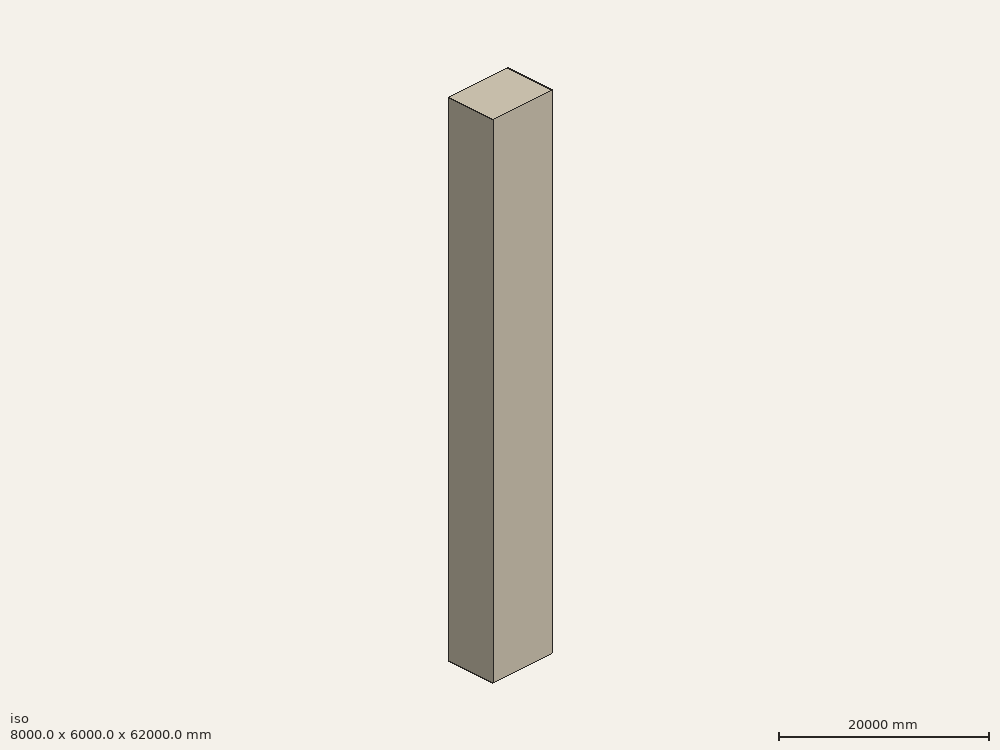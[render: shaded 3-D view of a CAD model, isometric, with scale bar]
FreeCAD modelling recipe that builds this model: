
FCSTD DOCUMENT  (FreeCAD 0.19R24276 (Git))
Label: Tower_Plant
License: All rights reserved
LicenseURL: http://en.wikipedia.org/wiki/All_rights_reserved
objects: Part::Line×1566, Part::Feature×523, Part::Plane×1, Part::Box×1
note: 2091 computed .brp shape members not serialized (recipe doc carries the construction recipe); baked Part::Feature solids carry a one-line shape summary decoded from their .brp

FEATURE [Part::Feature] Heliostat_1  label="Heliostat_1(Mirror,Axis_1_1,Axis_2_1,Normal_1,Target_point)"
  Placement = pos=(-239680,-638881,4.06356e-10) rot=(0,0,1;0rad)
  shape: bbox 10000 x 21.41 x 10000 mm, 1 faces, 0 solids (baked)
FEATURE [Part::Line] Normal_1
  AttacherType = Attacher::AttachEngine3D
  X1 = -239680
  X2 = -239680
  Y1 = 528703
  Y2 = 527703
  Z1 = 0
  Z2 = 0
FEATURE [Part::Line] Axis_1_1
  AttacherType = Attacher::AttachEngine3D
  X1 = -239680
  X2 = -239680
  Y1 = 528703
  Y2 = 528703
  Z1 = 0
  Z2 = -1000
FEATURE [Part::Line] Axis_2_1
  AttacherType = Attacher::AttachEngine3D
  X1 = -239680
  X2 = -240680
  Y1 = 528703
  Y2 = 528703
  Z1 = 0
  Z2 = 0
FEATURE [Part::Feature] Heliostat_2  label="Heliostat_2(Mirror,Axis_1_2,Axis_2_2,Normal_2,Target_point)"
  Placement = pos=(281709,-660028,4.06356e-10) rot=(0,0,1;0rad)
  shape: bbox 10000 x 21.41 x 10000 mm, 1 faces, 0 solids (baked)
FEATURE [Part::Line] Normal_2
  AttacherType = Attacher::AttachEngine3D
  X1 = 281709
  X2 = 281709
  Y1 = 507557
  Y2 = 506557
  Z1 = 0
  Z2 = 0
FEATURE [Part::Line] Axis_1_2
  AttacherType = Attacher::AttachEngine3D
  X1 = 281709
  X2 = 281709
  Y1 = 507557
  Y2 = 507557
  Z1 = 0
  Z2 = -1000
FEATURE [Part::Line] Axis_2_2
  AttacherType = Attacher::AttachEngine3D
  X1 = 281709
  X2 = 280709
  Y1 = 507557
  Y2 = 507557
  Z1 = 0
  Z2 = 0
FEATURE [Part::Feature] Heliostat_3  label="Heliostat_3(Mirror,Axis_1_3,Axis_2_3,Normal_3,Target_point)"
  Placement = pos=(-281709,-660028,4.06356e-10) rot=(0,0,1;0rad)
  shape: bbox 10000 x 21.41 x 10000 mm, 1 faces, 0 solids (baked)
FEATURE [Part::Line] Normal_3
  AttacherType = Attacher::AttachEngine3D
  X1 = -281709
  X2 = -281709
  Y1 = 507557
  Y2 = 506557
  Z1 = 0
  Z2 = 0
FEATURE [Part::Line] Axis_1_3
  AttacherType = Attacher::AttachEngine3D
  X1 = -281709
  X2 = -281709
  Y1 = 507557
  Y2 = 507557
  Z1 = 0
  Z2 = -1000
FEATURE [Part::Line] Axis_2_3
  AttacherType = Attacher::AttachEngine3D
  X1 = -281709
  X2 = -282709
  Y1 = 507557
  Y2 = 507557
  Z1 = 0
  Z2 = 0
FEATURE [Part::Feature] Heliostat_4  label="Heliostat_4(Mirror,Axis_1_4,Axis_2_4,Normal_4,Target_point)"
  Placement = pos=(324319,-653058,2.9829e-10) rot=(0,0,1;0rad)
  shape: bbox 10000 x 23.13 x 10000 mm, 1 faces, 0 solids (baked)
FEATURE [Part::Line] Normal_4
  AttacherType = Attacher::AttachEngine3D
  X1 = 324319
  X2 = 324319
  Y1 = 427889
  Y2 = 426889
  Z1 = 0
  Z2 = 0
FEATURE [Part::Line] Axis_1_4
  AttacherType = Attacher::AttachEngine3D
  X1 = 324319
  X2 = 324319
  Y1 = 427889
  Y2 = 427889
  Z1 = 0
  Z2 = -1000
FEATURE [Part::Line] Axis_2_4
  AttacherType = Attacher::AttachEngine3D
  X1 = 324319
  X2 = 323319
  Y1 = 427889
  Y2 = 427889
  Z1 = 0
  Z2 = 0
FEATURE [Part::Feature] Heliostat_5  label="Heliostat_5(Mirror,Axis_1_5,Axis_2_5,Normal_5,Target_point)"
  Placement = pos=(-324319,-653058,2.9829e-10) rot=(0,0,1;0rad)
  shape: bbox 10000 x 23.13 x 10000 mm, 1 faces, 0 solids (baked)
FEATURE [Part::Line] Normal_5
  AttacherType = Attacher::AttachEngine3D
  X1 = -324319
  X2 = -324319
  Y1 = 427889
  Y2 = 426889
  Z1 = 0
  Z2 = 0
FEATURE [Part::Line] Axis_1_5
  AttacherType = Attacher::AttachEngine3D
  X1 = -324319
  X2 = -324319
  Y1 = 427889
  Y2 = 427889
  Z1 = 0
  Z2 = -1000
FEATURE [Part::Line] Axis_2_5
  AttacherType = Attacher::AttachEngine3D
  X1 = -324319
  X2 = -325319
  Y1 = 427889
  Y2 = 427889
  Z1 = 0
  Z2 = 0
FEATURE [Part::Feature] Heliostat_6  label="Heliostat_6(Mirror,Axis_1_6,Axis_2_6,Normal_6,Target_point)"
  Placement = pos=(328411,-579165,4.3478e-11) rot=(0,0,1;0rad)
  shape: bbox 10000 x 31.86 x 10000 mm, 1 faces, 0 solids (baked)
FEATURE [Part::Line] Normal_6
  AttacherType = Attacher::AttachEngine3D
  X1 = 328411
  X2 = 328411
  Y1 = 205551
  Y2 = 204551
  Z1 = 0
  Z2 = 0
FEATURE [Part::Line] Axis_1_6
  AttacherType = Attacher::AttachEngine3D
  X1 = 328411
  X2 = 328411
  Y1 = 205551
  Y2 = 205551
  Z1 = 0
  Z2 = -1000
FEATURE [Part::Line] Axis_2_6
  AttacherType = Attacher::AttachEngine3D
  X1 = 328411
  X2 = 327411
  Y1 = 205551
  Y2 = 205551
  Z1 = 0
  Z2 = 0
FEATURE [Part::Feature] Heliostat_7  label="Heliostat_7(Mirror,Axis_1_7,Axis_2_7,Normal_7,Target_point)"
  Placement = pos=(-328411,-579165,4.3478e-11) rot=(0,0,1;0rad)
  shape: bbox 10000 x 31.86 x 10000 mm, 1 faces, 0 solids (baked)
FEATURE [Part::Line] Normal_7
  AttacherType = Attacher::AttachEngine3D
  X1 = -328411
  X2 = -328411
  Y1 = 205551
  Y2 = 204551
  Z1 = 0
  Z2 = 0
FEATURE [Part::Line] Axis_1_7
  AttacherType = Attacher::AttachEngine3D
  X1 = -328411
  X2 = -328411
  Y1 = 205551
  Y2 = 205551
  Z1 = 0
  Z2 = -1000
FEATURE [Part::Line] Axis_2_7
  AttacherType = Attacher::AttachEngine3D
  X1 = -328411
  X2 = -329411
  Y1 = 205551
  Y2 = 205551
  Z1 = 0
  Z2 = 0
FEATURE [Part::Feature] Heliostat_8  label="Heliostat_8(Mirror,Axis_1_8,Axis_2_8,Normal_8,Target_point)"
  Placement = pos=(180161,-344791,1.40591e-10) rot=(0,0,1;0rad)
  shape: bbox 10000 x 47.5 x 10000 mm, 1 faces, 0 solids (baked)
FEATURE [Part::Line] Normal_8
  AttacherType = Attacher::AttachEngine3D
  X1 = 180161
  X2 = 180161
  Y1 = 181556
  Y2 = 180556
  Z1 = 0
  Z2 = 0
FEATURE [Part::Line] Axis_1_8
  AttacherType = Attacher::AttachEngine3D
  X1 = 180161
  X2 = 180161
  Y1 = 181556
  Y2 = 181556
  Z1 = 0
  Z2 = -1000
FEATURE [Part::Line] Axis_2_8
  AttacherType = Attacher::AttachEngine3D
  X1 = 180161
  X2 = 179161
  Y1 = 181556
  Y2 = 181556
  Z1 = 0
  Z2 = 0
FEATURE [Part::Feature] Heliostat_9  label="Heliostat_9(Mirror,Axis_1_9,Axis_2_9,Normal_9,Target_point)"
  Placement = pos=(-180161,-344791,1.40591e-10) rot=(0,0,1;0rad)
  shape: bbox 10000 x 47.5 x 10000 mm, 1 faces, 0 solids (baked)
FEATURE [Part::Line] Normal_9
  AttacherType = Attacher::AttachEngine3D
  X1 = -180161
  X2 = -180161
  Y1 = 181556
  Y2 = 180556
  Z1 = 0
  Z2 = 0
FEATURE [Part::Line] Axis_1_9
  AttacherType = Attacher::AttachEngine3D
  X1 = -180161
  X2 = -180161
  Y1 = 181556
  Y2 = 181556
  Z1 = 0
  Z2 = -1000
FEATURE [Part::Line] Axis_2_9
  AttacherType = Attacher::AttachEngine3D
  X1 = -180161
  X2 = -181161
  Y1 = 181556
  Y2 = 181556
  Z1 = 0
  Z2 = 0
FEATURE [Part::Feature] Heliostat_10  label="Heliostat_10(Mirror,Axis_1_10,Axis_2_10,Normal_10,Target_point)"
  Placement = pos=(335249,-595803,2.1959e-10) rot=(0,0,1;0rad)
  shape: bbox 10000 x 29.51 x 10000 mm, 1 faces, 0 solids (baked)
FEATURE [Part::Line] Normal_10
  AttacherType = Attacher::AttachEngine3D
  X1 = 335249
  X2 = 335249
  Y1 = 251457
  Y2 = 250457
  Z1 = 0
  Z2 = 0
FEATURE [Part::Line] Axis_1_10
  AttacherType = Attacher::AttachEngine3D
  X1 = 335249
  X2 = 335249
  Y1 = 251457
  Y2 = 251457
  Z1 = 0
  Z2 = -1000
FEATURE [Part::Line] Axis_2_10
  AttacherType = Attacher::AttachEngine3D
  X1 = 335249
  X2 = 334249
  Y1 = 251457
  Y2 = 251457
  Z1 = 0
  Z2 = 0
FEATURE [Part::Feature] Heliostat_11  label="Heliostat_11(Mirror,Axis_1_11,Axis_2_11,Normal_11,Target_point)"
  Placement = pos=(-335249,-595803,2.1959e-10) rot=(0,0,1;0rad)
  shape: bbox 10000 x 29.51 x 10000 mm, 1 faces, 0 solids (baked)
FEATURE [Part::Line] Normal_11
  AttacherType = Attacher::AttachEngine3D
  X1 = -335249
  X2 = -335249
  Y1 = 251457
  Y2 = 250457
  Z1 = 0
  Z2 = 0
FEATURE [Part::Line] Axis_1_11
  AttacherType = Attacher::AttachEngine3D
  X1 = -335249
  X2 = -335249
  Y1 = 251457
  Y2 = 251457
  Z1 = 0
  Z2 = -1000
FEATURE [Part::Line] Axis_2_11
  AttacherType = Attacher::AttachEngine3D
  X1 = -335249
  X2 = -336249
  Y1 = 251457
  Y2 = 251457
  Z1 = 0
  Z2 = 0
FEATURE [Part::Feature] Heliostat_12  label="Heliostat_12(Mirror,Axis_1_12,Axis_2_12,Normal_12,Target_point)"
  Placement = pos=(-340605,-617288,8.39512e-11) rot=(0,0,1;0rad)
  shape: bbox 10000 x 27.15 x 10000 mm, 1 faces, 0 solids (baked)
FEATURE [Part::Line] Normal_12
  AttacherType = Attacher::AttachEngine3D
  X1 = -340605
  X2 = -340605
  Y1 = 303489
  Y2 = 302489
  Z1 = 0
  Z2 = 0
FEATURE [Part::Line] Axis_1_12
  AttacherType = Attacher::AttachEngine3D
  X1 = -340605
  X2 = -340605
  Y1 = 303489
  Y2 = 303489
  Z1 = 0
  Z2 = -1000
FEATURE [Part::Line] Axis_2_12
  AttacherType = Attacher::AttachEngine3D
  X1 = -340605
  X2 = -341605
  Y1 = 303489
  Y2 = 303489
  Z1 = 0
  Z2 = 0
FEATURE [Part::Feature] Heliostat_13  label="Heliostat_13(Mirror,Axis_1_13,Axis_2_13,Normal_13,Target_point)"
  Placement = pos=(340605,-617288,8.39512e-11) rot=(0,0,1;0rad)
  shape: bbox 10000 x 27.15 x 10000 mm, 1 faces, 0 solids (baked)
FEATURE [Part::Line] Normal_13
  AttacherType = Attacher::AttachEngine3D
  X1 = 340605
  X2 = 340605
  Y1 = 303489
  Y2 = 302489
  Z1 = 0
  Z2 = 0
FEATURE [Part::Line] Axis_1_13
  AttacherType = Attacher::AttachEngine3D
  X1 = 340605
  X2 = 340605
  Y1 = 303489
  Y2 = 303489
  Z1 = 0
  Z2 = -1000
FEATURE [Part::Line] Axis_2_13
  AttacherType = Attacher::AttachEngine3D
  X1 = 340605
  X2 = 339605
  Y1 = 303489
  Y2 = 303489
  Z1 = 0
  Z2 = 0
FEATURE [Part::Feature] Heliostat_14  label="Heliostat_14(Mirror,Axis_1_14,Axis_2_14,Normal_14,Target_point)"
  Placement = pos=(288602,-628199,2.94608e-10) rot=(0,0,1;0rad)
  shape: bbox 10000 x 23.13 x 10000 mm, 1 faces, 0 solids (baked)
FEATURE [Part::Line] Normal_14
  AttacherType = Attacher::AttachEngine3D
  X1 = 288602
  X2 = 288602
  Y1 = 452748
  Y2 = 451748
  Z1 = 0
  Z2 = 0
FEATURE [Part::Line] Axis_1_14
  AttacherType = Attacher::AttachEngine3D
  X1 = 288602
  X2 = 288602
  Y1 = 452748
  Y2 = 452748
  Z1 = 0
  Z2 = -1000
FEATURE [Part::Line] Axis_2_14
  AttacherType = Attacher::AttachEngine3D
  X1 = 288602
  X2 = 287602
  Y1 = 452748
  Y2 = 452748
  Z1 = 0
  Z2 = 0
FEATURE [Part::Feature] Heliostat_15  label="Heliostat_15(Mirror,Axis_1_15,Axis_2_15,Normal_15,Target_point)"
  Placement = pos=(-288602,-628199,2.94608e-10) rot=(0,0,1;0rad)
  shape: bbox 10000 x 23.13 x 10000 mm, 1 faces, 0 solids (baked)
FEATURE [Part::Line] Normal_15
  AttacherType = Attacher::AttachEngine3D
  X1 = -288602
  X2 = -288602
  Y1 = 452748
  Y2 = 451748
  Z1 = 0
  Z2 = 0
FEATURE [Part::Line] Axis_1_15
  AttacherType = Attacher::AttachEngine3D
  X1 = -288602
  X2 = -288602
  Y1 = 452748
  Y2 = 452748
  Z1 = 0
  Z2 = -1000
FEATURE [Part::Line] Axis_2_15
  AttacherType = Attacher::AttachEngine3D
  X1 = -288602
  X2 = -289602
  Y1 = 452748
  Y2 = 452748
  Z1 = 0
  Z2 = 0
FEATURE [Part::Feature] Heliostat_16  label="Heliostat_16(Mirror,Axis_1_16,Axis_2_16,Normal_16,Target_point)"
  Placement = pos=(306713,-640267,1.85804e-10) rot=(0,0,1;0rad)
  shape: bbox 10000 x 23.13 x 10000 mm, 1 faces, 0 solids (baked)
FEATURE [Part::Line] Normal_16
  AttacherType = Attacher::AttachEngine3D
  X1 = 306713
  X2 = 306713
  Y1 = 440680
  Y2 = 439680
  Z1 = 0
  Z2 = 0
FEATURE [Part::Line] Axis_1_16
  AttacherType = Attacher::AttachEngine3D
  X1 = 306713
  X2 = 306713
  Y1 = 440680
  Y2 = 440680
  Z1 = 0
  Z2 = -1000
FEATURE [Part::Line] Axis_2_16
  AttacherType = Attacher::AttachEngine3D
  X1 = 306713
  X2 = 305713
  Y1 = 440680
  Y2 = 440680
  Z1 = 0
  Z2 = 0
FEATURE [Part::Feature] Heliostat_17  label="Heliostat_17(Mirror,Axis_1_17,Axis_2_17,Normal_17,Target_point)"
  Placement = pos=(-306713,-640267,1.85804e-10) rot=(0,0,1;0rad)
  shape: bbox 10000 x 23.13 x 10000 mm, 1 faces, 0 solids (baked)
FEATURE [Part::Line] Normal_17
  AttacherType = Attacher::AttachEngine3D
  X1 = -306713
  X2 = -306713
  Y1 = 440680
  Y2 = 439680
  Z1 = 0
  Z2 = 0
FEATURE [Part::Line] Axis_1_17
  AttacherType = Attacher::AttachEngine3D
  X1 = -306713
  X2 = -306713
  Y1 = 440680
  Y2 = 440680
  Z1 = 0
  Z2 = -1000
FEATURE [Part::Line] Axis_2_17
  AttacherType = Attacher::AttachEngine3D
  X1 = -306713
  X2 = -307713
  Y1 = 440680
  Y2 = 440680
  Z1 = 0
  Z2 = 0
FEATURE [Part::Feature] Heliostat_18  label="Heliostat_18(Mirror,Axis_1_18,Axis_2_18,Normal_18,Target_point)"
  Placement = pos=(321332,-620083,1.82429e-10) rot=(0,0,1;0rad)
  shape: bbox 10000 x 25.14 x 10000 mm, 1 faces, 0 solids (baked)
FEATURE [Part::Line] Normal_18
  AttacherType = Attacher::AttachEngine3D
  X1 = 321332
  X2 = 321332
  Y1 = 374320
  Y2 = 373320
  Z1 = 0
  Z2 = 0
FEATURE [Part::Line] Axis_1_18
  AttacherType = Attacher::AttachEngine3D
  X1 = 321332
  X2 = 321332
  Y1 = 374320
  Y2 = 374320
  Z1 = 0
  Z2 = -1000
FEATURE [Part::Line] Axis_2_18
  AttacherType = Attacher::AttachEngine3D
  X1 = 321332
  X2 = 320332
  Y1 = 374320
  Y2 = 374320
  Z1 = 0
  Z2 = 0
FEATURE [Part::Feature] Heliostat_19  label="Heliostat_19(Mirror,Axis_1_19,Axis_2_19,Normal_19,Target_point)"
  Placement = pos=(-321332,-620083,1.82429e-10) rot=(0,0,1;0rad)
  shape: bbox 10000 x 25.14 x 10000 mm, 1 faces, 0 solids (baked)
FEATURE [Part::Line] Normal_19
  AttacherType = Attacher::AttachEngine3D
  X1 = -321332
  X2 = -321332
  Y1 = 374320
  Y2 = 373320
  Z1 = 0
  Z2 = 0
FEATURE [Part::Line] Axis_1_19
  AttacherType = Attacher::AttachEngine3D
  X1 = -321332
  X2 = -321332
  Y1 = 374320
  Y2 = 374320
  Z1 = 0
  Z2 = -1000
FEATURE [Part::Line] Axis_2_19
  AttacherType = Attacher::AttachEngine3D
  X1 = -321332
  X2 = -322332
  Y1 = 374320
  Y2 = 374320
  Z1 = 0
  Z2 = 0
FEATURE [Part::Feature] Heliostat_20  label="Heliostat_20(Mirror,Axis_1_20,Axis_2_20,Normal_20,Target_point)"
  Placement = pos=(59685.6,-162676,1.04186e-11) rot=(0,0,1;0rad)
  shape: bbox 10000 x 144.2 x 10000 mm, 1 faces, 0 solids (baked)
FEATURE [Part::Line] Normal_20
  AttacherType = Attacher::AttachEngine3D
  X1 = 59685.6
  X2 = 59685.6
  Y1 = 10728.3
  Y2 = 9728.32
  Z1 = 0
  Z2 = 0
FEATURE [Part::Line] Axis_1_20
  AttacherType = Attacher::AttachEngine3D
  X1 = 59685.6
  X2 = 59685.6
  Y1 = 10728.3
  Y2 = 10728.3
  Z1 = 0
  Z2 = -1000
FEATURE [Part::Line] Axis_2_20
  AttacherType = Attacher::AttachEngine3D
  X1 = 59685.6
  X2 = 58685.6
  Y1 = 10728.3
  Y2 = 10728.3
  Z1 = 0
  Z2 = 0
FEATURE [Part::Feature] Heliostat_21  label="Heliostat_21(Mirror,Axis_1_21,Axis_2_21,Normal_21,Target_point)"
  Placement = pos=(-59685.6,-162676,1.04186e-11) rot=(0,0,1;0rad)
  shape: bbox 10000 x 144.2 x 10000 mm, 1 faces, 0 solids (baked)
FEATURE [Part::Line] Normal_21
  AttacherType = Attacher::AttachEngine3D
  X1 = -59685.6
  X2 = -59685.6
  Y1 = 10728.3
  Y2 = 9728.32
  Z1 = 0
  Z2 = 0
FEATURE [Part::Line] Axis_1_21
  AttacherType = Attacher::AttachEngine3D
  X1 = -59685.6
  X2 = -59685.6
  Y1 = 10728.3
  Y2 = 10728.3
  Z1 = 0
  Z2 = -1000
FEATURE [Part::Line] Axis_2_21
  AttacherType = Attacher::AttachEngine3D
  X1 = -59685.6
  X2 = -60685.6
  Y1 = 10728.3
  Y2 = 10728.3
  Z1 = 0
  Z2 = 0
FEATURE [Part::Feature] Heliostat_22  label="Heliostat_22(Mirror,Axis_1_22,Axis_2_22,Normal_22,Target_point)"
  Placement = pos=(220290,-403255,4.94649e-11) rot=(0,0,1;0rad)
  shape: bbox 10000 x 51.21 x 10000 mm, 1 faces, 0 solids (baked)
FEATURE [Part::Line] Normal_22
  AttacherType = Attacher::AttachEngine3D
  X1 = 220290
  X2 = 220290
  Y1 = 84926.1
  Y2 = 83926.1
  Z1 = 0
  Z2 = 0
FEATURE [Part::Line] Axis_1_22
  AttacherType = Attacher::AttachEngine3D
  X1 = 220290
  X2 = 220290
  Y1 = 84926.1
  Y2 = 84926.1
  Z1 = 0
  Z2 = -1000
FEATURE [Part::Line] Axis_2_22
  AttacherType = Attacher::AttachEngine3D
  X1 = 220290
  X2 = 219290
  Y1 = 84926.1
  Y2 = 84926.1
  Z1 = 0
  Z2 = 0
FEATURE [Part::Feature] Heliostat_23  label="Heliostat_23(Mirror,Axis_1_23,Axis_2_23,Normal_23,Target_point)"
  Placement = pos=(-220290,-403255,4.94649e-11) rot=(0,0,1;0rad)
  shape: bbox 10000 x 51.21 x 10000 mm, 1 faces, 0 solids (baked)
FEATURE [Part::Line] Normal_23
  AttacherType = Attacher::AttachEngine3D
  X1 = -220290
  X2 = -220290
  Y1 = 84926.1
  Y2 = 83926.1
  Z1 = 0
  Z2 = 0
FEATURE [Part::Line] Axis_1_23
  AttacherType = Attacher::AttachEngine3D
  X1 = -220290
  X2 = -220290
  Y1 = 84926.1
  Y2 = 84926.1
  Z1 = 0
  Z2 = -1000
FEATURE [Part::Line] Axis_2_23
  AttacherType = Attacher::AttachEngine3D
  X1 = -220290
  X2 = -221290
  Y1 = 84926.1
  Y2 = 84926.1
  Z1 = 0
  Z2 = 0
FEATURE [Part::Feature] Heliostat_24  label="Heliostat_24(Mirror,Axis_1_24,Axis_2_24,Normal_24,Target_point)"
  Placement = pos=(244770,-464081,1.33122e-10) rot=(0,0,1;0rad)
  shape: bbox 10000 x 34.61 x 10000 mm, 1 faces, 0 solids (baked)
FEATURE [Part::Line] Normal_24
  AttacherType = Attacher::AttachEngine3D
  X1 = 244770
  X2 = 244770
  Y1 = 258220
  Y2 = 257220
  Z1 = 0
  Z2 = 0
FEATURE [Part::Line] Axis_1_24
  AttacherType = Attacher::AttachEngine3D
  X1 = 244770
  X2 = 244770
  Y1 = 258220
  Y2 = 258220
  Z1 = 0
  Z2 = -1000
FEATURE [Part::Line] Axis_2_24
  AttacherType = Attacher::AttachEngine3D
  X1 = 244770
  X2 = 243770
  Y1 = 258220
  Y2 = 258220
  Z1 = 0
  Z2 = 0
FEATURE [Part::Feature] Heliostat_25  label="Heliostat_25(Mirror,Axis_1_25,Axis_2_25,Normal_25,Target_point)"
  Placement = pos=(-244770,-464081,1.33122e-10) rot=(0,0,1;0rad)
  shape: bbox 10000 x 34.61 x 10000 mm, 1 faces, 0 solids (baked)
FEATURE [Part::Line] Normal_25
  AttacherType = Attacher::AttachEngine3D
  X1 = -244770
  X2 = -244770
  Y1 = 258220
  Y2 = 257220
  Z1 = 0
  Z2 = 0
FEATURE [Part::Line] Axis_1_25
  AttacherType = Attacher::AttachEngine3D
  X1 = -244770
  X2 = -244770
  Y1 = 258220
  Y2 = 258220
  Z1 = 0
  Z2 = -1000
FEATURE [Part::Line] Axis_2_25
  AttacherType = Attacher::AttachEngine3D
  X1 = -244770
  X2 = -245770
  Y1 = 258220
  Y2 = 258220
  Z1 = 0
  Z2 = 0
FEATURE [Part::Feature] Heliostat_26  label="Heliostat_26(Mirror,Axis_1_26,Axis_2_26,Normal_26,Target_point)"
  Placement = pos=(89489.5,-509262,2.66794e-10) rot=(0,0,1;0rad)
  shape: bbox 10000 x 25.14 x 10000 mm, 1 faces, 0 solids (baked)
FEATURE [Part::Line] Normal_26
  AttacherType = Attacher::AttachEngine3D
  X1 = 89489.5
  X2 = 89489.5
  Y1 = 485140
  Y2 = 484140
  Z1 = 0
  Z2 = 0
FEATURE [Part::Line] Axis_1_26
  AttacherType = Attacher::AttachEngine3D
  X1 = 89489.5
  X2 = 89489.5
  Y1 = 485140
  Y2 = 485140
  Z1 = 0
  Z2 = -1000
FEATURE [Part::Line] Axis_2_26
  AttacherType = Attacher::AttachEngine3D
  X1 = 89489.5
  X2 = 88489.5
  Y1 = 485140
  Y2 = 485140
  Z1 = 0
  Z2 = 0
FEATURE [Part::Feature] Heliostat_27  label="Heliostat_27(Mirror,Axis_1_27,Axis_2_27,Normal_27,Target_point)"
  Placement = pos=(-89489.5,-509262,2.66794e-10) rot=(0,0,1;0rad)
  shape: bbox 10000 x 25.14 x 10000 mm, 1 faces, 0 solids (baked)
FEATURE [Part::Line] Normal_27
  AttacherType = Attacher::AttachEngine3D
  X1 = -89489.5
  X2 = -89489.5
  Y1 = 485140
  Y2 = 484140
  Z1 = 0
  Z2 = 0
FEATURE [Part::Line] Axis_1_27
  AttacherType = Attacher::AttachEngine3D
  X1 = -89489.5
  X2 = -89489.5
  Y1 = 485140
  Y2 = 485140
  Z1 = 0
  Z2 = -1000
FEATURE [Part::Line] Axis_2_27
  AttacherType = Attacher::AttachEngine3D
  X1 = -89489.5
  X2 = -90489.5
  Y1 = 485140
  Y2 = 485140
  Z1 = 0
  Z2 = 0
FEATURE [Part::Feature] Heliostat_28  label="Heliostat_28(Mirror,Axis_1_28,Axis_2_28,Normal_28,Target_point)"
  Placement = pos=(110708,-230569,4.70102e-11) rot=(0,0,1;0rad)
  shape: bbox 10000 x 95.83 x 10000 mm, 1 faces, 0 solids (baked)
FEATURE [Part::Line] Normal_28
  AttacherType = Attacher::AttachEngine3D
  X1 = 110708
  X2 = 110708
  Y1 = 30316.5
  Y2 = 29316.5
  Z1 = 0
  Z2 = 0
FEATURE [Part::Line] Axis_1_28
  AttacherType = Attacher::AttachEngine3D
  X1 = 110708
  X2 = 110708
  Y1 = 30316.5
  Y2 = 30316.5
  Z1 = 0
  Z2 = -1000
FEATURE [Part::Line] Axis_2_28
  AttacherType = Attacher::AttachEngine3D
  X1 = 110708
  X2 = 109708
  Y1 = 30316.5
  Y2 = 30316.5
  Z1 = 0
  Z2 = 0
FEATURE [Part::Feature] Heliostat_29  label="Heliostat_29(Mirror,Axis_1_29,Axis_2_29,Normal_29,Target_point)"
  Placement = pos=(-110708,-230569,4.70102e-11) rot=(0,0,1;0rad)
  shape: bbox 10000 x 95.83 x 10000 mm, 1 faces, 0 solids (baked)
FEATURE [Part::Line] Normal_29
  AttacherType = Attacher::AttachEngine3D
  X1 = -110708
  X2 = -110708
  Y1 = 30316.5
  Y2 = 29316.5
  Z1 = 0
  Z2 = 0
FEATURE [Part::Line] Axis_1_29
  AttacherType = Attacher::AttachEngine3D
  X1 = -110708
  X2 = -110708
  Y1 = 30316.5
  Y2 = 30316.5
  Z1 = 0
  Z2 = -1000
FEATURE [Part::Line] Axis_2_29
  AttacherType = Attacher::AttachEngine3D
  X1 = -110708
  X2 = -111708
  Y1 = 30316.5
  Y2 = 30316.5
  Z1 = 0
  Z2 = 0
FEATURE [Part::Feature] Heliostat_30  label="Heliostat_30(Mirror,Axis_1_30,Axis_2_30,Normal_30,Target_point)"
  Placement = pos=(59421.5,-277571,9.8826e-11) rot=(0,0,1;0rad)
  shape: bbox 10000 x 47.5 x 10000 mm, 1 faces, 0 solids (baked)
FEATURE [Part::Line] Normal_30
  AttacherType = Attacher::AttachEngine3D
  X1 = 59421.5
  X2 = 59421.5
  Y1 = 248776
  Y2 = 247776
  Z1 = 0
  Z2 = 0
FEATURE [Part::Line] Axis_1_30
  AttacherType = Attacher::AttachEngine3D
  X1 = 59421.5
  X2 = 59421.5
  Y1 = 248776
  Y2 = 248776
  Z1 = 0
  Z2 = -1000
FEATURE [Part::Line] Axis_2_30
  AttacherType = Attacher::AttachEngine3D
  X1 = 59421.5
  X2 = 58421.5
  Y1 = 248776
  Y2 = 248776
  Z1 = 0
  Z2 = 0
FEATURE [Part::Feature] Heliostat_31  label="Heliostat_31(Mirror,Axis_1_31,Axis_2_31,Normal_31,Target_point)"
  Placement = pos=(-59421.5,-277571,9.8826e-11) rot=(0,0,1;0rad)
  shape: bbox 10000 x 47.5 x 10000 mm, 1 faces, 0 solids (baked)
FEATURE [Part::Line] Normal_31
  AttacherType = Attacher::AttachEngine3D
  X1 = -59421.5
  X2 = -59421.5
  Y1 = 248776
  Y2 = 247776
  Z1 = 0
  Z2 = 0
FEATURE [Part::Line] Axis_1_31
  AttacherType = Attacher::AttachEngine3D
  X1 = -59421.5
  X2 = -59421.5
  Y1 = 248776
  Y2 = 248776
  Z1 = 0
  Z2 = -1000
FEATURE [Part::Line] Axis_2_31
  AttacherType = Attacher::AttachEngine3D
  X1 = -59421.5
  X2 = -60421.5
  Y1 = 248776
  Y2 = 248776
  Z1 = 0
  Z2 = 0
FEATURE [Part::Feature] Heliostat_32  label="Heliostat_32(Mirror,Axis_1_32,Axis_2_32,Normal_32,Target_point)"
  Placement = pos=(218058,-629603,1.65478e-10) rot=(0,0,1;0rad)
  shape: bbox 10000 x 21.41 x 10000 mm, 1 faces, 0 solids (baked)
FEATURE [Part::Line] Normal_32
  AttacherType = Attacher::AttachEngine3D
  X1 = 218058
  X2 = 218058
  Y1 = 537982
  Y2 = 536982
  Z1 = 0
  Z2 = 0
FEATURE [Part::Line] Axis_1_32
  AttacherType = Attacher::AttachEngine3D
  X1 = 218058
  X2 = 218058
  Y1 = 537982
  Y2 = 537982
  Z1 = 0
  Z2 = -1000
FEATURE [Part::Line] Axis_2_32
  AttacherType = Attacher::AttachEngine3D
  X1 = 218058
  X2 = 217058
  Y1 = 537982
  Y2 = 537982
  Z1 = 0
  Z2 = 0
FEATURE [Part::Feature] Heliostat_33  label="Heliostat_33(Mirror,Axis_1_33,Axis_2_33,Normal_33,Target_point)"
  Placement = pos=(-218058,-629603,1.65478e-10) rot=(0,0,1;0rad)
  shape: bbox 10000 x 21.41 x 10000 mm, 1 faces, 0 solids (baked)
FEATURE [Part::Line] Normal_33
  AttacherType = Attacher::AttachEngine3D
  X1 = -218058
  X2 = -218058
  Y1 = 537982
  Y2 = 536982
  Z1 = 0
  Z2 = 0
FEATURE [Part::Line] Axis_1_33
  AttacherType = Attacher::AttachEngine3D
  X1 = -218058
  X2 = -218058
  Y1 = 537982
  Y2 = 537982
  Z1 = 0
  Z2 = -1000
FEATURE [Part::Line] Axis_2_33
  AttacherType = Attacher::AttachEngine3D
  X1 = -218058
  X2 = -219058
  Y1 = 537982
  Y2 = 537982
  Z1 = 0
  Z2 = 0
FEATURE [Part::Feature] Heliostat_34  label="Heliostat_34(Mirror,Axis_1_34,Axis_2_34,Normal_34,Target_point)"
  Placement = pos=(105302,-596721,2.14629e-10) rot=(0,0,1;0rad)
  shape: bbox 10000 x 21.41 x 10000 mm, 1 faces, 0 solids (baked)
FEATURE [Part::Line] Normal_34
  AttacherType = Attacher::AttachEngine3D
  X1 = 105302
  X2 = 105302
  Y1 = 570863
  Y2 = 569863
  Z1 = 0
  Z2 = 0
FEATURE [Part::Line] Axis_1_34
  AttacherType = Attacher::AttachEngine3D
  X1 = 105302
  X2 = 105302
  Y1 = 570863
  Y2 = 570863
  Z1 = 0
  Z2 = -1000
FEATURE [Part::Line] Axis_2_34
  AttacherType = Attacher::AttachEngine3D
  X1 = 105302
  X2 = 104302
  Y1 = 570863
  Y2 = 570863
  Z1 = 0
  Z2 = 0
FEATURE [Part::Feature] Heliostat_35  label="Heliostat_35(Mirror,Axis_1_35,Axis_2_35,Normal_35,Target_point)"
  Placement = pos=(-105302,-596721,2.14629e-10) rot=(0,0,1;0rad)
  shape: bbox 10000 x 21.41 x 10000 mm, 1 faces, 0 solids (baked)
FEATURE [Part::Line] Normal_35
  AttacherType = Attacher::AttachEngine3D
  X1 = -105302
  X2 = -105302
  Y1 = 570863
  Y2 = 569863
  Z1 = 0
  Z2 = 0
FEATURE [Part::Line] Axis_1_35
  AttacherType = Attacher::AttachEngine3D
  X1 = -105302
  X2 = -105302
  Y1 = 570863
  Y2 = 570863
  Z1 = 0
  Z2 = -1000
FEATURE [Part::Line] Axis_2_35
  AttacherType = Attacher::AttachEngine3D
  X1 = -105302
  X2 = -106302
  Y1 = 570863
  Y2 = 570863
  Z1 = 0
  Z2 = 0
FEATURE [Part::Feature] Heliostat_36  label="Heliostat_36(Mirror,Axis_1_36,Axis_2_36,Normal_36,Target_point)"
  Placement = pos=(127095,-389981,1.97655e-10) rot=(0,0,1;0rad)
  shape: bbox 10000 x 34.61 x 10000 mm, 1 faces, 0 solids (baked)
FEATURE [Part::Line] Normal_36
  AttacherType = Attacher::AttachEngine3D
  X1 = 127095
  X2 = 127095
  Y1 = 332320
  Y2 = 331320
  Z1 = 0
  Z2 = 0
FEATURE [Part::Line] Axis_1_36
  AttacherType = Attacher::AttachEngine3D
  X1 = 127095
  X2 = 127095
  Y1 = 332320
  Y2 = 332320
  Z1 = 0
  Z2 = -1000
FEATURE [Part::Line] Axis_2_36
  AttacherType = Attacher::AttachEngine3D
  X1 = 127095
  X2 = 126095
  Y1 = 332320
  Y2 = 332320
  Z1 = 0
  Z2 = 0
FEATURE [Part::Feature] Heliostat_37  label="Heliostat_37(Mirror,Axis_1_37,Axis_2_37,Normal_37,Target_point)"
  Placement = pos=(-127095,-389981,1.97655e-10) rot=(0,0,1;0rad)
  shape: bbox 10000 x 34.61 x 10000 mm, 1 faces, 0 solids (baked)
FEATURE [Part::Line] Normal_37
  AttacherType = Attacher::AttachEngine3D
  X1 = -127095
  X2 = -127095
  Y1 = 332320
  Y2 = 331320
  Z1 = 0
  Z2 = 0
FEATURE [Part::Line] Axis_1_37
  AttacherType = Attacher::AttachEngine3D
  X1 = -127095
  X2 = -127095
  Y1 = 332320
  Y2 = 332320
  Z1 = 0
  Z2 = -1000
FEATURE [Part::Line] Axis_2_37
  AttacherType = Attacher::AttachEngine3D
  X1 = -127095
  X2 = -128095
  Y1 = 332320
  Y2 = 332320
  Z1 = 0
  Z2 = 0
FEATURE [Part::Feature] Heliostat_38  label="Heliostat_38(Mirror,Axis_1_38,Axis_2_38,Normal_38,Target_point)"
  Placement = pos=(196077,-621208,1.15201e-10) rot=(0,0,1;0rad)
  shape: bbox 10000 x 21.41 x 10000 mm, 1 faces, 0 solids (baked)
FEATURE [Part::Line] Normal_38
  AttacherType = Attacher::AttachEngine3D
  X1 = 196077
  X2 = 196077
  Y1 = 546376
  Y2 = 545376
  Z1 = 0
  Z2 = 0
FEATURE [Part::Line] Axis_1_38
  AttacherType = Attacher::AttachEngine3D
  X1 = 196077
  X2 = 196077
  Y1 = 546376
  Y2 = 546376
  Z1 = 0
  Z2 = -1000
FEATURE [Part::Line] Axis_2_38
  AttacherType = Attacher::AttachEngine3D
  X1 = 196077
  X2 = 195077
  Y1 = 546376
  Y2 = 546376
  Z1 = 0
  Z2 = 0
FEATURE [Part::Feature] Heliostat_39  label="Heliostat_39(Mirror,Axis_1_39,Axis_2_39,Normal_39,Target_point)"
  Placement = pos=(-196077,-621208,1.15201e-10) rot=(0,0,1;0rad)
  shape: bbox 10000 x 21.41 x 10000 mm, 1 faces, 0 solids (baked)
FEATURE [Part::Line] Normal_39
  AttacherType = Attacher::AttachEngine3D
  X1 = -196077
  X2 = -196077
  Y1 = 546376
  Y2 = 545376
  Z1 = 0
  Z2 = 0
FEATURE [Part::Line] Axis_1_39
  AttacherType = Attacher::AttachEngine3D
  X1 = -196077
  X2 = -196077
  Y1 = 546376
  Y2 = 546376
  Z1 = 0
  Z2 = -1000
FEATURE [Part::Line] Axis_2_39
  AttacherType = Attacher::AttachEngine3D
  X1 = -196077
  X2 = -197077
  Y1 = 546376
  Y2 = 546376
  Z1 = 0
  Z2 = 0
FEATURE [Part::Feature] Heliostat_40  label="Heliostat_40(Mirror,Axis_1_40,Axis_2_40,Normal_40,Target_point)"
  Placement = pos=(82081.6,-592923,4.10454e-10) rot=(0,0,1;0rad)
  shape: bbox 10000 x 21.41 x 10000 mm, 1 faces, 0 solids (baked)
FEATURE [Part::Line] Normal_40
  AttacherType = Attacher::AttachEngine3D
  X1 = 82081.5
  X2 = 82081.5
  Y1 = 574662
  Y2 = 573662
  Z1 = 0
  Z2 = 0
FEATURE [Part::Line] Axis_1_40
  AttacherType = Attacher::AttachEngine3D
  X1 = 82081.5
  X2 = 82081.5
  Y1 = 574662
  Y2 = 574662
  Z1 = 0
  Z2 = -1000
FEATURE [Part::Line] Axis_2_40
  AttacherType = Attacher::AttachEngine3D
  X1 = 82081.5
  X2 = 81081.5
  Y1 = 574662
  Y2 = 574662
  Z1 = 0
  Z2 = 0
FEATURE [Part::Feature] Heliostat_41  label="Heliostat_41(Mirror,Axis_1_41,Axis_2_41,Normal_41,Target_point)"
  Placement = pos=(-82081.5,-592923,4.10454e-10) rot=(0,0,1;0rad)
  shape: bbox 10000 x 21.41 x 10000 mm, 1 faces, 0 solids (baked)
FEATURE [Part::Line] Normal_41
  AttacherType = Attacher::AttachEngine3D
  X1 = -82081.5
  X2 = -82081.5
  Y1 = 574662
  Y2 = 573662
  Z1 = 0
  Z2 = 0
FEATURE [Part::Line] Axis_1_41
  AttacherType = Attacher::AttachEngine3D
  X1 = -82081.5
  X2 = -82081.5
  Y1 = 574662
  Y2 = 574662
  Z1 = 0
  Z2 = -1000
FEATURE [Part::Line] Axis_2_41
  AttacherType = Attacher::AttachEngine3D
  X1 = -82081.5
  X2 = -83081.5
  Y1 = 574662
  Y2 = 574662
  Z1 = 0
  Z2 = 0
FEATURE [Part::Feature] Heliostat_42  label="Heliostat_42(Mirror,Axis_1_42,Axis_2_42,Normal_42,Target_point)"
  Placement = pos=(214264,-438257,1.97655e-10) rot=(0,0,1;0rad)
  shape: bbox 10000 x 34.61 x 10000 mm, 1 faces, 0 solids (baked)
FEATURE [Part::Line] Normal_42
  AttacherType = Attacher::AttachEngine3D
  X1 = 214264
  X2 = 214264
  Y1 = 284044
  Y2 = 283044
  Z1 = 0
  Z2 = 0
FEATURE [Part::Line] Axis_1_42
  AttacherType = Attacher::AttachEngine3D
  X1 = 214264
  X2 = 214264
  Y1 = 284044
  Y2 = 284044
  Z1 = 0
  Z2 = -1000
FEATURE [Part::Line] Axis_2_42
  AttacherType = Attacher::AttachEngine3D
  X1 = 214264
  X2 = 213264
  Y1 = 284044
  Y2 = 284044
  Z1 = 0
  Z2 = 0
FEATURE [Part::Feature] Heliostat_43  label="Heliostat_43(Mirror,Axis_1_43,Axis_2_43,Normal_43,Target_point)"
  Placement = pos=(-214264,-438257,1.97655e-10) rot=(0,0,1;0rad)
  shape: bbox 10000 x 34.61 x 10000 mm, 1 faces, 0 solids (baked)
FEATURE [Part::Line] Normal_43
  AttacherType = Attacher::AttachEngine3D
  X1 = -214264
  X2 = -214264
  Y1 = 284044
  Y2 = 283044
  Z1 = 0
  Z2 = 0
FEATURE [Part::Line] Axis_1_43
  AttacherType = Attacher::AttachEngine3D
  X1 = -214264
  X2 = -214264
  Y1 = 284044
  Y2 = 284044
  Z1 = 0
  Z2 = -1000
FEATURE [Part::Line] Axis_2_43
  AttacherType = Attacher::AttachEngine3D
  X1 = -214264
  X2 = -215264
  Y1 = 284044
  Y2 = 284044
  Z1 = 0
  Z2 = 0
FEATURE [Part::Feature] Heliostat_44  label="Heliostat_44(Mirror,Axis_1_44,Axis_2_44,Normal_44,Target_point)"
  Placement = pos=(58726.2,-590068,4.06356e-10) rot=(0,0,1;0rad)
  shape: bbox 10000 x 21.41 x 10000 mm, 1 faces, 0 solids (baked)
FEATURE [Part::Line] Normal_44
  AttacherType = Attacher::AttachEngine3D
  X1 = 58726.2
  X2 = 58726.2
  Y1 = 577516
  Y2 = 576516
  Z1 = 0
  Z2 = 0
FEATURE [Part::Line] Axis_1_44
  AttacherType = Attacher::AttachEngine3D
  X1 = 58726.2
  X2 = 58726.2
  Y1 = 577516
  Y2 = 577516
  Z1 = 0
  Z2 = -1000
FEATURE [Part::Line] Axis_2_44
  AttacherType = Attacher::AttachEngine3D
  X1 = 58726.2
  X2 = 57726.2
  Y1 = 577516
  Y2 = 577516
  Z1 = 0
  Z2 = 0
FEATURE [Part::Feature] Heliostat_45  label="Heliostat_45(Mirror,Axis_1_45,Axis_2_45,Normal_45,Target_point)"
  Placement = pos=(-58726.2,-590068,4.06356e-10) rot=(0,0,1;0rad)
  shape: bbox 10000 x 21.41 x 10000 mm, 1 faces, 0 solids (baked)
FEATURE [Part::Line] Normal_45
  AttacherType = Attacher::AttachEngine3D
  X1 = -58726.2
  X2 = -58726.2
  Y1 = 577516
  Y2 = 576516
  Z1 = 0
  Z2 = 0
FEATURE [Part::Line] Axis_1_45
  AttacherType = Attacher::AttachEngine3D
  X1 = -58726.2
  X2 = -58726.2
  Y1 = 577516
  Y2 = 577516
  Z1 = 0
  Z2 = -1000
FEATURE [Part::Line] Axis_2_45
  AttacherType = Attacher::AttachEngine3D
  X1 = -58726.2
  X2 = -59726.2
  Y1 = 577516
  Y2 = 577516
  Z1 = 0
  Z2 = 0
FEATURE [Part::Feature] Heliostat_46  label="Heliostat_46(Mirror,Axis_1_46,Axis_2_46,Normal_46,Target_point)"
  Placement = pos=(-35274.4,-588163,5.02412e-10) rot=(0,0,1;0rad)
  shape: bbox 10000 x 21.41 x 10000 mm, 1 faces, 0 solids (baked)
FEATURE [Part::Line] Normal_46
  AttacherType = Attacher::AttachEngine3D
  X1 = -35274.4
  X2 = -35274.4
  Y1 = 579421
  Y2 = 578421
  Z1 = 0
  Z2 = 0
FEATURE [Part::Line] Axis_1_46
  AttacherType = Attacher::AttachEngine3D
  X1 = -35274.4
  X2 = -35274.4
  Y1 = 579421
  Y2 = 579421
  Z1 = 0
  Z2 = -1000
FEATURE [Part::Line] Axis_2_46
  AttacherType = Attacher::AttachEngine3D
  X1 = -35274.4
  X2 = -36274.4
  Y1 = 579421
  Y2 = 579421
  Z1 = 0
  Z2 = 0
FEATURE [Part::Feature] Heliostat_47  label="Heliostat_47(Mirror,Axis_1_47,Axis_2_47,Normal_47,Target_point)"
  Placement = pos=(35274.4,-588163,5.02412e-10) rot=(0,0,1;0rad)
  shape: bbox 10000 x 21.41 x 10000 mm, 1 faces, 0 solids (baked)
FEATURE [Part::Line] Normal_47
  AttacherType = Attacher::AttachEngine3D
  X1 = 35274.4
  X2 = 35274.4
  Y1 = 579421
  Y2 = 578421
  Z1 = 0
  Z2 = 0
FEATURE [Part::Line] Axis_1_47
  AttacherType = Attacher::AttachEngine3D
  X1 = 35274.4
  X2 = 35274.4
  Y1 = 579421
  Y2 = 579421
  Z1 = 0
  Z2 = -1000
FEATURE [Part::Line] Axis_2_47
  AttacherType = Attacher::AttachEngine3D
  X1 = 35274.4
  X2 = 34274.4
  Y1 = 579421
  Y2 = 579421
  Z1 = 0
  Z2 = 0
FEATURE [Part::Feature] Heliostat_48  label="Heliostat_48(Mirror,Axis_1_48,Axis_2_48,Normal_48,Target_point)"
  Placement = pos=(-11764.6,-587209,2.14733e-10) rot=(0,0,1;0rad)
  shape: bbox 10000 x 21.41 x 10000 mm, 1 faces, 0 solids (baked)
FEATURE [Part::Line] Normal_48
  AttacherType = Attacher::AttachEngine3D
  X1 = -11764.6
  X2 = -11764.6
  Y1 = 580375
  Y2 = 579375
  Z1 = 0
  Z2 = 0
FEATURE [Part::Line] Axis_1_48
  AttacherType = Attacher::AttachEngine3D
  X1 = -11764.6
  X2 = -11764.6
  Y1 = 580375
  Y2 = 580375
  Z1 = 0
  Z2 = -1000
FEATURE [Part::Line] Axis_2_48
  AttacherType = Attacher::AttachEngine3D
  X1 = -11764.6
  X2 = -12764.6
  Y1 = 580375
  Y2 = 580375
  Z1 = 0
  Z2 = 0
FEATURE [Part::Feature] Heliostat_49  label="Heliostat_49(Mirror,Axis_1_49,Axis_2_49,Normal_49,Target_point)"
  Placement = pos=(11764.6,-587209,2.14733e-10) rot=(0,0,1;0rad)
  shape: bbox 10000 x 21.41 x 10000 mm, 1 faces, 0 solids (baked)
FEATURE [Part::Line] Normal_49
  AttacherType = Attacher::AttachEngine3D
  X1 = 11764.6
  X2 = 11764.6
  Y1 = 580375
  Y2 = 579375
  Z1 = 0
  Z2 = 0
FEATURE [Part::Line] Axis_1_49
  AttacherType = Attacher::AttachEngine3D
  X1 = 11764.6
  X2 = 11764.6
  Y1 = 580375
  Y2 = 580375
  Z1 = 0
  Z2 = -1000
FEATURE [Part::Line] Axis_2_49
  AttacherType = Attacher::AttachEngine3D
  X1 = 11764.6
  X2 = 10764.6
  Y1 = 580375
  Y2 = 580375
  Z1 = 0
  Z2 = 0
FEATURE [Part::Feature] Heliostat_50  label="Heliostat_50(Mirror,Axis_1_50,Axis_2_50,Normal_50,Target_point)"
  Placement = pos=(173774,-613711,3.12574e-10) rot=(0,0,1;0rad)
  shape: bbox 10000 x 21.41 x 10000 mm, 1 faces, 0 solids (baked)
FEATURE [Part::Line] Normal_50
  AttacherType = Attacher::AttachEngine3D
  X1 = 173774
  X2 = 173774
  Y1 = 553873
  Y2 = 552873
  Z1 = 0
  Z2 = 0
FEATURE [Part::Line] Axis_1_50
  AttacherType = Attacher::AttachEngine3D
  X1 = 173774
  X2 = 173774
  Y1 = 553873
  Y2 = 553873
  Z1 = 0
  Z2 = -1000
FEATURE [Part::Line] Axis_2_50
  AttacherType = Attacher::AttachEngine3D
  X1 = 173774
  X2 = 172774
  Y1 = 553873
  Y2 = 553873
  Z1 = 0
  Z2 = 0
FEATURE [Part::Feature] Heliostat_51  label="Heliostat_51(Mirror,Axis_1_51,Axis_2_51,Normal_51,Target_point)"
  Placement = pos=(-173774,-613711,3.12574e-10) rot=(0,0,1;0rad)
  shape: bbox 10000 x 21.41 x 10000 mm, 1 faces, 0 solids (baked)
FEATURE [Part::Line] Normal_51
  AttacherType = Attacher::AttachEngine3D
  X1 = -173774
  X2 = -173774
  Y1 = 553873
  Y2 = 552873
  Z1 = 0
  Z2 = 0
FEATURE [Part::Line] Axis_1_51
  AttacherType = Attacher::AttachEngine3D
  X1 = -173774
  X2 = -173774
  Y1 = 553873
  Y2 = 553873
  Z1 = 0
  Z2 = -1000
FEATURE [Part::Line] Axis_2_51
  AttacherType = Attacher::AttachEngine3D
  X1 = -173774
  X2 = -174774
  Y1 = 553873
  Y2 = 553873
  Z1 = 0
  Z2 = 0
FEATURE [Part::Feature] Heliostat_52  label="Heliostat_52(Mirror,Axis_1_52,Axis_2_52,Normal_52,Target_point)"
  Placement = pos=(286048,-507046,1.19225e-10) rot=(0,0,1;0rad)
  shape: bbox 10000 x 37.36 x 10000 mm, 1 faces, 0 solids (baked)
FEATURE [Part::Line] Normal_52
  AttacherType = Attacher::AttachEngine3D
  X1 = 286048
  X2 = 286048
  Y1 = 162157
  Y2 = 161157
  Z1 = 0
  Z2 = 0
FEATURE [Part::Line] Axis_1_52
  AttacherType = Attacher::AttachEngine3D
  X1 = 286048
  X2 = 286048
  Y1 = 162157
  Y2 = 162157
  Z1 = 0
  Z2 = -1000
FEATURE [Part::Line] Axis_2_52
  AttacherType = Attacher::AttachEngine3D
  X1 = 286048
  X2 = 285048
  Y1 = 162157
  Y2 = 162157
  Z1 = 0
  Z2 = 0
FEATURE [Part::Feature] Heliostat_53  label="Heliostat_53(Mirror,Axis_1_53,Axis_2_53,Normal_53,Target_point)"
  Placement = pos=(-286048,-507046,1.19225e-10) rot=(0,0,1;0rad)
  shape: bbox 10000 x 37.36 x 10000 mm, 1 faces, 0 solids (baked)
FEATURE [Part::Line] Normal_53
  AttacherType = Attacher::AttachEngine3D
  X1 = -286048
  X2 = -286048
  Y1 = 162157
  Y2 = 161157
  Z1 = 0
  Z2 = 0
FEATURE [Part::Line] Axis_1_53
  AttacherType = Attacher::AttachEngine3D
  X1 = -286048
  X2 = -286048
  Y1 = 162157
  Y2 = 162157
  Z1 = 0
  Z2 = -1000
FEATURE [Part::Line] Axis_2_53
  AttacherType = Attacher::AttachEngine3D
  X1 = -286048
  X2 = -287048
  Y1 = 162157
  Y2 = 162157
  Z1 = 0
  Z2 = 0
FEATURE [Part::Feature] Heliostat_54  label="Heliostat_54(Mirror,Axis_1_54,Axis_2_54,Normal_54,Target_point)"
  Placement = pos=(323021,-598636,1.69358e-10) rot=(0,0,1;0rad)
  shape: bbox 10000 x 27.15 x 10000 mm, 1 faces, 0 solids (baked)
FEATURE [Part::Line] Normal_54
  AttacherType = Attacher::AttachEngine3D
  X1 = 323021
  X2 = 323021
  Y1 = 322141
  Y2 = 321141
  Z1 = 0
  Z2 = 0
FEATURE [Part::Line] Axis_1_54
  AttacherType = Attacher::AttachEngine3D
  X1 = 323021
  X2 = 323021
  Y1 = 322141
  Y2 = 322141
  Z1 = 0
  Z2 = -1000
FEATURE [Part::Line] Axis_2_54
  AttacherType = Attacher::AttachEngine3D
  X1 = 323021
  X2 = 322021
  Y1 = 322141
  Y2 = 322141
  Z1 = 0
  Z2 = 0
FEATURE [Part::Feature] Heliostat_55  label="Heliostat_55(Mirror,Axis_1_55,Axis_2_55,Normal_55,Target_point)"
  Placement = pos=(-323021,-598636,1.69358e-10) rot=(0,0,1;0rad)
  shape: bbox 10000 x 27.15 x 10000 mm, 1 faces, 0 solids (baked)
FEATURE [Part::Line] Normal_55
  AttacherType = Attacher::AttachEngine3D
  X1 = -323021
  X2 = -323021
  Y1 = 322141
  Y2 = 321141
  Z1 = 0
  Z2 = 0
FEATURE [Part::Line] Axis_1_55
  AttacherType = Attacher::AttachEngine3D
  X1 = -323021
  X2 = -323021
  Y1 = 322141
  Y2 = 322141
  Z1 = 0
  Z2 = -1000
FEATURE [Part::Line] Axis_2_55
  AttacherType = Attacher::AttachEngine3D
  X1 = -323021
  X2 = -324021
  Y1 = 322141
  Y2 = 322141
  Z1 = 0
  Z2 = 0
FEATURE [Part::Feature] Heliostat_56  label="Heliostat_56(Mirror,Axis_1_56,Axis_2_56,Normal_56,Target_point)"
  Placement = pos=(268191,-477777,1.00815e-10) rot=(0,0,1;0rad)
  shape: bbox 10000 x 40.57 x 10000 mm, 1 faces, 0 solids (baked)
FEATURE [Part::Line] Normal_56
  AttacherType = Attacher::AttachEngine3D
  X1 = 268191
  X2 = 268191
  Y1 = 138479
  Y2 = 137479
  Z1 = 0
  Z2 = 0
FEATURE [Part::Line] Axis_1_56
  AttacherType = Attacher::AttachEngine3D
  X1 = 268191
  X2 = 268191
  Y1 = 138479
  Y2 = 138479
  Z1 = 0
  Z2 = -1000
FEATURE [Part::Line] Axis_2_56
  AttacherType = Attacher::AttachEngine3D
  X1 = 268191
  X2 = 267191
  Y1 = 138479
  Y2 = 138479
  Z1 = 0
  Z2 = 0
FEATURE [Part::Feature] Heliostat_57  label="Heliostat_57(Mirror,Axis_1_57,Axis_2_57,Normal_57,Target_point)"
  Placement = pos=(-268191,-477777,1.00815e-10) rot=(0,0,1;0rad)
  shape: bbox 10000 x 40.57 x 10000 mm, 1 faces, 0 solids (baked)
FEATURE [Part::Line] Normal_57
  AttacherType = Attacher::AttachEngine3D
  X1 = -268191
  X2 = -268191
  Y1 = 138479
  Y2 = 137479
  Z1 = 0
  Z2 = 0
FEATURE [Part::Line] Axis_1_57
  AttacherType = Attacher::AttachEngine3D
  X1 = -268191
  X2 = -268191
  Y1 = 138479
  Y2 = 138479
  Z1 = 0
  Z2 = -1000
FEATURE [Part::Line] Axis_2_57
  AttacherType = Attacher::AttachEngine3D
  X1 = -268191
  X2 = -269191
  Y1 = 138479
  Y2 = 138479
  Z1 = 0
  Z2 = 0
FEATURE [Part::Feature] Heliostat_58  label="Heliostat_58(Mirror,Axis_1_58,Axis_2_58,Normal_58,Target_point)"
  Placement = pos=(270018,-616876,1.9455e-10) rot=(0,0,1;0rad)
  shape: bbox 10000 x 23.13 x 10000 mm, 1 faces, 0 solids (baked)
FEATURE [Part::Line] Normal_58
  AttacherType = Attacher::AttachEngine3D
  X1 = 270018
  X2 = 270018
  Y1 = 464071
  Y2 = 463071
  Z1 = 0
  Z2 = 0
FEATURE [Part::Line] Axis_1_58
  AttacherType = Attacher::AttachEngine3D
  X1 = 270018
  X2 = 270018
  Y1 = 464071
  Y2 = 464071
  Z1 = 0
  Z2 = -1000
FEATURE [Part::Line] Axis_2_58
  AttacherType = Attacher::AttachEngine3D
  X1 = 270018
  X2 = 269018
  Y1 = 464071
  Y2 = 464071
  Z1 = 0
  Z2 = 0
FEATURE [Part::Feature] Heliostat_59  label="Heliostat_59(Mirror,Axis_1_59,Axis_2_59,Normal_59,Target_point)"
  Placement = pos=(-270018,-616876,1.9455e-10) rot=(0,0,1;0rad)
  shape: bbox 10000 x 23.13 x 10000 mm, 1 faces, 0 solids (baked)
FEATURE [Part::Line] Normal_59
  AttacherType = Attacher::AttachEngine3D
  X1 = -270018
  X2 = -270018
  Y1 = 464071
  Y2 = 463071
  Z1 = 0
  Z2 = 0
FEATURE [Part::Line] Axis_1_59
  AttacherType = Attacher::AttachEngine3D
  X1 = -270018
  X2 = -270018
  Y1 = 464071
  Y2 = 464071
  Z1 = 0
  Z2 = -1000
FEATURE [Part::Line] Axis_2_59
  AttacherType = Attacher::AttachEngine3D
  X1 = -270018
  X2 = -271018
  Y1 = 464071
  Y2 = 464071
  Z1 = 0
  Z2 = 0
FEATURE [Part::Feature] Heliostat_60  label="Heliostat_60(Mirror,Axis_1_60,Axis_2_60,Normal_60,Target_point)"
  Placement = pos=(320596,-577369,2.1959e-10) rot=(0,0,1;0rad)
  shape: bbox 10000 x 29.51 x 10000 mm, 1 faces, 0 solids (baked)
FEATURE [Part::Line] Normal_60
  AttacherType = Attacher::AttachEngine3D
  X1 = 320596
  X2 = 320596
  Y1 = 269890
  Y2 = 268890
  Z1 = 0
  Z2 = 0
FEATURE [Part::Line] Axis_1_60
  AttacherType = Attacher::AttachEngine3D
  X1 = 320596
  X2 = 320596
  Y1 = 269890
  Y2 = 269890
  Z1 = 0
  Z2 = -1000
FEATURE [Part::Line] Axis_2_60
  AttacherType = Attacher::AttachEngine3D
  X1 = 320596
  X2 = 319596
  Y1 = 269890
  Y2 = 269890
  Z1 = 0
  Z2 = 0
FEATURE [Part::Feature] Heliostat_61  label="Heliostat_61(Mirror,Axis_1_61,Axis_2_61,Normal_61,Target_point)"
  Placement = pos=(-320596,-577369,2.1959e-10) rot=(0,0,1;0rad)
  shape: bbox 10000 x 29.51 x 10000 mm, 1 faces, 0 solids (baked)
FEATURE [Part::Line] Normal_61
  AttacherType = Attacher::AttachEngine3D
  X1 = -320596
  X2 = -320596
  Y1 = 269890
  Y2 = 268890
  Z1 = 0
  Z2 = 0
FEATURE [Part::Line] Axis_1_61
  AttacherType = Attacher::AttachEngine3D
  X1 = -320596
  X2 = -320596
  Y1 = 269890
  Y2 = 269890
  Z1 = 0
  Z2 = -1000
FEATURE [Part::Line] Axis_2_61
  AttacherType = Attacher::AttachEngine3D
  X1 = -320596
  X2 = -321596
  Y1 = 269890
  Y2 = 269890
  Z1 = 0
  Z2 = 0
FEATURE [Part::Feature] Heliostat_62  label="Heliostat_62(Mirror,Axis_1_62,Axis_2_62,Normal_62,Target_point)"
  Placement = pos=(151186,-607124,2.14733e-10) rot=(0,0,1;0rad)
  shape: bbox 10000 x 21.41 x 10000 mm, 1 faces, 0 solids (baked)
FEATURE [Part::Line] Normal_62
  AttacherType = Attacher::AttachEngine3D
  X1 = 151186
  X2 = 151186
  Y1 = 560461
  Y2 = 559461
  Z1 = 0
  Z2 = 0
FEATURE [Part::Line] Axis_1_62
  AttacherType = Attacher::AttachEngine3D
  X1 = 151186
  X2 = 151186
  Y1 = 560461
  Y2 = 560461
  Z1 = 0
  Z2 = -1000
FEATURE [Part::Line] Axis_2_62
  AttacherType = Attacher::AttachEngine3D
  X1 = 151186
  X2 = 150186
  Y1 = 560461
  Y2 = 560461
  Z1 = 0
  Z2 = 0
FEATURE [Part::Feature] Heliostat_63  label="Heliostat_63(Mirror,Axis_1_63,Axis_2_63,Normal_63,Target_point)"
  Placement = pos=(-151186,-607124,2.14733e-10) rot=(0,0,1;0rad)
  shape: bbox 10000 x 21.41 x 10000 mm, 1 faces, 0 solids (baked)
FEATURE [Part::Line] Normal_63
  AttacherType = Attacher::AttachEngine3D
  X1 = -151186
  X2 = -151186
  Y1 = 560461
  Y2 = 559461
  Z1 = 0
  Z2 = 0
FEATURE [Part::Line] Axis_1_63
  AttacherType = Attacher::AttachEngine3D
  X1 = -151186
  X2 = -151186
  Y1 = 560461
  Y2 = 560461
  Z1 = 0
  Z2 = -1000
FEATURE [Part::Line] Axis_2_63
  AttacherType = Attacher::AttachEngine3D
  X1 = -151186
  X2 = -152186
  Y1 = 560461
  Y2 = 560461
  Z1 = 0
  Z2 = 0
FEATURE [Part::Feature] Heliostat_64  label="Heliostat_64(Mirror,Axis_1_64,Axis_2_64,Normal_64,Target_point)"
  Placement = pos=(316347,-561043,1.43589e-10) rot=(0,0,1;0rad)
  shape: bbox 10000 x 31.86 x 10000 mm, 1 faces, 0 solids (baked)
FEATURE [Part::Line] Normal_64
  AttacherType = Attacher::AttachEngine3D
  X1 = 316347
  X2 = 316347
  Y1 = 223673
  Y2 = 222673
  Z1 = 0
  Z2 = 0
FEATURE [Part::Line] Axis_1_64
  AttacherType = Attacher::AttachEngine3D
  X1 = 316347
  X2 = 316347
  Y1 = 223673
  Y2 = 223673
  Z1 = 0
  Z2 = -1000
FEATURE [Part::Line] Axis_2_64
  AttacherType = Attacher::AttachEngine3D
  X1 = 316347
  X2 = 315347
  Y1 = 223673
  Y2 = 223673
  Z1 = 0
  Z2 = 0
FEATURE [Part::Feature] Heliostat_65  label="Heliostat_65(Mirror,Axis_1_65,Axis_2_65,Normal_65,Target_point)"
  Placement = pos=(-316347,-561043,1.43589e-10) rot=(0,0,1;0rad)
  shape: bbox 10000 x 31.86 x 10000 mm, 1 faces, 0 solids (baked)
FEATURE [Part::Line] Normal_65
  AttacherType = Attacher::AttachEngine3D
  X1 = -316347
  X2 = -316347
  Y1 = 223673
  Y2 = 222673
  Z1 = 0
  Z2 = 0
FEATURE [Part::Line] Axis_1_65
  AttacherType = Attacher::AttachEngine3D
  X1 = -316347
  X2 = -316347
  Y1 = 223673
  Y2 = 223673
  Z1 = 0
  Z2 = -1000
FEATURE [Part::Line] Axis_2_65
  AttacherType = Attacher::AttachEngine3D
  X1 = -316347
  X2 = -317347
  Y1 = 223673
  Y2 = 223673
  Z1 = 0
  Z2 = 0
FEATURE [Part::Feature] Heliostat_66  label="Heliostat_66(Mirror,Axis_1_66,Axis_2_66,Normal_66,Target_point)"
  Placement = pos=(128350,-601457,3.14826e-10) rot=(0,0,1;0rad)
  shape: bbox 10000 x 21.41 x 10000 mm, 1 faces, 0 solids (baked)
FEATURE [Part::Line] Normal_66
  AttacherType = Attacher::AttachEngine3D
  X1 = 128350
  X2 = 128350
  Y1 = 566127
  Y2 = 565127
  Z1 = 0
  Z2 = 0
FEATURE [Part::Line] Axis_1_66
  AttacherType = Attacher::AttachEngine3D
  X1 = 128350
  X2 = 128350
  Y1 = 566127
  Y2 = 566127
  Z1 = 0
  Z2 = -1000
FEATURE [Part::Line] Axis_2_66
  AttacherType = Attacher::AttachEngine3D
  X1 = 128350
  X2 = 127350
  Y1 = 566127
  Y2 = 566127
  Z1 = 0
  Z2 = 0
FEATURE [Part::Feature] Heliostat_67  label="Heliostat_67(Mirror,Axis_1_67,Axis_2_67,Normal_67,Target_point)"
  Placement = pos=(-128350,-601457,3.14826e-10) rot=(0,0,1;0rad)
  shape: bbox 10000 x 21.41 x 10000 mm, 1 faces, 0 solids (baked)
FEATURE [Part::Line] Normal_67
  AttacherType = Attacher::AttachEngine3D
  X1 = -128350
  X2 = -128350
  Y1 = 566127
  Y2 = 565127
  Z1 = 0
  Z2 = 0
FEATURE [Part::Line] Axis_1_67
  AttacherType = Attacher::AttachEngine3D
  X1 = -128350
  X2 = -128350
  Y1 = 566127
  Y2 = 566127
  Z1 = 0
  Z2 = -1000
FEATURE [Part::Line] Axis_2_67
  AttacherType = Attacher::AttachEngine3D
  X1 = -128350
  X2 = -129350
  Y1 = 566127
  Y2 = 566127
  Z1 = 0
  Z2 = 0
FEATURE [Part::Feature] Heliostat_68  label="Heliostat_68(Mirror,Axis_1_68,Axis_2_68,Normal_68,Target_point)"
  Placement = pos=(221730,-553715,2.69056e-10) rot=(0,0,1;0rad)
  shape: bbox 10000 x 25.14 x 10000 mm, 1 faces, 0 solids (baked)
FEATURE [Part::Line] Normal_68
  AttacherType = Attacher::AttachEngine3D
  X1 = 221730
  X2 = 221730
  Y1 = 440687
  Y2 = 439687
  Z1 = 0
  Z2 = 0
FEATURE [Part::Line] Axis_1_68
  AttacherType = Attacher::AttachEngine3D
  X1 = 221730
  X2 = 221730
  Y1 = 440687
  Y2 = 440687
  Z1 = 0
  Z2 = -1000
FEATURE [Part::Line] Axis_2_68
  AttacherType = Attacher::AttachEngine3D
  X1 = 221730
  X2 = 220730
  Y1 = 440687
  Y2 = 440687
  Z1 = 0
  Z2 = 0
FEATURE [Part::Feature] Heliostat_69  label="Heliostat_69(Mirror,Axis_1_69,Axis_2_69,Normal_69,Target_point)"
  Placement = pos=(-221730,-553715,2.69056e-10) rot=(0,0,1;0rad)
  shape: bbox 10000 x 25.14 x 10000 mm, 1 faces, 0 solids (baked)
FEATURE [Part::Line] Normal_69
  AttacherType = Attacher::AttachEngine3D
  X1 = -221730
  X2 = -221730
  Y1 = 440687
  Y2 = 439687
  Z1 = 0
  Z2 = 0
FEATURE [Part::Line] Axis_1_69
  AttacherType = Attacher::AttachEngine3D
  X1 = -221730
  X2 = -221730
  Y1 = 440687
  Y2 = 440687
  Z1 = 0
  Z2 = -1000
FEATURE [Part::Line] Axis_2_69
  AttacherType = Attacher::AttachEngine3D
  X1 = -221730
  X2 = -222730
  Y1 = 440687
  Y2 = 440687
  Z1 = 0
  Z2 = 0
FEATURE [Part::Feature] Heliostat_70  label="Heliostat_70(Mirror,Axis_1_70,Axis_2_70,Normal_70,Target_point)"
  Placement = pos=(252537,-453076,1.05655e-10) rot=(0,0,1;0rad)
  shape: bbox 10000 x 43.77 x 10000 mm, 1 faces, 0 solids (baked)
FEATURE [Part::Line] Normal_70
  AttacherType = Attacher::AttachEngine3D
  X1 = 252537
  X2 = 252537
  Y1 = 118138
  Y2 = 117138
  Z1 = 0
  Z2 = 0
FEATURE [Part::Line] Axis_1_70
  AttacherType = Attacher::AttachEngine3D
  X1 = 252537
  X2 = 252537
  Y1 = 118138
  Y2 = 118138
  Z1 = 0
  Z2 = -1000
FEATURE [Part::Line] Axis_2_70
  AttacherType = Attacher::AttachEngine3D
  X1 = 252537
  X2 = 251537
  Y1 = 118138
  Y2 = 118138
  Z1 = 0
  Z2 = 0
FEATURE [Part::Feature] Heliostat_71  label="Heliostat_71(Mirror,Axis_1_71,Axis_2_71,Normal_71,Target_point)"
  Placement = pos=(-252537,-453076,1.05655e-10) rot=(0,0,1;0rad)
  shape: bbox 10000 x 43.77 x 10000 mm, 1 faces, 0 solids (baked)
FEATURE [Part::Line] Normal_71
  AttacherType = Attacher::AttachEngine3D
  X1 = -252537
  X2 = -252537
  Y1 = 118138
  Y2 = 117138
  Z1 = 0
  Z2 = 0
FEATURE [Part::Line] Axis_1_71
  AttacherType = Attacher::AttachEngine3D
  X1 = -252537
  X2 = -252537
  Y1 = 118138
  Y2 = 118138
  Z1 = 0
  Z2 = -1000
FEATURE [Part::Line] Axis_2_71
  AttacherType = Attacher::AttachEngine3D
  X1 = -252537
  X2 = -253537
  Y1 = 118138
  Y2 = 118138
  Z1 = 0
  Z2 = 0
FEATURE [Part::Feature] Heliostat_72  label="Heliostat_72(Mirror,Axis_1_72,Axis_2_72,Normal_72,Target_point)"
  Placement = pos=(250990,-606315,1.93734e-10) rot=(0,0,1;0rad)
  shape: bbox 10000 x 23.13 x 10000 mm, 1 faces, 0 solids (baked)
FEATURE [Part::Line] Normal_72
  AttacherType = Attacher::AttachEngine3D
  X1 = 250990
  X2 = 250990
  Y1 = 474632
  Y2 = 473632
  Z1 = 0
  Z2 = 0
FEATURE [Part::Line] Axis_1_72
  AttacherType = Attacher::AttachEngine3D
  X1 = 250990
  X2 = 250990
  Y1 = 474632
  Y2 = 474632
  Z1 = 0
  Z2 = -1000
FEATURE [Part::Line] Axis_2_72
  AttacherType = Attacher::AttachEngine3D
  X1 = 250990
  X2 = 249990
  Y1 = 474632
  Y2 = 474632
  Z1 = 0
  Z2 = 0
FEATURE [Part::Feature] Heliostat_73  label="Heliostat_73(Mirror,Axis_1_73,Axis_2_73,Normal_73,Target_point)"
  Placement = pos=(-250990,-606315,1.93734e-10) rot=(0,0,1;0rad)
  shape: bbox 10000 x 23.13 x 10000 mm, 1 faces, 0 solids (baked)
FEATURE [Part::Line] Normal_73
  AttacherType = Attacher::AttachEngine3D
  X1 = -250990
  X2 = -250990
  Y1 = 474632
  Y2 = 473632
  Z1 = 0
  Z2 = 0
FEATURE [Part::Line] Axis_1_73
  AttacherType = Attacher::AttachEngine3D
  X1 = -250990
  X2 = -250990
  Y1 = 474632
  Y2 = 474632
  Z1 = 0
  Z2 = -1000
FEATURE [Part::Line] Axis_2_73
  AttacherType = Attacher::AttachEngine3D
  X1 = -250990
  X2 = -251990
  Y1 = 474632
  Y2 = 474632
  Z1 = 0
  Z2 = 0
FEATURE [Part::Feature] Heliostat_74  label="Heliostat_74(Mirror,Axis_1_74,Axis_2_74,Normal_74,Target_point)"
  Placement = pos=(231549,-596533,2.86613e-10) rot=(0,0,1;0rad)
  shape: bbox 10000 x 23.13 x 10000 mm, 1 faces, 0 solids (baked)
FEATURE [Part::Line] Normal_74
  AttacherType = Attacher::AttachEngine3D
  X1 = 231549
  X2 = 231549
  Y1 = 484414
  Y2 = 483414
  Z1 = 0
  Z2 = 0
FEATURE [Part::Line] Axis_1_74
  AttacherType = Attacher::AttachEngine3D
  X1 = 231549
  X2 = 231549
  Y1 = 484414
  Y2 = 484414
  Z1 = 0
  Z2 = -1000
FEATURE [Part::Line] Axis_2_74
  AttacherType = Attacher::AttachEngine3D
  X1 = 231549
  X2 = 230549
  Y1 = 484414
  Y2 = 484414
  Z1 = 0
  Z2 = 0
FEATURE [Part::Feature] Heliostat_75  label="Heliostat_75(Mirror,Axis_1_75,Axis_2_75,Normal_75,Target_point)"
  Placement = pos=(-231549,-596533,2.86613e-10) rot=(0,0,1;0rad)
  shape: bbox 10000 x 23.13 x 10000 mm, 1 faces, 0 solids (baked)
FEATURE [Part::Line] Normal_75
  AttacherType = Attacher::AttachEngine3D
  X1 = -231549
  X2 = -231549
  Y1 = 484414
  Y2 = 483414
  Z1 = 0
  Z2 = 0
FEATURE [Part::Line] Axis_1_75
  AttacherType = Attacher::AttachEngine3D
  X1 = -231549
  X2 = -231549
  Y1 = 484414
  Y2 = 484414
  Z1 = 0
  Z2 = -1000
FEATURE [Part::Line] Axis_2_75
  AttacherType = Attacher::AttachEngine3D
  X1 = -231549
  X2 = -232549
  Y1 = 484414
  Y2 = 484414
  Z1 = 0
  Z2 = 0
FEATURE [Part::Feature] Heliostat_76  label="Heliostat_76(Mirror,Axis_1_76,Axis_2_76,Normal_76,Target_point)"
  Placement = pos=(303285,-543628,1.43666e-10) rot=(0,0,1;0rad)
  shape: bbox 10000 x 31.86 x 10000 mm, 1 faces, 0 solids (baked)
FEATURE [Part::Line] Normal_76
  AttacherType = Attacher::AttachEngine3D
  X1 = 303285
  X2 = 303285
  Y1 = 241088
  Y2 = 240088
  Z1 = 0
  Z2 = 0
FEATURE [Part::Line] Axis_1_76
  AttacherType = Attacher::AttachEngine3D
  X1 = 303285
  X2 = 303285
  Y1 = 241088
  Y2 = 241088
  Z1 = 0
  Z2 = -1000
FEATURE [Part::Line] Axis_2_76
  AttacherType = Attacher::AttachEngine3D
  X1 = 303285
  X2 = 302285
  Y1 = 241088
  Y2 = 241088
  Z1 = 0
  Z2 = 0
FEATURE [Part::Feature] Heliostat_77  label="Heliostat_77(Mirror,Axis_1_77,Axis_2_77,Normal_77,Target_point)"
  Placement = pos=(-303285,-543628,1.43666e-10) rot=(0,0,1;0rad)
  shape: bbox 10000 x 31.86 x 10000 mm, 1 faces, 0 solids (baked)
FEATURE [Part::Line] Normal_77
  AttacherType = Attacher::AttachEngine3D
  X1 = -303285
  X2 = -303285
  Y1 = 241088
  Y2 = 240088
  Z1 = 0
  Z2 = 0
FEATURE [Part::Line] Axis_1_77
  AttacherType = Attacher::AttachEngine3D
  X1 = -303285
  X2 = -303285
  Y1 = 241088
  Y2 = 241088
  Z1 = 0
  Z2 = -1000
FEATURE [Part::Line] Axis_2_77
  AttacherType = Attacher::AttachEngine3D
  X1 = -303285
  X2 = -304285
  Y1 = 241088
  Y2 = 241088
  Z1 = 0
  Z2 = 0
FEATURE [Part::Feature] Heliostat_78  label="Heliostat_78(Mirror,Axis_1_78,Axis_2_78,Normal_78,Target_point)"
  Placement = pos=(304418,-581001,2.42787e-10) rot=(0,0,1;0rad)
  shape: bbox 10000 x 27.15 x 10000 mm, 1 faces, 0 solids (baked)
FEATURE [Part::Line] Normal_78
  AttacherType = Attacher::AttachEngine3D
  X1 = 304418
  X2 = 304418
  Y1 = 339775
  Y2 = 338775
  Z1 = 0
  Z2 = 0
FEATURE [Part::Line] Axis_1_78
  AttacherType = Attacher::AttachEngine3D
  X1 = 304418
  X2 = 304418
  Y1 = 339775
  Y2 = 339775
  Z1 = 0
  Z2 = -1000
FEATURE [Part::Line] Axis_2_78
  AttacherType = Attacher::AttachEngine3D
  X1 = 304418
  X2 = 303418
  Y1 = 339775
  Y2 = 339775
  Z1 = 0
  Z2 = 0
FEATURE [Part::Feature] Heliostat_79  label="Heliostat_79(Mirror,Axis_1_79,Axis_2_79,Normal_79,Target_point)"
  Placement = pos=(-304418,-581001,2.42787e-10) rot=(0,0,1;0rad)
  shape: bbox 10000 x 27.15 x 10000 mm, 1 faces, 0 solids (baked)
FEATURE [Part::Line] Normal_79
  AttacherType = Attacher::AttachEngine3D
  X1 = -304418
  X2 = -304418
  Y1 = 339775
  Y2 = 338775
  Z1 = 0
  Z2 = 0
FEATURE [Part::Line] Axis_1_79
  AttacherType = Attacher::AttachEngine3D
  X1 = -304418
  X2 = -304418
  Y1 = 339775
  Y2 = 339775
  Z1 = 0
  Z2 = -1000
FEATURE [Part::Line] Axis_2_79
  AttacherType = Attacher::AttachEngine3D
  X1 = -304418
  X2 = -305418
  Y1 = 339775
  Y2 = 339775
  Z1 = 0
  Z2 = 0
FEATURE [Part::Feature] Heliostat_80  label="Heliostat_80(Mirror,Axis_1_80,Axis_2_80,Normal_80,Target_point)"
  Placement = pos=(273551,-583867,1.35663e-10) rot=(0,0,1;0rad)
  shape: bbox 10000 x 25.14 x 10000 mm, 1 faces, 0 solids (baked)
FEATURE [Part::Line] Normal_80
  AttacherType = Attacher::AttachEngine3D
  X1 = 273551
  X2 = 273551
  Y1 = 410535
  Y2 = 409535
  Z1 = 0
  Z2 = 0
FEATURE [Part::Line] Axis_1_80
  AttacherType = Attacher::AttachEngine3D
  X1 = 273551
  X2 = 273551
  Y1 = 410535
  Y2 = 410535
  Z1 = 0
  Z2 = -1000
FEATURE [Part::Line] Axis_2_80
  AttacherType = Attacher::AttachEngine3D
  X1 = 273551
  X2 = 272551
  Y1 = 410535
  Y2 = 410535
  Z1 = 0
  Z2 = 0
FEATURE [Part::Feature] Heliostat_81  label="Heliostat_81(Mirror,Axis_1_81,Axis_2_81,Normal_81,Target_point)"
  Placement = pos=(-273551,-583867,1.35663e-10) rot=(0,0,1;0rad)
  shape: bbox 10000 x 25.14 x 10000 mm, 1 faces, 0 solids (baked)
FEATURE [Part::Line] Normal_81
  AttacherType = Attacher::AttachEngine3D
  X1 = -273551
  X2 = -273551
  Y1 = 410535
  Y2 = 409535
  Z1 = 0
  Z2 = 0
FEATURE [Part::Line] Axis_1_81
  AttacherType = Attacher::AttachEngine3D
  X1 = -273551
  X2 = -273551
  Y1 = 410535
  Y2 = 410535
  Z1 = 0
  Z2 = -1000
FEATURE [Part::Line] Axis_2_81
  AttacherType = Attacher::AttachEngine3D
  X1 = -273551
  X2 = -274551
  Y1 = 410535
  Y2 = 410535
  Z1 = 0
  Z2 = 0
FEATURE [Part::Feature] Heliostat_82  label="Heliostat_82(Mirror,Axis_1_82,Axis_2_82,Normal_82,Target_point)"
  Placement = pos=(150312,-565507,1.93734e-10) rot=(0,0,1;0rad)
  shape: bbox 10000 x 23.13 x 10000 mm, 1 faces, 0 solids (baked)
FEATURE [Part::Line] Normal_82
  AttacherType = Attacher::AttachEngine3D
  X1 = 150312
  X2 = 150312
  Y1 = 515440
  Y2 = 514440
  Z1 = 0
  Z2 = 0
FEATURE [Part::Line] Axis_1_82
  AttacherType = Attacher::AttachEngine3D
  X1 = 150312
  X2 = 150312
  Y1 = 515440
  Y2 = 515440
  Z1 = 0
  Z2 = -1000
FEATURE [Part::Line] Axis_2_82
  AttacherType = Attacher::AttachEngine3D
  X1 = 150312
  X2 = 149312
  Y1 = 515440
  Y2 = 515440
  Z1 = 0
  Z2 = 0
FEATURE [Part::Feature] Heliostat_83  label="Heliostat_83(Mirror,Axis_1_83,Axis_2_83,Normal_83,Target_point)"
  Placement = pos=(-150312,-565507,1.93734e-10) rot=(0,0,1;0rad)
  shape: bbox 10000 x 23.13 x 10000 mm, 1 faces, 0 solids (baked)
FEATURE [Part::Line] Normal_83
  AttacherType = Attacher::AttachEngine3D
  X1 = -150312
  X2 = -150312
  Y1 = 515440
  Y2 = 514440
  Z1 = 0
  Z2 = 0
FEATURE [Part::Line] Axis_1_83
  AttacherType = Attacher::AttachEngine3D
  X1 = -150312
  X2 = -150312
  Y1 = 515440
  Y2 = 515440
  Z1 = 0
  Z2 = -1000
FEATURE [Part::Line] Axis_2_83
  AttacherType = Attacher::AttachEngine3D
  X1 = -150312
  X2 = -151312
  Y1 = 515440
  Y2 = 515440
  Z1 = 0
  Z2 = 0
FEATURE [Part::Feature] Heliostat_84  label="Heliostat_84(Mirror,Axis_1_84,Axis_2_84,Normal_84,Target_point)"
  Placement = pos=(211729,-587548,1.93734e-10) rot=(0,0,1;0rad)
  shape: bbox 10000 x 23.13 x 10000 mm, 1 faces, 0 solids (baked)
FEATURE [Part::Line] Normal_84
  AttacherType = Attacher::AttachEngine3D
  X1 = 211729
  X2 = 211729
  Y1 = 493399
  Y2 = 492399
  Z1 = 0
  Z2 = 0
FEATURE [Part::Line] Axis_1_84
  AttacherType = Attacher::AttachEngine3D
  X1 = 211729
  X2 = 211729
  Y1 = 493399
  Y2 = 493399
  Z1 = 0
  Z2 = -1000
FEATURE [Part::Line] Axis_2_84
  AttacherType = Attacher::AttachEngine3D
  X1 = 211729
  X2 = 210729
  Y1 = 493399
  Y2 = 493399
  Z1 = 0
  Z2 = 0
FEATURE [Part::Feature] Heliostat_85  label="Heliostat_85(Mirror,Axis_1_85,Axis_2_85,Normal_85,Target_point)"
  Placement = pos=(-211729,-587548,1.93734e-10) rot=(0,0,1;0rad)
  shape: bbox 10000 x 23.13 x 10000 mm, 1 faces, 0 solids (baked)
FEATURE [Part::Line] Normal_85
  AttacherType = Attacher::AttachEngine3D
  X1 = -211729
  X2 = -211729
  Y1 = 493399
  Y2 = 492399
  Z1 = 0
  Z2 = 0
FEATURE [Part::Line] Axis_1_85
  AttacherType = Attacher::AttachEngine3D
  X1 = -211729
  X2 = -211729
  Y1 = 493399
  Y2 = 493399
  Z1 = 0
  Z2 = -1000
FEATURE [Part::Line] Axis_2_85
  AttacherType = Attacher::AttachEngine3D
  X1 = -211729
  X2 = -212729
  Y1 = 493399
  Y2 = 493399
  Z1 = 0
  Z2 = 0
FEATURE [Part::Feature] Heliostat_86  label="Heliostat_86(Mirror,Axis_1_86,Axis_2_86,Normal_86,Target_point)"
  Placement = pos=(103798,-211881,7.05225e-11) rot=(0,0,1;0rad)
  shape: bbox 10000 x 95.83 x 10000 mm, 1 faces, 0 solids (baked)
FEATURE [Part::Line] Normal_86
  AttacherType = Attacher::AttachEngine3D
  X1 = 103798
  X2 = 103798
  Y1 = 49004.2
  Y2 = 48004.2
  Z1 = 0
  Z2 = 0
FEATURE [Part::Line] Axis_1_86
  AttacherType = Attacher::AttachEngine3D
  X1 = 103798
  X2 = 103798
  Y1 = 49004.2
  Y2 = 49004.2
  Z1 = 0
  Z2 = -1000
FEATURE [Part::Line] Axis_2_86
  AttacherType = Attacher::AttachEngine3D
  X1 = 103798
  X2 = 102798
  Y1 = 49004.2
  Y2 = 49004.2
  Z1 = 0
  Z2 = 0
FEATURE [Part::Feature] Heliostat_87  label="Heliostat_87(Mirror,Axis_1_87,Axis_2_87,Normal_87,Target_point)"
  Placement = pos=(-103798,-211881,7.05225e-11) rot=(0,0,1;0rad)
  shape: bbox 10000 x 95.83 x 10000 mm, 1 faces, 0 solids (baked)
FEATURE [Part::Line] Normal_87
  AttacherType = Attacher::AttachEngine3D
  X1 = -103798
  X2 = -103798
  Y1 = 49004.2
  Y2 = 48004.2
  Z1 = 0
  Z2 = 0
FEATURE [Part::Line] Axis_1_87
  AttacherType = Attacher::AttachEngine3D
  X1 = -103798
  X2 = -103798
  Y1 = 49004.2
  Y2 = 49004.2
  Z1 = 0
  Z2 = -1000
FEATURE [Part::Line] Axis_2_87
  AttacherType = Attacher::AttachEngine3D
  X1 = -103798
  X2 = -104798
  Y1 = 49004.2
  Y2 = 49004.2
  Z1 = 0
  Z2 = 0
FEATURE [Part::Feature] Heliostat_88  label="Heliostat_88(Mirror,Axis_1_88,Axis_2_88,Normal_88,Target_point)"
  Placement = pos=(128483,-518103,2.63934e-10) rot=(0,0,1;0rad)
  shape: bbox 10000 x 25.14 x 10000 mm, 1 faces, 0 solids (baked)
FEATURE [Part::Line] Normal_88
  AttacherType = Attacher::AttachEngine3D
  X1 = 128483
  X2 = 128483
  Y1 = 476300
  Y2 = 475300
  Z1 = 0
  Z2 = 0
FEATURE [Part::Line] Axis_1_88
  AttacherType = Attacher::AttachEngine3D
  X1 = 128483
  X2 = 128483
  Y1 = 476300
  Y2 = 476300
  Z1 = 0
  Z2 = -1000
FEATURE [Part::Line] Axis_2_88
  AttacherType = Attacher::AttachEngine3D
  X1 = 128483
  X2 = 127483
  Y1 = 476300
  Y2 = 476300
  Z1 = 0
  Z2 = 0
FEATURE [Part::Feature] Heliostat_89  label="Heliostat_89(Mirror,Axis_1_89,Axis_2_89,Normal_89,Target_point)"
  Placement = pos=(-128483,-518103,2.63934e-10) rot=(0,0,1;0rad)
  shape: bbox 10000 x 25.14 x 10000 mm, 1 faces, 0 solids (baked)
FEATURE [Part::Line] Normal_89
  AttacherType = Attacher::AttachEngine3D
  X1 = -128483
  X2 = -128483
  Y1 = 476300
  Y2 = 475300
  Z1 = 0
  Z2 = 0
FEATURE [Part::Line] Axis_1_89
  AttacherType = Attacher::AttachEngine3D
  X1 = -128483
  X2 = -128483
  Y1 = 476300
  Y2 = 476300
  Z1 = 0
  Z2 = -1000
FEATURE [Part::Line] Axis_2_89
  AttacherType = Attacher::AttachEngine3D
  X1 = -128483
  X2 = -129483
  Y1 = 476300
  Y2 = 476300
  Z1 = 0
  Z2 = 0
FEATURE [Part::Feature] Heliostat_90  label="Heliostat_90(Mirror,Axis_1_90,Axis_2_90,Normal_90,Target_point)"
  Placement = pos=(304931,-559788,8.18275e-11) rot=(0,0,1;0rad)
  shape: bbox 10000 x 29.51 x 10000 mm, 1 faces, 0 solids (baked)
FEATURE [Part::Line] Normal_90
  AttacherType = Attacher::AttachEngine3D
  X1 = 304931
  X2 = 304931
  Y1 = 287471
  Y2 = 286471
  Z1 = 0
  Z2 = 0
FEATURE [Part::Line] Axis_1_90
  AttacherType = Attacher::AttachEngine3D
  X1 = 304931
  X2 = 304931
  Y1 = 287471
  Y2 = 287471
  Z1 = 0
  Z2 = -1000
FEATURE [Part::Line] Axis_2_90
  AttacherType = Attacher::AttachEngine3D
  X1 = 304931
  X2 = 303931
  Y1 = 287471
  Y2 = 287471
  Z1 = 0
  Z2 = 0
FEATURE [Part::Feature] Heliostat_91  label="Heliostat_91(Mirror,Axis_1_91,Axis_2_91,Normal_91,Target_point)"
  Placement = pos=(-304931,-559788,8.18275e-11) rot=(0,0,1;0rad)
  shape: bbox 10000 x 29.51 x 10000 mm, 1 faces, 0 solids (baked)
FEATURE [Part::Line] Normal_91
  AttacherType = Attacher::AttachEngine3D
  X1 = -304931
  X2 = -304931
  Y1 = 287471
  Y2 = 286471
  Z1 = 0
  Z2 = 0
FEATURE [Part::Line] Axis_1_91
  AttacherType = Attacher::AttachEngine3D
  X1 = -304931
  X2 = -304931
  Y1 = 287471
  Y2 = 287471
  Z1 = 0
  Z2 = -1000
FEATURE [Part::Line] Axis_2_91
  AttacherType = Attacher::AttachEngine3D
  X1 = -304931
  X2 = -305931
  Y1 = 287471
  Y2 = 287471
  Z1 = 0
  Z2 = 0
FEATURE [Part::Feature] Heliostat_92  label="Heliostat_92(Mirror,Axis_1_92,Axis_2_92,Normal_92,Target_point)"
  Placement = pos=(98353.4,-215037,2.33538e-11) rot=(0,0,1;0rad)
  shape: bbox 10000 x 105.8 x 10000 mm, 1 faces, 0 solids (baked)
FEATURE [Part::Line] Normal_92
  AttacherType = Attacher::AttachEngine3D
  X1 = 98353.4
  X2 = 98353.4
  Y1 = 21341.3
  Y2 = 20341.3
  Z1 = 0
  Z2 = 0
FEATURE [Part::Line] Axis_1_92
  AttacherType = Attacher::AttachEngine3D
  X1 = 98353.4
  X2 = 98353.4
  Y1 = 21341.3
  Y2 = 21341.3
  Z1 = 0
  Z2 = -1000
FEATURE [Part::Line] Axis_2_92
  AttacherType = Attacher::AttachEngine3D
  X1 = 98353.4
  X2 = 97353.4
  Y1 = 21341.3
  Y2 = 21341.3
  Z1 = 0
  Z2 = 0
FEATURE [Part::Feature] Heliostat_93  label="Heliostat_93(Mirror,Axis_1_93,Axis_2_93,Normal_93,Target_point)"
  Placement = pos=(-98353.4,-215037,2.33538e-11) rot=(0,0,1;0rad)
  shape: bbox 10000 x 105.8 x 10000 mm, 1 faces, 0 solids (baked)
FEATURE [Part::Line] Normal_93
  AttacherType = Attacher::AttachEngine3D
  X1 = -98353.4
  X2 = -98353.4
  Y1 = 21341.3
  Y2 = 20341.3
  Z1 = 0
  Z2 = 0
FEATURE [Part::Line] Axis_1_93
  AttacherType = Attacher::AttachEngine3D
  X1 = -98353.4
  X2 = -98353.4
  Y1 = 21341.3
  Y2 = 21341.3
  Z1 = 0
  Z2 = -1000
FEATURE [Part::Line] Axis_2_93
  AttacherType = Attacher::AttachEngine3D
  X1 = -98353.4
  X2 = -99353.4
  Y1 = 21341.3
  Y2 = 21341.3
  Z1 = 0
  Z2 = 0
FEATURE [Part::Feature] Heliostat_94  label="Heliostat_94(Mirror,Axis_1_94,Axis_2_94,Normal_94,Target_point)"
  Placement = pos=(191560,-579373,2.9829e-10) rot=(0,0,1;0rad)
  shape: bbox 10000 x 23.13 x 10000 mm, 1 faces, 0 solids (baked)
FEATURE [Part::Line] Normal_94
  AttacherType = Attacher::AttachEngine3D
  X1 = 191560
  X2 = 191560
  Y1 = 501574
  Y2 = 500574
  Z1 = 0
  Z2 = 0
FEATURE [Part::Line] Axis_1_94
  AttacherType = Attacher::AttachEngine3D
  X1 = 191560
  X2 = 191560
  Y1 = 501574
  Y2 = 501574
  Z1 = 0
  Z2 = -1000
FEATURE [Part::Line] Axis_2_94
  AttacherType = Attacher::AttachEngine3D
  X1 = 191560
  X2 = 190560
  Y1 = 501574
  Y2 = 501574
  Z1 = 0
  Z2 = 0
FEATURE [Part::Feature] Heliostat_95  label="Heliostat_95(Mirror,Axis_1_95,Axis_2_95,Normal_95,Target_point)"
  Placement = pos=(-191560,-579373,2.9829e-10) rot=(0,0,1;0rad)
  shape: bbox 10000 x 23.13 x 10000 mm, 1 faces, 0 solids (baked)
FEATURE [Part::Line] Normal_95
  AttacherType = Attacher::AttachEngine3D
  X1 = -191560
  X2 = -191560
  Y1 = 501574
  Y2 = 500574
  Z1 = 0
  Z2 = 0
FEATURE [Part::Line] Axis_1_95
  AttacherType = Attacher::AttachEngine3D
  X1 = -191560
  X2 = -191560
  Y1 = 501574
  Y2 = 501574
  Z1 = 0
  Z2 = -1000
FEATURE [Part::Line] Axis_2_95
  AttacherType = Attacher::AttachEngine3D
  X1 = -191560
  X2 = -192560
  Y1 = 501574
  Y2 = 501574
  Z1 = 0
  Z2 = 0
FEATURE [Part::Feature] Heliostat_96  label="Heliostat_96(Mirror,Axis_1_96,Axis_2_96,Normal_96,Target_point)"
  Placement = pos=(136348,-271367,5.78436e-11) rot=(0,0,1;0rad)
  shape: bbox 10000 x 80.99 x 10000 mm, 1 faces, 0 solids (baked)
FEATURE [Part::Line] Normal_96
  AttacherType = Attacher::AttachEngine3D
  X1 = 136348
  X2 = 136348
  Y1 = 37337.6
  Y2 = 36337.6
  Z1 = 0
  Z2 = 0
FEATURE [Part::Line] Axis_1_96
  AttacherType = Attacher::AttachEngine3D
  X1 = 136348
  X2 = 136348
  Y1 = 37337.6
  Y2 = 37337.6
  Z1 = 0
  Z2 = -1000
FEATURE [Part::Line] Axis_2_96
  AttacherType = Attacher::AttachEngine3D
  X1 = 136348
  X2 = 135348
  Y1 = 37337.6
  Y2 = 37337.6
  Z1 = 0
  Z2 = 0
FEATURE [Part::Feature] Heliostat_97  label="Heliostat_97(Mirror,Axis_1_97,Axis_2_97,Normal_97,Target_point)"
  Placement = pos=(-136348,-271367,5.78436e-11) rot=(0,0,1;0rad)
  shape: bbox 10000 x 80.99 x 10000 mm, 1 faces, 0 solids (baked)
FEATURE [Part::Line] Normal_97
  AttacherType = Attacher::AttachEngine3D
  X1 = -136348
  X2 = -136348
  Y1 = 37337.6
  Y2 = 36337.6
  Z1 = 0
  Z2 = 0
FEATURE [Part::Line] Axis_1_97
  AttacherType = Attacher::AttachEngine3D
  X1 = -136348
  X2 = -136348
  Y1 = 37337.6
  Y2 = 37337.6
  Z1 = 0
  Z2 = -1000
FEATURE [Part::Line] Axis_2_97
  AttacherType = Attacher::AttachEngine3D
  X1 = -136348
  X2 = -137348
  Y1 = 37337.6
  Y2 = 37337.6
  Z1 = 0
  Z2 = 0
FEATURE [Part::Feature] Heliostat_98  label="Heliostat_98(Mirror,Axis_1_98,Axis_2_98,Normal_98,Target_point)"
  Placement = pos=(171076,-572022,2.9829e-10) rot=(0,0,1;0rad)
  shape: bbox 10000 x 23.13 x 10000 mm, 1 faces, 0 solids (baked)
FEATURE [Part::Line] Normal_98
  AttacherType = Attacher::AttachEngine3D
  X1 = 171076
  X2 = 171076
  Y1 = 508925
  Y2 = 507925
  Z1 = 0
  Z2 = 0
FEATURE [Part::Line] Axis_1_98
  AttacherType = Attacher::AttachEngine3D
  X1 = 171076
  X2 = 171076
  Y1 = 508925
  Y2 = 508925
  Z1 = 0
  Z2 = -1000
FEATURE [Part::Line] Axis_2_98
  AttacherType = Attacher::AttachEngine3D
  X1 = 171076
  X2 = 170076
  Y1 = 508925
  Y2 = 508925
  Z1 = 0
  Z2 = 0
FEATURE [Part::Feature] Heliostat_99  label="Heliostat_99(Mirror,Axis_1_99,Axis_2_99,Normal_99,Target_point)"
  Placement = pos=(-171076,-572022,2.9829e-10) rot=(0,0,1;0rad)
  shape: bbox 10000 x 23.13 x 10000 mm, 1 faces, 0 solids (baked)
FEATURE [Part::Line] Normal_99
  AttacherType = Attacher::AttachEngine3D
  X1 = -171076
  X2 = -171076
  Y1 = 508925
  Y2 = 507925
  Z1 = 0
  Z2 = 0
FEATURE [Part::Line] Axis_1_99
  AttacherType = Attacher::AttachEngine3D
  X1 = -171076
  X2 = -171076
  Y1 = 508925
  Y2 = 508925
  Z1 = 0
  Z2 = -1000
FEATURE [Part::Line] Axis_2_99
  AttacherType = Attacher::AttachEngine3D
  X1 = -171076
  X2 = -172076
  Y1 = 508925
  Y2 = 508925
  Z1 = 0
  Z2 = 0
FEATURE [Part::Feature] Heliostat_100  label="Heliostat_100(Mirror,Axis_1_100,Axis_2_100,Normal_100,Target_point)"
  Placement = pos=(86675,-551080,2.86613e-10) rot=(0,0,1;0rad)
  shape: bbox 10000 x 23.13 x 10000 mm, 1 faces, 0 solids (baked)
FEATURE [Part::Line] Normal_100
  AttacherType = Attacher::AttachEngine3D
  X1 = 86675
  X2 = 86675
  Y1 = 529867
  Y2 = 528867
  Z1 = 0
  Z2 = 0
FEATURE [Part::Line] Axis_1_100
  AttacherType = Attacher::AttachEngine3D
  X1 = 86675
  X2 = 86675
  Y1 = 529867
  Y2 = 529867
  Z1 = 0
  Z2 = -1000
FEATURE [Part::Line] Axis_2_100
  AttacherType = Attacher::AttachEngine3D
  X1 = 86675
  X2 = 85675
  Y1 = 529867
  Y2 = 529867
  Z1 = 0
  Z2 = 0
FEATURE [Part::Feature] Heliostat_101  label="Heliostat_101(Mirror,Axis_1_101,Axis_2_101,Normal_101,Target_point)"
  Placement = pos=(-86675,-551080,2.86613e-10) rot=(0,0,1;0rad)
  shape: bbox 10000 x 23.13 x 10000 mm, 1 faces, 0 solids (baked)
FEATURE [Part::Line] Normal_101
  AttacherType = Attacher::AttachEngine3D
  X1 = -86675
  X2 = -86675
  Y1 = 529867
  Y2 = 528867
  Z1 = 0
  Z2 = 0
FEATURE [Part::Line] Axis_1_101
  AttacherType = Attacher::AttachEngine3D
  X1 = -86675
  X2 = -86675
  Y1 = 529867
  Y2 = 529867
  Z1 = 0
  Z2 = -1000
FEATURE [Part::Line] Axis_2_101
  AttacherType = Attacher::AttachEngine3D
  X1 = -86675
  X2 = -87675
  Y1 = 529867
  Y2 = 529867
  Z1 = 0
  Z2 = 0
FEATURE [Part::Feature] Heliostat_102  label="Heliostat_102(Mirror,Axis_1_102,Axis_2_102,Normal_102,Target_point)"
  Placement = pos=(284853,-564439,8.39512e-11) rot=(0,0,1;0rad)
  shape: bbox 10000 x 27.15 x 10000 mm, 1 faces, 0 solids (baked)
FEATURE [Part::Line] Normal_102
  AttacherType = Attacher::AttachEngine3D
  X1 = 284853
  X2 = 284853
  Y1 = 356338
  Y2 = 355338
  Z1 = 0
  Z2 = 0
FEATURE [Part::Line] Axis_1_102
  AttacherType = Attacher::AttachEngine3D
  X1 = 284853
  X2 = 284853
  Y1 = 356338
  Y2 = 356338
  Z1 = 0
  Z2 = -1000
FEATURE [Part::Line] Axis_2_102
  AttacherType = Attacher::AttachEngine3D
  X1 = 284853
  X2 = 283853
  Y1 = 356338
  Y2 = 356338
  Z1 = 0
  Z2 = 0
FEATURE [Part::Feature] Heliostat_103  label="Heliostat_103(Mirror,Axis_1_103,Axis_2_103,Normal_103,Target_point)"
  Placement = pos=(-284853,-564439,8.39512e-11) rot=(0,0,1;0rad)
  shape: bbox 10000 x 27.15 x 10000 mm, 1 faces, 0 solids (baked)
FEATURE [Part::Line] Normal_103
  AttacherType = Attacher::AttachEngine3D
  X1 = -284853
  X2 = -284853
  Y1 = 356338
  Y2 = 355338
  Z1 = 0
  Z2 = 0
FEATURE [Part::Line] Axis_1_103
  AttacherType = Attacher::AttachEngine3D
  X1 = -284853
  X2 = -284853
  Y1 = 356338
  Y2 = 356338
  Z1 = 0
  Z2 = -1000
FEATURE [Part::Line] Axis_2_103
  AttacherType = Attacher::AttachEngine3D
  X1 = -284853
  X2 = -285853
  Y1 = 356338
  Y2 = 356338
  Z1 = 0
  Z2 = 0
FEATURE [Part::Feature] Heliostat_104  label="Heliostat_104(Mirror,Axis_1_104,Axis_2_104,Normal_104,Target_point)"
  Placement = pos=(65596.5,-166691,7.09671e-11) rot=(0,0,1;0rad)
  shape: bbox 10000 x 95.83 x 10000 mm, 1 faces, 0 solids (baked)
FEATURE [Part::Line] Normal_104
  AttacherType = Attacher::AttachEngine3D
  X1 = 65596.5
  X2 = 65596.5
  Y1 = 94194.1
  Y2 = 93194.1
  Z1 = 0
  Z2 = 0
FEATURE [Part::Line] Axis_1_104
  AttacherType = Attacher::AttachEngine3D
  X1 = 65596.5
  X2 = 65596.5
  Y1 = 94194.1
  Y2 = 94194.1
  Z1 = 0
  Z2 = -1000
FEATURE [Part::Line] Axis_2_104
  AttacherType = Attacher::AttachEngine3D
  X1 = 65596.5
  X2 = 64596.5
  Y1 = 94194.1
  Y2 = 94194.1
  Z1 = 0
  Z2 = 0
FEATURE [Part::Feature] Heliostat_105  label="Heliostat_105(Mirror,Axis_1_105,Axis_2_105,Normal_105,Target_point)"
  Placement = pos=(-65596.5,-166691,7.09671e-11) rot=(0,0,1;0rad)
  shape: bbox 10000 x 95.83 x 10000 mm, 1 faces, 0 solids (baked)
FEATURE [Part::Line] Normal_105
  AttacherType = Attacher::AttachEngine3D
  X1 = -65596.5
  X2 = -65596.5
  Y1 = 94194.1
  Y2 = 93194.1
  Z1 = 0
  Z2 = 0
FEATURE [Part::Line] Axis_1_105
  AttacherType = Attacher::AttachEngine3D
  X1 = -65596.5
  X2 = -65596.5
  Y1 = 94194.1
  Y2 = 94194.1
  Z1 = 0
  Z2 = -1000
FEATURE [Part::Line] Axis_2_105
  AttacherType = Attacher::AttachEngine3D
  X1 = -65596.5
  X2 = -66596.5
  Y1 = 94194.1
  Y2 = 94194.1
  Z1 = 0
  Z2 = 0
FEATURE [Part::Feature] Heliostat_106  label="Heliostat_106(Mirror,Axis_1_106,Axis_2_106,Normal_106,Target_point)"
  Placement = pos=(65131.2,-548003,4.24192e-10) rot=(0,0,1;0rad)
  shape: bbox 10000 x 23.13 x 10000 mm, 1 faces, 0 solids (baked)
FEATURE [Part::Line] Normal_106
  AttacherType = Attacher::AttachEngine3D
  X1 = 65131.2
  X2 = 65131.2
  Y1 = 532944
  Y2 = 531944
  Z1 = 0
  Z2 = 0
FEATURE [Part::Line] Axis_1_106
  AttacherType = Attacher::AttachEngine3D
  X1 = 65131.2
  X2 = 65131.2
  Y1 = 532944
  Y2 = 532944
  Z1 = 0
  Z2 = -1000
FEATURE [Part::Line] Axis_2_106
  AttacherType = Attacher::AttachEngine3D
  X1 = 65131.2
  X2 = 64131.2
  Y1 = 532944
  Y2 = 532944
  Z1 = 0
  Z2 = 0
FEATURE [Part::Feature] Heliostat_107  label="Heliostat_107(Mirror,Axis_1_107,Axis_2_107,Normal_107,Target_point)"
  Placement = pos=(-65131.2,-548003,4.24192e-10) rot=(0,0,1;0rad)
  shape: bbox 10000 x 23.13 x 10000 mm, 1 faces, 0 solids (baked)
FEATURE [Part::Line] Normal_107
  AttacherType = Attacher::AttachEngine3D
  X1 = -65131.2
  X2 = -65131.2
  Y1 = 532944
  Y2 = 531944
  Z1 = 0
  Z2 = 0
FEATURE [Part::Line] Axis_1_107
  AttacherType = Attacher::AttachEngine3D
  X1 = -65131.2
  X2 = -65131.2
  Y1 = 532944
  Y2 = 532944
  Z1 = 0
  Z2 = -1000
FEATURE [Part::Line] Axis_2_107
  AttacherType = Attacher::AttachEngine3D
  X1 = -65131.2
  X2 = -66131.2
  Y1 = 532944
  Y2 = 532944
  Z1 = 0
  Z2 = 0
FEATURE [Part::Feature] Heliostat_108  label="Heliostat_108(Mirror,Axis_1_108,Axis_2_108,Normal_108,Target_point)"
  Placement = pos=(129300,-559839,2.94608e-10) rot=(0,0,1;0rad)
  shape: bbox 10000 x 23.13 x 10000 mm, 1 faces, 0 solids (baked)
FEATURE [Part::Line] Normal_108
  AttacherType = Attacher::AttachEngine3D
  X1 = 129300
  X2 = 129300
  Y1 = 521108
  Y2 = 520108
  Z1 = 0
  Z2 = 0
FEATURE [Part::Line] Axis_1_108
  AttacherType = Attacher::AttachEngine3D
  X1 = 129300
  X2 = 129300
  Y1 = 521108
  Y2 = 521108
  Z1 = 0
  Z2 = -1000
FEATURE [Part::Line] Axis_2_108
  AttacherType = Attacher::AttachEngine3D
  X1 = 129300
  X2 = 128300
  Y1 = 521108
  Y2 = 521108
  Z1 = 0
  Z2 = 0
FEATURE [Part::Feature] Heliostat_109  label="Heliostat_109(Mirror,Axis_1_109,Axis_2_109,Normal_109,Target_point)"
  Placement = pos=(-129300,-559839,2.94608e-10) rot=(0,0,1;0rad)
  shape: bbox 10000 x 23.13 x 10000 mm, 1 faces, 0 solids (baked)
FEATURE [Part::Line] Normal_109
  AttacherType = Attacher::AttachEngine3D
  X1 = -129300
  X2 = -129300
  Y1 = 521108
  Y2 = 520108
  Z1 = 0
  Z2 = 0
FEATURE [Part::Line] Axis_1_109
  AttacherType = Attacher::AttachEngine3D
  X1 = -129300
  X2 = -129300
  Y1 = 521108
  Y2 = 521108
  Z1 = 0
  Z2 = -1000
FEATURE [Part::Line] Axis_2_109
  AttacherType = Attacher::AttachEngine3D
  X1 = -129300
  X2 = -130300
  Y1 = 521108
  Y2 = 521108
  Z1 = 0
  Z2 = 0
FEATURE [Part::Feature] Heliostat_110  label="Heliostat_110(Mirror,Axis_1_110,Axis_2_110,Normal_110,Target_point)"
  Placement = pos=(284628,-508813,1.94453e-10) rot=(0,0,1;0rad)
  shape: bbox 10000 x 34.61 x 10000 mm, 1 faces, 0 solids (baked)
FEATURE [Part::Line] Normal_110
  AttacherType = Attacher::AttachEngine3D
  X1 = 284628
  X2 = 284628
  Y1 = 213488
  Y2 = 212488
  Z1 = 0
  Z2 = 0
FEATURE [Part::Line] Axis_1_110
  AttacherType = Attacher::AttachEngine3D
  X1 = 284628
  X2 = 284628
  Y1 = 213488
  Y2 = 213488
  Z1 = 0
  Z2 = -1000
FEATURE [Part::Line] Axis_2_110
  AttacherType = Attacher::AttachEngine3D
  X1 = 284628
  X2 = 283628
  Y1 = 213488
  Y2 = 213488
  Z1 = 0
  Z2 = 0
FEATURE [Part::Feature] Heliostat_111  label="Heliostat_111(Mirror,Axis_1_111,Axis_2_111,Normal_111,Target_point)"
  Placement = pos=(-284628,-508813,1.94453e-10) rot=(0,0,1;0rad)
  shape: bbox 10000 x 34.61 x 10000 mm, 1 faces, 0 solids (baked)
FEATURE [Part::Line] Normal_111
  AttacherType = Attacher::AttachEngine3D
  X1 = -284628
  X2 = -284628
  Y1 = 213488
  Y2 = 212488
  Z1 = 0
  Z2 = 0
FEATURE [Part::Line] Axis_1_111
  AttacherType = Attacher::AttachEngine3D
  X1 = -284628
  X2 = -284628
  Y1 = 213488
  Y2 = 213488
  Z1 = 0
  Z2 = -1000
FEATURE [Part::Line] Axis_2_111
  AttacherType = Attacher::AttachEngine3D
  X1 = -284628
  X2 = -285628
  Y1 = 213488
  Y2 = 213488
  Z1 = 0
  Z2 = 0
FEATURE [Part::Feature] Heliostat_112  label="Heliostat_112(Mirror,Axis_1_112,Axis_2_112,Normal_112,Target_point)"
  Placement = pos=(186208,-346144,1.27201e-10) rot=(0,0,1;0rad)
  shape: bbox 10000 x 59.82 x 10000 mm, 1 faces, 0 solids (baked)
FEATURE [Part::Line] Normal_112
  AttacherType = Attacher::AttachEngine3D
  X1 = 186208
  X2 = 186208
  Y1 = 71786.6
  Y2 = 70786.6
  Z1 = 0
  Z2 = 0
FEATURE [Part::Line] Axis_1_112
  AttacherType = Attacher::AttachEngine3D
  X1 = 186208
  X2 = 186208
  Y1 = 71786.6
  Y2 = 71786.6
  Z1 = 0
  Z2 = -1000
FEATURE [Part::Line] Axis_2_112
  AttacherType = Attacher::AttachEngine3D
  X1 = 186208
  X2 = 185208
  Y1 = 71786.6
  Y2 = 71786.6
  Z1 = 0
  Z2 = 0
FEATURE [Part::Feature] Heliostat_113  label="Heliostat_113(Mirror,Axis_1_113,Axis_2_113,Normal_113,Target_point)"
  Placement = pos=(-186208,-346144,1.27201e-10) rot=(0,0,1;0rad)
  shape: bbox 10000 x 59.82 x 10000 mm, 1 faces, 0 solids (baked)
FEATURE [Part::Line] Normal_113
  AttacherType = Attacher::AttachEngine3D
  X1 = -186208
  X2 = -186208
  Y1 = 71786.6
  Y2 = 70786.6
  Z1 = 0
  Z2 = 0
FEATURE [Part::Line] Axis_1_113
  AttacherType = Attacher::AttachEngine3D
  X1 = -186208
  X2 = -186208
  Y1 = 71786.6
  Y2 = 71786.6
  Z1 = 0
  Z2 = -1000
FEATURE [Part::Line] Axis_2_113
  AttacherType = Attacher::AttachEngine3D
  X1 = -186208
  X2 = -187208
  Y1 = 71786.6
  Y2 = 71786.6
  Z1 = 0
  Z2 = 0
FEATURE [Part::Feature] Heliostat_114  label="Heliostat_114(Mirror,Axis_1_114,Axis_2_114,Normal_114,Target_point)"
  Placement = pos=(108076,-555028,2.9829e-10) rot=(0,0,1;0rad)
  shape: bbox 10000 x 23.13 x 10000 mm, 1 faces, 0 solids (baked)
FEATURE [Part::Line] Normal_114
  AttacherType = Attacher::AttachEngine3D
  X1 = 108076
  X2 = 108076
  Y1 = 525919
  Y2 = 524919
  Z1 = 0
  Z2 = 0
FEATURE [Part::Line] Axis_1_114
  AttacherType = Attacher::AttachEngine3D
  X1 = 108076
  X2 = 108076
  Y1 = 525919
  Y2 = 525919
  Z1 = 0
  Z2 = -1000
FEATURE [Part::Line] Axis_2_114
  AttacherType = Attacher::AttachEngine3D
  X1 = 108076
  X2 = 107076
  Y1 = 525919
  Y2 = 525919
  Z1 = 0
  Z2 = 0
FEATURE [Part::Feature] Heliostat_115  label="Heliostat_115(Mirror,Axis_1_115,Axis_2_115,Normal_115,Target_point)"
  Placement = pos=(-108076,-555028,2.9829e-10) rot=(0,0,1;0rad)
  shape: bbox 10000 x 23.13 x 10000 mm, 1 faces, 0 solids (baked)
FEATURE [Part::Line] Normal_115
  AttacherType = Attacher::AttachEngine3D
  X1 = -108076
  X2 = -108076
  Y1 = 525919
  Y2 = 524919
  Z1 = 0
  Z2 = 0
FEATURE [Part::Line] Axis_1_115
  AttacherType = Attacher::AttachEngine3D
  X1 = -108076
  X2 = -108076
  Y1 = 525919
  Y2 = 525919
  Z1 = 0
  Z2 = -1000
FEATURE [Part::Line] Axis_2_115
  AttacherType = Attacher::AttachEngine3D
  X1 = -108076
  X2 = -109076
  Y1 = 525919
  Y2 = 525919
  Z1 = 0
  Z2 = 0
FEATURE [Part::Feature] Heliostat_116  label="Heliostat_116(Mirror,Axis_1_116,Axis_2_116,Normal_116,Target_point)"
  Placement = pos=(272515,-485208,1.77539e-10) rot=(0,0,1;0rad)
  shape: bbox 10000 x 37.36 x 10000 mm, 1 faces, 0 solids (baked)
FEATURE [Part::Line] Normal_116
  AttacherType = Attacher::AttachEngine3D
  X1 = 272515
  X2 = 272515
  Y1 = 183995
  Y2 = 182995
  Z1 = 0
  Z2 = 0
FEATURE [Part::Line] Axis_1_116
  AttacherType = Attacher::AttachEngine3D
  X1 = 272515
  X2 = 272515
  Y1 = 183995
  Y2 = 183995
  Z1 = 0
  Z2 = -1000
FEATURE [Part::Line] Axis_2_116
  AttacherType = Attacher::AttachEngine3D
  X1 = 272515
  X2 = 271515
  Y1 = 183995
  Y2 = 183995
  Z1 = 0
  Z2 = 0
FEATURE [Part::Feature] Heliostat_117  label="Heliostat_117(Mirror,Axis_1_117,Axis_2_117,Normal_117,Target_point)"
  Placement = pos=(-272515,-485208,1.77539e-10) rot=(0,0,1;0rad)
  shape: bbox 10000 x 37.36 x 10000 mm, 1 faces, 0 solids (baked)
FEATURE [Part::Line] Normal_117
  AttacherType = Attacher::AttachEngine3D
  X1 = -272515
  X2 = -272515
  Y1 = 183995
  Y2 = 182995
  Z1 = 0
  Z2 = 0
FEATURE [Part::Line] Axis_1_117
  AttacherType = Attacher::AttachEngine3D
  X1 = -272515
  X2 = -272515
  Y1 = 183995
  Y2 = 183995
  Z1 = 0
  Z2 = -1000
FEATURE [Part::Line] Axis_2_117
  AttacherType = Attacher::AttachEngine3D
  X1 = -272515
  X2 = -273515
  Y1 = 183995
  Y2 = 183995
  Z1 = 0
  Z2 = 0
FEATURE [Part::Feature] Heliostat_118  label="Heliostat_118(Mirror,Axis_1_118,Axis_2_118,Normal_118,Target_point)"
  Placement = pos=(288303,-543115,8.65532e-11) rot=(0,0,1;0rad)
  shape: bbox 10000 x 29.51 x 10000 mm, 1 faces, 0 solids (baked)
FEATURE [Part::Line] Normal_118
  AttacherType = Attacher::AttachEngine3D
  X1 = 288303
  X2 = 288303
  Y1 = 304144
  Y2 = 303144
  Z1 = 0
  Z2 = 0
FEATURE [Part::Line] Axis_1_118
  AttacherType = Attacher::AttachEngine3D
  X1 = 288303
  X2 = 288303
  Y1 = 304144
  Y2 = 304144
  Z1 = 0
  Z2 = -1000
FEATURE [Part::Line] Axis_2_118
  AttacherType = Attacher::AttachEngine3D
  X1 = 288303
  X2 = 287303
  Y1 = 304144
  Y2 = 304144
  Z1 = 0
  Z2 = 0
FEATURE [Part::Feature] Heliostat_119  label="Heliostat_119(Mirror,Axis_1_119,Axis_2_119,Normal_119,Target_point)"
  Placement = pos=(-288303,-543115,8.65532e-11) rot=(0,0,1;0rad)
  shape: bbox 10000 x 29.51 x 10000 mm, 1 faces, 0 solids (baked)
FEATURE [Part::Line] Normal_119
  AttacherType = Attacher::AttachEngine3D
  X1 = -288303
  X2 = -288303
  Y1 = 304144
  Y2 = 303144
  Z1 = 0
  Z2 = 0
FEATURE [Part::Line] Axis_1_119
  AttacherType = Attacher::AttachEngine3D
  X1 = -288303
  X2 = -288303
  Y1 = 304144
  Y2 = 304144
  Z1 = 0
  Z2 = -1000
FEATURE [Part::Line] Axis_2_119
  AttacherType = Attacher::AttachEngine3D
  X1 = -288303
  X2 = -289303
  Y1 = 304144
  Y2 = 304144
  Z1 = 0
  Z2 = 0
FEATURE [Part::Feature] Heliostat_120  label="Heliostat_120(Mirror,Axis_1_120,Axis_2_120,Normal_120,Target_point)"
  Placement = pos=(272187,-493163,1.94453e-10) rot=(0,0,1;0rad)
  shape: bbox 10000 x 34.61 x 10000 mm, 1 faces, 0 solids (baked)
FEATURE [Part::Line] Normal_120
  AttacherType = Attacher::AttachEngine3D
  X1 = 272187
  X2 = 272187
  Y1 = 229138
  Y2 = 228138
  Z1 = 0
  Z2 = 0
FEATURE [Part::Line] Axis_1_120
  AttacherType = Attacher::AttachEngine3D
  X1 = 272187
  X2 = 272187
  Y1 = 229138
  Y2 = 229138
  Z1 = 0
  Z2 = -1000
FEATURE [Part::Line] Axis_2_120
  AttacherType = Attacher::AttachEngine3D
  X1 = 272187
  X2 = 271187
  Y1 = 229138
  Y2 = 229138
  Z1 = 0
  Z2 = 0
FEATURE [Part::Feature] Heliostat_121  label="Heliostat_121(Mirror,Axis_1_121,Axis_2_121,Normal_121,Target_point)"
  Placement = pos=(-272187,-493163,1.94453e-10) rot=(0,0,1;0rad)
  shape: bbox 10000 x 34.61 x 10000 mm, 1 faces, 0 solids (baked)
FEATURE [Part::Line] Normal_121
  AttacherType = Attacher::AttachEngine3D
  X1 = -272187
  X2 = -272187
  Y1 = 229138
  Y2 = 228138
  Z1 = 0
  Z2 = 0
FEATURE [Part::Line] Axis_1_121
  AttacherType = Attacher::AttachEngine3D
  X1 = -272187
  X2 = -272187
  Y1 = 229138
  Y2 = 229138
  Z1 = 0
  Z2 = -1000
FEATURE [Part::Line] Axis_2_121
  AttacherType = Attacher::AttachEngine3D
  X1 = -272187
  X2 = -273187
  Y1 = 229138
  Y2 = 229138
  Z1 = 0
  Z2 = 0
FEATURE [Part::Feature] Heliostat_122  label="Heliostat_122(Mirror,Axis_1_122,Axis_2_122,Normal_122,Target_point)"
  Placement = pos=(264388,-549002,8.81217e-11) rot=(0,0,1;0rad)
  shape: bbox 10000 x 27.15 x 10000 mm, 1 faces, 0 solids (baked)
FEATURE [Part::Line] Normal_122
  AttacherType = Attacher::AttachEngine3D
  X1 = 264388
  X2 = 264388
  Y1 = 371775
  Y2 = 370775
  Z1 = 0
  Z2 = 0
FEATURE [Part::Line] Axis_1_122
  AttacherType = Attacher::AttachEngine3D
  X1 = 264388
  X2 = 264388
  Y1 = 371775
  Y2 = 371775
  Z1 = 0
  Z2 = -1000
FEATURE [Part::Line] Axis_2_122
  AttacherType = Attacher::AttachEngine3D
  X1 = 264388
  X2 = 263388
  Y1 = 371775
  Y2 = 371775
  Z1 = 0
  Z2 = 0
FEATURE [Part::Feature] Heliostat_123  label="Heliostat_123(Mirror,Axis_1_123,Axis_2_123,Normal_123,Target_point)"
  Placement = pos=(-264388,-549002,8.81217e-11) rot=(0,0,1;0rad)
  shape: bbox 10000 x 27.15 x 10000 mm, 1 faces, 0 solids (baked)
FEATURE [Part::Line] Normal_123
  AttacherType = Attacher::AttachEngine3D
  X1 = -264388
  X2 = -264388
  Y1 = 371775
  Y2 = 370775
  Z1 = 0
  Z2 = 0
FEATURE [Part::Line] Axis_1_123
  AttacherType = Attacher::AttachEngine3D
  X1 = -264388
  X2 = -264388
  Y1 = 371775
  Y2 = 371775
  Z1 = 0
  Z2 = -1000
FEATURE [Part::Line] Axis_2_123
  AttacherType = Attacher::AttachEngine3D
  X1 = -264388
  X2 = -265388
  Y1 = 371775
  Y2 = 371775
  Z1 = 0
  Z2 = 0
FEATURE [Part::Feature] Heliostat_124  label="Heliostat_124(Mirror,Axis_1_124,Axis_2_124,Normal_124,Target_point)"
  Placement = pos=(256561,-457260,1.69118e-10) rot=(0,0,1;0rad)
  shape: bbox 10000 x 40.57 x 10000 mm, 1 faces, 0 solids (baked)
FEATURE [Part::Line] Normal_124
  AttacherType = Attacher::AttachEngine3D
  X1 = 256561
  X2 = 256561
  Y1 = 158996
  Y2 = 157996
  Z1 = 0
  Z2 = 0
FEATURE [Part::Line] Axis_1_124
  AttacherType = Attacher::AttachEngine3D
  X1 = 256561
  X2 = 256561
  Y1 = 158996
  Y2 = 158996
  Z1 = 0
  Z2 = -1000
FEATURE [Part::Line] Axis_2_124
  AttacherType = Attacher::AttachEngine3D
  X1 = 256561
  X2 = 255561
  Y1 = 158996
  Y2 = 158996
  Z1 = 0
  Z2 = 0
FEATURE [Part::Feature] Heliostat_125  label="Heliostat_125(Mirror,Axis_1_125,Axis_2_125,Normal_125,Target_point)"
  Placement = pos=(-256561,-457260,1.69118e-10) rot=(0,0,1;0rad)
  shape: bbox 10000 x 40.57 x 10000 mm, 1 faces, 0 solids (baked)
FEATURE [Part::Line] Normal_125
  AttacherType = Attacher::AttachEngine3D
  X1 = -256561
  X2 = -256561
  Y1 = 158996
  Y2 = 157996
  Z1 = 0
  Z2 = 0
FEATURE [Part::Line] Axis_1_125
  AttacherType = Attacher::AttachEngine3D
  X1 = -256561
  X2 = -256561
  Y1 = 158996
  Y2 = 158996
  Z1 = 0
  Z2 = -1000
FEATURE [Part::Line] Axis_2_125
  AttacherType = Attacher::AttachEngine3D
  X1 = -256561
  X2 = -257561
  Y1 = 158996
  Y2 = 158996
  Z1 = 0
  Z2 = 0
FEATURE [Part::Feature] Heliostat_126  label="Heliostat_126(Mirror,Axis_1_126,Axis_2_126,Normal_126,Target_point)"
  Placement = pos=(43480.3,-545801,2.9829e-10) rot=(0,0,1;0rad)
  shape: bbox 10000 x 23.13 x 10000 mm, 1 faces, 0 solids (baked)
FEATURE [Part::Line] Normal_126
  AttacherType = Attacher::AttachEngine3D
  X1 = 43480.3
  X2 = 43480.3
  Y1 = 535146
  Y2 = 534146
  Z1 = 0
  Z2 = 0
FEATURE [Part::Line] Axis_1_126
  AttacherType = Attacher::AttachEngine3D
  X1 = 43480.3
  X2 = 43480.3
  Y1 = 535146
  Y2 = 535146
  Z1 = 0
  Z2 = -1000
FEATURE [Part::Line] Axis_2_126
  AttacherType = Attacher::AttachEngine3D
  X1 = 43480.3
  X2 = 42480.3
  Y1 = 535146
  Y2 = 535146
  Z1 = 0
  Z2 = 0
FEATURE [Part::Feature] Heliostat_127  label="Heliostat_127(Mirror,Axis_1_127,Axis_2_127,Normal_127,Target_point)"
  Placement = pos=(-43480.3,-545801,2.9829e-10) rot=(0,0,1;0rad)
  shape: bbox 10000 x 23.13 x 10000 mm, 1 faces, 0 solids (baked)
FEATURE [Part::Line] Normal_127
  AttacherType = Attacher::AttachEngine3D
  X1 = -43480.3
  X2 = -43480.3
  Y1 = 535146
  Y2 = 534146
  Z1 = 0
  Z2 = 0
FEATURE [Part::Line] Axis_1_127
  AttacherType = Attacher::AttachEngine3D
  X1 = -43480.3
  X2 = -43480.3
  Y1 = 535146
  Y2 = 535146
  Z1 = 0
  Z2 = -1000
FEATURE [Part::Line] Axis_2_127
  AttacherType = Attacher::AttachEngine3D
  X1 = -43480.3
  X2 = -44480.3
  Y1 = 535146
  Y2 = 535146
  Z1 = 0
  Z2 = 0
FEATURE [Part::Feature] Heliostat_128  label="Heliostat_128(Mirror,Axis_1_128,Axis_2_128,Normal_128,Target_point)"
  Placement = pos=(21758,-544479,2.94608e-10) rot=(0,0,1;0rad)
  shape: bbox 10000 x 23.13 x 10000 mm, 1 faces, 0 solids (baked)
FEATURE [Part::Line] Normal_128
  AttacherType = Attacher::AttachEngine3D
  X1 = 21758
  X2 = 21758
  Y1 = 536468
  Y2 = 535468
  Z1 = 0
  Z2 = 0
FEATURE [Part::Line] Axis_1_128
  AttacherType = Attacher::AttachEngine3D
  X1 = 21758
  X2 = 21758
  Y1 = 536468
  Y2 = 536468
  Z1 = 0
  Z2 = -1000
FEATURE [Part::Line] Axis_2_128
  AttacherType = Attacher::AttachEngine3D
  X1 = 21758
  X2 = 20758
  Y1 = 536468
  Y2 = 536468
  Z1 = 0
  Z2 = 0
FEATURE [Part::Feature] Heliostat_129  label="Heliostat_129(Mirror,Axis_1_129,Axis_2_129,Normal_129,Target_point)"
  Placement = pos=(-21758,-544479,2.94608e-10) rot=(0,0,1;0rad)
  shape: bbox 10000 x 23.13 x 10000 mm, 1 faces, 0 solids (baked)
FEATURE [Part::Line] Normal_129
  AttacherType = Attacher::AttachEngine3D
  X1 = -21758
  X2 = -21758
  Y1 = 536468
  Y2 = 535468
  Z1 = 0
  Z2 = 0
FEATURE [Part::Line] Axis_1_129
  AttacherType = Attacher::AttachEngine3D
  X1 = -21758
  X2 = -21758
  Y1 = 536468
  Y2 = 536468
  Z1 = 0
  Z2 = -1000
FEATURE [Part::Line] Axis_2_129
  AttacherType = Attacher::AttachEngine3D
  X1 = -21758
  X2 = -22758
  Y1 = 536468
  Y2 = 536468
  Z1 = 0
  Z2 = 0
FEATURE [Part::Feature] Heliostat_130  label="Heliostat_130(Mirror,Axis_1_130,Axis_2_130,Normal_130,Target_point)"
  Placement = pos=(5.72425e-10,-544038,2.94608e-10) rot=(0,0,1;0rad)
  shape: bbox 10000 x 23.13 x 10000 mm, 1 faces, 0 solids (baked)
FEATURE [Part::Line] Normal_130
  AttacherType = Attacher::AttachEngine3D
  X1 = 0
  X2 = 0
  Y1 = 536909
  Y2 = 535909
  Z1 = 0
  Z2 = 0
FEATURE [Part::Line] Axis_1_130
  AttacherType = Attacher::AttachEngine3D
  X1 = 0
  X2 = 0
  Y1 = 536909
  Y2 = 536909
  Z1 = 0
  Z2 = -1000
FEATURE [Part::Line] Axis_2_130
  AttacherType = Attacher::AttachEngine3D
  X1 = 0
  X2 = -1000
  Y1 = 536909
  Y2 = 536909
  Z1 = 0
  Z2 = 0
FEATURE [Part::Feature] Heliostat_131  label="Heliostat_131(Mirror,Axis_1_131,Axis_2_131,Normal_131,Target_point)"
  Placement = pos=(217411,-391614,1.40591e-10) rot=(0,0,1;0rad)
  shape: bbox 10000 x 47.5 x 10000 mm, 1 faces, 0 solids (baked)
FEATURE [Part::Line] Normal_131
  AttacherType = Attacher::AttachEngine3D
  X1 = 217411
  X2 = 217411
  Y1 = 134733
  Y2 = 133733
  Z1 = 0
  Z2 = 0
FEATURE [Part::Line] Axis_1_131
  AttacherType = Attacher::AttachEngine3D
  X1 = 217411
  X2 = 217411
  Y1 = 134733
  Y2 = 134733
  Z1 = 0
  Z2 = -1000
FEATURE [Part::Line] Axis_2_131
  AttacherType = Attacher::AttachEngine3D
  X1 = 217411
  X2 = 216411
  Y1 = 134733
  Y2 = 134733
  Z1 = 0
  Z2 = 0
FEATURE [Part::Feature] Heliostat_132  label="Heliostat_132(Mirror,Axis_1_132,Axis_2_132,Normal_132,Target_point)"
  Placement = pos=(-217411,-391614,1.40591e-10) rot=(0,0,1;0rad)
  shape: bbox 10000 x 47.5 x 10000 mm, 1 faces, 0 solids (baked)
FEATURE [Part::Line] Normal_132
  AttacherType = Attacher::AttachEngine3D
  X1 = -217411
  X2 = -217411
  Y1 = 134733
  Y2 = 133733
  Z1 = 0
  Z2 = 0
FEATURE [Part::Line] Axis_1_132
  AttacherType = Attacher::AttachEngine3D
  X1 = -217411
  X2 = -217411
  Y1 = 134733
  Y2 = 134733
  Z1 = 0
  Z2 = -1000
FEATURE [Part::Line] Axis_2_132
  AttacherType = Attacher::AttachEngine3D
  X1 = -217411
  X2 = -218411
  Y1 = 134733
  Y2 = 134733
  Z1 = 0
  Z2 = 0
FEATURE [Part::Feature] Heliostat_133  label="Heliostat_133(Mirror,Axis_1_133,Axis_2_133,Normal_133,Target_point)"
  Placement = pos=(203689,-545092,9.48171e-11) rot=(0,0,1;0rad)
  shape: bbox 10000 x 25.14 x 10000 mm, 1 faces, 0 solids (baked)
FEATURE [Part::Line] Normal_133
  AttacherType = Attacher::AttachEngine3D
  X1 = 203689
  X2 = 203689
  Y1 = 449311
  Y2 = 448311
  Z1 = 0
  Z2 = 0
FEATURE [Part::Line] Axis_1_133
  AttacherType = Attacher::AttachEngine3D
  X1 = 203689
  X2 = 203689
  Y1 = 449311
  Y2 = 449311
  Z1 = 0
  Z2 = -1000
FEATURE [Part::Line] Axis_2_133
  AttacherType = Attacher::AttachEngine3D
  X1 = 203689
  X2 = 202689
  Y1 = 449311
  Y2 = 449311
  Z1 = 0
  Z2 = 0
FEATURE [Part::Feature] Heliostat_134  label="Heliostat_134(Mirror,Axis_1_134,Axis_2_134,Normal_134,Target_point)"
  Placement = pos=(-203689,-545092,9.48171e-11) rot=(0,0,1;0rad)
  shape: bbox 10000 x 25.14 x 10000 mm, 1 faces, 0 solids (baked)
FEATURE [Part::Line] Normal_134
  AttacherType = Attacher::AttachEngine3D
  X1 = -203689
  X2 = -203689
  Y1 = 449311
  Y2 = 448311
  Z1 = 0
  Z2 = 0
FEATURE [Part::Line] Axis_1_134
  AttacherType = Attacher::AttachEngine3D
  X1 = -203689
  X2 = -203689
  Y1 = 449311
  Y2 = 449311
  Z1 = 0
  Z2 = -1000
FEATURE [Part::Line] Axis_2_134
  AttacherType = Attacher::AttachEngine3D
  X1 = -203689
  X2 = -204689
  Y1 = 449311
  Y2 = 449311
  Z1 = 0
  Z2 = 0
FEATURE [Part::Feature] Heliostat_135  label="Heliostat_135(Mirror,Axis_1_135,Axis_2_135,Normal_135,Target_point)"
  Placement = pos=(197371,-361455,7.3208e-12) rot=(0,0,1;0rad)
  shape: bbox 10000 x 55.53 x 10000 mm, 1 faces, 0 solids (baked)
FEATURE [Part::Line] Normal_135
  AttacherType = Attacher::AttachEngine3D
  X1 = 197371
  X2 = 197371
  Y1 = 88765.2
  Y2 = 87765.2
  Z1 = 0
  Z2 = 0
FEATURE [Part::Line] Axis_1_135
  AttacherType = Attacher::AttachEngine3D
  X1 = 197371
  X2 = 197371
  Y1 = 88765.2
  Y2 = 88765.2
  Z1 = 0
  Z2 = -1000
FEATURE [Part::Line] Axis_2_135
  AttacherType = Attacher::AttachEngine3D
  X1 = 197371
  X2 = 196371
  Y1 = 88765.2
  Y2 = 88765.2
  Z1 = 0
  Z2 = 0
FEATURE [Part::Feature] Heliostat_136  label="Heliostat_136(Mirror,Axis_1_136,Axis_2_136,Normal_136,Target_point)"
  Placement = pos=(-197371,-361455,7.3208e-12) rot=(0,0,1;0rad)
  shape: bbox 10000 x 55.53 x 10000 mm, 1 faces, 0 solids (baked)
FEATURE [Part::Line] Normal_136
  AttacherType = Attacher::AttachEngine3D
  X1 = -197371
  X2 = -197371
  Y1 = 88765.2
  Y2 = 87765.2
  Z1 = 0
  Z2 = 0
FEATURE [Part::Line] Axis_1_136
  AttacherType = Attacher::AttachEngine3D
  X1 = -197371
  X2 = -197371
  Y1 = 88765.2
  Y2 = 88765.2
  Z1 = 0
  Z2 = -1000
FEATURE [Part::Line] Axis_2_136
  AttacherType = Attacher::AttachEngine3D
  X1 = -197371
  X2 = -198371
  Y1 = 88765.2
  Y2 = 88765.2
  Z1 = 0
  Z2 = 0
FEATURE [Part::Feature] Heliostat_137  label="Heliostat_137(Mirror,Axis_1_137,Axis_2_137,Normal_137,Target_point)"
  Placement = pos=(289264,-526974,1.43666e-10) rot=(0,0,1;0rad)
  shape: bbox 10000 x 31.86 x 10000 mm, 1 faces, 0 solids (baked)
FEATURE [Part::Line] Normal_137
  AttacherType = Attacher::AttachEngine3D
  X1 = 289264
  X2 = 289264
  Y1 = 257742
  Y2 = 256742
  Z1 = 0
  Z2 = 0
FEATURE [Part::Line] Axis_1_137
  AttacherType = Attacher::AttachEngine3D
  X1 = 289264
  X2 = 289264
  Y1 = 257742
  Y2 = 257742
  Z1 = 0
  Z2 = -1000
FEATURE [Part::Line] Axis_2_137
  AttacherType = Attacher::AttachEngine3D
  X1 = 289264
  X2 = 288264
  Y1 = 257742
  Y2 = 257742
  Z1 = 0
  Z2 = 0
FEATURE [Part::Feature] Heliostat_138  label="Heliostat_138(Mirror,Axis_1_138,Axis_2_138,Normal_138,Target_point)"
  Placement = pos=(-289264,-526974,1.43666e-10) rot=(0,0,1;0rad)
  shape: bbox 10000 x 31.86 x 10000 mm, 1 faces, 0 solids (baked)
FEATURE [Part::Line] Normal_138
  AttacherType = Attacher::AttachEngine3D
  X1 = -289264
  X2 = -289264
  Y1 = 257742
  Y2 = 256742
  Z1 = 0
  Z2 = 0
FEATURE [Part::Line] Axis_1_138
  AttacherType = Attacher::AttachEngine3D
  X1 = -289264
  X2 = -289264
  Y1 = 257742
  Y2 = 257742
  Z1 = 0
  Z2 = -1000
FEATURE [Part::Line] Axis_2_138
  AttacherType = Attacher::AttachEngine3D
  X1 = -289264
  X2 = -290264
  Y1 = 257742
  Y2 = 257742
  Z1 = 0
  Z2 = 0
FEATURE [Part::Feature] Heliostat_139  label="Heliostat_139(Mirror,Axis_1_139,Axis_2_139,Normal_139,Target_point)"
  Placement = pos=(78808.2,-186301,5.46924e-11) rot=(0,0,1;0rad)
  shape: bbox 10000 x 122.9 x 10000 mm, 1 faces, 0 solids (baked)
FEATURE [Part::Line] Normal_139
  AttacherType = Attacher::AttachEngine3D
  X1 = 78808.2
  X2 = 78808.2
  Y1 = 17100.2
  Y2 = 16100.2
  Z1 = 0
  Z2 = 0
FEATURE [Part::Line] Axis_1_139
  AttacherType = Attacher::AttachEngine3D
  X1 = 78808.2
  X2 = 78808.2
  Y1 = 17100.2
  Y2 = 17100.2
  Z1 = 0
  Z2 = -1000
FEATURE [Part::Line] Axis_2_139
  AttacherType = Attacher::AttachEngine3D
  X1 = 78808.2
  X2 = 77808.2
  Y1 = 17100.2
  Y2 = 17100.2
  Z1 = 0
  Z2 = 0
FEATURE [Part::Feature] Heliostat_140  label="Heliostat_140(Mirror,Axis_1_140,Axis_2_140,Normal_140,Target_point)"
  Placement = pos=(-78808.2,-186301,5.46924e-11) rot=(0,0,1;0rad)
  shape: bbox 10000 x 122.9 x 10000 mm, 1 faces, 0 solids (baked)
FEATURE [Part::Line] Normal_140
  AttacherType = Attacher::AttachEngine3D
  X1 = -78808.2
  X2 = -78808.2
  Y1 = 17100.2
  Y2 = 16100.2
  Z1 = 0
  Z2 = 0
FEATURE [Part::Line] Axis_1_140
  AttacherType = Attacher::AttachEngine3D
  X1 = -78808.2
  X2 = -78808.2
  Y1 = 17100.2
  Y2 = 17100.2
  Z1 = 0
  Z2 = -1000
FEATURE [Part::Line] Axis_2_140
  AttacherType = Attacher::AttachEngine3D
  X1 = -78808.2
  X2 = -79808.2
  Y1 = 17100.2
  Y2 = 17100.2
  Z1 = 0
  Z2 = 0
FEATURE [Part::Feature] Heliostat_141  label="Heliostat_141(Mirror,Axis_1_141,Axis_2_141,Normal_141,Target_point)"
  Placement = pos=(270764,-527402,2.28161e-10) rot=(0,0,1;0rad)
  shape: bbox 10000 x 29.51 x 10000 mm, 1 faces, 0 solids (baked)
FEATURE [Part::Line] Normal_141
  AttacherType = Attacher::AttachEngine3D
  X1 = 270764
  X2 = 270764
  Y1 = 319858
  Y2 = 318858
  Z1 = 0
  Z2 = 0
FEATURE [Part::Line] Axis_1_141
  AttacherType = Attacher::AttachEngine3D
  X1 = 270764
  X2 = 270764
  Y1 = 319858
  Y2 = 319858
  Z1 = 0
  Z2 = -1000
FEATURE [Part::Line] Axis_2_141
  AttacherType = Attacher::AttachEngine3D
  X1 = 270764
  X2 = 269764
  Y1 = 319858
  Y2 = 319858
  Z1 = 0
  Z2 = 0
FEATURE [Part::Feature] Heliostat_142  label="Heliostat_142(Mirror,Axis_1_142,Axis_2_142,Normal_142,Target_point)"
  Placement = pos=(-270764,-527402,2.28161e-10) rot=(0,0,1;0rad)
  shape: bbox 10000 x 29.51 x 10000 mm, 1 faces, 0 solids (baked)
FEATURE [Part::Line] Normal_142
  AttacherType = Attacher::AttachEngine3D
  X1 = -270764
  X2 = -270764
  Y1 = 319858
  Y2 = 318858
  Z1 = 0
  Z2 = 0
FEATURE [Part::Line] Axis_1_142
  AttacherType = Attacher::AttachEngine3D
  X1 = -270764
  X2 = -270764
  Y1 = 319858
  Y2 = 319858
  Z1 = 0
  Z2 = -1000
FEATURE [Part::Line] Axis_2_142
  AttacherType = Attacher::AttachEngine3D
  X1 = -270764
  X2 = -271764
  Y1 = 319858
  Y2 = 319858
  Z1 = 0
  Z2 = 0
FEATURE [Part::Feature] Heliostat_143  label="Heliostat_143(Mirror,Axis_1_143,Axis_2_143,Normal_143,Target_point)"
  Placement = pos=(242542,-433720,9.3684e-12) rot=(0,0,1;0rad)
  shape: bbox 10000 x 43.77 x 10000 mm, 1 faces, 0 solids (baked)
FEATURE [Part::Line] Normal_143
  AttacherType = Attacher::AttachEngine3D
  X1 = 242542
  X2 = 242542
  Y1 = 137494
  Y2 = 136494
  Z1 = 0
  Z2 = 0
FEATURE [Part::Line] Axis_1_143
  AttacherType = Attacher::AttachEngine3D
  X1 = 242542
  X2 = 242542
  Y1 = 137494
  Y2 = 137494
  Z1 = 0
  Z2 = -1000
FEATURE [Part::Line] Axis_2_143
  AttacherType = Attacher::AttachEngine3D
  X1 = 242542
  X2 = 241542
  Y1 = 137494
  Y2 = 137494
  Z1 = 0
  Z2 = 0
FEATURE [Part::Feature] Heliostat_144  label="Heliostat_144(Mirror,Axis_1_144,Axis_2_144,Normal_144,Target_point)"
  Placement = pos=(-242542,-433720,9.3684e-12) rot=(0,0,1;0rad)
  shape: bbox 10000 x 43.77 x 10000 mm, 1 faces, 0 solids (baked)
FEATURE [Part::Line] Normal_144
  AttacherType = Attacher::AttachEngine3D
  X1 = -242542
  X2 = -242542
  Y1 = 137494
  Y2 = 136494
  Z1 = 0
  Z2 = 0
FEATURE [Part::Line] Axis_1_144
  AttacherType = Attacher::AttachEngine3D
  X1 = -242542
  X2 = -242542
  Y1 = 137494
  Y2 = 137494
  Z1 = 0
  Z2 = -1000
FEATURE [Part::Line] Axis_2_144
  AttacherType = Attacher::AttachEngine3D
  X1 = -242542
  X2 = -243542
  Y1 = 137494
  Y2 = 137494
  Z1 = 0
  Z2 = 0
FEATURE [Part::Feature] Heliostat_145  label="Heliostat_145(Mirror,Axis_1_145,Axis_2_145,Normal_145,Target_point)"
  Placement = pos=(147680,-523701,9.48171e-11) rot=(0,0,1;0rad)
  shape: bbox 10000 x 25.14 x 10000 mm, 1 faces, 0 solids (baked)
FEATURE [Part::Line] Normal_145
  AttacherType = Attacher::AttachEngine3D
  X1 = 147680
  X2 = 147680
  Y1 = 470702
  Y2 = 469702
  Z1 = 0
  Z2 = 0
FEATURE [Part::Line] Axis_1_145
  AttacherType = Attacher::AttachEngine3D
  X1 = 147680
  X2 = 147680
  Y1 = 470702
  Y2 = 470702
  Z1 = 0
  Z2 = -1000
FEATURE [Part::Line] Axis_2_145
  AttacherType = Attacher::AttachEngine3D
  X1 = 147680
  X2 = 146680
  Y1 = 470702
  Y2 = 470702
  Z1 = 0
  Z2 = 0
FEATURE [Part::Feature] Heliostat_146  label="Heliostat_146(Mirror,Axis_1_146,Axis_2_146,Normal_146,Target_point)"
  Placement = pos=(-147680,-523701,9.48171e-11) rot=(0,0,1;0rad)
  shape: bbox 10000 x 25.14 x 10000 mm, 1 faces, 0 solids (baked)
FEATURE [Part::Line] Normal_146
  AttacherType = Attacher::AttachEngine3D
  X1 = -147680
  X2 = -147680
  Y1 = 470702
  Y2 = 469702
  Z1 = 0
  Z2 = 0
FEATURE [Part::Line] Axis_1_146
  AttacherType = Attacher::AttachEngine3D
  X1 = -147680
  X2 = -147680
  Y1 = 470702
  Y2 = 470702
  Z1 = 0
  Z2 = -1000
FEATURE [Part::Line] Axis_2_146
  AttacherType = Attacher::AttachEngine3D
  X1 = -147680
  X2 = -148680
  Y1 = 470702
  Y2 = 470702
  Z1 = 0
  Z2 = 0
FEATURE [Part::Feature] Heliostat_147  label="Heliostat_147(Mirror,Axis_1_147,Axis_2_147,Normal_147,Target_point)"
  Placement = pos=(209707,-379721,4.65379e-11) rot=(0,0,1;0rad)
  shape: bbox 10000 x 51.21 x 10000 mm, 1 faces, 0 solids (baked)
FEATURE [Part::Line] Normal_147
  AttacherType = Attacher::AttachEngine3D
  X1 = 209707
  X2 = 209707
  Y1 = 108459
  Y2 = 107459
  Z1 = 0
  Z2 = 0
FEATURE [Part::Line] Axis_1_147
  AttacherType = Attacher::AttachEngine3D
  X1 = 209707
  X2 = 209707
  Y1 = 108459
  Y2 = 108459
  Z1 = 0
  Z2 = -1000
FEATURE [Part::Line] Axis_2_147
  AttacherType = Attacher::AttachEngine3D
  X1 = 209707
  X2 = 208707
  Y1 = 108459
  Y2 = 108459
  Z1 = 0
  Z2 = 0
FEATURE [Part::Feature] Heliostat_148  label="Heliostat_148(Mirror,Axis_1_148,Axis_2_148,Normal_148,Target_point)"
  Placement = pos=(-209707,-379721,4.65379e-11) rot=(0,0,1;0rad)
  shape: bbox 10000 x 51.21 x 10000 mm, 1 faces, 0 solids (baked)
FEATURE [Part::Line] Normal_148
  AttacherType = Attacher::AttachEngine3D
  X1 = -209707
  X2 = -209707
  Y1 = 108459
  Y2 = 107459
  Z1 = 0
  Z2 = 0
FEATURE [Part::Line] Axis_1_148
  AttacherType = Attacher::AttachEngine3D
  X1 = -209707
  X2 = -209707
  Y1 = 108459
  Y2 = 108459
  Z1 = 0
  Z2 = -1000
FEATURE [Part::Line] Axis_2_148
  AttacherType = Attacher::AttachEngine3D
  X1 = -209707
  X2 = -210707
  Y1 = 108459
  Y2 = 108459
  Z1 = 0
  Z2 = 0
FEATURE [Part::Feature] Heliostat_149  label="Heliostat_149(Mirror,Axis_1_149,Axis_2_149,Normal_149,Target_point)"
  Placement = pos=(221022,-521694,2.39897e-10) rot=(0,0,1;0rad)
  shape: bbox 10000 x 27.15 x 10000 mm, 1 faces, 0 solids (baked)
FEATURE [Part::Line] Normal_149
  AttacherType = Attacher::AttachEngine3D
  X1 = 221022
  X2 = 221022
  Y1 = 399082
  Y2 = 398082
  Z1 = 0
  Z2 = 0
FEATURE [Part::Line] Axis_1_149
  AttacherType = Attacher::AttachEngine3D
  X1 = 221022
  X2 = 221022
  Y1 = 399082
  Y2 = 399082
  Z1 = 0
  Z2 = -1000
FEATURE [Part::Line] Axis_2_149
  AttacherType = Attacher::AttachEngine3D
  X1 = 221022
  X2 = 220022
  Y1 = 399082
  Y2 = 399082
  Z1 = 0
  Z2 = 0
FEATURE [Part::Feature] Heliostat_150  label="Heliostat_150(Mirror,Axis_1_150,Axis_2_150,Normal_150,Target_point)"
  Placement = pos=(-221022,-521694,2.39897e-10) rot=(0,0,1;0rad)
  shape: bbox 10000 x 27.15 x 10000 mm, 1 faces, 0 solids (baked)
FEATURE [Part::Line] Normal_150
  AttacherType = Attacher::AttachEngine3D
  X1 = -221022
  X2 = -221022
  Y1 = 399082
  Y2 = 398082
  Z1 = 0
  Z2 = 0
FEATURE [Part::Line] Axis_1_150
  AttacherType = Attacher::AttachEngine3D
  X1 = -221022
  X2 = -221022
  Y1 = 399082
  Y2 = 399082
  Z1 = 0
  Z2 = -1000
FEATURE [Part::Line] Axis_2_150
  AttacherType = Attacher::AttachEngine3D
  X1 = -221022
  X2 = -222022
  Y1 = 399082
  Y2 = 399082
  Z1 = 0
  Z2 = 0
FEATURE [Part::Feature] Heliostat_151  label="Heliostat_151(Mirror,Axis_1_151,Axis_2_151,Normal_151,Target_point)"
  Placement = pos=(144262,-278299,8.98539e-11) rot=(0,0,1;0rad)
  shape: bbox 10000 x 75.38 x 10000 mm, 1 faces, 0 solids (baked)
FEATURE [Part::Line] Normal_151
  AttacherType = Attacher::AttachEngine3D
  X1 = 144262
  X2 = 144262
  Y1 = 53345.5
  Y2 = 52345.5
  Z1 = 0
  Z2 = 0
FEATURE [Part::Line] Axis_1_151
  AttacherType = Attacher::AttachEngine3D
  X1 = 144262
  X2 = 144262
  Y1 = 53345.5
  Y2 = 53345.5
  Z1 = 0
  Z2 = -1000
FEATURE [Part::Line] Axis_2_151
  AttacherType = Attacher::AttachEngine3D
  X1 = 144262
  X2 = 143262
  Y1 = 53345.5
  Y2 = 53345.5
  Z1 = 0
  Z2 = 0
FEATURE [Part::Feature] Heliostat_152  label="Heliostat_152(Mirror,Axis_1_152,Axis_2_152,Normal_152,Target_point)"
  Placement = pos=(-144262,-278299,8.98539e-11) rot=(0,0,1;0rad)
  shape: bbox 10000 x 75.38 x 10000 mm, 1 faces, 0 solids (baked)
FEATURE [Part::Line] Normal_152
  AttacherType = Attacher::AttachEngine3D
  X1 = -144262
  X2 = -144262
  Y1 = 53345.5
  Y2 = 52345.5
  Z1 = 0
  Z2 = 0
FEATURE [Part::Line] Axis_1_152
  AttacherType = Attacher::AttachEngine3D
  X1 = -144262
  X2 = -144262
  Y1 = 53345.5
  Y2 = 53345.5
  Z1 = 0
  Z2 = -1000
FEATURE [Part::Line] Axis_2_152
  AttacherType = Attacher::AttachEngine3D
  X1 = -144262
  X2 = -145262
  Y1 = 53345.5
  Y2 = 53345.5
  Z1 = 0
  Z2 = 0
FEATURE [Part::Feature] Heliostat_153  label="Heliostat_153(Mirror,Axis_1_153,Axis_2_153,Normal_153,Target_point)"
  Placement = pos=(252371,-512698,9.08762e-11) rot=(0,0,1;0rad)
  shape: bbox 10000 x 29.51 x 10000 mm, 1 faces, 0 solids (baked)
FEATURE [Part::Line] Normal_153
  AttacherType = Attacher::AttachEngine3D
  X1 = 252371
  X2 = 252371
  Y1 = 334561
  Y2 = 333561
  Z1 = 0
  Z2 = 0
FEATURE [Part::Line] Axis_1_153
  AttacherType = Attacher::AttachEngine3D
  X1 = 252371
  X2 = 252371
  Y1 = 334561
  Y2 = 334561
  Z1 = 0
  Z2 = -1000
FEATURE [Part::Line] Axis_2_153
  AttacherType = Attacher::AttachEngine3D
  X1 = 252371
  X2 = 251371
  Y1 = 334561
  Y2 = 334561
  Z1 = 0
  Z2 = 0
FEATURE [Part::Feature] Heliostat_154  label="Heliostat_154(Mirror,Axis_1_154,Axis_2_154,Normal_154,Target_point)"
  Placement = pos=(-252371,-512698,9.08762e-11) rot=(0,0,1;0rad)
  shape: bbox 10000 x 29.51 x 10000 mm, 1 faces, 0 solids (baked)
FEATURE [Part::Line] Normal_154
  AttacherType = Attacher::AttachEngine3D
  X1 = -252371
  X2 = -252371
  Y1 = 334561
  Y2 = 333561
  Z1 = 0
  Z2 = 0
FEATURE [Part::Line] Axis_1_154
  AttacherType = Attacher::AttachEngine3D
  X1 = -252371
  X2 = -252371
  Y1 = 334561
  Y2 = 334561
  Z1 = 0
  Z2 = -1000
FEATURE [Part::Line] Axis_2_154
  AttacherType = Attacher::AttachEngine3D
  X1 = -252371
  X2 = -253371
  Y1 = 334561
  Y2 = 334561
  Z1 = 0
  Z2 = 0
FEATURE [Part::Feature] Heliostat_155  label="Heliostat_155(Mirror,Axis_1_155,Axis_2_155,Normal_155,Target_point)"
  Placement = pos=(89020.3,-377823,1.97655e-10) rot=(0,0,1;0rad)
  shape: bbox 10000 x 34.61 x 10000 mm, 1 faces, 0 solids (baked)
FEATURE [Part::Line] Normal_155
  AttacherType = Attacher::AttachEngine3D
  X1 = 89020.3
  X2 = 89020.3
  Y1 = 344478
  Y2 = 343478
  Z1 = 0
  Z2 = 0
FEATURE [Part::Line] Axis_1_155
  AttacherType = Attacher::AttachEngine3D
  X1 = 89020.3
  X2 = 89020.3
  Y1 = 344478
  Y2 = 344478
  Z1 = 0
  Z2 = -1000
FEATURE [Part::Line] Axis_2_155
  AttacherType = Attacher::AttachEngine3D
  X1 = 89020.3
  X2 = 88020.3
  Y1 = 344478
  Y2 = 344478
  Z1 = 0
  Z2 = 0
FEATURE [Part::Feature] Heliostat_156  label="Heliostat_156(Mirror,Axis_1_156,Axis_2_156,Normal_156,Target_point)"
  Placement = pos=(-89020.3,-377823,1.97655e-10) rot=(0,0,1;0rad)
  shape: bbox 10000 x 34.61 x 10000 mm, 1 faces, 0 solids (baked)
FEATURE [Part::Line] Normal_156
  AttacherType = Attacher::AttachEngine3D
  X1 = -89020.3
  X2 = -89020.3
  Y1 = 344478
  Y2 = 343478
  Z1 = 0
  Z2 = 0
FEATURE [Part::Line] Axis_1_156
  AttacherType = Attacher::AttachEngine3D
  X1 = -89020.3
  X2 = -89020.3
  Y1 = 344478
  Y2 = 344478
  Z1 = 0
  Z2 = -1000
FEATURE [Part::Line] Axis_2_156
  AttacherType = Attacher::AttachEngine3D
  X1 = -89020.3
  X2 = -90020.3
  Y1 = 344478
  Y2 = 344478
  Z1 = 0
  Z2 = 0
FEATURE [Part::Feature] Heliostat_157  label="Heliostat_157(Mirror,Axis_1_157,Axis_2_157,Normal_157,Target_point)"
  Placement = pos=(198258,-509910,2.39897e-10) rot=(0,0,1;0rad)
  shape: bbox 10000 x 27.15 x 10000 mm, 1 faces, 0 solids (baked)
FEATURE [Part::Line] Normal_157
  AttacherType = Attacher::AttachEngine3D
  X1 = 198258
  X2 = 198258
  Y1 = 410866
  Y2 = 409866
  Z1 = 0
  Z2 = 0
FEATURE [Part::Line] Axis_1_157
  AttacherType = Attacher::AttachEngine3D
  X1 = 198258
  X2 = 198258
  Y1 = 410866
  Y2 = 410866
  Z1 = 0
  Z2 = -1000
FEATURE [Part::Line] Axis_2_157
  AttacherType = Attacher::AttachEngine3D
  X1 = 198258
  X2 = 197258
  Y1 = 410866
  Y2 = 410866
  Z1 = 0
  Z2 = 0
FEATURE [Part::Feature] Heliostat_158  label="Heliostat_158(Mirror,Axis_1_158,Axis_2_158,Normal_158,Target_point)"
  Placement = pos=(-198258,-509910,2.39897e-10) rot=(0,0,1;0rad)
  shape: bbox 10000 x 27.15 x 10000 mm, 1 faces, 0 solids (baked)
FEATURE [Part::Line] Normal_158
  AttacherType = Attacher::AttachEngine3D
  X1 = -198258
  X2 = -198258
  Y1 = 410866
  Y2 = 409866
  Z1 = 0
  Z2 = 0
FEATURE [Part::Line] Axis_1_158
  AttacherType = Attacher::AttachEngine3D
  X1 = -198258
  X2 = -198258
  Y1 = 410866
  Y2 = 410866
  Z1 = 0
  Z2 = -1000
FEATURE [Part::Line] Axis_2_158
  AttacherType = Attacher::AttachEngine3D
  X1 = -198258
  X2 = -199258
  Y1 = 410866
  Y2 = 410866
  Z1 = 0
  Z2 = 0
FEATURE [Part::Feature] Heliostat_159  label="Heliostat_159(Mirror,Axis_1_159,Axis_2_159,Normal_159,Target_point)"
  Placement = pos=(274331,-511133,7.33721e-11) rot=(0,0,1;0rad)
  shape: bbox 10000 x 31.86 x 10000 mm, 1 faces, 0 solids (baked)
FEATURE [Part::Line] Normal_159
  AttacherType = Attacher::AttachEngine3D
  X1 = 274331
  X2 = 274331
  Y1 = 273583
  Y2 = 272583
  Z1 = 0
  Z2 = 0
FEATURE [Part::Line] Axis_1_159
  AttacherType = Attacher::AttachEngine3D
  X1 = 274331
  X2 = 274331
  Y1 = 273583
  Y2 = 273583
  Z1 = 0
  Z2 = -1000
FEATURE [Part::Line] Axis_2_159
  AttacherType = Attacher::AttachEngine3D
  X1 = 274331
  X2 = 273331
  Y1 = 273583
  Y2 = 273583
  Z1 = 0
  Z2 = 0
FEATURE [Part::Feature] Heliostat_160  label="Heliostat_160(Mirror,Axis_1_160,Axis_2_160,Normal_160,Target_point)"
  Placement = pos=(-274331,-511133,7.33721e-11) rot=(0,0,1;0rad)
  shape: bbox 10000 x 31.86 x 10000 mm, 1 faces, 0 solids (baked)
FEATURE [Part::Line] Normal_160
  AttacherType = Attacher::AttachEngine3D
  X1 = -274331
  X2 = -274331
  Y1 = 273583
  Y2 = 272583
  Z1 = 0
  Z2 = 0
FEATURE [Part::Line] Axis_1_160
  AttacherType = Attacher::AttachEngine3D
  X1 = -274331
  X2 = -274331
  Y1 = 273583
  Y2 = 273583
  Z1 = 0
  Z2 = -1000
FEATURE [Part::Line] Axis_2_160
  AttacherType = Attacher::AttachEngine3D
  X1 = -274331
  X2 = -275331
  Y1 = 273583
  Y2 = 273583
  Z1 = 0
  Z2 = 0
FEATURE [Part::Feature] Heliostat_161  label="Heliostat_161(Mirror,Axis_1_161,Axis_2_161,Normal_161,Target_point)"
  Placement = pos=(243089,-534739,2.4056e-10) rot=(0,0,1;0rad)
  shape: bbox 10000 x 27.15 x 10000 mm, 1 faces, 0 solids (baked)
FEATURE [Part::Line] Normal_161
  AttacherType = Attacher::AttachEngine3D
  X1 = 243089
  X2 = 243089
  Y1 = 386038
  Y2 = 385038
  Z1 = 0
  Z2 = 0
FEATURE [Part::Line] Axis_1_161
  AttacherType = Attacher::AttachEngine3D
  X1 = 243089
  X2 = 243089
  Y1 = 386038
  Y2 = 386038
  Z1 = 0
  Z2 = -1000
FEATURE [Part::Line] Axis_2_161
  AttacherType = Attacher::AttachEngine3D
  X1 = 243089
  X2 = 242089
  Y1 = 386038
  Y2 = 386038
  Z1 = 0
  Z2 = 0
FEATURE [Part::Feature] Heliostat_162  label="Heliostat_162(Mirror,Axis_1_162,Axis_2_162,Normal_162,Target_point)"
  Placement = pos=(-243089,-534739,2.4056e-10) rot=(0,0,1;0rad)
  shape: bbox 10000 x 27.15 x 10000 mm, 1 faces, 0 solids (baked)
FEATURE [Part::Line] Normal_162
  AttacherType = Attacher::AttachEngine3D
  X1 = -243089
  X2 = -243089
  Y1 = 386038
  Y2 = 385038
  Z1 = 0
  Z2 = 0
FEATURE [Part::Line] Axis_1_162
  AttacherType = Attacher::AttachEngine3D
  X1 = -243089
  X2 = -243089
  Y1 = 386038
  Y2 = 386038
  Z1 = 0
  Z2 = -1000
FEATURE [Part::Line] Axis_2_162
  AttacherType = Attacher::AttachEngine3D
  X1 = -243089
  X2 = -244089
  Y1 = 386038
  Y2 = 386038
  Z1 = 0
  Z2 = 0
FEATURE [Part::Feature] Heliostat_163  label="Heliostat_163(Mirror,Axis_1_163,Axis_2_163,Normal_163,Target_point)"
  Placement = pos=(257318,-464494,6.19852e-11) rot=(0,0,1;0rad)
  shape: bbox 10000 x 37.36 x 10000 mm, 1 faces, 0 solids (baked)
FEATURE [Part::Line] Normal_163
  AttacherType = Attacher::AttachEngine3D
  X1 = 257318
  X2 = 257318
  Y1 = 204710
  Y2 = 203710
  Z1 = 0
  Z2 = 0
FEATURE [Part::Line] Axis_1_163
  AttacherType = Attacher::AttachEngine3D
  X1 = 257318
  X2 = 257318
  Y1 = 204710
  Y2 = 204710
  Z1 = 0
  Z2 = -1000
FEATURE [Part::Line] Axis_2_163
  AttacherType = Attacher::AttachEngine3D
  X1 = 257318
  X2 = 256318
  Y1 = 204710
  Y2 = 204710
  Z1 = 0
  Z2 = 0
FEATURE [Part::Feature] Heliostat_164  label="Heliostat_164(Mirror,Axis_1_164,Axis_2_164,Normal_164,Target_point)"
  Placement = pos=(-257318,-464494,6.19852e-11) rot=(0,0,1;0rad)
  shape: bbox 10000 x 37.36 x 10000 mm, 1 faces, 0 solids (baked)
FEATURE [Part::Line] Normal_164
  AttacherType = Attacher::AttachEngine3D
  X1 = -257318
  X2 = -257318
  Y1 = 204710
  Y2 = 203710
  Z1 = 0
  Z2 = 0
FEATURE [Part::Line] Axis_1_164
  AttacherType = Attacher::AttachEngine3D
  X1 = -257318
  X2 = -257318
  Y1 = 204710
  Y2 = 204710
  Z1 = 0
  Z2 = -1000
FEATURE [Part::Line] Axis_2_164
  AttacherType = Attacher::AttachEngine3D
  X1 = -257318
  X2 = -258318
  Y1 = 204710
  Y2 = 204710
  Z1 = 0
  Z2 = 0
FEATURE [Part::Feature] Heliostat_165  label="Heliostat_165(Mirror,Axis_1_165,Axis_2_165,Normal_165,Target_point)"
  Placement = pos=(9997.95,-501179,2.66794e-10) rot=(0,0,1;0rad)
  shape: bbox 10000 x 25.14 x 10000 mm, 1 faces, 0 solids (baked)
FEATURE [Part::Line] Normal_165
  AttacherType = Attacher::AttachEngine3D
  X1 = 9997.95
  X2 = 9997.95
  Y1 = 493223
  Y2 = 492223
  Z1 = 0
  Z2 = 0
FEATURE [Part::Line] Axis_1_165
  AttacherType = Attacher::AttachEngine3D
  X1 = 9997.95
  X2 = 9997.95
  Y1 = 493223
  Y2 = 493223
  Z1 = 0
  Z2 = -1000
FEATURE [Part::Line] Axis_2_165
  AttacherType = Attacher::AttachEngine3D
  X1 = 9997.95
  X2 = 8997.95
  Y1 = 493223
  Y2 = 493223
  Z1 = 0
  Z2 = 0
FEATURE [Part::Feature] Heliostat_166  label="Heliostat_166(Mirror,Axis_1_166,Axis_2_166,Normal_166,Target_point)"
  Placement = pos=(-9997.95,-501179,2.66794e-10) rot=(0,0,1;0rad)
  shape: bbox 10000 x 25.14 x 10000 mm, 1 faces, 0 solids (baked)
FEATURE [Part::Line] Normal_166
  AttacherType = Attacher::AttachEngine3D
  X1 = -9997.95
  X2 = -9997.95
  Y1 = 493223
  Y2 = 492223
  Z1 = 0
  Z2 = 0
FEATURE [Part::Line] Axis_1_166
  AttacherType = Attacher::AttachEngine3D
  X1 = -9997.95
  X2 = -9997.95
  Y1 = 493223
  Y2 = 493223
  Z1 = 0
  Z2 = -1000
FEATURE [Part::Line] Axis_2_166
  AttacherType = Attacher::AttachEngine3D
  X1 = -9997.95
  X2 = -10997.9
  Y1 = 493223
  Y2 = 493223
  Z1 = 0
  Z2 = 0
FEATURE [Part::Feature] Heliostat_167  label="Heliostat_167(Mirror,Axis_1_167,Axis_2_167,Normal_167,Target_point)"
  Placement = pos=(9985.06,-203435,1.39932e-10) rot=(0,0,1;0rad)
  shape: bbox 10000 x 64.79 x 10000 mm, 1 faces, 0 solids (baked)
FEATURE [Part::Line] Normal_167
  AttacherType = Attacher::AttachEngine3D
  X1 = 9985.06
  X2 = 9985.06
  Y1 = 182446
  Y2 = 181446
  Z1 = 0
  Z2 = 0
FEATURE [Part::Line] Axis_1_167
  AttacherType = Attacher::AttachEngine3D
  X1 = 9985.06
  X2 = 9985.06
  Y1 = 182446
  Y2 = 182446
  Z1 = 0
  Z2 = -1000
FEATURE [Part::Line] Axis_2_167
  AttacherType = Attacher::AttachEngine3D
  X1 = 9985.06
  X2 = 8985.06
  Y1 = 182446
  Y2 = 182446
  Z1 = 0
  Z2 = 0
FEATURE [Part::Feature] Heliostat_168  label="Heliostat_168(Mirror,Axis_1_168,Axis_2_168,Normal_168,Target_point)"
  Placement = pos=(-9985.06,-203435,1.39932e-10) rot=(0,0,1;0rad)
  shape: bbox 10000 x 64.79 x 10000 mm, 1 faces, 0 solids (baked)
FEATURE [Part::Line] Normal_168
  AttacherType = Attacher::AttachEngine3D
  X1 = -9985.06
  X2 = -9985.06
  Y1 = 182446
  Y2 = 181446
  Z1 = 0
  Z2 = 0
FEATURE [Part::Line] Axis_1_168
  AttacherType = Attacher::AttachEngine3D
  X1 = -9985.06
  X2 = -9985.06
  Y1 = 182446
  Y2 = 182446
  Z1 = 0
  Z2 = -1000
FEATURE [Part::Line] Axis_2_168
  AttacherType = Attacher::AttachEngine3D
  X1 = -9985.06
  X2 = -10985.1
  Y1 = 182446
  Y2 = 182446
  Z1 = 0
  Z2 = 0
FEATURE [Part::Feature] Heliostat_169  label="Heliostat_169(Mirror,Axis_1_169,Axis_2_169,Normal_169,Target_point)"
  Placement = pos=(231067,-415203,5.24243e-11) rot=(0,0,1;0rad)
  shape: bbox 10000 x 43.77 x 10000 mm, 1 faces, 0 solids (baked)
FEATURE [Part::Line] Normal_169
  AttacherType = Attacher::AttachEngine3D
  X1 = 231067
  X2 = 231067
  Y1 = 156011
  Y2 = 155011
  Z1 = 0
  Z2 = 0
FEATURE [Part::Line] Axis_1_169
  AttacherType = Attacher::AttachEngine3D
  X1 = 231067
  X2 = 231067
  Y1 = 156011
  Y2 = 156011
  Z1 = 0
  Z2 = -1000
FEATURE [Part::Line] Axis_2_169
  AttacherType = Attacher::AttachEngine3D
  X1 = 231067
  X2 = 230067
  Y1 = 156011
  Y2 = 156011
  Z1 = 0
  Z2 = 0
FEATURE [Part::Feature] Heliostat_170  label="Heliostat_170(Mirror,Axis_1_170,Axis_2_170,Normal_170,Target_point)"
  Placement = pos=(-231067,-415203,5.24243e-11) rot=(0,0,1;0rad)
  shape: bbox 10000 x 43.77 x 10000 mm, 1 faces, 0 solids (baked)
FEATURE [Part::Line] Normal_170
  AttacherType = Attacher::AttachEngine3D
  X1 = -231067
  X2 = -231067
  Y1 = 156011
  Y2 = 155011
  Z1 = 0
  Z2 = 0
FEATURE [Part::Line] Axis_1_170
  AttacherType = Attacher::AttachEngine3D
  X1 = -231067
  X2 = -231067
  Y1 = 156011
  Y2 = 156011
  Z1 = 0
  Z2 = -1000
FEATURE [Part::Line] Axis_2_170
  AttacherType = Attacher::AttachEngine3D
  X1 = -231067
  X2 = -232067
  Y1 = 156011
  Y2 = 156011
  Z1 = 0
  Z2 = 0
FEATURE [Part::Feature] Heliostat_171  label="Heliostat_171(Mirror,Axis_1_171,Axis_2_171,Normal_171,Target_point)"
  Placement = pos=(258531,-496157,1.10204e-11) rot=(0,0,1;0rad)
  shape: bbox 10000 x 31.86 x 10000 mm, 1 faces, 0 solids (baked)
FEATURE [Part::Line] Normal_171
  AttacherType = Attacher::AttachEngine3D
  X1 = 258531
  X2 = 258531
  Y1 = 288559
  Y2 = 287559
  Z1 = 0
  Z2 = 0
FEATURE [Part::Line] Axis_1_171
  AttacherType = Attacher::AttachEngine3D
  X1 = 258531
  X2 = 258531
  Y1 = 288559
  Y2 = 288559
  Z1 = 0
  Z2 = -1000
FEATURE [Part::Line] Axis_2_171
  AttacherType = Attacher::AttachEngine3D
  X1 = 258531
  X2 = 257531
  Y1 = 288559
  Y2 = 288559
  Z1 = 0
  Z2 = 0
FEATURE [Part::Feature] Heliostat_172  label="Heliostat_172(Mirror,Axis_1_172,Axis_2_172,Normal_172,Target_point)"
  Placement = pos=(-258531,-496157,1.10204e-11) rot=(0,0,1;0rad)
  shape: bbox 10000 x 31.86 x 10000 mm, 1 faces, 0 solids (baked)
FEATURE [Part::Line] Normal_172
  AttacherType = Attacher::AttachEngine3D
  X1 = -258531
  X2 = -258531
  Y1 = 288559
  Y2 = 287559
  Z1 = 0
  Z2 = 0
FEATURE [Part::Line] Axis_1_172
  AttacherType = Attacher::AttachEngine3D
  X1 = -258531
  X2 = -258531
  Y1 = 288559
  Y2 = 288559
  Z1 = 0
  Z2 = -1000
FEATURE [Part::Line] Axis_2_172
  AttacherType = Attacher::AttachEngine3D
  X1 = -258531
  X2 = -259531
  Y1 = 288559
  Y2 = 288559
  Z1 = 0
  Z2 = 0
FEATURE [Part::Feature] Heliostat_173  label="Heliostat_173(Mirror,Axis_1_173,Axis_2_173,Normal_173,Target_point)"
  Placement = pos=(174867,-499423,8.39512e-11) rot=(0,0,1;0rad)
  shape: bbox 10000 x 27.15 x 10000 mm, 1 faces, 0 solids (baked)
FEATURE [Part::Line] Normal_173
  AttacherType = Attacher::AttachEngine3D
  X1 = 174867
  X2 = 174867
  Y1 = 421354
  Y2 = 420354
  Z1 = 0
  Z2 = 0
FEATURE [Part::Line] Axis_1_173
  AttacherType = Attacher::AttachEngine3D
  X1 = 174867
  X2 = 174867
  Y1 = 421354
  Y2 = 421354
  Z1 = 0
  Z2 = -1000
FEATURE [Part::Line] Axis_2_173
  AttacherType = Attacher::AttachEngine3D
  X1 = 174867
  X2 = 173867
  Y1 = 421354
  Y2 = 421354
  Z1 = 0
  Z2 = 0
FEATURE [Part::Feature] Heliostat_174  label="Heliostat_174(Mirror,Axis_1_174,Axis_2_174,Normal_174,Target_point)"
  Placement = pos=(-174867,-499423,8.39512e-11) rot=(0,0,1;0rad)
  shape: bbox 10000 x 27.15 x 10000 mm, 1 faces, 0 solids (baked)
FEATURE [Part::Line] Normal_174
  AttacherType = Attacher::AttachEngine3D
  X1 = -174867
  X2 = -174867
  Y1 = 421354
  Y2 = 420354
  Z1 = 0
  Z2 = 0
FEATURE [Part::Line] Axis_1_174
  AttacherType = Attacher::AttachEngine3D
  X1 = -174867
  X2 = -174867
  Y1 = 421354
  Y2 = 421354
  Z1 = 0
  Z2 = -1000
FEATURE [Part::Line] Axis_2_174
  AttacherType = Attacher::AttachEngine3D
  X1 = -174867
  X2 = -175867
  Y1 = 421354
  Y2 = 421354
  Z1 = 0
  Z2 = 0
FEATURE [Part::Feature] Heliostat_175  label="Heliostat_175(Mirror,Axis_1_175,Axis_2_175,Normal_175,Target_point)"
  Placement = pos=(243364,-437715,6.26794e-11) rot=(0,0,1;0rad)
  shape: bbox 10000 x 40.57 x 10000 mm, 1 faces, 0 solids (baked)
FEATURE [Part::Line] Normal_175
  AttacherType = Attacher::AttachEngine3D
  X1 = 243364
  X2 = 243364
  Y1 = 178541
  Y2 = 177541
  Z1 = 0
  Z2 = 0
FEATURE [Part::Line] Axis_1_175
  AttacherType = Attacher::AttachEngine3D
  X1 = 243364
  X2 = 243364
  Y1 = 178541
  Y2 = 178541
  Z1 = 0
  Z2 = -1000
FEATURE [Part::Line] Axis_2_175
  AttacherType = Attacher::AttachEngine3D
  X1 = 243364
  X2 = 242364
  Y1 = 178541
  Y2 = 178541
  Z1 = 0
  Z2 = 0
FEATURE [Part::Feature] Heliostat_176  label="Heliostat_176(Mirror,Axis_1_176,Axis_2_176,Normal_176,Target_point)"
  Placement = pos=(-243364,-437715,6.26794e-11) rot=(0,0,1;0rad)
  shape: bbox 10000 x 40.57 x 10000 mm, 1 faces, 0 solids (baked)
FEATURE [Part::Line] Normal_176
  AttacherType = Attacher::AttachEngine3D
  X1 = -243364
  X2 = -243364
  Y1 = 178541
  Y2 = 177541
  Z1 = 0
  Z2 = 0
FEATURE [Part::Line] Axis_1_176
  AttacherType = Attacher::AttachEngine3D
  X1 = -243364
  X2 = -243364
  Y1 = 178541
  Y2 = 178541
  Z1 = 0
  Z2 = -1000
FEATURE [Part::Line] Axis_2_176
  AttacherType = Attacher::AttachEngine3D
  X1 = -243364
  X2 = -244364
  Y1 = 178541
  Y2 = 178541
  Z1 = 0
  Z2 = 0
FEATURE [Part::Feature] Heliostat_177  label="Heliostat_177(Mirror,Axis_1_177,Axis_2_177,Normal_177,Target_point)"
  Placement = pos=(233181,-499051,2.2786e-10) rot=(0,0,1;0rad)
  shape: bbox 10000 x 29.51 x 10000 mm, 1 faces, 0 solids (baked)
FEATURE [Part::Line] Normal_177
  AttacherType = Attacher::AttachEngine3D
  X1 = 233181
  X2 = 233181
  Y1 = 348208
  Y2 = 347208
  Z1 = 0
  Z2 = 0
FEATURE [Part::Line] Axis_1_177
  AttacherType = Attacher::AttachEngine3D
  X1 = 233181
  X2 = 233181
  Y1 = 348208
  Y2 = 348208
  Z1 = 0
  Z2 = -1000
FEATURE [Part::Line] Axis_2_177
  AttacherType = Attacher::AttachEngine3D
  X1 = 233181
  X2 = 232181
  Y1 = 348208
  Y2 = 348208
  Z1 = 0
  Z2 = 0
FEATURE [Part::Feature] Heliostat_178  label="Heliostat_178(Mirror,Axis_1_178,Axis_2_178,Normal_178,Target_point)"
  Placement = pos=(-233181,-499051,2.2786e-10) rot=(0,0,1;0rad)
  shape: bbox 10000 x 29.51 x 10000 mm, 1 faces, 0 solids (baked)
FEATURE [Part::Line] Normal_178
  AttacherType = Attacher::AttachEngine3D
  X1 = -233181
  X2 = -233181
  Y1 = 348208
  Y2 = 347208
  Z1 = 0
  Z2 = 0
FEATURE [Part::Line] Axis_1_178
  AttacherType = Attacher::AttachEngine3D
  X1 = -233181
  X2 = -233181
  Y1 = 348208
  Y2 = 348208
  Z1 = 0
  Z2 = -1000
FEATURE [Part::Line] Axis_2_178
  AttacherType = Attacher::AttachEngine3D
  X1 = -233181
  X2 = -234181
  Y1 = 348208
  Y2 = 348208
  Z1 = 0
  Z2 = 0
FEATURE [Part::Feature] Heliostat_179  label="Heliostat_179(Mirror,Axis_1_179,Axis_2_179,Normal_179,Target_point)"
  Placement = pos=(150925,-490266,3.21893e-10) rot=(0,0,1;0rad)
  shape: bbox 10000 x 27.15 x 10000 mm, 1 faces, 0 solids (baked)
FEATURE [Part::Line] Normal_179
  AttacherType = Attacher::AttachEngine3D
  X1 = 150925
  X2 = 150925
  Y1 = 430510
  Y2 = 429510
  Z1 = 0
  Z2 = 0
FEATURE [Part::Line] Axis_1_179
  AttacherType = Attacher::AttachEngine3D
  X1 = 150925
  X2 = 150925
  Y1 = 430510
  Y2 = 430510
  Z1 = 0
  Z2 = -1000
FEATURE [Part::Line] Axis_2_179
  AttacherType = Attacher::AttachEngine3D
  X1 = 150925
  X2 = 149925
  Y1 = 430510
  Y2 = 430510
  Z1 = 0
  Z2 = 0
FEATURE [Part::Feature] Heliostat_180  label="Heliostat_180(Mirror,Axis_1_180,Axis_2_180,Normal_180,Target_point)"
  Placement = pos=(-150925,-490266,3.21893e-10) rot=(0,0,1;0rad)
  shape: bbox 10000 x 27.15 x 10000 mm, 1 faces, 0 solids (baked)
FEATURE [Part::Line] Normal_180
  AttacherType = Attacher::AttachEngine3D
  X1 = -150925
  X2 = -150925
  Y1 = 430510
  Y2 = 429510
  Z1 = 0
  Z2 = 0
FEATURE [Part::Line] Axis_1_180
  AttacherType = Attacher::AttachEngine3D
  X1 = -150925
  X2 = -150925
  Y1 = 430510
  Y2 = 430510
  Z1 = 0
  Z2 = -1000
FEATURE [Part::Line] Axis_2_180
  AttacherType = Attacher::AttachEngine3D
  X1 = -150925
  X2 = -151925
  Y1 = 430510
  Y2 = 430510
  Z1 = 0
  Z2 = 0
FEATURE [Part::Feature] Heliostat_181  label="Heliostat_181(Mirror,Axis_1_181,Axis_2_181,Normal_181,Target_point)"
  Placement = pos=(69755.9,-506034,3.50694e-10) rot=(0,0,1;0rad)
  shape: bbox 10000 x 25.14 x 10000 mm, 1 faces, 0 solids (baked)
FEATURE [Part::Line] Normal_181
  AttacherType = Attacher::AttachEngine3D
  X1 = 69755.9
  X2 = 69755.9
  Y1 = 488368
  Y2 = 487368
  Z1 = 0
  Z2 = 0
FEATURE [Part::Line] Axis_1_181
  AttacherType = Attacher::AttachEngine3D
  X1 = 69755.9
  X2 = 69755.9
  Y1 = 488368
  Y2 = 488368
  Z1 = 0
  Z2 = -1000
FEATURE [Part::Line] Axis_2_181
  AttacherType = Attacher::AttachEngine3D
  X1 = 69755.9
  X2 = 68755.9
  Y1 = 488368
  Y2 = 488368
  Z1 = 0
  Z2 = 0
FEATURE [Part::Feature] Heliostat_182  label="Heliostat_182(Mirror,Axis_1_182,Axis_2_182,Normal_182,Target_point)"
  Placement = pos=(-69755.9,-506034,3.50694e-10) rot=(0,0,1;0rad)
  shape: bbox 10000 x 25.14 x 10000 mm, 1 faces, 0 solids (baked)
FEATURE [Part::Line] Normal_182
  AttacherType = Attacher::AttachEngine3D
  X1 = -69755.9
  X2 = -69755.9
  Y1 = 488368
  Y2 = 487368
  Z1 = 0
  Z2 = 0
FEATURE [Part::Line] Axis_1_182
  AttacherType = Attacher::AttachEngine3D
  X1 = -69755.9
  X2 = -69755.9
  Y1 = 488368
  Y2 = 488368
  Z1 = 0
  Z2 = -1000
FEATURE [Part::Line] Axis_2_182
  AttacherType = Attacher::AttachEngine3D
  X1 = -69755.9
  X2 = -70755.9
  Y1 = 488368
  Y2 = 488368
  Z1 = 0
  Z2 = 0
FEATURE [Part::Feature] Heliostat_183  label="Heliostat_183(Mirror,Axis_1_183,Axis_2_183,Normal_183,Target_point)"
  Placement = pos=(241915,-482091,2.08325e-10) rot=(0,0,1;0rad)
  shape: bbox 10000 x 31.86 x 10000 mm, 1 faces, 0 solids (baked)
FEATURE [Part::Line] Normal_183
  AttacherType = Attacher::AttachEngine3D
  X1 = 241915
  X2 = 241915
  Y1 = 302625
  Y2 = 301625
  Z1 = 0
  Z2 = 0
FEATURE [Part::Line] Axis_1_183
  AttacherType = Attacher::AttachEngine3D
  X1 = 241915
  X2 = 241915
  Y1 = 302625
  Y2 = 302625
  Z1 = 0
  Z2 = -1000
FEATURE [Part::Line] Axis_2_183
  AttacherType = Attacher::AttachEngine3D
  X1 = 241915
  X2 = 240915
  Y1 = 302625
  Y2 = 302625
  Z1 = 0
  Z2 = 0
FEATURE [Part::Feature] Heliostat_184  label="Heliostat_184(Mirror,Axis_1_184,Axis_2_184,Normal_184,Target_point)"
  Placement = pos=(-241915,-482091,2.08325e-10) rot=(0,0,1;0rad)
  shape: bbox 10000 x 31.86 x 10000 mm, 1 faces, 0 solids (baked)
FEATURE [Part::Line] Normal_184
  AttacherType = Attacher::AttachEngine3D
  X1 = -241915
  X2 = -241915
  Y1 = 302625
  Y2 = 301625
  Z1 = 0
  Z2 = 0
FEATURE [Part::Line] Axis_1_184
  AttacherType = Attacher::AttachEngine3D
  X1 = -241915
  X2 = -241915
  Y1 = 302625
  Y2 = 302625
  Z1 = 0
  Z2 = -1000
FEATURE [Part::Line] Axis_2_184
  AttacherType = Attacher::AttachEngine3D
  X1 = -241915
  X2 = -242915
  Y1 = 302625
  Y2 = 302625
  Z1 = 0
  Z2 = 0
FEATURE [Part::Feature] Heliostat_185  label="Heliostat_185(Mirror,Axis_1_185,Axis_2_185,Normal_185,Target_point)"
  Placement = pos=(213255,-486504,3.36922e-10) rot=(0,0,1;0rad)
  shape: bbox 10000 x 29.51 x 10000 mm, 1 faces, 0 solids (baked)
FEATURE [Part::Line] Normal_185
  AttacherType = Attacher::AttachEngine3D
  X1 = 213255
  X2 = 213255
  Y1 = 360755
  Y2 = 359755
  Z1 = 0
  Z2 = 0
FEATURE [Part::Line] Axis_1_185
  AttacherType = Attacher::AttachEngine3D
  X1 = 213255
  X2 = 213255
  Y1 = 360755
  Y2 = 360755
  Z1 = 0
  Z2 = -1000
FEATURE [Part::Line] Axis_2_185
  AttacherType = Attacher::AttachEngine3D
  X1 = 213255
  X2 = 212255
  Y1 = 360755
  Y2 = 360755
  Z1 = 0
  Z2 = 0
FEATURE [Part::Feature] Heliostat_186  label="Heliostat_186(Mirror,Axis_1_186,Axis_2_186,Normal_186,Target_point)"
  Placement = pos=(-213255,-486504,3.36922e-10) rot=(0,0,1;0rad)
  shape: bbox 10000 x 29.51 x 10000 mm, 1 faces, 0 solids (baked)
FEATURE [Part::Line] Normal_186
  AttacherType = Attacher::AttachEngine3D
  X1 = -213255
  X2 = -213255
  Y1 = 360755
  Y2 = 359755
  Z1 = 0
  Z2 = 0
FEATURE [Part::Line] Axis_1_186
  AttacherType = Attacher::AttachEngine3D
  X1 = -213255
  X2 = -213255
  Y1 = 360755
  Y2 = 360755
  Z1 = 0
  Z2 = -1000
FEATURE [Part::Line] Axis_2_186
  AttacherType = Attacher::AttachEngine3D
  X1 = -213255
  X2 = -214255
  Y1 = 360755
  Y2 = 360755
  Z1 = 0
  Z2 = 0
FEATURE [Part::Feature] Heliostat_187  label="Heliostat_187(Mirror,Axis_1_187,Axis_2_187,Normal_187,Target_point)"
  Placement = pos=(149701,-318958,1.86587e-10) rot=(0,0,1;0rad)
  shape: bbox 10000 x 47.5 x 10000 mm, 1 faces, 0 solids (baked)
FEATURE [Part::Line] Normal_187
  AttacherType = Attacher::AttachEngine3D
  X1 = 149701
  X2 = 149701
  Y1 = 207389
  Y2 = 206389
  Z1 = 0
  Z2 = 0
FEATURE [Part::Line] Axis_1_187
  AttacherType = Attacher::AttachEngine3D
  X1 = 149701
  X2 = 149701
  Y1 = 207389
  Y2 = 207389
  Z1 = 0
  Z2 = -1000
FEATURE [Part::Line] Axis_2_187
  AttacherType = Attacher::AttachEngine3D
  X1 = 149701
  X2 = 148701
  Y1 = 207389
  Y2 = 207389
  Z1 = 0
  Z2 = 0
FEATURE [Part::Feature] Heliostat_188  label="Heliostat_188(Mirror,Axis_1_188,Axis_2_188,Normal_188,Target_point)"
  Placement = pos=(-149701,-318958,1.86587e-10) rot=(0,0,1;0rad)
  shape: bbox 10000 x 47.5 x 10000 mm, 1 faces, 0 solids (baked)
FEATURE [Part::Line] Normal_188
  AttacherType = Attacher::AttachEngine3D
  X1 = -149701
  X2 = -149701
  Y1 = 207389
  Y2 = 206389
  Z1 = 0
  Z2 = 0
FEATURE [Part::Line] Axis_1_188
  AttacherType = Attacher::AttachEngine3D
  X1 = -149701
  X2 = -149701
  Y1 = 207389
  Y2 = 207389
  Z1 = 0
  Z2 = -1000
FEATURE [Part::Line] Axis_2_188
  AttacherType = Attacher::AttachEngine3D
  X1 = -149701
  X2 = -150701
  Y1 = 207389
  Y2 = 207389
  Z1 = 0
  Z2 = 0
FEATURE [Part::Feature] Heliostat_189  label="Heliostat_189(Mirror,Axis_1_189,Axis_2_189,Normal_189,Target_point)"
  Placement = pos=(51166.5,-467456,8.43523e-11) rot=(0,0,1;0rad)
  shape: bbox 10000 x 27.15 x 10000 mm, 1 faces, 0 solids (baked)
FEATURE [Part::Line] Normal_189
  AttacherType = Attacher::AttachEngine3D
  X1 = 51166.5
  X2 = 51166.5
  Y1 = 453320
  Y2 = 452320
  Z1 = 0
  Z2 = 0
FEATURE [Part::Line] Axis_1_189
  AttacherType = Attacher::AttachEngine3D
  X1 = 51166.5
  X2 = 51166.5
  Y1 = 453320
  Y2 = 453320
  Z1 = 0
  Z2 = -1000
FEATURE [Part::Line] Axis_2_189
  AttacherType = Attacher::AttachEngine3D
  X1 = 51166.5
  X2 = 50166.5
  Y1 = 453320
  Y2 = 453320
  Z1 = 0
  Z2 = 0
FEATURE [Part::Feature] Heliostat_190  label="Heliostat_190(Mirror,Axis_1_190,Axis_2_190,Normal_190,Target_point)"
  Placement = pos=(-51166.5,-467456,8.43523e-11) rot=(0,0,1;0rad)
  shape: bbox 10000 x 27.15 x 10000 mm, 1 faces, 0 solids (baked)
FEATURE [Part::Line] Normal_190
  AttacherType = Attacher::AttachEngine3D
  X1 = -51166.5
  X2 = -51166.5
  Y1 = 453320
  Y2 = 452320
  Z1 = 0
  Z2 = 0
FEATURE [Part::Line] Axis_1_190
  AttacherType = Attacher::AttachEngine3D
  X1 = -51166.5
  X2 = -51166.5
  Y1 = 453320
  Y2 = 453320
  Z1 = 0
  Z2 = -1000
FEATURE [Part::Line] Axis_2_190
  AttacherType = Attacher::AttachEngine3D
  X1 = -51166.5
  X2 = -52166.5
  Y1 = 453320
  Y2 = 453320
  Z1 = 0
  Z2 = 0
FEATURE [Part::Feature] Heliostat_191  label="Heliostat_191(Mirror,Axis_1_191,Axis_2_191,Normal_191,Target_point)"
  Placement = pos=(192656,-475095,1.54673e-10) rot=(0,0,1;0rad)
  shape: bbox 10000 x 29.51 x 10000 mm, 1 faces, 0 solids (baked)
FEATURE [Part::Line] Normal_191
  AttacherType = Attacher::AttachEngine3D
  X1 = 192656
  X2 = 192656
  Y1 = 372164
  Y2 = 371164
  Z1 = 0
  Z2 = 0
FEATURE [Part::Line] Axis_1_191
  AttacherType = Attacher::AttachEngine3D
  X1 = 192656
  X2 = 192656
  Y1 = 372164
  Y2 = 372164
  Z1 = 0
  Z2 = -1000
FEATURE [Part::Line] Axis_2_191
  AttacherType = Attacher::AttachEngine3D
  X1 = 192656
  X2 = 191656
  Y1 = 372164
  Y2 = 372164
  Z1 = 0
  Z2 = 0
FEATURE [Part::Feature] Heliostat_192  label="Heliostat_192(Mirror,Axis_1_192,Axis_2_192,Normal_192,Target_point)"
  Placement = pos=(-192656,-475095,1.54673e-10) rot=(0,0,1;0rad)
  shape: bbox 10000 x 29.51 x 10000 mm, 1 faces, 0 solids (baked)
FEATURE [Part::Line] Normal_192
  AttacherType = Attacher::AttachEngine3D
  X1 = -192656
  X2 = -192656
  Y1 = 372164
  Y2 = 371164
  Z1 = 0
  Z2 = 0
FEATURE [Part::Line] Axis_1_192
  AttacherType = Attacher::AttachEngine3D
  X1 = -192656
  X2 = -192656
  Y1 = 372164
  Y2 = 372164
  Z1 = 0
  Z2 = -1000
FEATURE [Part::Line] Axis_2_192
  AttacherType = Attacher::AttachEngine3D
  X1 = -192656
  X2 = -193656
  Y1 = 372164
  Y2 = 372164
  Z1 = 0
  Z2 = 0
FEATURE [Part::Feature] Heliostat_193  label="Heliostat_193(Mirror,Axis_1_193,Axis_2_193,Normal_193,Target_point)"
  Placement = pos=(240549,-445028,1.19225e-10) rot=(0,0,1;0rad)
  shape: bbox 10000 x 37.36 x 10000 mm, 1 faces, 0 solids (baked)
FEATURE [Part::Line] Normal_193
  AttacherType = Attacher::AttachEngine3D
  X1 = 240549
  X2 = 240549
  Y1 = 224175
  Y2 = 223175
  Z1 = 0
  Z2 = 0
FEATURE [Part::Line] Axis_1_193
  AttacherType = Attacher::AttachEngine3D
  X1 = 240549
  X2 = 240549
  Y1 = 224175
  Y2 = 224175
  Z1 = 0
  Z2 = -1000
FEATURE [Part::Line] Axis_2_193
  AttacherType = Attacher::AttachEngine3D
  X1 = 240549
  X2 = 239549
  Y1 = 224175
  Y2 = 224175
  Z1 = 0
  Z2 = 0
FEATURE [Part::Feature] Heliostat_194  label="Heliostat_194(Mirror,Axis_1_194,Axis_2_194,Normal_194,Target_point)"
  Placement = pos=(-240549,-445028,1.19225e-10) rot=(0,0,1;0rad)
  shape: bbox 10000 x 37.36 x 10000 mm, 1 faces, 0 solids (baked)
FEATURE [Part::Line] Normal_194
  AttacherType = Attacher::AttachEngine3D
  X1 = -240549
  X2 = -240549
  Y1 = 224175
  Y2 = 223175
  Z1 = 0
  Z2 = 0
FEATURE [Part::Line] Axis_1_194
  AttacherType = Attacher::AttachEngine3D
  X1 = -240549
  X2 = -240549
  Y1 = 224175
  Y2 = 224175
  Z1 = 0
  Z2 = -1000
FEATURE [Part::Line] Axis_2_194
  AttacherType = Attacher::AttachEngine3D
  X1 = -240549
  X2 = -241549
  Y1 = 224175
  Y2 = 224175
  Z1 = 0
  Z2 = 0
FEATURE [Part::Feature] Heliostat_195  label="Heliostat_195(Mirror,Axis_1_195,Axis_2_195,Normal_195,Target_point)"
  Placement = pos=(25623.7,-465298,2.3998e-10) rot=(0,0,1;0rad)
  shape: bbox 10000 x 27.15 x 10000 mm, 1 faces, 0 solids (baked)
FEATURE [Part::Line] Normal_195
  AttacherType = Attacher::AttachEngine3D
  X1 = 25623.7
  X2 = 25623.7
  Y1 = 455479
  Y2 = 454479
  Z1 = 0
  Z2 = 0
FEATURE [Part::Line] Axis_1_195
  AttacherType = Attacher::AttachEngine3D
  X1 = 25623.7
  X2 = 25623.7
  Y1 = 455479
  Y2 = 455479
  Z1 = 0
  Z2 = -1000
FEATURE [Part::Line] Axis_2_195
  AttacherType = Attacher::AttachEngine3D
  X1 = 25623.7
  X2 = 24623.7
  Y1 = 455479
  Y2 = 455479
  Z1 = 0
  Z2 = 0
FEATURE [Part::Feature] Heliostat_196  label="Heliostat_196(Mirror,Axis_1_196,Axis_2_196,Normal_196,Target_point)"
  Placement = pos=(-25623.7,-465298,2.3998e-10) rot=(0,0,1;0rad)
  shape: bbox 10000 x 27.15 x 10000 mm, 1 faces, 0 solids (baked)
FEATURE [Part::Line] Normal_196
  AttacherType = Attacher::AttachEngine3D
  X1 = -25623.7
  X2 = -25623.7
  Y1 = 455479
  Y2 = 454479
  Z1 = 0
  Z2 = 0
FEATURE [Part::Line] Axis_1_196
  AttacherType = Attacher::AttachEngine3D
  X1 = -25623.7
  X2 = -25623.7
  Y1 = 455479
  Y2 = 455479
  Z1 = 0
  Z2 = -1000
FEATURE [Part::Line] Axis_2_196
  AttacherType = Attacher::AttachEngine3D
  X1 = -25623.7
  X2 = -26623.7
  Y1 = 455479
  Y2 = 455479
  Z1 = 0
  Z2 = 0
FEATURE [Part::Feature] Heliostat_197  label="Heliostat_197(Mirror,Axis_1_197,Axis_2_197,Normal_197,Target_point)"
  Placement = pos=(4.14308e-11,-464577,1.69358e-10) rot=(0,0,1;0rad)
  shape: bbox 10000 x 27.15 x 10000 mm, 1 faces, 0 solids (baked)
FEATURE [Part::Line] Normal_197
  AttacherType = Attacher::AttachEngine3D
  X1 = 0
  X2 = 0
  Y1 = 456199
  Y2 = 455199
  Z1 = 0
  Z2 = 0
FEATURE [Part::Line] Axis_1_197
  AttacherType = Attacher::AttachEngine3D
  X1 = 0
  X2 = 0
  Y1 = 456199
  Y2 = 456199
  Z1 = 0
  Z2 = -1000
FEATURE [Part::Line] Axis_2_197
  AttacherType = Attacher::AttachEngine3D
  X1 = 0
  X2 = -1000
  Y1 = 456199
  Y2 = 456199
  Z1 = 0
  Z2 = 0
FEATURE [Part::Feature] Heliostat_198  label="Heliostat_198(Mirror,Axis_1_198,Axis_2_198,Normal_198,Target_point)"
  Placement = pos=(133608,-261242,3.73906e-11) rot=(0,0,1;0rad)
  shape: bbox 10000 x 64.79 x 10000 mm, 1 faces, 0 solids (baked)
FEATURE [Part::Line] Normal_198
  AttacherType = Attacher::AttachEngine3D
  X1 = 133608
  X2 = 133608
  Y1 = 124639
  Y2 = 123639
  Z1 = 0
  Z2 = 0
FEATURE [Part::Line] Axis_1_198
  AttacherType = Attacher::AttachEngine3D
  X1 = 133608
  X2 = 133608
  Y1 = 124639
  Y2 = 124639
  Z1 = 0
  Z2 = -1000
FEATURE [Part::Line] Axis_2_198
  AttacherType = Attacher::AttachEngine3D
  X1 = 133608
  X2 = 132608
  Y1 = 124639
  Y2 = 124639
  Z1 = 0
  Z2 = 0
FEATURE [Part::Feature] Heliostat_199  label="Heliostat_199(Mirror,Axis_1_199,Axis_2_199,Normal_199,Target_point)"
  Placement = pos=(-133608,-261242,3.73906e-11) rot=(0,0,1;0rad)
  shape: bbox 10000 x 64.79 x 10000 mm, 1 faces, 0 solids (baked)
FEATURE [Part::Line] Normal_199
  AttacherType = Attacher::AttachEngine3D
  X1 = -133608
  X2 = -133608
  Y1 = 124639
  Y2 = 123639
  Z1 = 0
  Z2 = 0
FEATURE [Part::Line] Axis_1_199
  AttacherType = Attacher::AttachEngine3D
  X1 = -133608
  X2 = -133608
  Y1 = 124639
  Y2 = 124639
  Z1 = 0
  Z2 = -1000
FEATURE [Part::Line] Axis_2_199
  AttacherType = Attacher::AttachEngine3D
  X1 = -133608
  X2 = -134608
  Y1 = 124639
  Y2 = 124639
  Z1 = 0
  Z2 = 0
FEATURE [Part::Feature] Heliostat_200  label="Heliostat_200(Mirror,Axis_1_200,Axis_2_200,Normal_200,Target_point)"
  Placement = pos=(177261,-326251,4.05393e-11) rot=(0,0,1;0rad)
  shape: bbox 10000 x 59.82 x 10000 mm, 1 faces, 0 solids (baked)
FEATURE [Part::Line] Normal_200
  AttacherType = Attacher::AttachEngine3D
  X1 = 177261
  X2 = 177261
  Y1 = 91678.8
  Y2 = 90678.8
  Z1 = 0
  Z2 = 0
FEATURE [Part::Line] Axis_1_200
  AttacherType = Attacher::AttachEngine3D
  X1 = 177261
  X2 = 177261
  Y1 = 91678.8
  Y2 = 91678.8
  Z1 = 0
  Z2 = -1000
FEATURE [Part::Line] Axis_2_200
  AttacherType = Attacher::AttachEngine3D
  X1 = 177261
  X2 = 176261
  Y1 = 91678.8
  Y2 = 91678.8
  Z1 = 0
  Z2 = 0
FEATURE [Part::Feature] Heliostat_201  label="Heliostat_201(Mirror,Axis_1_201,Axis_2_201,Normal_201,Target_point)"
  Placement = pos=(-177261,-326251,4.05393e-11) rot=(0,0,1;0rad)
  shape: bbox 10000 x 59.82 x 10000 mm, 1 faces, 0 solids (baked)
FEATURE [Part::Line] Normal_201
  AttacherType = Attacher::AttachEngine3D
  X1 = -177261
  X2 = -177261
  Y1 = 91678.8
  Y2 = 90678.8
  Z1 = 0
  Z2 = 0
FEATURE [Part::Line] Axis_1_201
  AttacherType = Attacher::AttachEngine3D
  X1 = -177261
  X2 = -177261
  Y1 = 91678.8
  Y2 = 91678.8
  Z1 = 0
  Z2 = -1000
FEATURE [Part::Line] Axis_2_201
  AttacherType = Attacher::AttachEngine3D
  X1 = -177261
  X2 = -178261
  Y1 = 91678.8
  Y2 = 91678.8
  Z1 = 0
  Z2 = 0
FEATURE [Part::Feature] Heliostat_202  label="Heliostat_202(Mirror,Axis_1_202,Axis_2_202,Normal_202,Target_point)"
  Placement = pos=(152159,-286787,6.51989e-11) rot=(0,0,1;0rad)
  shape: bbox 10000 x 69.71 x 10000 mm, 1 faces, 0 solids (baked)
FEATURE [Part::Line] Normal_202
  AttacherType = Attacher::AttachEngine3D
  X1 = 152159
  X2 = 152159
  Y1 = 71836
  Y2 = 70836
  Z1 = 0
  Z2 = 0
FEATURE [Part::Line] Axis_1_202
  AttacherType = Attacher::AttachEngine3D
  X1 = 152159
  X2 = 152159
  Y1 = 71836
  Y2 = 71836
  Z1 = 0
  Z2 = -1000
FEATURE [Part::Line] Axis_2_202
  AttacherType = Attacher::AttachEngine3D
  X1 = 152159
  X2 = 151159
  Y1 = 71836
  Y2 = 71836
  Z1 = 0
  Z2 = 0
FEATURE [Part::Feature] Heliostat_203  label="Heliostat_203(Mirror,Axis_1_203,Axis_2_203,Normal_203,Target_point)"
  Placement = pos=(-152159,-286787,6.51989e-11) rot=(0,0,1;0rad)
  shape: bbox 10000 x 69.71 x 10000 mm, 1 faces, 0 solids (baked)
FEATURE [Part::Line] Normal_203
  AttacherType = Attacher::AttachEngine3D
  X1 = -152159
  X2 = -152159
  Y1 = 71836
  Y2 = 70836
  Z1 = 0
  Z2 = 0
FEATURE [Part::Line] Axis_1_203
  AttacherType = Attacher::AttachEngine3D
  X1 = -152159
  X2 = -152159
  Y1 = 71836
  Y2 = 71836
  Z1 = 0
  Z2 = -1000
FEATURE [Part::Line] Axis_2_203
  AttacherType = Attacher::AttachEngine3D
  X1 = -152159
  X2 = -153159
  Y1 = 71836
  Y2 = 71836
  Z1 = 0
  Z2 = 0
FEATURE [Part::Feature] Heliostat_204  label="Heliostat_204(Mirror,Axis_1_204,Axis_2_204,Normal_204,Target_point)"
  Placement = pos=(186505,-340446,4.16514e-11) rot=(0,0,1;0rad)
  shape: bbox 10000 x 55.53 x 10000 mm, 1 faces, 0 solids (baked)
FEATURE [Part::Line] Normal_204
  AttacherType = Attacher::AttachEngine3D
  X1 = 186505
  X2 = 186505
  Y1 = 109774
  Y2 = 108774
  Z1 = 0
  Z2 = 0
FEATURE [Part::Line] Axis_1_204
  AttacherType = Attacher::AttachEngine3D
  X1 = 186505
  X2 = 186505
  Y1 = 109774
  Y2 = 109774
  Z1 = 0
  Z2 = -1000
FEATURE [Part::Line] Axis_2_204
  AttacherType = Attacher::AttachEngine3D
  X1 = 186505
  X2 = 185505
  Y1 = 109774
  Y2 = 109774
  Z1 = 0
  Z2 = 0
FEATURE [Part::Feature] Heliostat_205  label="Heliostat_205(Mirror,Axis_1_205,Axis_2_205,Normal_205,Target_point)"
  Placement = pos=(-186505,-340446,4.16514e-11) rot=(0,0,1;0rad)
  shape: bbox 10000 x 55.53 x 10000 mm, 1 faces, 0 solids (baked)
FEATURE [Part::Line] Normal_205
  AttacherType = Attacher::AttachEngine3D
  X1 = -186505
  X2 = -186505
  Y1 = 109774
  Y2 = 108774
  Z1 = 0
  Z2 = 0
FEATURE [Part::Line] Axis_1_205
  AttacherType = Attacher::AttachEngine3D
  X1 = -186505
  X2 = -186505
  Y1 = 109774
  Y2 = 109774
  Z1 = 0
  Z2 = -1000
FEATURE [Part::Line] Axis_2_205
  AttacherType = Attacher::AttachEngine3D
  X1 = -186505
  X2 = -187505
  Y1 = 109774
  Y2 = 109774
  Z1 = 0
  Z2 = 0
FEATURE [Part::Feature] Heliostat_206  label="Heliostat_206(Mirror,Axis_1_206,Axis_2_206,Normal_206,Target_point)"
  Placement = pos=(228682,-419259,1.69118e-10) rot=(0,0,1;0rad)
  shape: bbox 10000 x 40.57 x 10000 mm, 1 faces, 0 solids (baked)
FEATURE [Part::Line] Normal_206
  AttacherType = Attacher::AttachEngine3D
  X1 = 228682
  X2 = 228682
  Y1 = 196997
  Y2 = 195997
  Z1 = 0
  Z2 = 0
FEATURE [Part::Line] Axis_1_206
  AttacherType = Attacher::AttachEngine3D
  X1 = 228682
  X2 = 228682
  Y1 = 196997
  Y2 = 196997
  Z1 = 0
  Z2 = -1000
FEATURE [Part::Line] Axis_2_206
  AttacherType = Attacher::AttachEngine3D
  X1 = 228682
  X2 = 227682
  Y1 = 196997
  Y2 = 196997
  Z1 = 0
  Z2 = 0
FEATURE [Part::Feature] Heliostat_207  label="Heliostat_207(Mirror,Axis_1_207,Axis_2_207,Normal_207,Target_point)"
  Placement = pos=(-228682,-419259,1.69118e-10) rot=(0,0,1;0rad)
  shape: bbox 10000 x 40.57 x 10000 mm, 1 faces, 0 solids (baked)
FEATURE [Part::Line] Normal_207
  AttacherType = Attacher::AttachEngine3D
  X1 = -228682
  X2 = -228682
  Y1 = 196997
  Y2 = 195997
  Z1 = 0
  Z2 = 0
FEATURE [Part::Line] Axis_1_207
  AttacherType = Attacher::AttachEngine3D
  X1 = -228682
  X2 = -228682
  Y1 = 196997
  Y2 = 196997
  Z1 = 0
  Z2 = -1000
FEATURE [Part::Line] Axis_2_207
  AttacherType = Attacher::AttachEngine3D
  X1 = -228682
  X2 = -229682
  Y1 = 196997
  Y2 = 196997
  Z1 = 0
  Z2 = 0
FEATURE [Part::Feature] Heliostat_208  label="Heliostat_208(Mirror,Axis_1_208,Axis_2_208,Normal_208,Target_point)"
  Placement = pos=(229880,-450741,2.54381e-10) rot=(0,0,1;0rad)
  shape: bbox 10000 x 34.61 x 10000 mm, 1 faces, 0 solids (baked)
FEATURE [Part::Line] Normal_208
  AttacherType = Attacher::AttachEngine3D
  X1 = 229880
  X2 = 229880
  Y1 = 271560
  Y2 = 270560
  Z1 = 0
  Z2 = 0
FEATURE [Part::Line] Axis_1_208
  AttacherType = Attacher::AttachEngine3D
  X1 = 229880
  X2 = 229880
  Y1 = 271560
  Y2 = 271560
  Z1 = 0
  Z2 = -1000
FEATURE [Part::Line] Axis_2_208
  AttacherType = Attacher::AttachEngine3D
  X1 = 229880
  X2 = 228880
  Y1 = 271560
  Y2 = 271560
  Z1 = 0
  Z2 = 0
FEATURE [Part::Feature] Heliostat_209  label="Heliostat_209(Mirror,Axis_1_209,Axis_2_209,Normal_209,Target_point)"
  Placement = pos=(-229880,-450741,2.54381e-10) rot=(0,0,1;0rad)
  shape: bbox 10000 x 34.61 x 10000 mm, 1 faces, 0 solids (baked)
FEATURE [Part::Line] Normal_209
  AttacherType = Attacher::AttachEngine3D
  X1 = -229880
  X2 = -229880
  Y1 = 271560
  Y2 = 270560
  Z1 = 0
  Z2 = 0
FEATURE [Part::Line] Axis_1_209
  AttacherType = Attacher::AttachEngine3D
  X1 = -229880
  X2 = -229880
  Y1 = 271560
  Y2 = 271560
  Z1 = 0
  Z2 = -1000
FEATURE [Part::Line] Axis_2_209
  AttacherType = Attacher::AttachEngine3D
  X1 = -229880
  X2 = -230880
  Y1 = 271560
  Y2 = 271560
  Z1 = 0
  Z2 = 0
FEATURE [Part::Feature] Heliostat_210  label="Heliostat_210(Mirror,Axis_1_210,Axis_2_210,Normal_210,Target_point)"
  Placement = pos=(126506,-482469,1.69358e-10) rot=(0,0,1;0rad)
  shape: bbox 10000 x 27.15 x 10000 mm, 1 faces, 0 solids (baked)
FEATURE [Part::Line] Normal_210
  AttacherType = Attacher::AttachEngine3D
  X1 = 126506
  X2 = 126506
  Y1 = 438308
  Y2 = 437308
  Z1 = 0
  Z2 = 0
FEATURE [Part::Line] Axis_1_210
  AttacherType = Attacher::AttachEngine3D
  X1 = 126506
  X2 = 126506
  Y1 = 438308
  Y2 = 438308
  Z1 = 0
  Z2 = -1000
FEATURE [Part::Line] Axis_2_210
  AttacherType = Attacher::AttachEngine3D
  X1 = 126506
  X2 = 125506
  Y1 = 438308
  Y2 = 438308
  Z1 = 0
  Z2 = 0
FEATURE [Part::Feature] Heliostat_211  label="Heliostat_211(Mirror,Axis_1_211,Axis_2_211,Normal_211,Target_point)"
  Placement = pos=(-126506,-482469,1.69358e-10) rot=(0,0,1;0rad)
  shape: bbox 10000 x 27.15 x 10000 mm, 1 faces, 0 solids (baked)
FEATURE [Part::Line] Normal_211
  AttacherType = Attacher::AttachEngine3D
  X1 = -126506
  X2 = -126506
  Y1 = 438308
  Y2 = 437308
  Z1 = 0
  Z2 = 0
FEATURE [Part::Line] Axis_1_211
  AttacherType = Attacher::AttachEngine3D
  X1 = -126506
  X2 = -126506
  Y1 = 438308
  Y2 = 438308
  Z1 = 0
  Z2 = -1000
FEATURE [Part::Line] Axis_2_211
  AttacherType = Attacher::AttachEngine3D
  X1 = -126506
  X2 = -127506
  Y1 = 438308
  Y2 = 438308
  Z1 = 0
  Z2 = 0
FEATURE [Part::Feature] Heliostat_212  label="Heliostat_212(Mirror,Axis_1_212,Axis_2_212,Normal_212,Target_point)"
  Placement = pos=(149699,-455835,2.1959e-10) rot=(0,0,1;0rad)
  shape: bbox 10000 x 29.51 x 10000 mm, 1 faces, 0 solids (baked)
FEATURE [Part::Line] Normal_212
  AttacherType = Attacher::AttachEngine3D
  X1 = 149699
  X2 = 149699
  Y1 = 391424
  Y2 = 390424
  Z1 = 0
  Z2 = 0
FEATURE [Part::Line] Axis_1_212
  AttacherType = Attacher::AttachEngine3D
  X1 = 149699
  X2 = 149699
  Y1 = 391424
  Y2 = 391424
  Z1 = 0
  Z2 = -1000
FEATURE [Part::Line] Axis_2_212
  AttacherType = Attacher::AttachEngine3D
  X1 = 149699
  X2 = 148699
  Y1 = 391424
  Y2 = 391424
  Z1 = 0
  Z2 = 0
FEATURE [Part::Feature] Heliostat_213  label="Heliostat_213(Mirror,Axis_1_213,Axis_2_213,Normal_213,Target_point)"
  Placement = pos=(-149699,-455835,2.1959e-10) rot=(0,0,1;0rad)
  shape: bbox 10000 x 29.51 x 10000 mm, 1 faces, 0 solids (baked)
FEATURE [Part::Line] Normal_213
  AttacherType = Attacher::AttachEngine3D
  X1 = -149699
  X2 = -149699
  Y1 = 391424
  Y2 = 390424
  Z1 = 0
  Z2 = 0
FEATURE [Part::Line] Axis_1_213
  AttacherType = Attacher::AttachEngine3D
  X1 = -149699
  X2 = -149699
  Y1 = 391424
  Y2 = 391424
  Z1 = 0
  Z2 = -1000
FEATURE [Part::Line] Axis_2_213
  AttacherType = Attacher::AttachEngine3D
  X1 = -149699
  X2 = -150699
  Y1 = 391424
  Y2 = 391424
  Z1 = 0
  Z2 = 0
FEATURE [Part::Feature] Heliostat_214  label="Heliostat_214(Mirror,Axis_1_214,Axis_2_214,Normal_214,Target_point)"
  Placement = pos=(120924,-241374,5.28103e-11) rot=(0,0,1;0rad)
  shape: bbox 10000 x 87.39 x 10000 mm, 1 faces, 0 solids (baked)
FEATURE [Part::Line] Normal_214
  AttacherType = Attacher::AttachEngine3D
  X1 = 120924
  X2 = 120924
  Y1 = 44715.5
  Y2 = 43715.5
  Z1 = 0
  Z2 = 0
FEATURE [Part::Line] Axis_1_214
  AttacherType = Attacher::AttachEngine3D
  X1 = 120924
  X2 = 120924
  Y1 = 44715.5
  Y2 = 44715.5
  Z1 = 0
  Z2 = -1000
FEATURE [Part::Line] Axis_2_214
  AttacherType = Attacher::AttachEngine3D
  X1 = 120924
  X2 = 119924
  Y1 = 44715.5
  Y2 = 44715.5
  Z1 = 0
  Z2 = 0
FEATURE [Part::Feature] Heliostat_215  label="Heliostat_215(Mirror,Axis_1_215,Axis_2_215,Normal_215,Target_point)"
  Placement = pos=(-120924,-241374,5.28103e-11) rot=(0,0,1;0rad)
  shape: bbox 10000 x 87.39 x 10000 mm, 1 faces, 0 solids (baked)
FEATURE [Part::Line] Normal_215
  AttacherType = Attacher::AttachEngine3D
  X1 = -120924
  X2 = -120924
  Y1 = 44715.5
  Y2 = 43715.5
  Z1 = 0
  Z2 = 0
FEATURE [Part::Line] Axis_1_215
  AttacherType = Attacher::AttachEngine3D
  X1 = -120924
  X2 = -120924
  Y1 = 44715.5
  Y2 = 44715.5
  Z1 = 0
  Z2 = -1000
FEATURE [Part::Line] Axis_2_215
  AttacherType = Attacher::AttachEngine3D
  X1 = -120924
  X2 = -121924
  Y1 = 44715.5
  Y2 = 44715.5
  Z1 = 0
  Z2 = 0
FEATURE [Part::Feature] Heliostat_216  label="Heliostat_216(Mirror,Axis_1_216,Axis_2_216,Normal_216,Target_point)"
  Placement = pos=(196618,-357484,8.6968e-11) rot=(0,0,1;0rad)
  shape: bbox 10000 x 51.21 x 10000 mm, 1 faces, 0 solids (baked)
FEATURE [Part::Line] Normal_216
  AttacherType = Attacher::AttachEngine3D
  X1 = 196618
  X2 = 196618
  Y1 = 130697
  Y2 = 129697
  Z1 = 0
  Z2 = 0
FEATURE [Part::Line] Axis_1_216
  AttacherType = Attacher::AttachEngine3D
  X1 = 196618
  X2 = 196618
  Y1 = 130697
  Y2 = 130697
  Z1 = 0
  Z2 = -1000
FEATURE [Part::Line] Axis_2_216
  AttacherType = Attacher::AttachEngine3D
  X1 = 196618
  X2 = 195618
  Y1 = 130697
  Y2 = 130697
  Z1 = 0
  Z2 = 0
FEATURE [Part::Feature] Heliostat_217  label="Heliostat_217(Mirror,Axis_1_217,Axis_2_217,Normal_217,Target_point)"
  Placement = pos=(187707,-445790,7.33721e-11) rot=(0,0,1;0rad)
  shape: bbox 10000 x 31.86 x 10000 mm, 1 faces, 0 solids (baked)
FEATURE [Part::Line] Normal_217
  AttacherType = Attacher::AttachEngine3D
  X1 = 187707
  X2 = 187707
  Y1 = 338927
  Y2 = 337927
  Z1 = 0
  Z2 = 0
FEATURE [Part::Line] Axis_1_217
  AttacherType = Attacher::AttachEngine3D
  X1 = 187707
  X2 = 187707
  Y1 = 338927
  Y2 = 338927
  Z1 = 0
  Z2 = -1000
FEATURE [Part::Line] Axis_2_217
  AttacherType = Attacher::AttachEngine3D
  X1 = 187707
  X2 = 186707
  Y1 = 338927
  Y2 = 338927
  Z1 = 0
  Z2 = 0
FEATURE [Part::Feature] Heliostat_218  label="Heliostat_218(Mirror,Axis_1_218,Axis_2_218,Normal_218,Target_point)"
  Placement = pos=(-187707,-445790,7.33721e-11) rot=(0,0,1;0rad)
  shape: bbox 10000 x 31.86 x 10000 mm, 1 faces, 0 solids (baked)
FEATURE [Part::Line] Normal_218
  AttacherType = Attacher::AttachEngine3D
  X1 = -187707
  X2 = -187707
  Y1 = 338927
  Y2 = 337927
  Z1 = 0
  Z2 = 0
FEATURE [Part::Line] Axis_1_218
  AttacherType = Attacher::AttachEngine3D
  X1 = -187707
  X2 = -187707
  Y1 = 338927
  Y2 = 338927
  Z1 = 0
  Z2 = -1000
FEATURE [Part::Line] Axis_2_218
  AttacherType = Attacher::AttachEngine3D
  X1 = -187707
  X2 = -188707
  Y1 = 338927
  Y2 = 338927
  Z1 = 0
  Z2 = 0
FEATURE [Part::Feature] Heliostat_219  label="Heliostat_219(Mirror,Axis_1_219,Axis_2_219,Normal_219,Target_point)"
  Placement = pos=(-196618,-357484,8.6968e-11) rot=(0,0,1;0rad)
  shape: bbox 10000 x 51.21 x 10000 mm, 1 faces, 0 solids (baked)
FEATURE [Part::Line] Normal_219
  AttacherType = Attacher::AttachEngine3D
  X1 = -196618
  X2 = -196618
  Y1 = 130697
  Y2 = 129697
  Z1 = 0
  Z2 = 0
FEATURE [Part::Line] Axis_1_219
  AttacherType = Attacher::AttachEngine3D
  X1 = -196618
  X2 = -196618
  Y1 = 130697
  Y2 = 130697
  Z1 = 0
  Z2 = -1000
FEATURE [Part::Line] Axis_2_219
  AttacherType = Attacher::AttachEngine3D
  X1 = -196618
  X2 = -197618
  Y1 = 130697
  Y2 = 130697
  Z1 = 0
  Z2 = 0
FEATURE [Part::Feature] Heliostat_220  label="Heliostat_220(Mirror,Axis_1_220,Axis_2_220,Normal_220,Target_point)"
  Placement = pos=(101687,-476055,3.21893e-10) rot=(0,0,1;0rad)
  shape: bbox 10000 x 27.15 x 10000 mm, 1 faces, 0 solids (baked)
FEATURE [Part::Line] Normal_220
  AttacherType = Attacher::AttachEngine3D
  X1 = 101687
  X2 = 101687
  Y1 = 444721
  Y2 = 443721
  Z1 = 0
  Z2 = 0
FEATURE [Part::Line] Axis_1_220
  AttacherType = Attacher::AttachEngine3D
  X1 = 101687
  X2 = 101687
  Y1 = 444721
  Y2 = 444721
  Z1 = 0
  Z2 = -1000
FEATURE [Part::Line] Axis_2_220
  AttacherType = Attacher::AttachEngine3D
  X1 = 101687
  X2 = 100687
  Y1 = 444721
  Y2 = 444721
  Z1 = 0
  Z2 = 0
FEATURE [Part::Feature] Heliostat_221  label="Heliostat_221(Mirror,Axis_1_221,Axis_2_221,Normal_221,Target_point)"
  Placement = pos=(-101687,-476055,3.21893e-10) rot=(0,0,1;0rad)
  shape: bbox 10000 x 27.15 x 10000 mm, 1 faces, 0 solids (baked)
FEATURE [Part::Line] Normal_221
  AttacherType = Attacher::AttachEngine3D
  X1 = -101687
  X2 = -101687
  Y1 = 444721
  Y2 = 443721
  Z1 = 0
  Z2 = 0
FEATURE [Part::Line] Axis_1_221
  AttacherType = Attacher::AttachEngine3D
  X1 = -101687
  X2 = -101687
  Y1 = 444721
  Y2 = 444721
  Z1 = 0
  Z2 = -1000
FEATURE [Part::Line] Axis_2_221
  AttacherType = Attacher::AttachEngine3D
  X1 = -101687
  X2 = -102687
  Y1 = 444721
  Y2 = 444721
  Z1 = 0
  Z2 = 0
FEATURE [Part::Feature] Heliostat_222  label="Heliostat_222(Mirror,Axis_1_222,Axis_2_222,Normal_222,Target_point)"
  Placement = pos=(181054,-416018,2.78906e-10) rot=(0,0,1;0rad)
  shape: bbox 10000 x 34.61 x 10000 mm, 1 faces, 0 solids (baked)
FEATURE [Part::Line] Normal_222
  AttacherType = Attacher::AttachEngine3D
  X1 = 181054
  X2 = 181054
  Y1 = 306283
  Y2 = 305283
  Z1 = 0
  Z2 = 0
FEATURE [Part::Line] Axis_1_222
  AttacherType = Attacher::AttachEngine3D
  X1 = 181054
  X2 = 181054
  Y1 = 306283
  Y2 = 306283
  Z1 = 0
  Z2 = -1000
FEATURE [Part::Line] Axis_2_222
  AttacherType = Attacher::AttachEngine3D
  X1 = 181054
  X2 = 180054
  Y1 = 306283
  Y2 = 306283
  Z1 = 0
  Z2 = 0
FEATURE [Part::Feature] Heliostat_223  label="Heliostat_223(Mirror,Axis_1_223,Axis_2_223,Normal_223,Target_point)"
  Placement = pos=(-181054,-416018,2.78906e-10) rot=(0,0,1;0rad)
  shape: bbox 10000 x 34.61 x 10000 mm, 1 faces, 0 solids (baked)
FEATURE [Part::Line] Normal_223
  AttacherType = Attacher::AttachEngine3D
  X1 = -181054
  X2 = -181054
  Y1 = 306283
  Y2 = 305283
  Z1 = 0
  Z2 = 0
FEATURE [Part::Line] Axis_1_223
  AttacherType = Attacher::AttachEngine3D
  X1 = -181054
  X2 = -181054
  Y1 = 306283
  Y2 = 306283
  Z1 = 0
  Z2 = -1000
FEATURE [Part::Line] Axis_2_223
  AttacherType = Attacher::AttachEngine3D
  X1 = -181054
  X2 = -182054
  Y1 = 306283
  Y2 = 306283
  Z1 = 0
  Z2 = 0
FEATURE [Part::Feature] Heliostat_224  label="Heliostat_224(Mirror,Axis_1_224,Axis_2_224,Normal_224,Target_point)"
  Placement = pos=(224536,-468981,1.10204e-11) rot=(0,0,1;0rad)
  shape: bbox 10000 x 31.86 x 10000 mm, 1 faces, 0 solids (baked)
FEATURE [Part::Line] Normal_224
  AttacherType = Attacher::AttachEngine3D
  X1 = 224536
  X2 = 224536
  Y1 = 315735
  Y2 = 314735
  Z1 = 0
  Z2 = 0
FEATURE [Part::Line] Axis_1_224
  AttacherType = Attacher::AttachEngine3D
  X1 = 224536
  X2 = 224536
  Y1 = 315735
  Y2 = 315735
  Z1 = 0
  Z2 = -1000
FEATURE [Part::Line] Axis_2_224
  AttacherType = Attacher::AttachEngine3D
  X1 = 224536
  X2 = 223536
  Y1 = 315735
  Y2 = 315735
  Z1 = 0
  Z2 = 0
FEATURE [Part::Feature] Heliostat_225  label="Heliostat_225(Mirror,Axis_1_225,Axis_2_225,Normal_225,Target_point)"
  Placement = pos=(-224536,-468981,1.10204e-11) rot=(0,0,1;0rad)
  shape: bbox 10000 x 31.86 x 10000 mm, 1 faces, 0 solids (baked)
FEATURE [Part::Line] Normal_225
  AttacherType = Attacher::AttachEngine3D
  X1 = -224536
  X2 = -224536
  Y1 = 315735
  Y2 = 314735
  Z1 = 0
  Z2 = 0
FEATURE [Part::Line] Axis_1_225
  AttacherType = Attacher::AttachEngine3D
  X1 = -224536
  X2 = -224536
  Y1 = 315735
  Y2 = 315735
  Z1 = 0
  Z2 = -1000
FEATURE [Part::Line] Axis_2_225
  AttacherType = Attacher::AttachEngine3D
  X1 = -224536
  X2 = -225536
  Y1 = 315735
  Y2 = 315735
  Z1 = 0
  Z2 = 0
FEATURE [Part::Feature] Heliostat_226  label="Heliostat_226(Mirror,Axis_1_226,Axis_2_226,Normal_226,Target_point)"
  Placement = pos=(49822.6,-370012,1.33122e-10) rot=(0,0,1;0rad)
  shape: bbox 10000 x 34.61 x 10000 mm, 1 faces, 0 solids (baked)
FEATURE [Part::Line] Normal_226
  AttacherType = Attacher::AttachEngine3D
  X1 = 49822.6
  X2 = 49822.6
  Y1 = 352289
  Y2 = 351289
  Z1 = 0
  Z2 = 0
FEATURE [Part::Line] Axis_1_226
  AttacherType = Attacher::AttachEngine3D
  X1 = 49822.6
  X2 = 49822.6
  Y1 = 352289
  Y2 = 352289
  Z1 = 0
  Z2 = -1000
FEATURE [Part::Line] Axis_2_226
  AttacherType = Attacher::AttachEngine3D
  X1 = 49822.6
  X2 = 48822.6
  Y1 = 352289
  Y2 = 352289
  Z1 = 0
  Z2 = 0
FEATURE [Part::Feature] Heliostat_227  label="Heliostat_227(Mirror,Axis_1_227,Axis_2_227,Normal_227,Target_point)"
  Placement = pos=(-49822.6,-370012,1.33122e-10) rot=(0,0,1;0rad)
  shape: bbox 10000 x 34.61 x 10000 mm, 1 faces, 0 solids (baked)
FEATURE [Part::Line] Normal_227
  AttacherType = Attacher::AttachEngine3D
  X1 = -49822.6
  X2 = -49822.6
  Y1 = 352289
  Y2 = 351289
  Z1 = 0
  Z2 = 0
FEATURE [Part::Line] Axis_1_227
  AttacherType = Attacher::AttachEngine3D
  X1 = -49822.6
  X2 = -49822.6
  Y1 = 352289
  Y2 = 352289
  Z1 = 0
  Z2 = -1000
FEATURE [Part::Line] Axis_2_227
  AttacherType = Attacher::AttachEngine3D
  X1 = -49822.6
  X2 = -50822.6
  Y1 = 352289
  Y2 = 352289
  Z1 = 0
  Z2 = 0
FEATURE [Part::Feature] Heliostat_228  label="Heliostat_228(Mirror,Axis_1_228,Axis_2_228,Normal_228,Target_point)"
  Placement = pos=(127477,-448045,3.36922e-10) rot=(0,0,1;0rad)
  shape: bbox 10000 x 29.51 x 10000 mm, 1 faces, 0 solids (baked)
FEATURE [Part::Line] Normal_228
  AttacherType = Attacher::AttachEngine3D
  X1 = 127477
  X2 = 127477
  Y1 = 399214
  Y2 = 398214
  Z1 = 0
  Z2 = 0
FEATURE [Part::Line] Axis_1_228
  AttacherType = Attacher::AttachEngine3D
  X1 = 127477
  X2 = 127477
  Y1 = 399214
  Y2 = 399214
  Z1 = 0
  Z2 = -1000
FEATURE [Part::Line] Axis_2_228
  AttacherType = Attacher::AttachEngine3D
  X1 = 127477
  X2 = 126477
  Y1 = 399214
  Y2 = 399214
  Z1 = 0
  Z2 = 0
FEATURE [Part::Feature] Heliostat_229  label="Heliostat_229(Mirror,Axis_1_229,Axis_2_229,Normal_229,Target_point)"
  Placement = pos=(-127477,-448045,3.36922e-10) rot=(0,0,1;0rad)
  shape: bbox 10000 x 29.51 x 10000 mm, 1 faces, 0 solids (baked)
FEATURE [Part::Line] Normal_229
  AttacherType = Attacher::AttachEngine3D
  X1 = -127477
  X2 = -127477
  Y1 = 399214
  Y2 = 398214
  Z1 = 0
  Z2 = 0
FEATURE [Part::Line] Axis_1_229
  AttacherType = Attacher::AttachEngine3D
  X1 = -127477
  X2 = -127477
  Y1 = 399214
  Y2 = 399214
  Z1 = 0
  Z2 = -1000
FEATURE [Part::Line] Axis_2_229
  AttacherType = Attacher::AttachEngine3D
  X1 = -127477
  X2 = -128477
  Y1 = 399214
  Y2 = 399214
  Z1 = 0
  Z2 = 0
FEATURE [Part::Feature] Heliostat_230  label="Heliostat_230(Mirror,Axis_1_230,Axis_2_230,Normal_230,Target_point)"
  Placement = pos=(9962.27,-146534,2.59227e-11) rot=(0,0,1;0rad)
  shape: bbox 10000 x 95.83 x 10000 mm, 1 faces, 0 solids (baked)
FEATURE [Part::Line] Normal_230
  AttacherType = Attacher::AttachEngine3D
  X1 = 9962.27
  X2 = 9962.27
  Y1 = 114351
  Y2 = 113351
  Z1 = 0
  Z2 = 0
FEATURE [Part::Line] Axis_1_230
  AttacherType = Attacher::AttachEngine3D
  X1 = 9962.27
  X2 = 9962.27
  Y1 = 114351
  Y2 = 114351
  Z1 = 0
  Z2 = -1000
FEATURE [Part::Line] Axis_2_230
  AttacherType = Attacher::AttachEngine3D
  X1 = 9962.27
  X2 = 8962.27
  Y1 = 114351
  Y2 = 114351
  Z1 = 0
  Z2 = 0
FEATURE [Part::Feature] Heliostat_231  label="Heliostat_231(Mirror,Axis_1_231,Axis_2_231,Normal_231,Target_point)"
  Placement = pos=(-9962.26,-146534,2.59227e-11) rot=(0,0,1;0rad)
  shape: bbox 10000 x 95.83 x 10000 mm, 1 faces, 0 solids (baked)
FEATURE [Part::Line] Normal_231
  AttacherType = Attacher::AttachEngine3D
  X1 = -9962.27
  X2 = -9962.27
  Y1 = 114351
  Y2 = 113351
  Z1 = 0
  Z2 = 0
FEATURE [Part::Line] Axis_1_231
  AttacherType = Attacher::AttachEngine3D
  X1 = -9962.27
  X2 = -9962.27
  Y1 = 114351
  Y2 = 114351
  Z1 = 0
  Z2 = -1000
FEATURE [Part::Line] Axis_2_231
  AttacherType = Attacher::AttachEngine3D
  X1 = -9962.27
  X2 = -10962.3
  Y1 = 114351
  Y2 = 114351
  Z1 = 0
  Z2 = 0
FEATURE [Part::Feature] Heliostat_232  label="Heliostat_232(Mirror,Axis_1_232,Axis_2_232,Normal_232,Target_point)"
  Placement = pos=(76547.7,-471045,8.81217e-11) rot=(0,0,1;0rad)
  shape: bbox 10000 x 27.15 x 10000 mm, 1 faces, 0 solids (baked)
FEATURE [Part::Line] Normal_232
  AttacherType = Attacher::AttachEngine3D
  X1 = 76547.7
  X2 = 76547.7
  Y1 = 449731
  Y2 = 448731
  Z1 = 0
  Z2 = 0
FEATURE [Part::Line] Axis_1_232
  AttacherType = Attacher::AttachEngine3D
  X1 = 76547.7
  X2 = 76547.7
  Y1 = 449731
  Y2 = 449731
  Z1 = 0
  Z2 = -1000
FEATURE [Part::Line] Axis_2_232
  AttacherType = Attacher::AttachEngine3D
  X1 = 76547.7
  X2 = 75547.7
  Y1 = 449731
  Y2 = 449731
  Z1 = 0
  Z2 = 0
FEATURE [Part::Feature] Heliostat_233  label="Heliostat_233(Mirror,Axis_1_233,Axis_2_233,Normal_233,Target_point)"
  Placement = pos=(-76547.7,-471045,8.81217e-11) rot=(0,0,1;0rad)
  shape: bbox 10000 x 27.15 x 10000 mm, 1 faces, 0 solids (baked)
FEATURE [Part::Line] Normal_233
  AttacherType = Attacher::AttachEngine3D
  X1 = -76547.7
  X2 = -76547.7
  Y1 = 449731
  Y2 = 448731
  Z1 = 0
  Z2 = 0
FEATURE [Part::Line] Axis_1_233
  AttacherType = Attacher::AttachEngine3D
  X1 = -76547.7
  X2 = -76547.7
  Y1 = 449731
  Y2 = 449731
  Z1 = 0
  Z2 = -1000
FEATURE [Part::Line] Axis_2_233
  AttacherType = Attacher::AttachEngine3D
  X1 = -76547.7
  X2 = -77547.7
  Y1 = 449731
  Y2 = 449731
  Z1 = 0
  Z2 = 0
FEATURE [Part::Feature] Heliostat_234  label="Heliostat_234(Mirror,Axis_1_234,Axis_2_234,Normal_234,Target_point)"
  Placement = pos=(206228,-375051,1.40591e-10) rot=(0,0,1;0rad)
  shape: bbox 10000 x 47.5 x 10000 mm, 1 faces, 0 solids (baked)
FEATURE [Part::Line] Normal_234
  AttacherType = Attacher::AttachEngine3D
  X1 = 206228
  X2 = 206228
  Y1 = 151296
  Y2 = 150296
  Z1 = 0
  Z2 = 0
FEATURE [Part::Line] Axis_1_234
  AttacherType = Attacher::AttachEngine3D
  X1 = 206228
  X2 = 206228
  Y1 = 151296
  Y2 = 151296
  Z1 = 0
  Z2 = -1000
FEATURE [Part::Line] Axis_2_234
  AttacherType = Attacher::AttachEngine3D
  X1 = 206228
  X2 = 205228
  Y1 = 151296
  Y2 = 151296
  Z1 = 0
  Z2 = 0
FEATURE [Part::Feature] Heliostat_235  label="Heliostat_235(Mirror,Axis_1_235,Axis_2_235,Normal_235,Target_point)"
  Placement = pos=(-206228,-375051,1.40591e-10) rot=(0,0,1;0rad)
  shape: bbox 10000 x 47.5 x 10000 mm, 1 faces, 0 solids (baked)
FEATURE [Part::Line] Normal_235
  AttacherType = Attacher::AttachEngine3D
  X1 = -206228
  X2 = -206228
  Y1 = 151296
  Y2 = 150296
  Z1 = 0
  Z2 = 0
FEATURE [Part::Line] Axis_1_235
  AttacherType = Attacher::AttachEngine3D
  X1 = -206228
  X2 = -206228
  Y1 = 151296
  Y2 = 151296
  Z1 = 0
  Z2 = -1000
FEATURE [Part::Line] Axis_2_235
  AttacherType = Attacher::AttachEngine3D
  X1 = -206228
  X2 = -207228
  Y1 = 151296
  Y2 = 151296
  Z1 = 0
  Z2 = 0
FEATURE [Part::Feature] Heliostat_236  label="Heliostat_236(Mirror,Axis_1_236,Axis_2_236,Normal_236,Target_point)"
  Placement = pos=(218181,-397639,1.0474e-10) rot=(0,0,1;0rad)
  shape: bbox 10000 x 43.77 x 10000 mm, 1 faces, 0 solids (baked)
FEATURE [Part::Line] Normal_236
  AttacherType = Attacher::AttachEngine3D
  X1 = 218181
  X2 = 218181
  Y1 = 173575
  Y2 = 172575
  Z1 = 0
  Z2 = 0
FEATURE [Part::Line] Axis_1_236
  AttacherType = Attacher::AttachEngine3D
  X1 = 218181
  X2 = 218181
  Y1 = 173575
  Y2 = 173575
  Z1 = 0
  Z2 = -1000
FEATURE [Part::Line] Axis_2_236
  AttacherType = Attacher::AttachEngine3D
  X1 = 218181
  X2 = 217181
  Y1 = 173575
  Y2 = 173575
  Z1 = 0
  Z2 = 0
FEATURE [Part::Feature] Heliostat_237  label="Heliostat_237(Mirror,Axis_1_237,Axis_2_237,Normal_237,Target_point)"
  Placement = pos=(-218181,-397639,1.0474e-10) rot=(0,0,1;0rad)
  shape: bbox 10000 x 43.77 x 10000 mm, 1 faces, 0 solids (baked)
FEATURE [Part::Line] Normal_237
  AttacherType = Attacher::AttachEngine3D
  X1 = -218181
  X2 = -218181
  Y1 = 173575
  Y2 = 172575
  Z1 = 0
  Z2 = 0
FEATURE [Part::Line] Axis_1_237
  AttacherType = Attacher::AttachEngine3D
  X1 = -218181
  X2 = -218181
  Y1 = 173575
  Y2 = 173575
  Z1 = 0
  Z2 = -1000
FEATURE [Part::Line] Axis_2_237
  AttacherType = Attacher::AttachEngine3D
  X1 = -218181
  X2 = -219181
  Y1 = 173575
  Y2 = 173575
  Z1 = 0
  Z2 = 0
FEATURE [Part::Feature] Heliostat_238  label="Heliostat_238(Mirror,Axis_1_238,Axis_2_238,Normal_238,Target_point)"
  Placement = pos=(222313,-426932,1.77539e-10) rot=(0,0,1;0rad)
  shape: bbox 10000 x 37.36 x 10000 mm, 1 faces, 0 solids (baked)
FEATURE [Part::Line] Normal_238
  AttacherType = Attacher::AttachEngine3D
  X1 = 222313
  X2 = 222313
  Y1 = 242271
  Y2 = 241271
  Z1 = 0
  Z2 = 0
FEATURE [Part::Line] Axis_1_238
  AttacherType = Attacher::AttachEngine3D
  X1 = 222313
  X2 = 222313
  Y1 = 242271
  Y2 = 242271
  Z1 = 0
  Z2 = -1000
FEATURE [Part::Line] Axis_2_238
  AttacherType = Attacher::AttachEngine3D
  X1 = 222313
  X2 = 221313
  Y1 = 242271
  Y2 = 242271
  Z1 = 0
  Z2 = 0
FEATURE [Part::Feature] Heliostat_239  label="Heliostat_239(Mirror,Axis_1_239,Axis_2_239,Normal_239,Target_point)"
  Placement = pos=(-222313,-426932,1.77539e-10) rot=(0,0,1;0rad)
  shape: bbox 10000 x 37.36 x 10000 mm, 1 faces, 0 solids (baked)
FEATURE [Part::Line] Normal_239
  AttacherType = Attacher::AttachEngine3D
  X1 = -222313
  X2 = -222313
  Y1 = 242271
  Y2 = 241271
  Z1 = 0
  Z2 = 0
FEATURE [Part::Line] Axis_1_239
  AttacherType = Attacher::AttachEngine3D
  X1 = -222313
  X2 = -222313
  Y1 = 242271
  Y2 = 242271
  Z1 = 0
  Z2 = -1000
FEATURE [Part::Line] Axis_2_239
  AttacherType = Attacher::AttachEngine3D
  X1 = -222313
  X2 = -223313
  Y1 = 242271
  Y2 = 242271
  Z1 = 0
  Z2 = 0
FEATURE [Part::Feature] Heliostat_240  label="Heliostat_240(Mirror,Axis_1_240,Axis_2_240,Normal_240,Target_point)"
  Placement = pos=(104853,-441515,9.08762e-11) rot=(0,0,1;0rad)
  shape: bbox 10000 x 29.51 x 10000 mm, 1 faces, 0 solids (baked)
FEATURE [Part::Line] Normal_240
  AttacherType = Attacher::AttachEngine3D
  X1 = 104853
  X2 = 104853
  Y1 = 405744
  Y2 = 404744
  Z1 = 0
  Z2 = 0
FEATURE [Part::Line] Axis_1_240
  AttacherType = Attacher::AttachEngine3D
  X1 = 104853
  X2 = 104853
  Y1 = 405744
  Y2 = 405744
  Z1 = 0
  Z2 = -1000
FEATURE [Part::Line] Axis_2_240
  AttacherType = Attacher::AttachEngine3D
  X1 = 104853
  X2 = 103853
  Y1 = 405744
  Y2 = 405744
  Z1 = 0
  Z2 = 0
FEATURE [Part::Feature] Heliostat_241  label="Heliostat_241(Mirror,Axis_1_241,Axis_2_241,Normal_241,Target_point)"
  Placement = pos=(-104853,-441515,9.08762e-11) rot=(0,0,1;0rad)
  shape: bbox 10000 x 29.51 x 10000 mm, 1 faces, 0 solids (baked)
FEATURE [Part::Line] Normal_241
  AttacherType = Attacher::AttachEngine3D
  X1 = -104853
  X2 = -104853
  Y1 = 405744
  Y2 = 404744
  Z1 = 0
  Z2 = 0
FEATURE [Part::Line] Axis_1_241
  AttacherType = Attacher::AttachEngine3D
  X1 = -104853
  X2 = -104853
  Y1 = 405744
  Y2 = 405744
  Z1 = 0
  Z2 = -1000
FEATURE [Part::Line] Axis_2_241
  AttacherType = Attacher::AttachEngine3D
  X1 = -104853
  X2 = -105853
  Y1 = 405744
  Y2 = 405744
  Z1 = 0
  Z2 = 0
FEATURE [Part::Feature] Heliostat_242  label="Heliostat_242(Mirror,Axis_1_242,Axis_2_242,Normal_242,Target_point)"
  Placement = pos=(81897.4,-436266,8.65532e-11) rot=(0,0,1;0rad)
  shape: bbox 10000 x 29.51 x 10000 mm, 1 faces, 0 solids (baked)
FEATURE [Part::Line] Normal_242
  AttacherType = Attacher::AttachEngine3D
  X1 = 81897.4
  X2 = 81897.4
  Y1 = 410993
  Y2 = 409993
  Z1 = 0
  Z2 = 0
FEATURE [Part::Line] Axis_1_242
  AttacherType = Attacher::AttachEngine3D
  X1 = 81897.4
  X2 = 81897.4
  Y1 = 410993
  Y2 = 410993
  Z1 = 0
  Z2 = -1000
FEATURE [Part::Line] Axis_2_242
  AttacherType = Attacher::AttachEngine3D
  X1 = 81897.4
  X2 = 80897.4
  Y1 = 410993
  Y2 = 410993
  Z1 = 0
  Z2 = 0
FEATURE [Part::Feature] Heliostat_243  label="Heliostat_243(Mirror,Axis_1_243,Axis_2_243,Normal_243,Target_point)"
  Placement = pos=(-81897.4,-436266,8.65532e-11) rot=(0,0,1;0rad)
  shape: bbox 10000 x 29.51 x 10000 mm, 1 faces, 0 solids (baked)
FEATURE [Part::Line] Normal_243
  AttacherType = Attacher::AttachEngine3D
  X1 = -81897.4
  X2 = -81897.4
  Y1 = 410993
  Y2 = 409993
  Z1 = 0
  Z2 = 0
FEATURE [Part::Line] Axis_1_243
  AttacherType = Attacher::AttachEngine3D
  X1 = -81897.4
  X2 = -81897.4
  Y1 = 410993
  Y2 = 410993
  Z1 = 0
  Z2 = -1000
FEATURE [Part::Line] Axis_2_243
  AttacherType = Attacher::AttachEngine3D
  X1 = -81897.4
  X2 = -82897.4
  Y1 = 410993
  Y2 = 410993
  Z1 = 0
  Z2 = 0
FEATURE [Part::Feature] Heliostat_244  label="Heliostat_244(Mirror,Axis_1_244,Axis_2_244,Normal_244,Target_point)"
  Placement = pos=(206447,-456868,7.33721e-11) rot=(0,0,1;0rad)
  shape: bbox 10000 x 31.86 x 10000 mm, 1 faces, 0 solids (baked)
FEATURE [Part::Line] Normal_244
  AttacherType = Attacher::AttachEngine3D
  X1 = 206447
  X2 = 206447
  Y1 = 327848
  Y2 = 326848
  Z1 = 0
  Z2 = 0
FEATURE [Part::Line] Axis_1_244
  AttacherType = Attacher::AttachEngine3D
  X1 = 206447
  X2 = 206447
  Y1 = 327848
  Y2 = 327848
  Z1 = 0
  Z2 = -1000
FEATURE [Part::Line] Axis_2_244
  AttacherType = Attacher::AttachEngine3D
  X1 = 206447
  X2 = 205447
  Y1 = 327848
  Y2 = 327848
  Z1 = 0
  Z2 = 0
FEATURE [Part::Feature] Heliostat_245  label="Heliostat_245(Mirror,Axis_1_245,Axis_2_245,Normal_245,Target_point)"
  Placement = pos=(-206447,-456868,7.33721e-11) rot=(0,0,1;0rad)
  shape: bbox 10000 x 31.86 x 10000 mm, 1 faces, 0 solids (baked)
FEATURE [Part::Line] Normal_245
  AttacherType = Attacher::AttachEngine3D
  X1 = -206447
  X2 = -206447
  Y1 = 327848
  Y2 = 326848
  Z1 = 0
  Z2 = 0
FEATURE [Part::Line] Axis_1_245
  AttacherType = Attacher::AttachEngine3D
  X1 = -206447
  X2 = -206447
  Y1 = 327848
  Y2 = 327848
  Z1 = 0
  Z2 = -1000
FEATURE [Part::Line] Axis_2_245
  AttacherType = Attacher::AttachEngine3D
  X1 = -206447
  X2 = -207447
  Y1 = 327848
  Y2 = 327848
  Z1 = 0
  Z2 = 0
FEATURE [Part::Feature] Heliostat_246  label="Heliostat_246(Mirror,Axis_1_246,Axis_2_246,Normal_246,Target_point)"
  Placement = pos=(58683.5,-432315,2.28161e-10) rot=(0,0,1;0rad)
  shape: bbox 10000 x 29.51 x 10000 mm, 1 faces, 0 solids (baked)
FEATURE [Part::Line] Normal_246
  AttacherType = Attacher::AttachEngine3D
  X1 = 58683.5
  X2 = 58683.5
  Y1 = 414944
  Y2 = 413944
  Z1 = 0
  Z2 = 0
FEATURE [Part::Line] Axis_1_246
  AttacherType = Attacher::AttachEngine3D
  X1 = 58683.5
  X2 = 58683.5
  Y1 = 414944
  Y2 = 414944
  Z1 = 0
  Z2 = -1000
FEATURE [Part::Line] Axis_2_246
  AttacherType = Attacher::AttachEngine3D
  X1 = 58683.5
  X2 = 57683.5
  Y1 = 414944
  Y2 = 414944
  Z1 = 0
  Z2 = 0
FEATURE [Part::Feature] Heliostat_247  label="Heliostat_247(Mirror,Axis_1_247,Axis_2_247,Normal_247,Target_point)"
  Placement = pos=(-58683.5,-432315,2.28161e-10) rot=(0,0,1;0rad)
  shape: bbox 10000 x 29.51 x 10000 mm, 1 faces, 0 solids (baked)
FEATURE [Part::Line] Normal_247
  AttacherType = Attacher::AttachEngine3D
  X1 = -58683.5
  X2 = -58683.5
  Y1 = 414944
  Y2 = 413944
  Z1 = 0
  Z2 = 0
FEATURE [Part::Line] Axis_1_247
  AttacherType = Attacher::AttachEngine3D
  X1 = -58683.5
  X2 = -58683.5
  Y1 = 414944
  Y2 = 414944
  Z1 = 0
  Z2 = -1000
FEATURE [Part::Line] Axis_2_247
  AttacherType = Attacher::AttachEngine3D
  X1 = -58683.5
  X2 = -59683.5
  Y1 = 414944
  Y2 = 414944
  Z1 = 0
  Z2 = 0
FEATURE [Part::Feature] Heliostat_248  label="Heliostat_248(Mirror,Axis_1_248,Axis_2_248,Normal_248,Target_point)"
  Placement = pos=(171448,-464862,9.08762e-11) rot=(0,0,1;0rad)
  shape: bbox 10000 x 29.51 x 10000 mm, 1 faces, 0 solids (baked)
FEATURE [Part::Line] Normal_248
  AttacherType = Attacher::AttachEngine3D
  X1 = 171448
  X2 = 171448
  Y1 = 382398
  Y2 = 381398
  Z1 = 0
  Z2 = 0
FEATURE [Part::Line] Axis_1_248
  AttacherType = Attacher::AttachEngine3D
  X1 = 171448
  X2 = 171448
  Y1 = 382398
  Y2 = 382398
  Z1 = 0
  Z2 = -1000
FEATURE [Part::Line] Axis_2_248
  AttacherType = Attacher::AttachEngine3D
  X1 = 171448
  X2 = 170448
  Y1 = 382398
  Y2 = 382398
  Z1 = 0
  Z2 = 0
FEATURE [Part::Feature] Heliostat_249  label="Heliostat_249(Mirror,Axis_1_249,Axis_2_249,Normal_249,Target_point)"
  Placement = pos=(-171448,-464862,9.08762e-11) rot=(0,0,1;0rad)
  shape: bbox 10000 x 29.51 x 10000 mm, 1 faces, 0 solids (baked)
FEATURE [Part::Line] Normal_249
  AttacherType = Attacher::AttachEngine3D
  X1 = -171448
  X2 = -171448
  Y1 = 382398
  Y2 = 381398
  Z1 = 0
  Z2 = 0
FEATURE [Part::Line] Axis_1_249
  AttacherType = Attacher::AttachEngine3D
  X1 = -171448
  X2 = -171448
  Y1 = 382398
  Y2 = 382398
  Z1 = 0
  Z2 = -1000
FEATURE [Part::Line] Axis_2_249
  AttacherType = Attacher::AttachEngine3D
  X1 = -171448
  X2 = -172448
  Y1 = 382398
  Y2 = 382398
  Z1 = 0
  Z2 = 0
FEATURE [Part::Feature] Heliostat_250  label="Heliostat_250(Mirror,Axis_1_250,Axis_2_250,Normal_250,Target_point)"
  Placement = pos=(-35284.4,-429674,3.36922e-10) rot=(0,0,1;0rad)
  shape: bbox 10000 x 29.51 x 10000 mm, 1 faces, 0 solids (baked)
FEATURE [Part::Line] Normal_250
  AttacherType = Attacher::AttachEngine3D
  X1 = -35284.4
  X2 = -35284.4
  Y1 = 417585
  Y2 = 416585
  Z1 = 0
  Z2 = 0
FEATURE [Part::Line] Axis_1_250
  AttacherType = Attacher::AttachEngine3D
  X1 = -35284.4
  X2 = -35284.4
  Y1 = 417585
  Y2 = 417585
  Z1 = 0
  Z2 = -1000
FEATURE [Part::Line] Axis_2_250
  AttacherType = Attacher::AttachEngine3D
  X1 = -35284.4
  X2 = -36284.4
  Y1 = 417585
  Y2 = 417585
  Z1 = 0
  Z2 = 0
FEATURE [Part::Feature] Heliostat_251  label="Heliostat_251(Mirror,Axis_1_251,Axis_2_251,Normal_251,Target_point)"
  Placement = pos=(35284.4,-429674,3.36922e-10) rot=(0,0,1;0rad)
  shape: bbox 10000 x 29.51 x 10000 mm, 1 faces, 0 solids (baked)
FEATURE [Part::Line] Normal_251
  AttacherType = Attacher::AttachEngine3D
  X1 = 35284.4
  X2 = 35284.4
  Y1 = 417585
  Y2 = 416585
  Z1 = 0
  Z2 = 0
FEATURE [Part::Line] Axis_1_251
  AttacherType = Attacher::AttachEngine3D
  X1 = 35284.4
  X2 = 35284.4
  Y1 = 417585
  Y2 = 417585
  Z1 = 0
  Z2 = -1000
FEATURE [Part::Line] Axis_2_251
  AttacherType = Attacher::AttachEngine3D
  X1 = 35284.4
  X2 = 34284.4
  Y1 = 417585
  Y2 = 417585
  Z1 = 0
  Z2 = 0
FEATURE [Part::Feature] Heliostat_252  label="Heliostat_252(Mirror,Axis_1_252,Axis_2_252,Normal_252,Target_point)"
  Placement = pos=(212603,-402006,1.64204e-10) rot=(0,0,1;0rad)
  shape: bbox 10000 x 40.57 x 10000 mm, 1 faces, 0 solids (baked)
FEATURE [Part::Line] Normal_252
  AttacherType = Attacher::AttachEngine3D
  X1 = 212603
  X2 = 212603
  Y1 = 214250
  Y2 = 213250
  Z1 = 0
  Z2 = 0
FEATURE [Part::Line] Axis_1_252
  AttacherType = Attacher::AttachEngine3D
  X1 = 212603
  X2 = 212603
  Y1 = 214250
  Y2 = 214250
  Z1 = 0
  Z2 = -1000
FEATURE [Part::Line] Axis_2_252
  AttacherType = Attacher::AttachEngine3D
  X1 = 212603
  X2 = 211603
  Y1 = 214250
  Y2 = 214250
  Z1 = 0
  Z2 = 0
FEATURE [Part::Feature] Heliostat_253  label="Heliostat_253(Mirror,Axis_1_253,Axis_2_253,Normal_253,Target_point)"
  Placement = pos=(-212603,-402006,1.64204e-10) rot=(0,0,1;0rad)
  shape: bbox 10000 x 40.57 x 10000 mm, 1 faces, 0 solids (baked)
FEATURE [Part::Line] Normal_253
  AttacherType = Attacher::AttachEngine3D
  X1 = -212603
  X2 = -212603
  Y1 = 214250
  Y2 = 213250
  Z1 = 0
  Z2 = 0
FEATURE [Part::Line] Axis_1_253
  AttacherType = Attacher::AttachEngine3D
  X1 = -212603
  X2 = -212603
  Y1 = 214250
  Y2 = 214250
  Z1 = 0
  Z2 = -1000
FEATURE [Part::Line] Axis_2_253
  AttacherType = Attacher::AttachEngine3D
  X1 = -212603
  X2 = -213603
  Y1 = 214250
  Y2 = 214250
  Z1 = 0
  Z2 = 0
FEATURE [Part::Feature] Heliostat_254  label="Heliostat_254(Mirror,Axis_1_254,Axis_2_254,Normal_254,Target_point)"
  Placement = pos=(11773.9,-428352,3.36922e-10) rot=(0,0,1;0rad)
  shape: bbox 10000 x 29.51 x 10000 mm, 1 faces, 0 solids (baked)
FEATURE [Part::Line] Normal_254
  AttacherType = Attacher::AttachEngine3D
  X1 = 11773.9
  X2 = 11773.9
  Y1 = 418908
  Y2 = 417908
  Z1 = 0
  Z2 = 0
FEATURE [Part::Line] Axis_1_254
  AttacherType = Attacher::AttachEngine3D
  X1 = 11773.9
  X2 = 11773.9
  Y1 = 418908
  Y2 = 418908
  Z1 = 0
  Z2 = -1000
FEATURE [Part::Line] Axis_2_254
  AttacherType = Attacher::AttachEngine3D
  X1 = 11773.9
  X2 = 10773.9
  Y1 = 418908
  Y2 = 418908
  Z1 = 0
  Z2 = 0
FEATURE [Part::Feature] Heliostat_255  label="Heliostat_255(Mirror,Axis_1_255,Axis_2_255,Normal_255,Target_point)"
  Placement = pos=(-11773.9,-428352,3.36922e-10) rot=(0,0,1;0rad)
  shape: bbox 10000 x 29.51 x 10000 mm, 1 faces, 0 solids (baked)
FEATURE [Part::Line] Normal_255
  AttacherType = Attacher::AttachEngine3D
  X1 = -11773.9
  X2 = -11773.9
  Y1 = 418908
  Y2 = 417908
  Z1 = 0
  Z2 = 0
FEATURE [Part::Line] Axis_1_255
  AttacherType = Attacher::AttachEngine3D
  X1 = -11773.9
  X2 = -11773.9
  Y1 = 418908
  Y2 = 418908
  Z1 = 0
  Z2 = -1000
FEATURE [Part::Line] Axis_2_255
  AttacherType = Attacher::AttachEngine3D
  X1 = -11773.9
  X2 = -12773.9
  Y1 = 418908
  Y2 = 418908
  Z1 = 0
  Z2 = 0
FEATURE [Part::Feature] Heliostat_256  label="Heliostat_256(Mirror,Axis_1_256,Axis_2_256,Normal_256,Target_point)"
  Placement = pos=(157468,-293198,3.77169e-11) rot=(0,0,1;0rad)
  shape: bbox 10000 x 64.79 x 10000 mm, 1 faces, 0 solids (baked)
FEATURE [Part::Line] Normal_256
  AttacherType = Attacher::AttachEngine3D
  X1 = 157468
  X2 = 157468
  Y1 = 92683
  Y2 = 91683
  Z1 = 0
  Z2 = 0
FEATURE [Part::Line] Axis_1_256
  AttacherType = Attacher::AttachEngine3D
  X1 = 157468
  X2 = 157468
  Y1 = 92683
  Y2 = 92683
  Z1 = 0
  Z2 = -1000
FEATURE [Part::Line] Axis_2_256
  AttacherType = Attacher::AttachEngine3D
  X1 = 157468
  X2 = 156468
  Y1 = 92683
  Y2 = 92683
  Z1 = 0
  Z2 = 0
FEATURE [Part::Feature] Heliostat_257  label="Heliostat_257(Mirror,Axis_1_257,Axis_2_257,Normal_257,Target_point)"
  Placement = pos=(-157468,-293198,3.77169e-11) rot=(0,0,1;0rad)
  shape: bbox 10000 x 64.79 x 10000 mm, 1 faces, 0 solids (baked)
FEATURE [Part::Line] Normal_257
  AttacherType = Attacher::AttachEngine3D
  X1 = -157468
  X2 = -157468
  Y1 = 92683
  Y2 = 91683
  Z1 = 0
  Z2 = 0
FEATURE [Part::Line] Axis_1_257
  AttacherType = Attacher::AttachEngine3D
  X1 = -157468
  X2 = -157468
  Y1 = 92683
  Y2 = 92683
  Z1 = 0
  Z2 = -1000
FEATURE [Part::Line] Axis_2_257
  AttacherType = Attacher::AttachEngine3D
  X1 = -157468
  X2 = -158468
  Y1 = 92683
  Y2 = 92683
  Z1 = 0
  Z2 = 0
FEATURE [Part::Feature] Heliostat_258  label="Heliostat_258(Mirror,Axis_1_258,Axis_2_258,Normal_258,Target_point)"
  Placement = pos=(202719,-410314,4.24186e-11) rot=(0,0,1;0rad)
  shape: bbox 10000 x 37.36 x 10000 mm, 1 faces, 0 solids (baked)
FEATURE [Part::Line] Normal_258
  AttacherType = Attacher::AttachEngine3D
  X1 = 202719
  X2 = 202719
  Y1 = 258889
  Y2 = 257889
  Z1 = 0
  Z2 = 0
FEATURE [Part::Line] Axis_1_258
  AttacherType = Attacher::AttachEngine3D
  X1 = 202719
  X2 = 202719
  Y1 = 258889
  Y2 = 258889
  Z1 = 0
  Z2 = -1000
FEATURE [Part::Line] Axis_2_258
  AttacherType = Attacher::AttachEngine3D
  X1 = 202719
  X2 = 201719
  Y1 = 258889
  Y2 = 258889
  Z1 = 0
  Z2 = 0
FEATURE [Part::Feature] Heliostat_259  label="Heliostat_259(Mirror,Axis_1_259,Axis_2_259,Normal_259,Target_point)"
  Placement = pos=(-202719,-410314,4.24186e-11) rot=(0,0,1;0rad)
  shape: bbox 10000 x 37.36 x 10000 mm, 1 faces, 0 solids (baked)
FEATURE [Part::Line] Normal_259
  AttacherType = Attacher::AttachEngine3D
  X1 = -202719
  X2 = -202719
  Y1 = 258889
  Y2 = 257889
  Z1 = 0
  Z2 = 0
FEATURE [Part::Line] Axis_1_259
  AttacherType = Attacher::AttachEngine3D
  X1 = -202719
  X2 = -202719
  Y1 = 258889
  Y2 = 258889
  Z1 = 0
  Z2 = -1000
FEATURE [Part::Line] Axis_2_259
  AttacherType = Attacher::AttachEngine3D
  X1 = -202719
  X2 = -203719
  Y1 = 258889
  Y2 = 258889
  Z1 = 0
  Z2 = 0
FEATURE [Part::Feature] Heliostat_260  label="Heliostat_260(Mirror,Axis_1_260,Axis_2_260,Normal_260,Target_point)"
  Placement = pos=(115591,-298182,5.0481e-11) rot=(0,0,1;0rad)
  shape: bbox 10000 x 47.5 x 10000 mm, 1 faces, 0 solids (baked)
FEATURE [Part::Line] Normal_260
  AttacherType = Attacher::AttachEngine3D
  X1 = 115591
  X2 = 115591
  Y1 = 228165
  Y2 = 227165
  Z1 = 0
  Z2 = 0
FEATURE [Part::Line] Axis_1_260
  AttacherType = Attacher::AttachEngine3D
  X1 = 115591
  X2 = 115591
  Y1 = 228165
  Y2 = 228165
  Z1 = 0
  Z2 = -1000
FEATURE [Part::Line] Axis_2_260
  AttacherType = Attacher::AttachEngine3D
  X1 = 115591
  X2 = 114591
  Y1 = 228165
  Y2 = 228165
  Z1 = 0
  Z2 = 0
FEATURE [Part::Feature] Heliostat_261  label="Heliostat_261(Mirror,Axis_1_261,Axis_2_261,Normal_261,Target_point)"
  Placement = pos=(-115591,-298182,5.0481e-11) rot=(0,0,1;0rad)
  shape: bbox 10000 x 47.5 x 10000 mm, 1 faces, 0 solids (baked)
FEATURE [Part::Line] Normal_261
  AttacherType = Attacher::AttachEngine3D
  X1 = -115591
  X2 = -115591
  Y1 = 228165
  Y2 = 227165
  Z1 = 0
  Z2 = 0
FEATURE [Part::Line] Axis_1_261
  AttacherType = Attacher::AttachEngine3D
  X1 = -115591
  X2 = -115591
  Y1 = 228165
  Y2 = 228165
  Z1 = 0
  Z2 = -1000
FEATURE [Part::Line] Axis_2_261
  AttacherType = Attacher::AttachEngine3D
  X1 = -115591
  X2 = -116591
  Y1 = 228165
  Y2 = 228165
  Z1 = 0
  Z2 = 0
FEATURE [Part::Feature] Heliostat_262  label="Heliostat_262(Mirror,Axis_1_262,Axis_2_262,Normal_262,Target_point)"
  Placement = pos=(168374,-435781,2.07508e-10) rot=(0,0,1;0rad)
  shape: bbox 10000 x 31.86 x 10000 mm, 1 faces, 0 solids (baked)
FEATURE [Part::Line] Normal_262
  AttacherType = Attacher::AttachEngine3D
  X1 = 168374
  X2 = 168374
  Y1 = 348935
  Y2 = 347935
  Z1 = 0
  Z2 = 0
FEATURE [Part::Line] Axis_1_262
  AttacherType = Attacher::AttachEngine3D
  X1 = 168374
  X2 = 168374
  Y1 = 348935
  Y2 = 348935
  Z1 = 0
  Z2 = -1000
FEATURE [Part::Line] Axis_2_262
  AttacherType = Attacher::AttachEngine3D
  X1 = 168374
  X2 = 167374
  Y1 = 348935
  Y2 = 348935
  Z1 = 0
  Z2 = 0
FEATURE [Part::Feature] Heliostat_263  label="Heliostat_263(Mirror,Axis_1_263,Axis_2_263,Normal_263,Target_point)"
  Placement = pos=(-168374,-435781,2.07508e-10) rot=(0,0,1;0rad)
  shape: bbox 10000 x 31.86 x 10000 mm, 1 faces, 0 solids (baked)
FEATURE [Part::Line] Normal_263
  AttacherType = Attacher::AttachEngine3D
  X1 = -168374
  X2 = -168374
  Y1 = 348935
  Y2 = 347935
  Z1 = 0
  Z2 = 0
FEATURE [Part::Line] Axis_1_263
  AttacherType = Attacher::AttachEngine3D
  X1 = -168374
  X2 = -168374
  Y1 = 348935
  Y2 = 348935
  Z1 = 0
  Z2 = -1000
FEATURE [Part::Line] Axis_2_263
  AttacherType = Attacher::AttachEngine3D
  X1 = -168374
  X2 = -169374
  Y1 = 348935
  Y2 = 348935
  Z1 = 0
  Z2 = 0
FEATURE [Part::Feature] Heliostat_264  label="Heliostat_264(Mirror,Axis_1_264,Axis_2_264,Normal_264,Target_point)"
  Placement = pos=(107437,-412477,9.6377e-12) rot=(0,0,1;0rad)
  shape: bbox 10000 x 31.86 x 10000 mm, 1 faces, 0 solids (baked)
FEATURE [Part::Line] Normal_264
  AttacherType = Attacher::AttachEngine3D
  X1 = 107437
  X2 = 107437
  Y1 = 372240
  Y2 = 371240
  Z1 = 0
  Z2 = 0
FEATURE [Part::Line] Axis_1_264
  AttacherType = Attacher::AttachEngine3D
  X1 = 107437
  X2 = 107437
  Y1 = 372240
  Y2 = 372240
  Z1 = 0
  Z2 = -1000
FEATURE [Part::Line] Axis_2_264
  AttacherType = Attacher::AttachEngine3D
  X1 = 107437
  X2 = 106437
  Y1 = 372240
  Y2 = 372240
  Z1 = 0
  Z2 = 0
FEATURE [Part::Feature] Heliostat_265  label="Heliostat_265(Mirror,Axis_1_265,Axis_2_265,Normal_265,Target_point)"
  Placement = pos=(-107437,-412477,9.6377e-12) rot=(0,0,1;0rad)
  shape: bbox 10000 x 31.86 x 10000 mm, 1 faces, 0 solids (baked)
FEATURE [Part::Line] Normal_265
  AttacherType = Attacher::AttachEngine3D
  X1 = -107437
  X2 = -107437
  Y1 = 372240
  Y2 = 371240
  Z1 = 0
  Z2 = 0
FEATURE [Part::Line] Axis_1_265
  AttacherType = Attacher::AttachEngine3D
  X1 = -107437
  X2 = -107437
  Y1 = 372240
  Y2 = 372240
  Z1 = 0
  Z2 = -1000
FEATURE [Part::Line] Axis_2_265
  AttacherType = Attacher::AttachEngine3D
  X1 = -107437
  X2 = -108437
  Y1 = 372240
  Y2 = 372240
  Z1 = 0
  Z2 = 0
FEATURE [Part::Feature] Heliostat_266  label="Heliostat_266(Mirror,Axis_1_266,Axis_2_266,Normal_266,Target_point)"
  Placement = pos=(173412,-320748,6.0785e-12) rot=(0,0,1;0rad)
  shape: bbox 10000 x 55.53 x 10000 mm, 1 faces, 0 solids (baked)
FEATURE [Part::Line] Normal_266
  AttacherType = Attacher::AttachEngine3D
  X1 = 173412
  X2 = 173412
  Y1 = 129472
  Y2 = 128472
  Z1 = 0
  Z2 = 0
FEATURE [Part::Line] Axis_1_266
  AttacherType = Attacher::AttachEngine3D
  X1 = 173412
  X2 = 173412
  Y1 = 129472
  Y2 = 129472
  Z1 = 0
  Z2 = -1000
FEATURE [Part::Line] Axis_2_266
  AttacherType = Attacher::AttachEngine3D
  X1 = 173412
  X2 = 172412
  Y1 = 129472
  Y2 = 129472
  Z1 = 0
  Z2 = 0
FEATURE [Part::Feature] Heliostat_267  label="Heliostat_267(Mirror,Axis_1_267,Axis_2_267,Normal_267,Target_point)"
  Placement = pos=(-173412,-320748,6.0785e-12) rot=(0,0,1;0rad)
  shape: bbox 10000 x 55.53 x 10000 mm, 1 faces, 0 solids (baked)
FEATURE [Part::Line] Normal_267
  AttacherType = Attacher::AttachEngine3D
  X1 = -173412
  X2 = -173412
  Y1 = 129472
  Y2 = 128472
  Z1 = 0
  Z2 = 0
FEATURE [Part::Line] Axis_1_267
  AttacherType = Attacher::AttachEngine3D
  X1 = -173412
  X2 = -173412
  Y1 = 129472
  Y2 = 129472
  Z1 = 0
  Z2 = -1000
FEATURE [Part::Line] Axis_2_267
  AttacherType = Attacher::AttachEngine3D
  X1 = -173412
  X2 = -174412
  Y1 = 129472
  Y2 = 129472
  Z1 = 0
  Z2 = 0
FEATURE [Part::Feature] Heliostat_268  label="Heliostat_268(Mirror,Axis_1_268,Axis_2_268,Normal_268,Target_point)"
  Placement = pos=(166198,-307454,4.05393e-11) rot=(0,0,1;0rad)
  shape: bbox 10000 x 59.82 x 10000 mm, 1 faces, 0 solids (baked)
FEATURE [Part::Line] Normal_268
  AttacherType = Attacher::AttachEngine3D
  X1 = 166198
  X2 = 166198
  Y1 = 110476
  Y2 = 109476
  Z1 = 0
  Z2 = 0
FEATURE [Part::Line] Axis_1_268
  AttacherType = Attacher::AttachEngine3D
  X1 = 166198
  X2 = 166198
  Y1 = 110476
  Y2 = 110476
  Z1 = 0
  Z2 = -1000
FEATURE [Part::Line] Axis_2_268
  AttacherType = Attacher::AttachEngine3D
  X1 = 166198
  X2 = 165198
  Y1 = 110476
  Y2 = 110476
  Z1 = 0
  Z2 = 0
FEATURE [Part::Feature] Heliostat_269  label="Heliostat_269(Mirror,Axis_1_269,Axis_2_269,Normal_269,Target_point)"
  Placement = pos=(-166198,-307454,4.05393e-11) rot=(0,0,1;0rad)
  shape: bbox 10000 x 59.82 x 10000 mm, 1 faces, 0 solids (baked)
FEATURE [Part::Line] Normal_269
  AttacherType = Attacher::AttachEngine3D
  X1 = -166198
  X2 = -166198
  Y1 = 110476
  Y2 = 109476
  Z1 = 0
  Z2 = 0
FEATURE [Part::Line] Axis_1_269
  AttacherType = Attacher::AttachEngine3D
  X1 = -166198
  X2 = -166198
  Y1 = 110476
  Y2 = 110476
  Z1 = 0
  Z2 = -1000
FEATURE [Part::Line] Axis_2_269
  AttacherType = Attacher::AttachEngine3D
  X1 = -166198
  X2 = -167198
  Y1 = 110476
  Y2 = 110476
  Z1 = 0
  Z2 = 0
FEATURE [Part::Feature] Heliostat_270  label="Heliostat_270(Mirror,Axis_1_270,Axis_2_270,Normal_270,Target_point)"
  Placement = pos=(19969.5,-271354,1.86587e-10) rot=(0,0,1;0rad)
  shape: bbox 10000 x 47.5 x 10000 mm, 1 faces, 0 solids (baked)
FEATURE [Part::Line] Normal_270
  AttacherType = Attacher::AttachEngine3D
  X1 = 19969.5
  X2 = 19969.5
  Y1 = 254994
  Y2 = 253994
  Z1 = 0
  Z2 = 0
FEATURE [Part::Line] Axis_1_270
  AttacherType = Attacher::AttachEngine3D
  X1 = 19969.5
  X2 = 19969.5
  Y1 = 254994
  Y2 = 254994
  Z1 = 0
  Z2 = -1000
FEATURE [Part::Line] Axis_2_270
  AttacherType = Attacher::AttachEngine3D
  X1 = 19969.5
  X2 = 18969.5
  Y1 = 254994
  Y2 = 254994
  Z1 = 0
  Z2 = 0
FEATURE [Part::Feature] Heliostat_271  label="Heliostat_271(Mirror,Axis_1_271,Axis_2_271,Normal_271,Target_point)"
  Placement = pos=(-19969.5,-271354,1.86587e-10) rot=(0,0,1;0rad)
  shape: bbox 10000 x 47.5 x 10000 mm, 1 faces, 0 solids (baked)
FEATURE [Part::Line] Normal_271
  AttacherType = Attacher::AttachEngine3D
  X1 = -19969.5
  X2 = -19969.5
  Y1 = 254994
  Y2 = 253994
  Z1 = 0
  Z2 = 0
FEATURE [Part::Line] Axis_1_271
  AttacherType = Attacher::AttachEngine3D
  X1 = -19969.5
  X2 = -19969.5
  Y1 = 254994
  Y2 = 254994
  Z1 = 0
  Z2 = -1000
FEATURE [Part::Line] Axis_2_271
  AttacherType = Attacher::AttachEngine3D
  X1 = -19969.5
  X2 = -20969.5
  Y1 = 254994
  Y2 = 254994
  Z1 = 0
  Z2 = 0
FEATURE [Part::Feature] Heliostat_272  label="Heliostat_272(Mirror,Axis_1_272,Axis_2_272,Normal_272,Target_point)"
  Placement = pos=(128175,-419099,1.48498e-10) rot=(0,0,1;0rad)
  shape: bbox 10000 x 31.86 x 10000 mm, 1 faces, 0 solids (baked)
FEATURE [Part::Line] Normal_272
  AttacherType = Attacher::AttachEngine3D
  X1 = 128175
  X2 = 128175
  Y1 = 365617
  Y2 = 364617
  Z1 = 0
  Z2 = 0
FEATURE [Part::Line] Axis_1_272
  AttacherType = Attacher::AttachEngine3D
  X1 = 128175
  X2 = 128175
  Y1 = 365617
  Y2 = 365617
  Z1 = 0
  Z2 = -1000
FEATURE [Part::Line] Axis_2_272
  AttacherType = Attacher::AttachEngine3D
  X1 = 128175
  X2 = 127175
  Y1 = 365617
  Y2 = 365617
  Z1 = 0
  Z2 = 0
FEATURE [Part::Feature] Heliostat_273  label="Heliostat_273(Mirror,Axis_1_273,Axis_2_273,Normal_273,Target_point)"
  Placement = pos=(-128175,-419099,1.48498e-10) rot=(0,0,1;0rad)
  shape: bbox 10000 x 31.86 x 10000 mm, 1 faces, 0 solids (baked)
FEATURE [Part::Line] Normal_273
  AttacherType = Attacher::AttachEngine3D
  X1 = -128175
  X2 = -128175
  Y1 = 365617
  Y2 = 364617
  Z1 = 0
  Z2 = 0
FEATURE [Part::Line] Axis_1_273
  AttacherType = Attacher::AttachEngine3D
  X1 = -128175
  X2 = -128175
  Y1 = 365617
  Y2 = 365617
  Z1 = 0
  Z2 = -1000
FEATURE [Part::Line] Axis_2_273
  AttacherType = Attacher::AttachEngine3D
  X1 = -128175
  X2 = -129175
  Y1 = 365617
  Y2 = 365617
  Z1 = 0
  Z2 = 0
FEATURE [Part::Feature] Heliostat_274  label="Heliostat_274(Mirror,Axis_1_274,Axis_2_274,Normal_274,Target_point)"
  Placement = pos=(195227,-386061,5.83394e-11) rot=(0,0,1;0rad)
  shape: bbox 10000 x 40.57 x 10000 mm, 1 faces, 0 solids (baked)
FEATURE [Part::Line] Normal_274
  AttacherType = Attacher::AttachEngine3D
  X1 = 195227
  X2 = 195227
  Y1 = 230194
  Y2 = 229194
  Z1 = 0
  Z2 = 0
FEATURE [Part::Line] Axis_1_274
  AttacherType = Attacher::AttachEngine3D
  X1 = 195227
  X2 = 195227
  Y1 = 230194
  Y2 = 230194
  Z1 = 0
  Z2 = -1000
FEATURE [Part::Line] Axis_2_274
  AttacherType = Attacher::AttachEngine3D
  X1 = 195227
  X2 = 194227
  Y1 = 230194
  Y2 = 230194
  Z1 = 0
  Z2 = 0
FEATURE [Part::Feature] Heliostat_275  label="Heliostat_275(Mirror,Axis_1_275,Axis_2_275,Normal_275,Target_point)"
  Placement = pos=(-195227,-386061,5.83394e-11) rot=(0,0,1;0rad)
  shape: bbox 10000 x 40.57 x 10000 mm, 1 faces, 0 solids (baked)
FEATURE [Part::Line] Normal_275
  AttacherType = Attacher::AttachEngine3D
  X1 = -195227
  X2 = -195227
  Y1 = 230194
  Y2 = 229194
  Z1 = 0
  Z2 = 0
FEATURE [Part::Line] Axis_1_275
  AttacherType = Attacher::AttachEngine3D
  X1 = -195227
  X2 = -195227
  Y1 = 230194
  Y2 = 230194
  Z1 = 0
  Z2 = -1000
FEATURE [Part::Line] Axis_2_275
  AttacherType = Attacher::AttachEngine3D
  X1 = -195227
  X2 = -196227
  Y1 = 230194
  Y2 = 230194
  Z1 = 0
  Z2 = 0
FEATURE [Part::Feature] Heliostat_276  label="Heliostat_276(Mirror,Axis_1_276,Axis_2_276,Normal_276,Target_point)"
  Placement = pos=(85542.2,-189622,6.92563e-11) rot=(0,0,1;0rad)
  shape: bbox 10000 x 113.9 x 10000 mm, 1 faces, 0 solids (baked)
FEATURE [Part::Line] Normal_276
  AttacherType = Attacher::AttachEngine3D
  X1 = 85542.2
  X2 = 85542.2
  Y1 = 29975.6
  Y2 = 28975.6
  Z1 = 0
  Z2 = 0
FEATURE [Part::Line] Axis_1_276
  AttacherType = Attacher::AttachEngine3D
  X1 = 85542.2
  X2 = 85542.2
  Y1 = 29975.6
  Y2 = 29975.6
  Z1 = 0
  Z2 = -1000
FEATURE [Part::Line] Axis_2_276
  AttacherType = Attacher::AttachEngine3D
  X1 = 85542.2
  X2 = 84542.2
  Y1 = 29975.6
  Y2 = 29975.6
  Z1 = 0
  Z2 = 0
FEATURE [Part::Feature] Heliostat_277  label="Heliostat_277(Mirror,Axis_1_277,Axis_2_277,Normal_277,Target_point)"
  Placement = pos=(-85542.2,-189622,6.92563e-11) rot=(0,0,1;0rad)
  shape: bbox 10000 x 113.9 x 10000 mm, 1 faces, 0 solids (baked)
FEATURE [Part::Line] Normal_277
  AttacherType = Attacher::AttachEngine3D
  X1 = -85542.2
  X2 = -85542.2
  Y1 = 29975.6
  Y2 = 28975.6
  Z1 = 0
  Z2 = 0
FEATURE [Part::Line] Axis_1_277
  AttacherType = Attacher::AttachEngine3D
  X1 = -85542.2
  X2 = -85542.2
  Y1 = 29975.6
  Y2 = 29975.6
  Z1 = 0
  Z2 = -1000
FEATURE [Part::Line] Axis_2_277
  AttacherType = Attacher::AttachEngine3D
  X1 = -85542.2
  X2 = -86542.2
  Y1 = 29975.6
  Y2 = 29975.6
  Z1 = 0
  Z2 = 0
FEATURE [Part::Feature] Heliostat_278  label="Heliostat_278(Mirror,Axis_1_278,Axis_2_278,Normal_278,Target_point)"
  Placement = pos=(181180,-336807,4.94649e-11) rot=(0,0,1;0rad)
  shape: bbox 10000 x 51.21 x 10000 mm, 1 faces, 0 solids (baked)
FEATURE [Part::Line] Normal_278
  AttacherType = Attacher::AttachEngine3D
  X1 = 181180
  X2 = 181180
  Y1 = 151373
  Y2 = 150373
  Z1 = 0
  Z2 = 0
FEATURE [Part::Line] Axis_1_278
  AttacherType = Attacher::AttachEngine3D
  X1 = 181180
  X2 = 181180
  Y1 = 151373
  Y2 = 151373
  Z1 = 0
  Z2 = -1000
FEATURE [Part::Line] Axis_2_278
  AttacherType = Attacher::AttachEngine3D
  X1 = 181180
  X2 = 180180
  Y1 = 151373
  Y2 = 151373
  Z1 = 0
  Z2 = 0
FEATURE [Part::Feature] Heliostat_279  label="Heliostat_279(Mirror,Axis_1_279,Axis_2_279,Normal_279,Target_point)"
  Placement = pos=(-181180,-336807,4.94649e-11) rot=(0,0,1;0rad)
  shape: bbox 10000 x 51.21 x 10000 mm, 1 faces, 0 solids (baked)
FEATURE [Part::Line] Normal_279
  AttacherType = Attacher::AttachEngine3D
  X1 = -181180
  X2 = -181180
  Y1 = 151373
  Y2 = 150373
  Z1 = 0
  Z2 = 0
FEATURE [Part::Line] Axis_1_279
  AttacherType = Attacher::AttachEngine3D
  X1 = -181180
  X2 = -181180
  Y1 = 151373
  Y2 = 151373
  Z1 = 0
  Z2 = -1000
FEATURE [Part::Line] Axis_2_279
  AttacherType = Attacher::AttachEngine3D
  X1 = -181180
  X2 = -182180
  Y1 = 151373
  Y2 = 151373
  Z1 = 0
  Z2 = 0
FEATURE [Part::Feature] Heliostat_280  label="Heliostat_280(Mirror,Axis_1_280,Axis_2_280,Normal_280,Target_point)"
  Placement = pos=(163565,-406332,1.97655e-10) rot=(0,0,1;0rad)
  shape: bbox 10000 x 34.61 x 10000 mm, 1 faces, 0 solids (baked)
FEATURE [Part::Line] Normal_280
  AttacherType = Attacher::AttachEngine3D
  X1 = 163565
  X2 = 163565
  Y1 = 315969
  Y2 = 314969
  Z1 = 0
  Z2 = 0
FEATURE [Part::Line] Axis_1_280
  AttacherType = Attacher::AttachEngine3D
  X1 = 163565
  X2 = 163565
  Y1 = 315969
  Y2 = 315969
  Z1 = 0
  Z2 = -1000
FEATURE [Part::Line] Axis_2_280
  AttacherType = Attacher::AttachEngine3D
  X1 = 163565
  X2 = 162565
  Y1 = 315969
  Y2 = 315969
  Z1 = 0
  Z2 = 0
FEATURE [Part::Feature] Heliostat_281  label="Heliostat_281(Mirror,Axis_1_281,Axis_2_281,Normal_281,Target_point)"
  Placement = pos=(-163565,-406332,1.97655e-10) rot=(0,0,1;0rad)
  shape: bbox 10000 x 34.61 x 10000 mm, 1 faces, 0 solids (baked)
FEATURE [Part::Line] Normal_281
  AttacherType = Attacher::AttachEngine3D
  X1 = -163565
  X2 = -163565
  Y1 = 315969
  Y2 = 314969
  Z1 = 0
  Z2 = 0
FEATURE [Part::Line] Axis_1_281
  AttacherType = Attacher::AttachEngine3D
  X1 = -163565
  X2 = -163565
  Y1 = 315969
  Y2 = 315969
  Z1 = 0
  Z2 = -1000
FEATURE [Part::Line] Axis_2_281
  AttacherType = Attacher::AttachEngine3D
  X1 = -163565
  X2 = -164565
  Y1 = 315969
  Y2 = 315969
  Z1 = 0
  Z2 = 0
FEATURE [Part::Feature] Heliostat_282  label="Heliostat_282(Mirror,Axis_1_282,Axis_2_282,Normal_282,Target_point)"
  Placement = pos=(132863,-254156,3.36582e-11) rot=(0,0,1;0rad)
  shape: bbox 10000 x 75.38 x 10000 mm, 1 faces, 0 solids (baked)
FEATURE [Part::Line] Normal_282
  AttacherType = Attacher::AttachEngine3D
  X1 = 132863
  X2 = 132863
  Y1 = 77488.6
  Y2 = 76488.6
  Z1 = 0
  Z2 = 0
FEATURE [Part::Line] Axis_1_282
  AttacherType = Attacher::AttachEngine3D
  X1 = 132863
  X2 = 132863
  Y1 = 77488.6
  Y2 = 77488.6
  Z1 = 0
  Z2 = -1000
FEATURE [Part::Line] Axis_2_282
  AttacherType = Attacher::AttachEngine3D
  X1 = 132863
  X2 = 131863
  Y1 = 77488.6
  Y2 = 77488.6
  Z1 = 0
  Z2 = 0
FEATURE [Part::Feature] Heliostat_283  label="Heliostat_283(Mirror,Axis_1_283,Axis_2_283,Normal_283,Target_point)"
  Placement = pos=(-132863,-254156,3.36582e-11) rot=(0,0,1;0rad)
  shape: bbox 10000 x 75.38 x 10000 mm, 1 faces, 0 solids (baked)
FEATURE [Part::Line] Normal_283
  AttacherType = Attacher::AttachEngine3D
  X1 = -132863
  X2 = -132863
  Y1 = 77488.6
  Y2 = 76488.6
  Z1 = 0
  Z2 = 0
FEATURE [Part::Line] Axis_1_283
  AttacherType = Attacher::AttachEngine3D
  X1 = -132863
  X2 = -132863
  Y1 = 77488.6
  Y2 = 77488.6
  Z1 = 0
  Z2 = -1000
FEATURE [Part::Line] Axis_2_283
  AttacherType = Attacher::AttachEngine3D
  X1 = -132863
  X2 = -133863
  Y1 = 77488.6
  Y2 = 77488.6
  Z1 = 0
  Z2 = 0
FEATURE [Part::Feature] Heliostat_284  label="Heliostat_284(Mirror,Axis_1_284,Axis_2_284,Normal_284,Target_point)"
  Placement = pos=(181888,-395278,1.74384e-10) rot=(0,0,1;0rad)
  shape: bbox 10000 x 37.36 x 10000 mm, 1 faces, 0 solids (baked)
FEATURE [Part::Line] Normal_284
  AttacherType = Attacher::AttachEngine3D
  X1 = 181888
  X2 = 181888
  Y1 = 273926
  Y2 = 272926
  Z1 = 0
  Z2 = 0
FEATURE [Part::Line] Axis_1_284
  AttacherType = Attacher::AttachEngine3D
  X1 = 181888
  X2 = 181888
  Y1 = 273926
  Y2 = 273926
  Z1 = 0
  Z2 = -1000
FEATURE [Part::Line] Axis_2_284
  AttacherType = Attacher::AttachEngine3D
  X1 = 181888
  X2 = 180888
  Y1 = 273926
  Y2 = 273926
  Z1 = 0
  Z2 = 0
FEATURE [Part::Feature] Heliostat_285  label="Heliostat_285(Mirror,Axis_1_285,Axis_2_285,Normal_285,Target_point)"
  Placement = pos=(-181888,-395278,1.74384e-10) rot=(0,0,1;0rad)
  shape: bbox 10000 x 37.36 x 10000 mm, 1 faces, 0 solids (baked)
FEATURE [Part::Line] Normal_285
  AttacherType = Attacher::AttachEngine3D
  X1 = -181888
  X2 = -181888
  Y1 = 273926
  Y2 = 272926
  Z1 = 0
  Z2 = 0
FEATURE [Part::Line] Axis_1_285
  AttacherType = Attacher::AttachEngine3D
  X1 = -181888
  X2 = -181888
  Y1 = 273926
  Y2 = 273926
  Z1 = 0
  Z2 = -1000
FEATURE [Part::Line] Axis_2_285
  AttacherType = Attacher::AttachEngine3D
  X1 = -181888
  X2 = -182888
  Y1 = 273926
  Y2 = 273926
  Z1 = 0
  Z2 = 0
FEATURE [Part::Feature] Heliostat_286  label="Heliostat_286(Mirror,Axis_1_286,Axis_2_286,Normal_286,Target_point)"
  Placement = pos=(148509,-426875,1.44071e-10) rot=(0,0,1;0rad)
  shape: bbox 10000 x 31.86 x 10000 mm, 1 faces, 0 solids (baked)
FEATURE [Part::Line] Normal_286
  AttacherType = Attacher::AttachEngine3D
  X1 = 148509
  X2 = 148509
  Y1 = 357841
  Y2 = 356841
  Z1 = 0
  Z2 = 0
FEATURE [Part::Line] Axis_1_286
  AttacherType = Attacher::AttachEngine3D
  X1 = 148509
  X2 = 148509
  Y1 = 357841
  Y2 = 357841
  Z1 = 0
  Z2 = -1000
FEATURE [Part::Line] Axis_2_286
  AttacherType = Attacher::AttachEngine3D
  X1 = 148509
  X2 = 147509
  Y1 = 357841
  Y2 = 357841
  Z1 = 0
  Z2 = 0
FEATURE [Part::Feature] Heliostat_287  label="Heliostat_287(Mirror,Axis_1_287,Axis_2_287,Normal_287,Target_point)"
  Placement = pos=(-148509,-426875,1.44071e-10) rot=(0,0,1;0rad)
  shape: bbox 10000 x 31.86 x 10000 mm, 1 faces, 0 solids (baked)
FEATURE [Part::Line] Normal_287
  AttacherType = Attacher::AttachEngine3D
  X1 = -148509
  X2 = -148509
  Y1 = 357841
  Y2 = 356841
  Z1 = 0
  Z2 = 0
FEATURE [Part::Line] Axis_1_287
  AttacherType = Attacher::AttachEngine3D
  X1 = -148509
  X2 = -148509
  Y1 = 357841
  Y2 = 357841
  Z1 = 0
  Z2 = -1000
FEATURE [Part::Line] Axis_2_287
  AttacherType = Attacher::AttachEngine3D
  X1 = -148509
  X2 = -149509
  Y1 = 357841
  Y2 = 357841
  Z1 = 0
  Z2 = 0
FEATURE [Part::Feature] Heliostat_288  label="Heliostat_288(Mirror,Axis_1_288,Axis_2_288,Normal_288,Target_point)"
  Placement = pos=(203964,-381134,5.58821e-11) rot=(0,0,1;0rad)
  shape: bbox 10000 x 43.77 x 10000 mm, 1 faces, 0 solids (baked)
FEATURE [Part::Line] Normal_288
  AttacherType = Attacher::AttachEngine3D
  X1 = 203964
  X2 = 203964
  Y1 = 190080
  Y2 = 189080
  Z1 = 0
  Z2 = 0
FEATURE [Part::Line] Axis_1_288
  AttacherType = Attacher::AttachEngine3D
  X1 = 203964
  X2 = 203964
  Y1 = 190080
  Y2 = 190080
  Z1 = 0
  Z2 = -1000
FEATURE [Part::Line] Axis_2_288
  AttacherType = Attacher::AttachEngine3D
  X1 = 203964
  X2 = 202964
  Y1 = 190080
  Y2 = 190080
  Z1 = 0
  Z2 = 0
FEATURE [Part::Feature] Heliostat_289  label="Heliostat_289(Mirror,Axis_1_289,Axis_2_289,Normal_289,Target_point)"
  Placement = pos=(-203964,-381134,5.58821e-11) rot=(0,0,1;0rad)
  shape: bbox 10000 x 43.77 x 10000 mm, 1 faces, 0 solids (baked)
FEATURE [Part::Line] Normal_289
  AttacherType = Attacher::AttachEngine3D
  X1 = -203964
  X2 = -203964
  Y1 = 190080
  Y2 = 189080
  Z1 = 0
  Z2 = 0
FEATURE [Part::Line] Axis_1_289
  AttacherType = Attacher::AttachEngine3D
  X1 = -203964
  X2 = -203964
  Y1 = 190080
  Y2 = 190080
  Z1 = 0
  Z2 = -1000
FEATURE [Part::Line] Axis_2_289
  AttacherType = Attacher::AttachEngine3D
  X1 = -203964
  X2 = -204964
  Y1 = 190080
  Y2 = 190080
  Z1 = 0
  Z2 = 0
FEATURE [Part::Feature] Heliostat_290  label="Heliostat_290(Mirror,Axis_1_290,Axis_2_290,Normal_290,Target_point)"
  Placement = pos=(127837,-248351,3.18246e-11) rot=(0,0,1;0rad)
  shape: bbox 10000 x 80.99 x 10000 mm, 1 faces, 0 solids (baked)
FEATURE [Part::Line] Normal_290
  AttacherType = Attacher::AttachEngine3D
  X1 = 127837
  X2 = 127837
  Y1 = 60353.4
  Y2 = 59353.4
  Z1 = 0
  Z2 = 0
FEATURE [Part::Line] Axis_1_290
  AttacherType = Attacher::AttachEngine3D
  X1 = 127837
  X2 = 127837
  Y1 = 60353.4
  Y2 = 60353.4
  Z1 = 0
  Z2 = -1000
FEATURE [Part::Line] Axis_2_290
  AttacherType = Attacher::AttachEngine3D
  X1 = 127837
  X2 = 126837
  Y1 = 60353.4
  Y2 = 60353.4
  Z1 = 0
  Z2 = 0
FEATURE [Part::Feature] Heliostat_291  label="Heliostat_291(Mirror,Axis_1_291,Axis_2_291,Normal_291,Target_point)"
  Placement = pos=(-127837,-248351,3.18246e-11) rot=(0,0,1;0rad)
  shape: bbox 10000 x 80.99 x 10000 mm, 1 faces, 0 solids (baked)
FEATURE [Part::Line] Normal_291
  AttacherType = Attacher::AttachEngine3D
  X1 = -127837
  X2 = -127837
  Y1 = 60353.4
  Y2 = 59353.4
  Z1 = 0
  Z2 = 0
FEATURE [Part::Line] Axis_1_291
  AttacherType = Attacher::AttachEngine3D
  X1 = -127837
  X2 = -127837
  Y1 = 60353.4
  Y2 = 60353.4
  Z1 = 0
  Z2 = -1000
FEATURE [Part::Line] Axis_2_291
  AttacherType = Attacher::AttachEngine3D
  X1 = -127837
  X2 = -128837
  Y1 = 60353.4
  Y2 = 60353.4
  Z1 = 0
  Z2 = 0
FEATURE [Part::Feature] Heliostat_292  label="Heliostat_292(Mirror,Axis_1_292,Axis_2_292,Normal_292,Target_point)"
  Placement = pos=(176659,-371522,1.00815e-10) rot=(0,0,1;0rad)
  shape: bbox 10000 x 40.57 x 10000 mm, 1 faces, 0 solids (baked)
FEATURE [Part::Line] Normal_292
  AttacherType = Attacher::AttachEngine3D
  X1 = 176659
  X2 = 176659
  Y1 = 244734
  Y2 = 243734
  Z1 = 0
  Z2 = 0
FEATURE [Part::Line] Axis_1_292
  AttacherType = Attacher::AttachEngine3D
  X1 = 176659
  X2 = 176659
  Y1 = 244734
  Y2 = 244734
  Z1 = 0
  Z2 = -1000
FEATURE [Part::Line] Axis_2_292
  AttacherType = Attacher::AttachEngine3D
  X1 = 176659
  X2 = 175659
  Y1 = 244734
  Y2 = 244734
  Z1 = 0
  Z2 = 0
FEATURE [Part::Feature] Heliostat_293  label="Heliostat_293(Mirror,Axis_1_293,Axis_2_293,Normal_293,Target_point)"
  Placement = pos=(-176659,-371522,1.00815e-10) rot=(0,0,1;0rad)
  shape: bbox 10000 x 40.57 x 10000 mm, 1 faces, 0 solids (baked)
FEATURE [Part::Line] Normal_293
  AttacherType = Attacher::AttachEngine3D
  X1 = -176659
  X2 = -176659
  Y1 = 244734
  Y2 = 243734
  Z1 = 0
  Z2 = 0
FEATURE [Part::Line] Axis_1_293
  AttacherType = Attacher::AttachEngine3D
  X1 = -176659
  X2 = -176659
  Y1 = 244734
  Y2 = 244734
  Z1 = 0
  Z2 = -1000
FEATURE [Part::Line] Axis_2_293
  AttacherType = Attacher::AttachEngine3D
  X1 = -176659
  X2 = -177659
  Y1 = 244734
  Y2 = 244734
  Z1 = 0
  Z2 = 0
FEATURE [Part::Feature] Heliostat_294  label="Heliostat_294(Mirror,Axis_1_294,Axis_2_294,Normal_294,Target_point)"
  Placement = pos=(188501,-365790,5.87511e-11) rot=(0,0,1;0rad)
  shape: bbox 10000 x 43.77 x 10000 mm, 1 faces, 0 solids (baked)
FEATURE [Part::Line] Normal_294
  AttacherType = Attacher::AttachEngine3D
  X1 = 188501
  X2 = 188501
  Y1 = 205424
  Y2 = 204424
  Z1 = 0
  Z2 = 0
FEATURE [Part::Line] Axis_1_294
  AttacherType = Attacher::AttachEngine3D
  X1 = 188501
  X2 = 188501
  Y1 = 205424
  Y2 = 205424
  Z1 = 0
  Z2 = -1000
FEATURE [Part::Line] Axis_2_294
  AttacherType = Attacher::AttachEngine3D
  X1 = 188501
  X2 = 187501
  Y1 = 205424
  Y2 = 205424
  Z1 = 0
  Z2 = 0
FEATURE [Part::Feature] Heliostat_295  label="Heliostat_295(Mirror,Axis_1_295,Axis_2_295,Normal_295,Target_point)"
  Placement = pos=(-188501,-365790,5.87511e-11) rot=(0,0,1;0rad)
  shape: bbox 10000 x 43.77 x 10000 mm, 1 faces, 0 solids (baked)
FEATURE [Part::Line] Normal_295
  AttacherType = Attacher::AttachEngine3D
  X1 = -188501
  X2 = -188501
  Y1 = 205424
  Y2 = 204424
  Z1 = 0
  Z2 = 0
FEATURE [Part::Line] Axis_1_295
  AttacherType = Attacher::AttachEngine3D
  X1 = -188501
  X2 = -188501
  Y1 = 205424
  Y2 = 205424
  Z1 = 0
  Z2 = -1000
FEATURE [Part::Line] Axis_2_295
  AttacherType = Attacher::AttachEngine3D
  X1 = -188501
  X2 = -189501
  Y1 = 205424
  Y2 = 205424
  Z1 = 0
  Z2 = 0
FEATURE [Part::Feature] Heliostat_296  label="Heliostat_296(Mirror,Axis_1_296,Axis_2_296,Normal_296,Target_point)"
  Placement = pos=(171887,-351700,1.05176e-10) rot=(0,0,1;0rad)
  shape: bbox 10000 x 43.77 x 10000 mm, 1 faces, 0 solids (baked)
FEATURE [Part::Line] Normal_296
  AttacherType = Attacher::AttachEngine3D
  X1 = 171887
  X2 = 171887
  Y1 = 219514
  Y2 = 218514
  Z1 = 0
  Z2 = 0
FEATURE [Part::Line] Axis_1_296
  AttacherType = Attacher::AttachEngine3D
  X1 = 171887
  X2 = 171887
  Y1 = 219514
  Y2 = 219514
  Z1 = 0
  Z2 = -1000
FEATURE [Part::Line] Axis_2_296
  AttacherType = Attacher::AttachEngine3D
  X1 = 171887
  X2 = 170887
  Y1 = 219514
  Y2 = 219514
  Z1 = 0
  Z2 = 0
FEATURE [Part::Feature] Heliostat_297  label="Heliostat_297(Mirror,Axis_1_297,Axis_2_297,Normal_297,Target_point)"
  Placement = pos=(-171887,-351700,1.05176e-10) rot=(0,0,1;0rad)
  shape: bbox 10000 x 43.77 x 10000 mm, 1 faces, 0 solids (baked)
FEATURE [Part::Line] Normal_297
  AttacherType = Attacher::AttachEngine3D
  X1 = -171887
  X2 = -171887
  Y1 = 219514
  Y2 = 218514
  Z1 = 0
  Z2 = 0
FEATURE [Part::Line] Axis_1_297
  AttacherType = Attacher::AttachEngine3D
  X1 = -171887
  X2 = -171887
  Y1 = 219514
  Y2 = 219514
  Z1 = 0
  Z2 = -1000
FEATURE [Part::Line] Axis_2_297
  AttacherType = Attacher::AttachEngine3D
  X1 = -171887
  X2 = -172887
  Y1 = 219514
  Y2 = 219514
  Z1 = 0
  Z2 = 0
FEATURE [Part::Feature] Heliostat_298  label="Heliostat_298(Mirror,Axis_1_298,Axis_2_298,Normal_298,Target_point)"
  Placement = pos=(-159946,-381913,1.77539e-10) rot=(0,0,1;0rad)
  shape: bbox 10000 x 37.36 x 10000 mm, 1 faces, 0 solids (baked)
FEATURE [Part::Line] Normal_298
  AttacherType = Attacher::AttachEngine3D
  X1 = -159946
  X2 = -159946
  Y1 = 287291
  Y2 = 286291
  Z1 = 0
  Z2 = 0
FEATURE [Part::Line] Axis_1_298
  AttacherType = Attacher::AttachEngine3D
  X1 = -159946
  X2 = -159946
  Y1 = 287291
  Y2 = 287291
  Z1 = 0
  Z2 = -1000
FEATURE [Part::Line] Axis_2_298
  AttacherType = Attacher::AttachEngine3D
  X1 = -159946
  X2 = -160946
  Y1 = 287291
  Y2 = 287291
  Z1 = 0
  Z2 = 0
FEATURE [Part::Feature] Heliostat_299  label="Heliostat_299(Mirror,Axis_1_299,Axis_2_299,Normal_299,Target_point)"
  Placement = pos=(159946,-381913,1.77539e-10) rot=(0,0,1;0rad)
  shape: bbox 10000 x 37.36 x 10000 mm, 1 faces, 0 solids (baked)
FEATURE [Part::Line] Normal_299
  AttacherType = Attacher::AttachEngine3D
  X1 = 159946
  X2 = 159946
  Y1 = 287291
  Y2 = 286291
  Z1 = 0
  Z2 = 0
FEATURE [Part::Line] Axis_1_299
  AttacherType = Attacher::AttachEngine3D
  X1 = 159946
  X2 = 159946
  Y1 = 287291
  Y2 = 287291
  Z1 = 0
  Z2 = -1000
FEATURE [Part::Line] Axis_2_299
  AttacherType = Attacher::AttachEngine3D
  X1 = 159946
  X2 = 158946
  Y1 = 287291
  Y2 = 287291
  Z1 = 0
  Z2 = 0
FEATURE [Part::Feature] Heliostat_300  label="Heliostat_300(Mirror,Axis_1_300,Axis_2_300,Normal_300,Target_point)"
  Placement = pos=(108228,-383367,1.63382e-10) rot=(0,0,1;0rad)
  shape: bbox 10000 x 34.61 x 10000 mm, 1 faces, 0 solids (baked)
FEATURE [Part::Line] Normal_300
  AttacherType = Attacher::AttachEngine3D
  X1 = 108228
  X2 = 108228
  Y1 = 338934
  Y2 = 337934
  Z1 = 0
  Z2 = 0
FEATURE [Part::Line] Axis_1_300
  AttacherType = Attacher::AttachEngine3D
  X1 = 108228
  X2 = 108228
  Y1 = 338934
  Y2 = 338934
  Z1 = 0
  Z2 = -1000
FEATURE [Part::Line] Axis_2_300
  AttacherType = Attacher::AttachEngine3D
  X1 = 108228
  X2 = 107228
  Y1 = 338934
  Y2 = 338934
  Z1 = 0
  Z2 = 0
FEATURE [Part::Feature] Heliostat_301  label="Heliostat_301(Mirror,Axis_1_301,Axis_2_301,Normal_301,Target_point)"
  Placement = pos=(-108228,-383367,1.63382e-10) rot=(0,0,1;0rad)
  shape: bbox 10000 x 34.61 x 10000 mm, 1 faces, 0 solids (baked)
FEATURE [Part::Line] Normal_301
  AttacherType = Attacher::AttachEngine3D
  X1 = -108228
  X2 = -108228
  Y1 = 338934
  Y2 = 337934
  Z1 = 0
  Z2 = 0
FEATURE [Part::Line] Axis_1_301
  AttacherType = Attacher::AttachEngine3D
  X1 = -108228
  X2 = -108228
  Y1 = 338934
  Y2 = 338934
  Z1 = 0
  Z2 = -1000
FEATURE [Part::Line] Axis_2_301
  AttacherType = Attacher::AttachEngine3D
  X1 = -108228
  X2 = -109228
  Y1 = 338934
  Y2 = 338934
  Z1 = 0
  Z2 = 0
FEATURE [Part::Feature] Heliostat_302  label="Heliostat_302(Mirror,Axis_1_302,Axis_2_302,Normal_302,Target_point)"
  Placement = pos=(86359.5,-407030,2.08325e-10) rot=(0,0,1;0rad)
  shape: bbox 10000 x 31.86 x 10000 mm, 1 faces, 0 solids (baked)
FEATURE [Part::Line] Normal_302
  AttacherType = Attacher::AttachEngine3D
  X1 = 86359.5
  X2 = 86359.5
  Y1 = 377686
  Y2 = 376686
  Z1 = 0
  Z2 = 0
FEATURE [Part::Line] Axis_1_302
  AttacherType = Attacher::AttachEngine3D
  X1 = 86359.5
  X2 = 86359.5
  Y1 = 377686
  Y2 = 377686
  Z1 = 0
  Z2 = -1000
FEATURE [Part::Line] Axis_2_302
  AttacherType = Attacher::AttachEngine3D
  X1 = 86359.5
  X2 = 85359.5
  Y1 = 377686
  Y2 = 377686
  Z1 = 0
  Z2 = 0
FEATURE [Part::Feature] Heliostat_303  label="Heliostat_303(Mirror,Axis_1_303,Axis_2_303,Normal_303,Target_point)"
  Placement = pos=(-86359.5,-407030,2.08325e-10) rot=(0,0,1;0rad)
  shape: bbox 10000 x 31.86 x 10000 mm, 1 faces, 0 solids (baked)
FEATURE [Part::Line] Normal_303
  AttacherType = Attacher::AttachEngine3D
  X1 = -86359.5
  X2 = -86359.5
  Y1 = 377686
  Y2 = 376686
  Z1 = 0
  Z2 = 0
FEATURE [Part::Line] Axis_1_303
  AttacherType = Attacher::AttachEngine3D
  X1 = -86359.5
  X2 = -86359.5
  Y1 = 377686
  Y2 = 377686
  Z1 = 0
  Z2 = -1000
FEATURE [Part::Line] Axis_2_303
  AttacherType = Attacher::AttachEngine3D
  X1 = -86359.5
  X2 = -87359.5
  Y1 = 377686
  Y2 = 377686
  Z1 = 0
  Z2 = 0
FEATURE [Part::Feature] Heliostat_304  label="Heliostat_304(Mirror,Axis_1_304,Axis_2_304,Normal_304,Target_point)"
  Placement = pos=(137444,-261557,6.51989e-11) rot=(0,0,1;0rad)
  shape: bbox 10000 x 69.71 x 10000 mm, 1 faces, 0 solids (baked)
FEATURE [Part::Line] Normal_304
  AttacherType = Attacher::AttachEngine3D
  X1 = 137444
  X2 = 137444
  Y1 = 97066.2
  Y2 = 96066.2
  Z1 = 0
  Z2 = 0
FEATURE [Part::Line] Axis_1_304
  AttacherType = Attacher::AttachEngine3D
  X1 = 137444
  X2 = 137444
  Y1 = 97066.2
  Y2 = 97066.2
  Z1 = 0
  Z2 = -1000
FEATURE [Part::Line] Axis_2_304
  AttacherType = Attacher::AttachEngine3D
  X1 = 137444
  X2 = 136444
  Y1 = 97066.2
  Y2 = 97066.2
  Z1 = 0
  Z2 = 0
FEATURE [Part::Feature] Heliostat_305  label="Heliostat_305(Mirror,Axis_1_305,Axis_2_305,Normal_305,Target_point)"
  Placement = pos=(-137444,-261557,6.51989e-11) rot=(0,0,1;0rad)
  shape: bbox 10000 x 69.71 x 10000 mm, 1 faces, 0 solids (baked)
FEATURE [Part::Line] Normal_305
  AttacherType = Attacher::AttachEngine3D
  X1 = -137444
  X2 = -137444
  Y1 = 97066.2
  Y2 = 96066.2
  Z1 = 0
  Z2 = 0
FEATURE [Part::Line] Axis_1_305
  AttacherType = Attacher::AttachEngine3D
  X1 = -137444
  X2 = -137444
  Y1 = 97066.2
  Y2 = 97066.2
  Z1 = 0
  Z2 = -1000
FEATURE [Part::Line] Axis_2_305
  AttacherType = Attacher::AttachEngine3D
  X1 = -137444
  X2 = -138444
  Y1 = 97066.2
  Y2 = 97066.2
  Z1 = 0
  Z2 = 0
FEATURE [Part::Feature] Heliostat_306  label="Heliostat_306(Mirror,Axis_1_306,Axis_2_306,Normal_306,Target_point)"
  Placement = pos=(65009.3,-402775,1.43666e-10) rot=(0,0,1;0rad)
  shape: bbox 10000 x 31.86 x 10000 mm, 1 faces, 0 solids (baked)
FEATURE [Part::Line] Normal_306
  AttacherType = Attacher::AttachEngine3D
  X1 = 65009.3
  X2 = 65009.3
  Y1 = 381941
  Y2 = 380941
  Z1 = 0
  Z2 = 0
FEATURE [Part::Line] Axis_1_306
  AttacherType = Attacher::AttachEngine3D
  X1 = 65009.3
  X2 = 65009.3
  Y1 = 381941
  Y2 = 381941
  Z1 = 0
  Z2 = -1000
FEATURE [Part::Line] Axis_2_306
  AttacherType = Attacher::AttachEngine3D
  X1 = 65009.3
  X2 = 64009.3
  Y1 = 381941
  Y2 = 381941
  Z1 = 0
  Z2 = 0
FEATURE [Part::Feature] Heliostat_307  label="Heliostat_307(Mirror,Axis_1_307,Axis_2_307,Normal_307,Target_point)"
  Placement = pos=(-65009.3,-402775,1.43666e-10) rot=(0,0,1;0rad)
  shape: bbox 10000 x 31.86 x 10000 mm, 1 faces, 0 solids (baked)
FEATURE [Part::Line] Normal_307
  AttacherType = Attacher::AttachEngine3D
  X1 = -65009.3
  X2 = -65009.3
  Y1 = 381941
  Y2 = 380941
  Z1 = 0
  Z2 = 0
FEATURE [Part::Line] Axis_1_307
  AttacherType = Attacher::AttachEngine3D
  X1 = -65009.3
  X2 = -65009.3
  Y1 = 381941
  Y2 = 381941
  Z1 = 0
  Z2 = -1000
FEATURE [Part::Line] Axis_2_307
  AttacherType = Attacher::AttachEngine3D
  X1 = -65009.3
  X2 = -66009.3
  Y1 = 381941
  Y2 = 381941
  Z1 = 0
  Z2 = 0
FEATURE [Part::Feature] Heliostat_308  label="Heliostat_308(Mirror,Axis_1_308,Axis_2_308,Normal_308,Target_point)"
  Placement = pos=(158247,-302597,4.47692e-11) rot=(0,0,1;0rad)
  shape: bbox 10000 x 55.53 x 10000 mm, 1 faces, 0 solids (baked)
FEATURE [Part::Line] Normal_308
  AttacherType = Attacher::AttachEngine3D
  X1 = 158247
  X2 = 158247
  Y1 = 147623
  Y2 = 146623
  Z1 = 0
  Z2 = 0
FEATURE [Part::Line] Axis_1_308
  AttacherType = Attacher::AttachEngine3D
  X1 = 158247
  X2 = 158247
  Y1 = 147623
  Y2 = 147623
  Z1 = 0
  Z2 = -1000
FEATURE [Part::Line] Axis_2_308
  AttacherType = Attacher::AttachEngine3D
  X1 = 158247
  X2 = 157247
  Y1 = 147623
  Y2 = 147623
  Z1 = 0
  Z2 = 0
FEATURE [Part::Feature] Heliostat_309  label="Heliostat_309(Mirror,Axis_1_309,Axis_2_309,Normal_309,Target_point)"
  Placement = pos=(-158247,-302597,4.47692e-11) rot=(0,0,1;0rad)
  shape: bbox 10000 x 55.53 x 10000 mm, 1 faces, 0 solids (baked)
FEATURE [Part::Line] Normal_309
  AttacherType = Attacher::AttachEngine3D
  X1 = -158247
  X2 = -158247
  Y1 = 147623
  Y2 = 146623
  Z1 = 0
  Z2 = 0
FEATURE [Part::Line] Axis_1_309
  AttacherType = Attacher::AttachEngine3D
  X1 = -158247
  X2 = -158247
  Y1 = 147623
  Y2 = 147623
  Z1 = 0
  Z2 = -1000
FEATURE [Part::Line] Axis_2_309
  AttacherType = Attacher::AttachEngine3D
  X1 = -158247
  X2 = -159247
  Y1 = 147623
  Y2 = 147623
  Z1 = 0
  Z2 = 0
FEATURE [Part::Feature] Heliostat_310  label="Heliostat_310(Mirror,Axis_1_310,Axis_2_310,Normal_310,Target_point)"
  Placement = pos=(137027,-370302,1.19225e-10) rot=(0,0,1;0rad)
  shape: bbox 10000 x 37.36 x 10000 mm, 1 faces, 0 solids (baked)
FEATURE [Part::Line] Normal_310
  AttacherType = Attacher::AttachEngine3D
  X1 = 137027
  X2 = 137027
  Y1 = 298901
  Y2 = 297901
  Z1 = 0
  Z2 = 0
FEATURE [Part::Line] Axis_1_310
  AttacherType = Attacher::AttachEngine3D
  X1 = 137027
  X2 = 137027
  Y1 = 298901
  Y2 = 298901
  Z1 = 0
  Z2 = -1000
FEATURE [Part::Line] Axis_2_310
  AttacherType = Attacher::AttachEngine3D
  X1 = 137027
  X2 = 136027
  Y1 = 298901
  Y2 = 298901
  Z1 = 0
  Z2 = 0
FEATURE [Part::Feature] Heliostat_311  label="Heliostat_311(Mirror,Axis_1_311,Axis_2_311,Normal_311,Target_point)"
  Placement = pos=(-137027,-370302,1.19225e-10) rot=(0,0,1;0rad)
  shape: bbox 10000 x 37.36 x 10000 mm, 1 faces, 0 solids (baked)
FEATURE [Part::Line] Normal_311
  AttacherType = Attacher::AttachEngine3D
  X1 = -137027
  X2 = -137027
  Y1 = 298901
  Y2 = 297901
  Z1 = 0
  Z2 = 0
FEATURE [Part::Line] Axis_1_311
  AttacherType = Attacher::AttachEngine3D
  X1 = -137027
  X2 = -137027
  Y1 = 298901
  Y2 = 298901
  Z1 = 0
  Z2 = -1000
FEATURE [Part::Line] Axis_2_311
  AttacherType = Attacher::AttachEngine3D
  X1 = -137027
  X2 = -138027
  Y1 = 298901
  Y2 = 298901
  Z1 = 0
  Z2 = 0
FEATURE [Part::Feature] Heliostat_312  label="Heliostat_312(Mirror,Axis_1_312,Axis_2_312,Normal_312,Target_point)"
  Placement = pos=(43453.9,-399727,2.08325e-10) rot=(0,0,1;0rad)
  shape: bbox 10000 x 31.86 x 10000 mm, 1 faces, 0 solids (baked)
FEATURE [Part::Line] Normal_312
  AttacherType = Attacher::AttachEngine3D
  X1 = 43453.9
  X2 = 43453.9
  Y1 = 384989
  Y2 = 383989
  Z1 = 0
  Z2 = 0
FEATURE [Part::Line] Axis_1_312
  AttacherType = Attacher::AttachEngine3D
  X1 = 43453.9
  X2 = 43453.9
  Y1 = 384989
  Y2 = 384989
  Z1 = 0
  Z2 = -1000
FEATURE [Part::Line] Axis_2_312
  AttacherType = Attacher::AttachEngine3D
  X1 = 43453.9
  X2 = 42453.9
  Y1 = 384989
  Y2 = 384989
  Z1 = 0
  Z2 = 0
FEATURE [Part::Feature] Heliostat_313  label="Heliostat_313(Mirror,Axis_1_313,Axis_2_313,Normal_313,Target_point)"
  Placement = pos=(-43453.9,-399727,2.08325e-10) rot=(0,0,1;0rad)
  shape: bbox 10000 x 31.86 x 10000 mm, 1 faces, 0 solids (baked)
FEATURE [Part::Line] Normal_313
  AttacherType = Attacher::AttachEngine3D
  X1 = -43453.9
  X2 = -43453.9
  Y1 = 384989
  Y2 = 383989
  Z1 = 0
  Z2 = 0
FEATURE [Part::Line] Axis_1_313
  AttacherType = Attacher::AttachEngine3D
  X1 = -43453.9
  X2 = -43453.9
  Y1 = 384989
  Y2 = 384989
  Z1 = 0
  Z2 = -1000
FEATURE [Part::Line] Axis_2_313
  AttacherType = Attacher::AttachEngine3D
  X1 = -43453.9
  X2 = -44453.9
  Y1 = 384989
  Y2 = 384989
  Z1 = 0
  Z2 = 0
FEATURE [Part::Feature] Heliostat_314  label="Heliostat_314(Mirror,Axis_1_314,Axis_2_314,Normal_314,Target_point)"
  Placement = pos=(163579,-317939,4.65379e-11) rot=(0,0,1;0rad)
  shape: bbox 10000 x 51.21 x 10000 mm, 1 faces, 0 solids (baked)
FEATURE [Part::Line] Normal_314
  AttacherType = Attacher::AttachEngine3D
  X1 = 163579
  X2 = 163579
  Y1 = 170242
  Y2 = 169242
  Z1 = 0
  Z2 = 0
FEATURE [Part::Line] Axis_1_314
  AttacherType = Attacher::AttachEngine3D
  X1 = 163579
  X2 = 163579
  Y1 = 170242
  Y2 = 170242
  Z1 = 0
  Z2 = -1000
FEATURE [Part::Line] Axis_2_314
  AttacherType = Attacher::AttachEngine3D
  X1 = 163579
  X2 = 162579
  Y1 = 170242
  Y2 = 170242
  Z1 = 0
  Z2 = 0
FEATURE [Part::Feature] Heliostat_315  label="Heliostat_315(Mirror,Axis_1_315,Axis_2_315,Normal_315,Target_point)"
  Placement = pos=(-163579,-317939,4.65379e-11) rot=(0,0,1;0rad)
  shape: bbox 10000 x 51.21 x 10000 mm, 1 faces, 0 solids (baked)
FEATURE [Part::Line] Normal_315
  AttacherType = Attacher::AttachEngine3D
  X1 = -163579
  X2 = -163579
  Y1 = 170242
  Y2 = 169242
  Z1 = 0
  Z2 = 0
FEATURE [Part::Line] Axis_1_315
  AttacherType = Attacher::AttachEngine3D
  X1 = -163579
  X2 = -163579
  Y1 = 170242
  Y2 = 170242
  Z1 = 0
  Z2 = -1000
FEATURE [Part::Line] Axis_2_315
  AttacherType = Attacher::AttachEngine3D
  X1 = -163579
  X2 = -164579
  Y1 = 170242
  Y2 = 170242
  Z1 = 0
  Z2 = 0
FEATURE [Part::Feature] Heliostat_316  label="Heliostat_316(Mirror,Axis_1_316,Axis_2_316,Normal_316,Target_point)"
  Placement = pos=(157012,-358476,2.13178e-10) rot=(0,0,1;0rad)
  shape: bbox 10000 x 40.57 x 10000 mm, 1 faces, 0 solids (baked)
FEATURE [Part::Line] Normal_316
  AttacherType = Attacher::AttachEngine3D
  X1 = 157012
  X2 = 157012
  Y1 = 257780
  Y2 = 256780
  Z1 = 0
  Z2 = 0
FEATURE [Part::Line] Axis_1_316
  AttacherType = Attacher::AttachEngine3D
  X1 = 157012
  X2 = 157012
  Y1 = 257780
  Y2 = 257780
  Z1 = 0
  Z2 = -1000
FEATURE [Part::Line] Axis_2_316
  AttacherType = Attacher::AttachEngine3D
  X1 = 157012
  X2 = 156012
  Y1 = 257780
  Y2 = 257780
  Z1 = 0
  Z2 = 0
FEATURE [Part::Feature] Heliostat_317  label="Heliostat_317(Mirror,Axis_1_317,Axis_2_317,Normal_317,Target_point)"
  Placement = pos=(-157012,-358476,2.13178e-10) rot=(0,0,1;0rad)
  shape: bbox 10000 x 40.57 x 10000 mm, 1 faces, 0 solids (baked)
FEATURE [Part::Line] Normal_317
  AttacherType = Attacher::AttachEngine3D
  X1 = -157012
  X2 = -157012
  Y1 = 257780
  Y2 = 256780
  Z1 = 0
  Z2 = 0
FEATURE [Part::Line] Axis_1_317
  AttacherType = Attacher::AttachEngine3D
  X1 = -157012
  X2 = -157012
  Y1 = 257780
  Y2 = 257780
  Z1 = 0
  Z2 = -1000
FEATURE [Part::Line] Axis_2_317
  AttacherType = Attacher::AttachEngine3D
  X1 = -157012
  X2 = -158012
  Y1 = 257780
  Y2 = 257780
  Z1 = 0
  Z2 = 0
FEATURE [Part::Feature] Heliostat_318  label="Heliostat_318(Mirror,Axis_1_318,Axis_2_318,Normal_318,Target_point)"
  Placement = pos=(21761.3,-397894,2.08325e-10) rot=(0,0,1;0rad)
  shape: bbox 10000 x 31.86 x 10000 mm, 1 faces, 0 solids (baked)
FEATURE [Part::Line] Normal_318
  AttacherType = Attacher::AttachEngine3D
  X1 = 21761.3
  X2 = 21761.3
  Y1 = 386822
  Y2 = 385822
  Z1 = 0
  Z2 = 0
FEATURE [Part::Line] Axis_1_318
  AttacherType = Attacher::AttachEngine3D
  X1 = 21761.3
  X2 = 21761.3
  Y1 = 386822
  Y2 = 386822
  Z1 = 0
  Z2 = -1000
FEATURE [Part::Line] Axis_2_318
  AttacherType = Attacher::AttachEngine3D
  X1 = 21761.3
  X2 = 20761.3
  Y1 = 386822
  Y2 = 386822
  Z1 = 0
  Z2 = 0
FEATURE [Part::Feature] Heliostat_319  label="Heliostat_319(Mirror,Axis_1_319,Axis_2_319,Normal_319,Target_point)"
  Placement = pos=(-21761.3,-397894,2.08325e-10) rot=(0,0,1;0rad)
  shape: bbox 10000 x 31.86 x 10000 mm, 1 faces, 0 solids (baked)
FEATURE [Part::Line] Normal_319
  AttacherType = Attacher::AttachEngine3D
  X1 = -21761.3
  X2 = -21761.3
  Y1 = 386822
  Y2 = 385822
  Z1 = 0
  Z2 = 0
FEATURE [Part::Line] Axis_1_319
  AttacherType = Attacher::AttachEngine3D
  X1 = -21761.3
  X2 = -21761.3
  Y1 = 386822
  Y2 = 386822
  Z1 = 0
  Z2 = -1000
FEATURE [Part::Line] Axis_2_319
  AttacherType = Attacher::AttachEngine3D
  X1 = -21761.3
  X2 = -22761.3
  Y1 = 386822
  Y2 = 386822
  Z1 = 0
  Z2 = 0
FEATURE [Part::Feature] Heliostat_320  label="Heliostat_320(Mirror,Axis_1_320,Axis_2_320,Normal_320,Target_point)"
  Placement = pos=(4.74609e-10,-397282,2.07508e-10) rot=(0,0,1;0rad)
  shape: bbox 10000 x 31.86 x 10000 mm, 1 faces, 0 solids (baked)
FEATURE [Part::Line] Normal_320
  AttacherType = Attacher::AttachEngine3D
  X1 = 0
  X2 = 0
  Y1 = 387434
  Y2 = 386434
  Z1 = 0
  Z2 = 0
FEATURE [Part::Line] Axis_1_320
  AttacherType = Attacher::AttachEngine3D
  X1 = 0
  X2 = 0
  Y1 = 387434
  Y2 = 387434
  Z1 = 0
  Z2 = -1000
FEATURE [Part::Line] Axis_2_320
  AttacherType = Attacher::AttachEngine3D
  X1 = 0
  X2 = -1000
  Y1 = 387434
  Y2 = 387434
  Z1 = 0
  Z2 = 0
FEATURE [Part::Feature] Heliostat_321  label="Heliostat_321(Mirror,Axis_1_321,Axis_2_321,Normal_321,Target_point)"
  Placement = pos=(165436,-331279,9.8826e-11) rot=(0,0,1;0rad)
  shape: bbox 10000 x 47.5 x 10000 mm, 1 faces, 0 solids (baked)
FEATURE [Part::Line] Normal_321
  AttacherType = Attacher::AttachEngine3D
  X1 = 165436
  X2 = 165436
  Y1 = 195068
  Y2 = 194068
  Z1 = 0
  Z2 = 0
FEATURE [Part::Line] Axis_1_321
  AttacherType = Attacher::AttachEngine3D
  X1 = 165436
  X2 = 165436
  Y1 = 195068
  Y2 = 195068
  Z1 = 0
  Z2 = -1000
FEATURE [Part::Line] Axis_2_321
  AttacherType = Attacher::AttachEngine3D
  X1 = 165436
  X2 = 164436
  Y1 = 195068
  Y2 = 195068
  Z1 = 0
  Z2 = 0
FEATURE [Part::Feature] Heliostat_322  label="Heliostat_322(Mirror,Axis_1_322,Axis_2_322,Normal_322,Target_point)"
  Placement = pos=(-165436,-331279,9.8826e-11) rot=(0,0,1;0rad)
  shape: bbox 10000 x 47.5 x 10000 mm, 1 faces, 0 solids (baked)
FEATURE [Part::Line] Normal_322
  AttacherType = Attacher::AttachEngine3D
  X1 = -165436
  X2 = -165436
  Y1 = 195068
  Y2 = 194068
  Z1 = 0
  Z2 = 0
FEATURE [Part::Line] Axis_1_322
  AttacherType = Attacher::AttachEngine3D
  X1 = -165436
  X2 = -165436
  Y1 = 195068
  Y2 = 195068
  Z1 = 0
  Z2 = -1000
FEATURE [Part::Line] Axis_2_322
  AttacherType = Attacher::AttachEngine3D
  X1 = -165436
  X2 = -166436
  Y1 = 195068
  Y2 = 195068
  Z1 = 0
  Z2 = 0
FEATURE [Part::Feature] Heliostat_323  label="Heliostat_323(Mirror,Axis_1_323,Axis_2_323,Normal_323,Target_point)"
  Placement = pos=(113272,-360516,6.55621e-11) rot=(0,0,1;0rad)
  shape: bbox 10000 x 37.36 x 10000 mm, 1 faces, 0 solids (baked)
FEATURE [Part::Line] Normal_323
  AttacherType = Attacher::AttachEngine3D
  X1 = 113272
  X2 = 113272
  Y1 = 308687
  Y2 = 307687
  Z1 = 0
  Z2 = 0
FEATURE [Part::Line] Axis_1_323
  AttacherType = Attacher::AttachEngine3D
  X1 = 113272
  X2 = 113272
  Y1 = 308687
  Y2 = 308687
  Z1 = 0
  Z2 = -1000
FEATURE [Part::Line] Axis_2_323
  AttacherType = Attacher::AttachEngine3D
  X1 = 113272
  X2 = 112272
  Y1 = 308687
  Y2 = 308687
  Z1 = 0
  Z2 = 0
FEATURE [Part::Feature] Heliostat_324  label="Heliostat_324(Mirror,Axis_1_324,Axis_2_324,Normal_324,Target_point)"
  Placement = pos=(-113272,-360516,6.55621e-11) rot=(0,0,1;0rad)
  shape: bbox 10000 x 37.36 x 10000 mm, 1 faces, 0 solids (baked)
FEATURE [Part::Line] Normal_324
  AttacherType = Attacher::AttachEngine3D
  X1 = -113272
  X2 = -113272
  Y1 = 308687
  Y2 = 307687
  Z1 = 0
  Z2 = 0
FEATURE [Part::Line] Axis_1_324
  AttacherType = Attacher::AttachEngine3D
  X1 = -113272
  X2 = -113272
  Y1 = 308687
  Y2 = 308687
  Z1 = 0
  Z2 = -1000
FEATURE [Part::Line] Axis_2_324
  AttacherType = Attacher::AttachEngine3D
  X1 = -113272
  X2 = -114272
  Y1 = 308687
  Y2 = 308687
  Z1 = 0
  Z2 = 0
FEATURE [Part::Feature] Heliostat_325  label="Heliostat_325(Mirror,Axis_1_325,Axis_2_325,Normal_325,Target_point)"
  Placement = pos=(29956.6,-367770,1.63382e-10) rot=(0,0,1;0rad)
  shape: bbox 10000 x 34.61 x 10000 mm, 1 faces, 0 solids (baked)
FEATURE [Part::Line] Normal_325
  AttacherType = Attacher::AttachEngine3D
  X1 = 29956.6
  X2 = 29956.6
  Y1 = 354531
  Y2 = 353531
  Z1 = 0
  Z2 = 0
FEATURE [Part::Line] Axis_1_325
  AttacherType = Attacher::AttachEngine3D
  X1 = 29956.6
  X2 = 29956.6
  Y1 = 354531
  Y2 = 354531
  Z1 = 0
  Z2 = -1000
FEATURE [Part::Line] Axis_2_325
  AttacherType = Attacher::AttachEngine3D
  X1 = 29956.6
  X2 = 28956.6
  Y1 = 354531
  Y2 = 354531
  Z1 = 0
  Z2 = 0
FEATURE [Part::Feature] Heliostat_326  label="Heliostat_326(Mirror,Axis_1_326,Axis_2_326,Normal_326,Target_point)"
  Placement = pos=(-29956.6,-367770,1.63382e-10) rot=(0,0,1;0rad)
  shape: bbox 10000 x 34.61 x 10000 mm, 1 faces, 0 solids (baked)
FEATURE [Part::Line] Normal_326
  AttacherType = Attacher::AttachEngine3D
  X1 = -29956.6
  X2 = -29956.6
  Y1 = 354531
  Y2 = 353531
  Z1 = 0
  Z2 = 0
FEATURE [Part::Line] Axis_1_326
  AttacherType = Attacher::AttachEngine3D
  X1 = -29956.6
  X2 = -29956.6
  Y1 = 354531
  Y2 = 354531
  Z1 = 0
  Z2 = -1000
FEATURE [Part::Line] Axis_2_326
  AttacherType = Attacher::AttachEngine3D
  X1 = -29956.6
  X2 = -30956.6
  Y1 = 354531
  Y2 = 354531
  Z1 = 0
  Z2 = 0
FEATURE [Part::Feature] Heliostat_327  label="Heliostat_327(Mirror,Axis_1_327,Axis_2_327,Normal_327,Target_point)"
  Placement = pos=(136407,-347005,5.83394e-11) rot=(0,0,1;0rad)
  shape: bbox 10000 x 40.57 x 10000 mm, 1 faces, 0 solids (baked)
FEATURE [Part::Line] Normal_327
  AttacherType = Attacher::AttachEngine3D
  X1 = 136407
  X2 = 136407
  Y1 = 269251
  Y2 = 268251
  Z1 = 0
  Z2 = 0
FEATURE [Part::Line] Axis_1_327
  AttacherType = Attacher::AttachEngine3D
  X1 = 136407
  X2 = 136407
  Y1 = 269251
  Y2 = 269251
  Z1 = 0
  Z2 = -1000
FEATURE [Part::Line] Axis_2_327
  AttacherType = Attacher::AttachEngine3D
  X1 = 136407
  X2 = 135407
  Y1 = 269251
  Y2 = 269251
  Z1 = 0
  Z2 = 0
FEATURE [Part::Feature] Heliostat_328  label="Heliostat_328(Mirror,Axis_1_328,Axis_2_328,Normal_328,Target_point)"
  Placement = pos=(-136407,-347005,5.83394e-11) rot=(0,0,1;0rad)
  shape: bbox 10000 x 40.57 x 10000 mm, 1 faces, 0 solids (baked)
FEATURE [Part::Line] Normal_328
  AttacherType = Attacher::AttachEngine3D
  X1 = -136407
  X2 = -136407
  Y1 = 269251
  Y2 = 268251
  Z1 = 0
  Z2 = 0
FEATURE [Part::Line] Axis_1_328
  AttacherType = Attacher::AttachEngine3D
  X1 = -136407
  X2 = -136407
  Y1 = 269251
  Y2 = 269251
  Z1 = 0
  Z2 = -1000
FEATURE [Part::Line] Axis_2_328
  AttacherType = Attacher::AttachEngine3D
  X1 = -136407
  X2 = -137407
  Y1 = 269251
  Y2 = 269251
  Z1 = 0
  Z2 = 0
FEATURE [Part::Feature] Heliostat_329  label="Heliostat_329(Mirror,Axis_1_329,Axis_2_329,Normal_329,Target_point)"
  Placement = pos=(88826.1,-352615,1.25007e-10) rot=(0,0,1;0rad)
  shape: bbox 10000 x 37.36 x 10000 mm, 1 faces, 0 solids (baked)
FEATURE [Part::Line] Normal_329
  AttacherType = Attacher::AttachEngine3D
  X1 = 88826.1
  X2 = 88826.1
  Y1 = 316589
  Y2 = 315589
  Z1 = 0
  Z2 = 0
FEATURE [Part::Line] Axis_1_329
  AttacherType = Attacher::AttachEngine3D
  X1 = 88826.1
  X2 = 88826.1
  Y1 = 316589
  Y2 = 316589
  Z1 = 0
  Z2 = -1000
FEATURE [Part::Line] Axis_2_329
  AttacherType = Attacher::AttachEngine3D
  X1 = 88826.1
  X2 = 87826.1
  Y1 = 316589
  Y2 = 316589
  Z1 = 0
  Z2 = 0
FEATURE [Part::Feature] Heliostat_330  label="Heliostat_330(Mirror,Axis_1_330,Axis_2_330,Normal_330,Target_point)"
  Placement = pos=(-88826.1,-352615,1.25007e-10) rot=(0,0,1;0rad)
  shape: bbox 10000 x 37.36 x 10000 mm, 1 faces, 0 solids (baked)
FEATURE [Part::Line] Normal_330
  AttacherType = Attacher::AttachEngine3D
  X1 = -88826.1
  X2 = -88826.1
  Y1 = 316589
  Y2 = 315589
  Z1 = 0
  Z2 = 0
FEATURE [Part::Line] Axis_1_330
  AttacherType = Attacher::AttachEngine3D
  X1 = -88826.1
  X2 = -88826.1
  Y1 = 316589
  Y2 = 316589
  Z1 = 0
  Z2 = -1000
FEATURE [Part::Line] Axis_2_330
  AttacherType = Attacher::AttachEngine3D
  X1 = -88826.1
  X2 = -89826.1
  Y1 = 316589
  Y2 = 316589
  Z1 = 0
  Z2 = 0
FEATURE [Part::Feature] Heliostat_331  label="Heliostat_331(Mirror,Axis_1_331,Axis_2_331,Normal_331,Target_point)"
  Placement = pos=(138270,-274028,7.62902e-11) rot=(0,0,1;0rad)
  shape: bbox 10000 x 59.82 x 10000 mm, 1 faces, 0 solids (baked)
FEATURE [Part::Line] Normal_331
  AttacherType = Attacher::AttachEngine3D
  X1 = 138270
  X2 = 138270
  Y1 = 143902
  Y2 = 142902
  Z1 = 0
  Z2 = 0
FEATURE [Part::Line] Axis_1_331
  AttacherType = Attacher::AttachEngine3D
  X1 = 138270
  X2 = 138270
  Y1 = 143902
  Y2 = 143902
  Z1 = 0
  Z2 = -1000
FEATURE [Part::Line] Axis_2_331
  AttacherType = Attacher::AttachEngine3D
  X1 = 138270
  X2 = 137270
  Y1 = 143902
  Y2 = 143902
  Z1 = 0
  Z2 = 0
FEATURE [Part::Feature] Heliostat_332  label="Heliostat_332(Mirror,Axis_1_332,Axis_2_332,Normal_332,Target_point)"
  Placement = pos=(-138270,-274028,7.62902e-11) rot=(0,0,1;0rad)
  shape: bbox 10000 x 59.82 x 10000 mm, 1 faces, 0 solids (baked)
FEATURE [Part::Line] Normal_332
  AttacherType = Attacher::AttachEngine3D
  X1 = -138270
  X2 = -138270
  Y1 = 143902
  Y2 = 142902
  Z1 = 0
  Z2 = 0
FEATURE [Part::Line] Axis_1_332
  AttacherType = Attacher::AttachEngine3D
  X1 = -138270
  X2 = -138270
  Y1 = 143902
  Y2 = 143902
  Z1 = 0
  Z2 = -1000
FEATURE [Part::Line] Axis_2_332
  AttacherType = Attacher::AttachEngine3D
  X1 = -138270
  X2 = -139270
  Y1 = 143902
  Y2 = 143902
  Z1 = 0
  Z2 = 0
FEATURE [Part::Feature] Heliostat_333  label="Heliostat_333(Mirror,Axis_1_333,Axis_2_333,Normal_333,Target_point)"
  Placement = pos=(63837.4,-346646,2.45772e-10) rot=(0,0,1;0rad)
  shape: bbox 10000 x 37.36 x 10000 mm, 1 faces, 0 solids (baked)
FEATURE [Part::Line] Normal_333
  AttacherType = Attacher::AttachEngine3D
  X1 = 63837.4
  X2 = 63837.4
  Y1 = 322557
  Y2 = 321557
  Z1 = 0
  Z2 = 0
FEATURE [Part::Line] Axis_1_333
  AttacherType = Attacher::AttachEngine3D
  X1 = 63837.4
  X2 = 63837.4
  Y1 = 322557
  Y2 = 322557
  Z1 = 0
  Z2 = -1000
FEATURE [Part::Line] Axis_2_333
  AttacherType = Attacher::AttachEngine3D
  X1 = 63837.4
  X2 = 62837.4
  Y1 = 322557
  Y2 = 322557
  Z1 = 0
  Z2 = 0
FEATURE [Part::Feature] Heliostat_334  label="Heliostat_334(Mirror,Axis_1_334,Axis_2_334,Normal_334,Target_point)"
  Placement = pos=(-63837.4,-346646,2.45772e-10) rot=(0,0,1;0rad)
  shape: bbox 10000 x 37.36 x 10000 mm, 1 faces, 0 solids (baked)
FEATURE [Part::Line] Normal_334
  AttacherType = Attacher::AttachEngine3D
  X1 = -63837.4
  X2 = -63837.4
  Y1 = 322557
  Y2 = 321557
  Z1 = 0
  Z2 = 0
FEATURE [Part::Line] Axis_1_334
  AttacherType = Attacher::AttachEngine3D
  X1 = -63837.4
  X2 = -63837.4
  Y1 = 322557
  Y2 = 322557
  Z1 = 0
  Z2 = -1000
FEATURE [Part::Line] Axis_2_334
  AttacherType = Attacher::AttachEngine3D
  X1 = -63837.4
  X2 = -64837.4
  Y1 = 322557
  Y2 = 322557
  Z1 = 0
  Z2 = 0
FEATURE [Part::Feature] Heliostat_335  label="Heliostat_335(Mirror,Axis_1_335,Axis_2_335,Normal_335,Target_point)"
  Placement = pos=(153149,-289977,7.62902e-11) rot=(0,0,1;0rad)
  shape: bbox 10000 x 59.82 x 10000 mm, 1 faces, 0 solids (baked)
FEATURE [Part::Line] Normal_335
  AttacherType = Attacher::AttachEngine3D
  X1 = 153149
  X2 = 153149
  Y1 = 127953
  Y2 = 126953
  Z1 = 0
  Z2 = 0
FEATURE [Part::Line] Axis_1_335
  AttacherType = Attacher::AttachEngine3D
  X1 = 153149
  X2 = 153149
  Y1 = 127953
  Y2 = 127953
  Z1 = 0
  Z2 = -1000
FEATURE [Part::Line] Axis_2_335
  AttacherType = Attacher::AttachEngine3D
  X1 = 153149
  X2 = 152149
  Y1 = 127953
  Y2 = 127953
  Z1 = 0
  Z2 = 0
FEATURE [Part::Feature] Heliostat_336  label="Heliostat_336(Mirror,Axis_1_336,Axis_2_336,Normal_336,Target_point)"
  Placement = pos=(-153149,-289977,7.62902e-11) rot=(0,0,1;0rad)
  shape: bbox 10000 x 59.82 x 10000 mm, 1 faces, 0 solids (baked)
FEATURE [Part::Line] Normal_336
  AttacherType = Attacher::AttachEngine3D
  X1 = -153149
  X2 = -153149
  Y1 = 127953
  Y2 = 126953
  Z1 = 0
  Z2 = 0
FEATURE [Part::Line] Axis_1_336
  AttacherType = Attacher::AttachEngine3D
  X1 = -153149
  X2 = -153149
  Y1 = 127953
  Y2 = 127953
  Z1 = 0
  Z2 = -1000
FEATURE [Part::Line] Axis_2_336
  AttacherType = Attacher::AttachEngine3D
  X1 = -153149
  X2 = -154149
  Y1 = 127953
  Y2 = 127953
  Z1 = 0
  Z2 = 0
FEATURE [Part::Feature] Heliostat_337  label="Heliostat_337(Mirror,Axis_1_337,Axis_2_337,Normal_337,Target_point)"
  Placement = pos=(141191,-286209,1.17366e-10) rot=(0,0,1;0rad)
  shape: bbox 10000 x 55.53 x 10000 mm, 1 faces, 0 solids (baked)
FEATURE [Part::Line] Normal_337
  AttacherType = Attacher::AttachEngine3D
  X1 = 141191
  X2 = 141191
  Y1 = 164011
  Y2 = 163011
  Z1 = 0
  Z2 = 0
FEATURE [Part::Line] Axis_1_337
  AttacherType = Attacher::AttachEngine3D
  X1 = 141191
  X2 = 141191
  Y1 = 164011
  Y2 = 164011
  Z1 = 0
  Z2 = -1000
FEATURE [Part::Line] Axis_2_337
  AttacherType = Attacher::AttachEngine3D
  X1 = 141191
  X2 = 140191
  Y1 = 164011
  Y2 = 164011
  Z1 = 0
  Z2 = 0
FEATURE [Part::Feature] Heliostat_338  label="Heliostat_338(Mirror,Axis_1_338,Axis_2_338,Normal_338,Target_point)"
  Placement = pos=(-141191,-286209,1.17366e-10) rot=(0,0,1;0rad)
  shape: bbox 10000 x 55.53 x 10000 mm, 1 faces, 0 solids (baked)
FEATURE [Part::Line] Normal_338
  AttacherType = Attacher::AttachEngine3D
  X1 = -141191
  X2 = -141191
  Y1 = 164011
  Y2 = 163011
  Z1 = 0
  Z2 = 0
FEATURE [Part::Line] Axis_1_338
  AttacherType = Attacher::AttachEngine3D
  X1 = -141191
  X2 = -141191
  Y1 = 164011
  Y2 = 164011
  Z1 = 0
  Z2 = -1000
FEATURE [Part::Line] Axis_2_338
  AttacherType = Attacher::AttachEngine3D
  X1 = -141191
  X2 = -142191
  Y1 = 164011
  Y2 = 164011
  Z1 = 0
  Z2 = 0
FEATURE [Part::Feature] Heliostat_339  label="Heliostat_339(Mirror,Axis_1_339,Axis_2_339,Normal_339,Target_point)"
  Placement = pos=(116186,-317773,1.51391e-10) rot=(0,0,1;0rad)
  shape: bbox 10000 x 43.77 x 10000 mm, 1 faces, 0 solids (baked)
FEATURE [Part::Line] Normal_339
  AttacherType = Attacher::AttachEngine3D
  X1 = 116186
  X2 = 116186
  Y1 = 253441
  Y2 = 252441
  Z1 = 0
  Z2 = 0
FEATURE [Part::Line] Axis_1_339
  AttacherType = Attacher::AttachEngine3D
  X1 = 116186
  X2 = 116186
  Y1 = 253441
  Y2 = 253441
  Z1 = 0
  Z2 = -1000
FEATURE [Part::Line] Axis_2_339
  AttacherType = Attacher::AttachEngine3D
  X1 = 116186
  X2 = 115186
  Y1 = 253441
  Y2 = 253441
  Z1 = 0
  Z2 = 0
FEATURE [Part::Feature] Heliostat_340  label="Heliostat_340(Mirror,Axis_1_340,Axis_2_340,Normal_340,Target_point)"
  Placement = pos=(-116186,-317773,1.51391e-10) rot=(0,0,1;0rad)
  shape: bbox 10000 x 43.77 x 10000 mm, 1 faces, 0 solids (baked)
FEATURE [Part::Line] Normal_340
  AttacherType = Attacher::AttachEngine3D
  X1 = -116186
  X2 = -116186
  Y1 = 253441
  Y2 = 252441
  Z1 = 0
  Z2 = 0
FEATURE [Part::Line] Axis_1_340
  AttacherType = Attacher::AttachEngine3D
  X1 = -116186
  X2 = -116186
  Y1 = 253441
  Y2 = 253441
  Z1 = 0
  Z2 = -1000
FEATURE [Part::Line] Axis_2_340
  AttacherType = Attacher::AttachEngine3D
  X1 = -116186
  X2 = -117186
  Y1 = 253441
  Y2 = 253441
  Z1 = 0
  Z2 = 0
FEATURE [Part::Feature] Heliostat_341  label="Heliostat_341(Mirror,Axis_1_341,Axis_2_341,Normal_341,Target_point)"
  Placement = pos=(114968,-337177,1.69118e-10) rot=(0,0,1;0rad)
  shape: bbox 10000 x 40.57 x 10000 mm, 1 faces, 0 solids (baked)
FEATURE [Part::Line] Normal_341
  AttacherType = Attacher::AttachEngine3D
  X1 = 114968
  X2 = 114968
  Y1 = 279079
  Y2 = 278079
  Z1 = 0
  Z2 = 0
FEATURE [Part::Line] Axis_1_341
  AttacherType = Attacher::AttachEngine3D
  X1 = 114968
  X2 = 114968
  Y1 = 279079
  Y2 = 279079
  Z1 = 0
  Z2 = -1000
FEATURE [Part::Line] Axis_2_341
  AttacherType = Attacher::AttachEngine3D
  X1 = 114968
  X2 = 113968
  Y1 = 279079
  Y2 = 279079
  Z1 = 0
  Z2 = 0
FEATURE [Part::Feature] Heliostat_342  label="Heliostat_342(Mirror,Axis_1_342,Axis_2_342,Normal_342,Target_point)"
  Placement = pos=(-114968,-337177,1.69118e-10) rot=(0,0,1;0rad)
  shape: bbox 10000 x 40.57 x 10000 mm, 1 faces, 0 solids (baked)
FEATURE [Part::Line] Normal_342
  AttacherType = Attacher::AttachEngine3D
  X1 = -114968
  X2 = -114968
  Y1 = 279079
  Y2 = 278079
  Z1 = 0
  Z2 = 0
FEATURE [Part::Line] Axis_1_342
  AttacherType = Attacher::AttachEngine3D
  X1 = -114968
  X2 = -114968
  Y1 = 279079
  Y2 = 279079
  Z1 = 0
  Z2 = -1000
FEATURE [Part::Line] Axis_2_342
  AttacherType = Attacher::AttachEngine3D
  X1 = -114968
  X2 = -115968
  Y1 = 279079
  Y2 = 279079
  Z1 = 0
  Z2 = 0
FEATURE [Part::Feature] Heliostat_343  label="Heliostat_343(Mirror,Axis_1_343,Axis_2_343,Normal_343,Target_point)"
  Placement = pos=(144023,-301104,8.96294e-11) rot=(0,0,1;0rad)
  shape: bbox 10000 x 51.21 x 10000 mm, 1 faces, 0 solids (baked)
FEATURE [Part::Line] Normal_343
  AttacherType = Attacher::AttachEngine3D
  X1 = 144023
  X2 = 144023
  Y1 = 187076
  Y2 = 186076
  Z1 = 0
  Z2 = 0
FEATURE [Part::Line] Axis_1_343
  AttacherType = Attacher::AttachEngine3D
  X1 = 144023
  X2 = 144023
  Y1 = 187076
  Y2 = 187076
  Z1 = 0
  Z2 = -1000
FEATURE [Part::Line] Axis_2_343
  AttacherType = Attacher::AttachEngine3D
  X1 = 144023
  X2 = 143023
  Y1 = 187076
  Y2 = 187076
  Z1 = 0
  Z2 = 0
FEATURE [Part::Feature] Heliostat_344  label="Heliostat_344(Mirror,Axis_1_344,Axis_2_344,Normal_344,Target_point)"
  Placement = pos=(43461.3,-138412,5.35401e-11) rot=(0,0,1;0rad)
  shape: bbox 10010 x 161.4 x 10000 mm, 1 faces, 0 solids (baked)
FEATURE [Part::Line] Normal_344
  AttacherType = Attacher::AttachEngine3D
  X1 = 43461.3
  X2 = 43461.3
  Y1 = 16533.7
  Y2 = 15533.7
  Z1 = 0
  Z2 = 0
FEATURE [Part::Line] Axis_1_344
  AttacherType = Attacher::AttachEngine3D
  X1 = 43461.3
  X2 = 43461.3
  Y1 = 16533.7
  Y2 = 16533.7
  Z1 = 0
  Z2 = -1000
FEATURE [Part::Line] Axis_2_344
  AttacherType = Attacher::AttachEngine3D
  X1 = 43461.3
  X2 = 42461.3
  Y1 = 16533.7
  Y2 = 16533.7
  Z1 = 0
  Z2 = 0
FEATURE [Part::Feature] Heliostat_345  label="Heliostat_345(Mirror,Axis_1_345,Axis_2_345,Normal_345,Target_point)"
  Placement = pos=(-144023,-301104,8.96294e-11) rot=(0,0,1;0rad)
  shape: bbox 10000 x 51.21 x 10000 mm, 1 faces, 0 solids (baked)
FEATURE [Part::Line] Normal_345
  AttacherType = Attacher::AttachEngine3D
  X1 = -144023
  X2 = -144023
  Y1 = 187076
  Y2 = 186076
  Z1 = 0
  Z2 = 0
FEATURE [Part::Line] Axis_1_345
  AttacherType = Attacher::AttachEngine3D
  X1 = -144023
  X2 = -144023
  Y1 = 187076
  Y2 = 187076
  Z1 = 0
  Z2 = -1000
FEATURE [Part::Line] Axis_2_345
  AttacherType = Attacher::AttachEngine3D
  X1 = -144023
  X2 = -145023
  Y1 = 187076
  Y2 = 187076
  Z1 = 0
  Z2 = 0
FEATURE [Part::Feature] Heliostat_346  label="Heliostat_346(Mirror,Axis_1_346,Axis_2_346,Normal_346,Target_point)"
  Placement = pos=(-43461.3,-138412,5.35401e-11) rot=(0,0,1;0rad)
  shape: bbox 10010 x 161.4 x 10000 mm, 1 faces, 0 solids (baked)
FEATURE [Part::Line] Normal_346
  AttacherType = Attacher::AttachEngine3D
  X1 = -43461.3
  X2 = -43461.3
  Y1 = 16533.7
  Y2 = 15533.7
  Z1 = 0
  Z2 = 0
FEATURE [Part::Line] Axis_1_346
  AttacherType = Attacher::AttachEngine3D
  X1 = -43461.3
  X2 = -43461.3
  Y1 = 16533.7
  Y2 = 16533.7
  Z1 = 0
  Z2 = -1000
FEATURE [Part::Line] Axis_2_346
  AttacherType = Attacher::AttachEngine3D
  X1 = -43461.3
  X2 = -44461.3
  Y1 = 16533.7
  Y2 = 16533.7
  Z1 = 0
  Z2 = 0
FEATURE [Part::Feature] Heliostat_347  label="Heliostat_347(Mirror,Axis_1_347,Axis_2_347,Normal_347,Target_point)"
  Placement = pos=(38459,-342647,2.45772e-10) rot=(0,0,1;0rad)
  shape: bbox 10000 x 37.36 x 10000 mm, 1 faces, 0 solids (baked)
FEATURE [Part::Line] Normal_347
  AttacherType = Attacher::AttachEngine3D
  X1 = 38459
  X2 = 38459
  Y1 = 326557
  Y2 = 325557
  Z1 = 0
  Z2 = 0
FEATURE [Part::Line] Axis_1_347
  AttacherType = Attacher::AttachEngine3D
  X1 = 38459
  X2 = 38459
  Y1 = 326557
  Y2 = 326557
  Z1 = 0
  Z2 = -1000
FEATURE [Part::Line] Axis_2_347
  AttacherType = Attacher::AttachEngine3D
  X1 = 38459
  X2 = 37459
  Y1 = 326557
  Y2 = 326557
  Z1 = 0
  Z2 = 0
FEATURE [Part::Feature] Heliostat_348  label="Heliostat_348(Mirror,Axis_1_348,Axis_2_348,Normal_348,Target_point)"
  Placement = pos=(-38459,-342647,2.45772e-10) rot=(0,0,1;0rad)
  shape: bbox 10000 x 37.36 x 10000 mm, 1 faces, 0 solids (baked)
FEATURE [Part::Line] Normal_348
  AttacherType = Attacher::AttachEngine3D
  X1 = -38459
  X2 = -38459
  Y1 = 326557
  Y2 = 325557
  Z1 = 0
  Z2 = 0
FEATURE [Part::Line] Axis_1_348
  AttacherType = Attacher::AttachEngine3D
  X1 = -38459
  X2 = -38459
  Y1 = 326557
  Y2 = 326557
  Z1 = 0
  Z2 = -1000
FEATURE [Part::Line] Axis_2_348
  AttacherType = Attacher::AttachEngine3D
  X1 = -38459
  X2 = -39459
  Y1 = 326557
  Y2 = 326557
  Z1 = 0
  Z2 = 0
FEATURE [Part::Feature] Heliostat_349  label="Heliostat_349(Mirror,Axis_1_349,Axis_2_349,Normal_349,Target_point)"
  Placement = pos=(12845.8,-340641,1.81782e-10) rot=(0,0,1;0rad)
  shape: bbox 10000 x 37.36 x 10000 mm, 1 faces, 0 solids (baked)
FEATURE [Part::Line] Normal_349
  AttacherType = Attacher::AttachEngine3D
  X1 = 12845.8
  X2 = 12845.8
  Y1 = 328563
  Y2 = 327563
  Z1 = 0
  Z2 = 0
FEATURE [Part::Line] Axis_1_349
  AttacherType = Attacher::AttachEngine3D
  X1 = 12845.8
  X2 = 12845.8
  Y1 = 328563
  Y2 = 328563
  Z1 = 0
  Z2 = -1000
FEATURE [Part::Line] Axis_2_349
  AttacherType = Attacher::AttachEngine3D
  X1 = 12845.8
  X2 = 11845.8
  Y1 = 328563
  Y2 = 328563
  Z1 = 0
  Z2 = 0
FEATURE [Part::Feature] Heliostat_350  label="Heliostat_350(Mirror,Axis_1_350,Axis_2_350,Normal_350,Target_point)"
  Placement = pos=(-12845.8,-340641,1.81782e-10) rot=(0,0,1;0rad)
  shape: bbox 10000 x 37.36 x 10000 mm, 1 faces, 0 solids (baked)
FEATURE [Part::Line] Normal_350
  AttacherType = Attacher::AttachEngine3D
  X1 = -12845.8
  X2 = -12845.8
  Y1 = 328563
  Y2 = 327563
  Z1 = 0
  Z2 = 0
FEATURE [Part::Line] Axis_1_350
  AttacherType = Attacher::AttachEngine3D
  X1 = -12845.8
  X2 = -12845.8
  Y1 = 328563
  Y2 = 328563
  Z1 = 0
  Z2 = -1000
FEATURE [Part::Line] Axis_2_350
  AttacherType = Attacher::AttachEngine3D
  X1 = -12845.8
  X2 = -13845.8
  Y1 = 328563
  Y2 = 328563
  Z1 = 0
  Z2 = 0
FEATURE [Part::Feature] Heliostat_351  label="Heliostat_351(Mirror,Axis_1_351,Axis_2_351,Normal_351,Target_point)"
  Placement = pos=(117462,-232348,8.98539e-11) rot=(0,0,1;0rad)
  shape: bbox 10000 x 75.38 x 10000 mm, 1 faces, 0 solids (baked)
FEATURE [Part::Line] Normal_351
  AttacherType = Attacher::AttachEngine3D
  X1 = 117462
  X2 = 117462
  Y1 = 99297
  Y2 = 98297
  Z1 = 0
  Z2 = 0
FEATURE [Part::Line] Axis_1_351
  AttacherType = Attacher::AttachEngine3D
  X1 = 117462
  X2 = 117462
  Y1 = 99297
  Y2 = 99297
  Z1 = 0
  Z2 = -1000
FEATURE [Part::Line] Axis_2_351
  AttacherType = Attacher::AttachEngine3D
  X1 = 117462
  X2 = 116462
  Y1 = 99297
  Y2 = 99297
  Z1 = 0
  Z2 = 0
FEATURE [Part::Feature] Heliostat_352  label="Heliostat_352(Mirror,Axis_1_352,Axis_2_352,Normal_352,Target_point)"
  Placement = pos=(-117462,-232348,8.98539e-11) rot=(0,0,1;0rad)
  shape: bbox 10000 x 75.38 x 10000 mm, 1 faces, 0 solids (baked)
FEATURE [Part::Line] Normal_352
  AttacherType = Attacher::AttachEngine3D
  X1 = -117462
  X2 = -117462
  Y1 = 99297
  Y2 = 98297
  Z1 = 0
  Z2 = 0
FEATURE [Part::Line] Axis_1_352
  AttacherType = Attacher::AttachEngine3D
  X1 = -117462
  X2 = -117462
  Y1 = 99297
  Y2 = 99297
  Z1 = 0
  Z2 = -1000
FEATURE [Part::Line] Axis_2_352
  AttacherType = Attacher::AttachEngine3D
  X1 = -117462
  X2 = -118462
  Y1 = 99297
  Y2 = 99297
  Z1 = 0
  Z2 = 0
FEATURE [Part::Feature] Heliostat_353  label="Heliostat_353(Mirror,Axis_1_353,Axis_2_353,Normal_353,Target_point)"
  Placement = pos=(92828.5,-329052,1.64204e-10) rot=(0,0,1;0rad)
  shape: bbox 10000 x 40.57 x 10000 mm, 1 faces, 0 solids (baked)
FEATURE [Part::Line] Normal_353
  AttacherType = Attacher::AttachEngine3D
  X1 = 92828.5
  X2 = 92828.5
  Y1 = 287204
  Y2 = 286204
  Z1 = 0
  Z2 = 0
FEATURE [Part::Line] Axis_1_353
  AttacherType = Attacher::AttachEngine3D
  X1 = 92828.5
  X2 = 92828.5
  Y1 = 287204
  Y2 = 287204
  Z1 = 0
  Z2 = -1000
FEATURE [Part::Line] Axis_2_353
  AttacherType = Attacher::AttachEngine3D
  X1 = 92828.5
  X2 = 91828.5
  Y1 = 287204
  Y2 = 287204
  Z1 = 0
  Z2 = 0
FEATURE [Part::Feature] Heliostat_354  label="Heliostat_354(Mirror,Axis_1_354,Axis_2_354,Normal_354,Target_point)"
  Placement = pos=(-92828.5,-329052,1.64204e-10) rot=(0,0,1;0rad)
  shape: bbox 10000 x 40.57 x 10000 mm, 1 faces, 0 solids (baked)
FEATURE [Part::Line] Normal_354
  AttacherType = Attacher::AttachEngine3D
  X1 = -92828.5
  X2 = -92828.5
  Y1 = 287204
  Y2 = 286204
  Z1 = 0
  Z2 = 0
FEATURE [Part::Line] Axis_1_354
  AttacherType = Attacher::AttachEngine3D
  X1 = -92828.5
  X2 = -92828.5
  Y1 = 287204
  Y2 = 287204
  Z1 = 0
  Z2 = -1000
FEATURE [Part::Line] Axis_2_354
  AttacherType = Attacher::AttachEngine3D
  X1 = -92828.5
  X2 = -93828.5
  Y1 = 287204
  Y2 = 287204
  Z1 = 0
  Z2 = 0
FEATURE [Part::Feature] Heliostat_355  label="Heliostat_355(Mirror,Axis_1_355,Axis_2_355,Normal_355,Target_point)"
  Placement = pos=(111369,-221137,5.2501e-11) rot=(0,0,1;0rad)
  shape: bbox 10000 x 87.39 x 10000 mm, 1 faces, 0 solids (baked)
FEATURE [Part::Line] Normal_355
  AttacherType = Attacher::AttachEngine3D
  X1 = 111369
  X2 = 111369
  Y1 = 64952.9
  Y2 = 63952.9
  Z1 = 0
  Z2 = 0
FEATURE [Part::Line] Axis_1_355
  AttacherType = Attacher::AttachEngine3D
  X1 = 111369
  X2 = 111369
  Y1 = 64952.9
  Y2 = 64952.9
  Z1 = 0
  Z2 = -1000
FEATURE [Part::Line] Axis_2_355
  AttacherType = Attacher::AttachEngine3D
  X1 = 111369
  X2 = 110369
  Y1 = 64952.9
  Y2 = 64952.9
  Z1 = 0
  Z2 = 0
FEATURE [Part::Feature] Heliostat_356  label="Heliostat_356(Mirror,Axis_1_356,Axis_2_356,Normal_356,Target_point)"
  Placement = pos=(-111369,-221137,5.2501e-11) rot=(0,0,1;0rad)
  shape: bbox 10000 x 87.39 x 10000 mm, 1 faces, 0 solids (baked)
FEATURE [Part::Line] Normal_356
  AttacherType = Attacher::AttachEngine3D
  X1 = -111369
  X2 = -111369
  Y1 = 64952.9
  Y2 = 63952.9
  Z1 = 0
  Z2 = 0
FEATURE [Part::Line] Axis_1_356
  AttacherType = Attacher::AttachEngine3D
  X1 = -111369
  X2 = -111369
  Y1 = 64952.9
  Y2 = 64952.9
  Z1 = 0
  Z2 = -1000
FEATURE [Part::Line] Axis_2_356
  AttacherType = Attacher::AttachEngine3D
  X1 = -111369
  X2 = -112369
  Y1 = 64952.9
  Y2 = 64952.9
  Z1 = 0
  Z2 = 0
FEATURE [Part::Feature] Heliostat_357  label="Heliostat_357(Mirror,Axis_1_357,Axis_2_357,Normal_357,Target_point)"
  Placement = pos=(154224,-338950,1.04051e-10) rot=(0,0,1;0rad)
  shape: bbox 10000 x 43.77 x 10000 mm, 1 faces, 0 solids (baked)
FEATURE [Part::Line] Normal_357
  AttacherType = Attacher::AttachEngine3D
  X1 = 154224
  X2 = 154224
  Y1 = 232264
  Y2 = 231264
  Z1 = 0
  Z2 = 0
FEATURE [Part::Line] Axis_1_357
  AttacherType = Attacher::AttachEngine3D
  X1 = 154224
  X2 = 154224
  Y1 = 232264
  Y2 = 232264
  Z1 = 0
  Z2 = -1000
FEATURE [Part::Line] Axis_2_357
  AttacherType = Attacher::AttachEngine3D
  X1 = 154224
  X2 = 153224
  Y1 = 232264
  Y2 = 232264
  Z1 = 0
  Z2 = 0
FEATURE [Part::Feature] Heliostat_358  label="Heliostat_358(Mirror,Axis_1_358,Axis_2_358,Normal_358,Target_point)"
  Placement = pos=(-154224,-338950,1.04051e-10) rot=(0,0,1;0rad)
  shape: bbox 10000 x 43.77 x 10000 mm, 1 faces, 0 solids (baked)
FEATURE [Part::Line] Normal_358
  AttacherType = Attacher::AttachEngine3D
  X1 = -154224
  X2 = -154224
  Y1 = 232264
  Y2 = 231264
  Z1 = 0
  Z2 = 0
FEATURE [Part::Line] Axis_1_358
  AttacherType = Attacher::AttachEngine3D
  X1 = -154224
  X2 = -154224
  Y1 = 232264
  Y2 = 232264
  Z1 = 0
  Z2 = -1000
FEATURE [Part::Line] Axis_2_358
  AttacherType = Attacher::AttachEngine3D
  X1 = -154224
  X2 = -155224
  Y1 = 232264
  Y2 = 232264
  Z1 = 0
  Z2 = 0
FEATURE [Part::Feature] Heliostat_359  label="Heliostat_359(Mirror,Axis_1_359,Axis_2_359,Normal_359,Target_point)"
  Placement = pos=(70121.8,-322682,1.64204e-10) rot=(0,0,1;0rad)
  shape: bbox 10000 x 40.57 x 10000 mm, 1 faces, 0 solids (baked)
FEATURE [Part::Line] Normal_359
  AttacherType = Attacher::AttachEngine3D
  X1 = 70121.8
  X2 = 70121.8
  Y1 = 293574
  Y2 = 292574
  Z1 = 0
  Z2 = 0
FEATURE [Part::Line] Axis_1_359
  AttacherType = Attacher::AttachEngine3D
  X1 = 70121.8
  X2 = 70121.8
  Y1 = 293574
  Y2 = 293574
  Z1 = 0
  Z2 = -1000
FEATURE [Part::Line] Axis_2_359
  AttacherType = Attacher::AttachEngine3D
  X1 = 70121.8
  X2 = 69121.8
  Y1 = 293574
  Y2 = 293574
  Z1 = 0
  Z2 = 0
FEATURE [Part::Feature] Heliostat_360  label="Heliostat_360(Mirror,Axis_1_360,Axis_2_360,Normal_360,Target_point)"
  Placement = pos=(-70121.8,-322682,1.64204e-10) rot=(0,0,1;0rad)
  shape: bbox 10000 x 40.57 x 10000 mm, 1 faces, 0 solids (baked)
FEATURE [Part::Line] Normal_360
  AttacherType = Attacher::AttachEngine3D
  X1 = -70121.8
  X2 = -70121.8
  Y1 = 293574
  Y2 = 292574
  Z1 = 0
  Z2 = 0
FEATURE [Part::Line] Axis_1_360
  AttacherType = Attacher::AttachEngine3D
  X1 = -70121.8
  X2 = -70121.8
  Y1 = 293574
  Y2 = 293574
  Z1 = 0
  Z2 = -1000
FEATURE [Part::Line] Axis_2_360
  AttacherType = Attacher::AttachEngine3D
  X1 = -70121.8
  X2 = -71121.8
  Y1 = 293574
  Y2 = 293574
  Z1 = 0
  Z2 = 0
FEATURE [Part::Feature] Heliostat_361  label="Heliostat_361(Mirror,Axis_1_361,Axis_2_361,Normal_361,Target_point)"
  Placement = pos=(118588,-239251,1.12173e-10) rot=(0,0,1;0rad)
  shape: bbox 10000 x 69.71 x 10000 mm, 1 faces, 0 solids (baked)
FEATURE [Part::Line] Normal_361
  AttacherType = Attacher::AttachEngine3D
  X1 = 118588
  X2 = 118588
  Y1 = 119372
  Y2 = 118372
  Z1 = 0
  Z2 = 0
FEATURE [Part::Line] Axis_1_361
  AttacherType = Attacher::AttachEngine3D
  X1 = 118588
  X2 = 118588
  Y1 = 119372
  Y2 = 119372
  Z1 = 0
  Z2 = -1000
FEATURE [Part::Line] Axis_2_361
  AttacherType = Attacher::AttachEngine3D
  X1 = 118588
  X2 = 117588
  Y1 = 119372
  Y2 = 119372
  Z1 = 0
  Z2 = 0
FEATURE [Part::Feature] Heliostat_362  label="Heliostat_362(Mirror,Axis_1_362,Axis_2_362,Normal_362,Target_point)"
  Placement = pos=(-118588,-239251,1.12173e-10) rot=(0,0,1;0rad)
  shape: bbox 10000 x 69.71 x 10000 mm, 1 faces, 0 solids (baked)
FEATURE [Part::Line] Normal_362
  AttacherType = Attacher::AttachEngine3D
  X1 = -118588
  X2 = -118588
  Y1 = 119372
  Y2 = 118372
  Z1 = 0
  Z2 = 0
FEATURE [Part::Line] Axis_1_362
  AttacherType = Attacher::AttachEngine3D
  X1 = -118588
  X2 = -118588
  Y1 = 119372
  Y2 = 119372
  Z1 = 0
  Z2 = -1000
FEATURE [Part::Line] Axis_2_362
  AttacherType = Attacher::AttachEngine3D
  X1 = -118588
  X2 = -119588
  Y1 = 119372
  Y2 = 119372
  Z1 = 0
  Z2 = 0
FEATURE [Part::Feature] Heliostat_363  label="Heliostat_363(Mirror,Axis_1_363,Axis_2_363,Normal_363,Target_point)"
  Placement = pos=(46987.1,-318103,1.69118e-10) rot=(0,0,1;0rad)
  shape: bbox 10000 x 40.57 x 10000 mm, 1 faces, 0 solids (baked)
FEATURE [Part::Line] Normal_363
  AttacherType = Attacher::AttachEngine3D
  X1 = 46987.1
  X2 = 46987.1
  Y1 = 298153
  Y2 = 297153
  Z1 = 0
  Z2 = 0
FEATURE [Part::Line] Axis_1_363
  AttacherType = Attacher::AttachEngine3D
  X1 = 46987.1
  X2 = 46987.1
  Y1 = 298153
  Y2 = 298153
  Z1 = 0
  Z2 = -1000
FEATURE [Part::Line] Axis_2_363
  AttacherType = Attacher::AttachEngine3D
  X1 = 46987.1
  X2 = 45987.1
  Y1 = 298153
  Y2 = 298153
  Z1 = 0
  Z2 = 0
FEATURE [Part::Feature] Heliostat_364  label="Heliostat_364(Mirror,Axis_1_364,Axis_2_364,Normal_364,Target_point)"
  Placement = pos=(-46987.1,-318103,1.69118e-10) rot=(0,0,1;0rad)
  shape: bbox 10000 x 40.57 x 10000 mm, 1 faces, 0 solids (baked)
FEATURE [Part::Line] Normal_364
  AttacherType = Attacher::AttachEngine3D
  X1 = -46987.1
  X2 = -46987.1
  Y1 = 298153
  Y2 = 297153
  Z1 = 0
  Z2 = 0
FEATURE [Part::Line] Axis_1_364
  AttacherType = Attacher::AttachEngine3D
  X1 = -46987.1
  X2 = -46987.1
  Y1 = 298153
  Y2 = 298153
  Z1 = 0
  Z2 = -1000
FEATURE [Part::Line] Axis_2_364
  AttacherType = Attacher::AttachEngine3D
  X1 = -46987.1
  X2 = -47987.1
  Y1 = 298153
  Y2 = 298153
  Z1 = 0
  Z2 = 0
FEATURE [Part::Feature] Heliostat_365  label="Heliostat_365(Mirror,Axis_1_365,Axis_2_365,Normal_365,Target_point)"
  Placement = pos=(-122449,-271780,3.5712e-12) rot=(0,0,1;0rad)
  shape: bbox 10000 x 55.53 x 10000 mm, 1 faces, 0 solids (baked)
FEATURE [Part::Line] Normal_365
  AttacherType = Attacher::AttachEngine3D
  X1 = -122449
  X2 = -122449
  Y1 = 178440
  Y2 = 177440
  Z1 = 0
  Z2 = 0
FEATURE [Part::Line] Axis_1_365
  AttacherType = Attacher::AttachEngine3D
  X1 = -122449
  X2 = -122449
  Y1 = 178440
  Y2 = 178440
  Z1 = 0
  Z2 = -1000
FEATURE [Part::Line] Axis_2_365
  AttacherType = Attacher::AttachEngine3D
  X1 = -122449
  X2 = -123449
  Y1 = 178440
  Y2 = 178440
  Z1 = 0
  Z2 = 0
FEATURE [Part::Feature] Heliostat_366  label="Heliostat_366(Mirror,Axis_1_366,Axis_2_366,Normal_366,Target_point)"
  Placement = pos=(122747,-286504,8.94339e-11) rot=(0,0,1;0rad)
  shape: bbox 10000 x 51.21 x 10000 mm, 1 faces, 0 solids (baked)
FEATURE [Part::Line] Normal_366
  AttacherType = Attacher::AttachEngine3D
  X1 = 122747
  X2 = 122747
  Y1 = 201677
  Y2 = 200677
  Z1 = 0
  Z2 = 0
FEATURE [Part::Line] Axis_1_366
  AttacherType = Attacher::AttachEngine3D
  X1 = 122747
  X2 = 122747
  Y1 = 201677
  Y2 = 201677
  Z1 = 0
  Z2 = -1000
FEATURE [Part::Line] Axis_2_366
  AttacherType = Attacher::AttachEngine3D
  X1 = 122747
  X2 = 121747
  Y1 = 201677
  Y2 = 201677
  Z1 = 0
  Z2 = 0
FEATURE [Part::Feature] Heliostat_367  label="Heliostat_367(Mirror,Axis_1_367,Axis_2_367,Normal_367,Target_point)"
  Placement = pos=(-122747,-286504,8.94339e-11) rot=(0,0,1;0rad)
  shape: bbox 10000 x 51.21 x 10000 mm, 1 faces, 0 solids (baked)
FEATURE [Part::Line] Normal_367
  AttacherType = Attacher::AttachEngine3D
  X1 = -122747
  X2 = -122747
  Y1 = 201677
  Y2 = 200677
  Z1 = 0
  Z2 = 0
FEATURE [Part::Line] Axis_1_367
  AttacherType = Attacher::AttachEngine3D
  X1 = -122747
  X2 = -122747
  Y1 = 201677
  Y2 = 201677
  Z1 = 0
  Z2 = -1000
FEATURE [Part::Line] Axis_2_367
  AttacherType = Attacher::AttachEngine3D
  X1 = -122747
  X2 = -123747
  Y1 = 201677
  Y2 = 201677
  Z1 = 0
  Z2 = 0
FEATURE [Part::Feature] Heliostat_368  label="Heliostat_368(Mirror,Axis_1_368,Axis_2_368,Normal_368,Target_point)"
  Placement = pos=(122449,-271780,3.5712e-12) rot=(0,0,1;0rad)
  shape: bbox 10000 x 55.53 x 10000 mm, 1 faces, 0 solids (baked)
FEATURE [Part::Line] Normal_368
  AttacherType = Attacher::AttachEngine3D
  X1 = 122449
  X2 = 122449
  Y1 = 178440
  Y2 = 177440
  Z1 = 0
  Z2 = 0
FEATURE [Part::Line] Axis_1_368
  AttacherType = Attacher::AttachEngine3D
  X1 = 122449
  X2 = 122449
  Y1 = 178440
  Y2 = 178440
  Z1 = 0
  Z2 = -1000
FEATURE [Part::Line] Axis_2_368
  AttacherType = Attacher::AttachEngine3D
  X1 = 122449
  X2 = 121449
  Y1 = 178440
  Y2 = 178440
  Z1 = 0
  Z2 = 0
FEATURE [Part::Feature] Heliostat_369  label="Heliostat_369(Mirror,Axis_1_369,Axis_2_369,Normal_369,Target_point)"
  Placement = pos=(-23565.5,-315345,1.69118e-10) rot=(0,0,1;0rad)
  shape: bbox 10000 x 40.57 x 10000 mm, 1 faces, 0 solids (baked)
FEATURE [Part::Line] Normal_369
  AttacherType = Attacher::AttachEngine3D
  X1 = -23565.5
  X2 = -23565.5
  Y1 = 300911
  Y2 = 299911
  Z1 = 0
  Z2 = 0
FEATURE [Part::Line] Axis_1_369
  AttacherType = Attacher::AttachEngine3D
  X1 = -23565.5
  X2 = -23565.5
  Y1 = 300911
  Y2 = 300911
  Z1 = 0
  Z2 = -1000
FEATURE [Part::Line] Axis_2_369
  AttacherType = Attacher::AttachEngine3D
  X1 = -23565.5
  X2 = -24565.5
  Y1 = 300911
  Y2 = 300911
  Z1 = 0
  Z2 = 0
FEATURE [Part::Feature] Heliostat_370  label="Heliostat_370(Mirror,Axis_1_370,Axis_2_370,Normal_370,Target_point)"
  Placement = pos=(23565.5,-315345,1.69118e-10) rot=(0,0,1;0rad)
  shape: bbox 10000 x 40.57 x 10000 mm, 1 faces, 0 solids (baked)
FEATURE [Part::Line] Normal_370
  AttacherType = Attacher::AttachEngine3D
  X1 = 23565.5
  X2 = 23565.5
  Y1 = 300911
  Y2 = 299911
  Z1 = 0
  Z2 = 0
FEATURE [Part::Line] Axis_1_370
  AttacherType = Attacher::AttachEngine3D
  X1 = 23565.5
  X2 = 23565.5
  Y1 = 300911
  Y2 = 300911
  Z1 = 0
  Z2 = -1000
FEATURE [Part::Line] Axis_2_370
  AttacherType = Attacher::AttachEngine3D
  X1 = 23565.5
  X2 = 22565.5
  Y1 = 300911
  Y2 = 300911
  Z1 = 0
  Z2 = 0
FEATURE [Part::Feature] Heliostat_371  label="Heliostat_371(Mirror,Axis_1_371,Axis_2_371,Normal_371,Target_point)"
  Placement = pos=(3.37488e-10,-314423,1.64204e-10) rot=(0,0,1;0rad)
  shape: bbox 10000 x 40.57 x 10000 mm, 1 faces, 0 solids (baked)
FEATURE [Part::Line] Normal_371
  AttacherType = Attacher::AttachEngine3D
  X1 = 0
  X2 = 0
  Y1 = 301833
  Y2 = 300833
  Z1 = 0
  Z2 = 0
FEATURE [Part::Line] Axis_1_371
  AttacherType = Attacher::AttachEngine3D
  X1 = 0
  X2 = 0
  Y1 = 301833
  Y2 = 301833
  Z1 = 0
  Z2 = -1000
FEATURE [Part::Line] Axis_2_371
  AttacherType = Attacher::AttachEngine3D
  X1 = 0
  X2 = -1000
  Y1 = 301833
  Y2 = 301833
  Z1 = 0
  Z2 = 0
FEATURE [Part::Feature] Heliostat_372  label="Heliostat_372(Mirror,Axis_1_372,Axis_2_372,Normal_372,Target_point)"
  Placement = pos=(32609.7,-294324,1.0474e-10) rot=(0,0,1;0rad)
  shape: bbox 10000 x 43.77 x 10000 mm, 1 faces, 0 solids (baked)
FEATURE [Part::Line] Normal_372
  AttacherType = Attacher::AttachEngine3D
  X1 = 32609.7
  X2 = 32609.7
  Y1 = 276890
  Y2 = 275890
  Z1 = 0
  Z2 = 0
FEATURE [Part::Line] Axis_1_372
  AttacherType = Attacher::AttachEngine3D
  X1 = 32609.7
  X2 = 32609.7
  Y1 = 276890
  Y2 = 276890
  Z1 = 0
  Z2 = -1000
FEATURE [Part::Line] Axis_2_372
  AttacherType = Attacher::AttachEngine3D
  X1 = 32609.7
  X2 = 31609.7
  Y1 = 276890
  Y2 = 276890
  Z1 = 0
  Z2 = 0
FEATURE [Part::Feature] Heliostat_373  label="Heliostat_373(Mirror,Axis_1_373,Axis_2_373,Normal_373,Target_point)"
  Placement = pos=(-32609.7,-294324,1.0474e-10) rot=(0,0,1;0rad)
  shape: bbox 10000 x 43.77 x 10000 mm, 1 faces, 0 solids (baked)
FEATURE [Part::Line] Normal_373
  AttacherType = Attacher::AttachEngine3D
  X1 = -32609.7
  X2 = -32609.7
  Y1 = 276890
  Y2 = 275890
  Z1 = 0
  Z2 = 0
FEATURE [Part::Line] Axis_1_373
  AttacherType = Attacher::AttachEngine3D
  X1 = -32609.7
  X2 = -32609.7
  Y1 = 276890
  Y2 = 276890
  Z1 = 0
  Z2 = -1000
FEATURE [Part::Line] Axis_2_373
  AttacherType = Attacher::AttachEngine3D
  X1 = -32609.7
  X2 = -33609.7
  Y1 = 276890
  Y2 = 276890
  Z1 = 0
  Z2 = 0
FEATURE [Part::Feature] Heliostat_374  label="Heliostat_374(Mirror,Axis_1_374,Axis_2_374,Normal_374,Target_point)"
  Placement = pos=(135619,-327618,5.24243e-11) rot=(0,0,1;0rad)
  shape: bbox 10000 x 43.77 x 10000 mm, 1 faces, 0 solids (baked)
FEATURE [Part::Line] Normal_374
  AttacherType = Attacher::AttachEngine3D
  X1 = 135619
  X2 = 135619
  Y1 = 243596
  Y2 = 242596
  Z1 = 0
  Z2 = 0
FEATURE [Part::Line] Axis_1_374
  AttacherType = Attacher::AttachEngine3D
  X1 = 135619
  X2 = 135619
  Y1 = 243596
  Y2 = 243596
  Z1 = 0
  Z2 = -1000
FEATURE [Part::Line] Axis_2_374
  AttacherType = Attacher::AttachEngine3D
  X1 = 135619
  X2 = 134619
  Y1 = 243596
  Y2 = 243596
  Z1 = 0
  Z2 = 0
FEATURE [Part::Feature] Heliostat_375  label="Heliostat_375(Mirror,Axis_1_375,Axis_2_375,Normal_375,Target_point)"
  Placement = pos=(-135619,-327618,5.24243e-11) rot=(0,0,1;0rad)
  shape: bbox 10000 x 43.77 x 10000 mm, 1 faces, 0 solids (baked)
FEATURE [Part::Line] Normal_375
  AttacherType = Attacher::AttachEngine3D
  X1 = -135619
  X2 = -135619
  Y1 = 243596
  Y2 = 242596
  Z1 = 0
  Z2 = 0
FEATURE [Part::Line] Axis_1_375
  AttacherType = Attacher::AttachEngine3D
  X1 = -135619
  X2 = -135619
  Y1 = 243596
  Y2 = 243596
  Z1 = 0
  Z2 = -1000
FEATURE [Part::Line] Axis_2_375
  AttacherType = Attacher::AttachEngine3D
  X1 = -135619
  X2 = -136619
  Y1 = 243596
  Y2 = 243596
  Z1 = 0
  Z2 = 0
FEATURE [Part::Feature] Heliostat_376  label="Heliostat_376(Mirror,Axis_1_376,Axis_2_376,Normal_376,Target_point)"
  Placement = pos=(90161.7,-191660,8.4983e-11) rot=(0,0,1;0rad)
  shape: bbox 10000 x 105.8 x 10000 mm, 1 faces, 0 solids (baked)
FEATURE [Part::Line] Normal_376
  AttacherType = Attacher::AttachEngine3D
  X1 = 90161.7
  X2 = 90161.7
  Y1 = 44718
  Y2 = 43718
  Z1 = 0
  Z2 = 0
FEATURE [Part::Line] Axis_1_376
  AttacherType = Attacher::AttachEngine3D
  X1 = 90161.7
  X2 = 90161.7
  Y1 = 44718
  Y2 = 44718
  Z1 = 0
  Z2 = -1000
FEATURE [Part::Line] Axis_2_376
  AttacherType = Attacher::AttachEngine3D
  X1 = 90161.7
  X2 = 89161.7
  Y1 = 44718
  Y2 = 44718
  Z1 = 0
  Z2 = 0
FEATURE [Part::Feature] Heliostat_377  label="Heliostat_377(Mirror,Axis_1_377,Axis_2_377,Normal_377,Target_point)"
  Placement = pos=(-90161.7,-191660,8.4983e-11) rot=(0,0,1;0rad)
  shape: bbox 10000 x 105.8 x 10000 mm, 1 faces, 0 solids (baked)
FEATURE [Part::Line] Normal_377
  AttacherType = Attacher::AttachEngine3D
  X1 = -90161.7
  X2 = -90161.7
  Y1 = 44718
  Y2 = 43718
  Z1 = 0
  Z2 = 0
FEATURE [Part::Line] Axis_1_377
  AttacherType = Attacher::AttachEngine3D
  X1 = -90161.7
  X2 = -90161.7
  Y1 = 44718
  Y2 = 44718
  Z1 = 0
  Z2 = -1000
FEATURE [Part::Line] Axis_2_377
  AttacherType = Attacher::AttachEngine3D
  X1 = -90161.7
  X2 = -91161.7
  Y1 = 44718
  Y2 = 44718
  Z1 = 0
  Z2 = 0
FEATURE [Part::Feature] Heliostat_378  label="Heliostat_378(Mirror,Axis_1_378,Axis_2_378,Normal_378,Target_point)"
  Placement = pos=(84532.4,-237152,4.25141e-11) rot=(0,0,1;0rad)
  shape: bbox 10000 x 59.82 x 10000 mm, 1 faces, 0 solids (baked)
FEATURE [Part::Line] Normal_378
  AttacherType = Attacher::AttachEngine3D
  X1 = 84532.4
  X2 = 84532.4
  Y1 = 180779
  Y2 = 179779
  Z1 = 0
  Z2 = 0
FEATURE [Part::Line] Axis_1_378
  AttacherType = Attacher::AttachEngine3D
  X1 = 84532.4
  X2 = 84532.4
  Y1 = 180779
  Y2 = 180779
  Z1 = 0
  Z2 = -1000
FEATURE [Part::Line] Axis_2_378
  AttacherType = Attacher::AttachEngine3D
  X1 = 84532.4
  X2 = 83532.4
  Y1 = 180779
  Y2 = 180779
  Z1 = 0
  Z2 = 0
FEATURE [Part::Feature] Heliostat_379  label="Heliostat_379(Mirror,Axis_1_379,Axis_2_379,Normal_379,Target_point)"
  Placement = pos=(-84532.4,-237152,4.25141e-11) rot=(0,0,1;0rad)
  shape: bbox 10000 x 59.82 x 10000 mm, 1 faces, 0 solids (baked)
FEATURE [Part::Line] Normal_379
  AttacherType = Attacher::AttachEngine3D
  X1 = -84532.4
  X2 = -84532.4
  Y1 = 180779
  Y2 = 179779
  Z1 = 0
  Z2 = 0
FEATURE [Part::Line] Axis_1_379
  AttacherType = Attacher::AttachEngine3D
  X1 = -84532.4
  X2 = -84532.4
  Y1 = 180779
  Y2 = 180779
  Z1 = 0
  Z2 = -1000
FEATURE [Part::Line] Axis_2_379
  AttacherType = Attacher::AttachEngine3D
  X1 = -84532.4
  X2 = -85532.4
  Y1 = 180779
  Y2 = 180779
  Z1 = 0
  Z2 = 0
FEATURE [Part::Feature] Heliostat_380  label="Heliostat_380(Mirror,Axis_1_380,Axis_2_380,Normal_380,Target_point)"
  Placement = pos=(100005,-274313,8.0063e-12) rot=(0,0,1;0rad)
  shape: bbox 10000 x 51.21 x 10000 mm, 1 faces, 0 solids (baked)
FEATURE [Part::Line] Normal_380
  AttacherType = Attacher::AttachEngine3D
  X1 = 100005
  X2 = 100005
  Y1 = 213867
  Y2 = 212867
  Z1 = 0
  Z2 = 0
FEATURE [Part::Line] Axis_1_380
  AttacherType = Attacher::AttachEngine3D
  X1 = 100005
  X2 = 100005
  Y1 = 213867
  Y2 = 213867
  Z1 = 0
  Z2 = -1000
FEATURE [Part::Line] Axis_2_380
  AttacherType = Attacher::AttachEngine3D
  X1 = 100005
  X2 = 99004.8
  Y1 = 213867
  Y2 = 213867
  Z1 = 0
  Z2 = 0
FEATURE [Part::Feature] Heliostat_381  label="Heliostat_381(Mirror,Axis_1_381,Axis_2_381,Normal_381,Target_point)"
  Placement = pos=(-100005,-274313,8.0063e-12) rot=(0,0,1;0rad)
  shape: bbox 10000 x 51.21 x 10000 mm, 1 faces, 0 solids (baked)
FEATURE [Part::Line] Normal_381
  AttacherType = Attacher::AttachEngine3D
  X1 = -100005
  X2 = -100005
  Y1 = 213867
  Y2 = 212867
  Z1 = 0
  Z2 = 0
FEATURE [Part::Line] Axis_1_381
  AttacherType = Attacher::AttachEngine3D
  X1 = -100005
  X2 = -100005
  Y1 = 213867
  Y2 = 213867
  Z1 = 0
  Z2 = -1000
FEATURE [Part::Line] Axis_2_381
  AttacherType = Attacher::AttachEngine3D
  X1 = -100005
  X2 = -101005
  Y1 = 213867
  Y2 = 213867
  Z1 = 0
  Z2 = 0
FEATURE [Part::Feature] Heliostat_382  label="Heliostat_382(Mirror,Axis_1_382,Axis_2_382,Normal_382,Target_point)"
  Placement = pos=(119208,-247405,1.02726e-10) rot=(0,0,1;0rad)
  shape: bbox 10000 x 64.79 x 10000 mm, 1 faces, 0 solids (baked)
FEATURE [Part::Line] Normal_382
  AttacherType = Attacher::AttachEngine3D
  X1 = 119208
  X2 = 119208
  Y1 = 138476
  Y2 = 137476
  Z1 = 0
  Z2 = 0
FEATURE [Part::Line] Axis_1_382
  AttacherType = Attacher::AttachEngine3D
  X1 = 119208
  X2 = 119208
  Y1 = 138476
  Y2 = 138476
  Z1 = 0
  Z2 = -1000
FEATURE [Part::Line] Axis_2_382
  AttacherType = Attacher::AttachEngine3D
  X1 = 119208
  X2 = 118208
  Y1 = 138476
  Y2 = 138476
  Z1 = 0
  Z2 = 0
FEATURE [Part::Feature] Heliostat_383  label="Heliostat_383(Mirror,Axis_1_383,Axis_2_383,Normal_383,Target_point)"
  Placement = pos=(-119208,-247405,1.02726e-10) rot=(0,0,1;0rad)
  shape: bbox 10000 x 64.79 x 10000 mm, 1 faces, 0 solids (baked)
FEATURE [Part::Line] Normal_383
  AttacherType = Attacher::AttachEngine3D
  X1 = -119208
  X2 = -119208
  Y1 = 138476
  Y2 = 137476
  Z1 = 0
  Z2 = 0
FEATURE [Part::Line] Axis_1_383
  AttacherType = Attacher::AttachEngine3D
  X1 = -119208
  X2 = -119208
  Y1 = 138476
  Y2 = 138476
  Z1 = 0
  Z2 = -1000
FEATURE [Part::Line] Axis_2_383
  AttacherType = Attacher::AttachEngine3D
  X1 = -119208
  X2 = -120208
  Y1 = 138476
  Y2 = 138476
  Z1 = 0
  Z2 = 0
FEATURE [Part::Feature] Heliostat_384  label="Heliostat_384(Mirror,Axis_1_384,Axis_2_384,Normal_384,Target_point)"
  Placement = pos=(102245,-259483,3.5712e-12) rot=(0,0,1;0rad)
  shape: bbox 10000 x 55.53 x 10000 mm, 1 faces, 0 solids (baked)
FEATURE [Part::Line] Normal_384
  AttacherType = Attacher::AttachEngine3D
  X1 = 102245
  X2 = 102245
  Y1 = 190737
  Y2 = 189737
  Z1 = 0
  Z2 = 0
FEATURE [Part::Line] Axis_1_384
  AttacherType = Attacher::AttachEngine3D
  X1 = 102245
  X2 = 102245
  Y1 = 190737
  Y2 = 190737
  Z1 = 0
  Z2 = -1000
FEATURE [Part::Line] Axis_2_384
  AttacherType = Attacher::AttachEngine3D
  X1 = 102245
  X2 = 101245
  Y1 = 190737
  Y2 = 190737
  Z1 = 0
  Z2 = 0
FEATURE [Part::Feature] Heliostat_385  label="Heliostat_385(Mirror,Axis_1_385,Axis_2_385,Normal_385,Target_point)"
  Placement = pos=(-102245,-259483,3.5712e-12) rot=(0,0,1;0rad)
  shape: bbox 10000 x 55.53 x 10000 mm, 1 faces, 0 solids (baked)
FEATURE [Part::Line] Normal_385
  AttacherType = Attacher::AttachEngine3D
  X1 = -102245
  X2 = -102245
  Y1 = 190737
  Y2 = 189737
  Z1 = 0
  Z2 = 0
FEATURE [Part::Line] Axis_1_385
  AttacherType = Attacher::AttachEngine3D
  X1 = -102245
  X2 = -102245
  Y1 = 190737
  Y2 = 190737
  Z1 = 0
  Z2 = -1000
FEATURE [Part::Line] Axis_2_385
  AttacherType = Attacher::AttachEngine3D
  X1 = -102245
  X2 = -103245
  Y1 = 190737
  Y2 = 190737
  Z1 = 0
  Z2 = 0
FEATURE [Part::Feature] Heliostat_386  label="Heliostat_386(Mirror,Axis_1_386,Axis_2_386,Normal_386,Target_point)"
  Placement = pos=(97424.7,-289854,1.40591e-10) rot=(0,0,1;0rad)
  shape: bbox 10000 x 47.5 x 10000 mm, 1 faces, 0 solids (baked)
FEATURE [Part::Line] Normal_386
  AttacherType = Attacher::AttachEngine3D
  X1 = 97424.7
  X2 = 97424.7
  Y1 = 236493
  Y2 = 235493
  Z1 = 0
  Z2 = 0
FEATURE [Part::Line] Axis_1_386
  AttacherType = Attacher::AttachEngine3D
  X1 = 97424.7
  X2 = 97424.7
  Y1 = 236493
  Y2 = 236493
  Z1 = 0
  Z2 = -1000
FEATURE [Part::Line] Axis_2_386
  AttacherType = Attacher::AttachEngine3D
  X1 = 97424.7
  X2 = 96424.7
  Y1 = 236493
  Y2 = 236493
  Z1 = 0
  Z2 = 0
FEATURE [Part::Feature] Heliostat_387  label="Heliostat_387(Mirror,Axis_1_387,Axis_2_387,Normal_387,Target_point)"
  Placement = pos=(-97424.7,-289854,1.40591e-10) rot=(0,0,1;0rad)
  shape: bbox 10000 x 47.5 x 10000 mm, 1 faces, 0 solids (baked)
FEATURE [Part::Line] Normal_387
  AttacherType = Attacher::AttachEngine3D
  X1 = -97424.7
  X2 = -97424.7
  Y1 = 236493
  Y2 = 235493
  Z1 = 0
  Z2 = 0
FEATURE [Part::Line] Axis_1_387
  AttacherType = Attacher::AttachEngine3D
  X1 = -97424.7
  X2 = -97424.7
  Y1 = 236493
  Y2 = 236493
  Z1 = 0
  Z2 = -1000
FEATURE [Part::Line] Axis_2_387
  AttacherType = Attacher::AttachEngine3D
  X1 = -97424.7
  X2 = -98424.7
  Y1 = 236493
  Y2 = 236493
  Z1 = 0
  Z2 = 0
FEATURE [Part::Feature] Heliostat_388  label="Heliostat_388(Mirror,Axis_1_388,Axis_2_388,Normal_388,Target_point)"
  Placement = pos=(68235.5,-216381,1.02726e-10) rot=(0,0,1;0rad)
  shape: bbox 10000 x 64.79 x 10000 mm, 1 faces, 0 solids (baked)
FEATURE [Part::Line] Normal_388
  AttacherType = Attacher::AttachEngine3D
  X1 = 68235.5
  X2 = 68235.5
  Y1 = 169500
  Y2 = 168500
  Z1 = 0
  Z2 = 0
FEATURE [Part::Line] Axis_1_388
  AttacherType = Attacher::AttachEngine3D
  X1 = 68235.5
  X2 = 68235.5
  Y1 = 169500
  Y2 = 169500
  Z1 = 0
  Z2 = -1000
FEATURE [Part::Line] Axis_2_388
  AttacherType = Attacher::AttachEngine3D
  X1 = 68235.5
  X2 = 67235.5
  Y1 = 169500
  Y2 = 169500
  Z1 = 0
  Z2 = 0
FEATURE [Part::Feature] Heliostat_389  label="Heliostat_389(Mirror,Axis_1_389,Axis_2_389,Normal_389,Target_point)"
  Placement = pos=(-68235.5,-216381,1.02726e-10) rot=(0,0,1;0rad)
  shape: bbox 10000 x 64.79 x 10000 mm, 1 faces, 0 solids (baked)
FEATURE [Part::Line] Normal_389
  AttacherType = Attacher::AttachEngine3D
  X1 = -68235.5
  X2 = -68235.5
  Y1 = 169500
  Y2 = 168500
  Z1 = 0
  Z2 = 0
FEATURE [Part::Line] Axis_1_389
  AttacherType = Attacher::AttachEngine3D
  X1 = -68235.5
  X2 = -68235.5
  Y1 = 169500
  Y2 = 169500
  Z1 = 0
  Z2 = -1000
FEATURE [Part::Line] Axis_2_389
  AttacherType = Attacher::AttachEngine3D
  X1 = -68235.5
  X2 = -69235.5
  Y1 = 169500
  Y2 = 169500
  Z1 = 0
  Z2 = 0
FEATURE [Part::Feature] Heliostat_390  label="Heliostat_390(Mirror,Axis_1_390,Axis_2_390,Normal_390,Target_point)"
  Placement = pos=(96044.5,-309475,5.58821e-11) rot=(0,0,1;0rad)
  shape: bbox 10000 x 43.77 x 10000 mm, 1 faces, 0 solids (baked)
FEATURE [Part::Line] Normal_390
  AttacherType = Attacher::AttachEngine3D
  X1 = 96044.5
  X2 = 96044.5
  Y1 = 261738
  Y2 = 260738
  Z1 = 0
  Z2 = 0
FEATURE [Part::Line] Axis_1_390
  AttacherType = Attacher::AttachEngine3D
  X1 = 96044.5
  X2 = 96044.5
  Y1 = 261738
  Y2 = 261738
  Z1 = 0
  Z2 = -1000
FEATURE [Part::Line] Axis_2_390
  AttacherType = Attacher::AttachEngine3D
  X1 = 96044.5
  X2 = 95044.5
  Y1 = 261738
  Y2 = 261738
  Z1 = 0
  Z2 = 0
FEATURE [Part::Feature] Heliostat_391  label="Heliostat_391(Mirror,Axis_1_391,Axis_2_391,Normal_391,Target_point)"
  Placement = pos=(-96044.5,-309475,5.58821e-11) rot=(0,0,1;0rad)
  shape: bbox 10000 x 43.77 x 10000 mm, 1 faces, 0 solids (baked)
FEATURE [Part::Line] Normal_391
  AttacherType = Attacher::AttachEngine3D
  X1 = -96044.5
  X2 = -96044.5
  Y1 = 261738
  Y2 = 260738
  Z1 = 0
  Z2 = 0
FEATURE [Part::Line] Axis_1_391
  AttacherType = Attacher::AttachEngine3D
  X1 = -96044.5
  X2 = -96044.5
  Y1 = 261738
  Y2 = 261738
  Z1 = 0
  Z2 = -1000
FEATURE [Part::Line] Axis_2_391
  AttacherType = Attacher::AttachEngine3D
  X1 = -96044.5
  X2 = -97044.5
  Y1 = 261738
  Y2 = 261738
  Z1 = 0
  Z2 = 0
FEATURE [Part::Feature] Heliostat_392  label="Heliostat_392(Mirror,Axis_1_392,Axis_2_392,Normal_392,Target_point)"
  Placement = pos=(-98521.1,-213531,8.98539e-11) rot=(0,0,1;0rad)
  shape: bbox 10000 x 75.38 x 10000 mm, 1 faces, 0 solids (baked)
FEATURE [Part::Line] Normal_392
  AttacherType = Attacher::AttachEngine3D
  X1 = -98521.1
  X2 = -98521.1
  Y1 = 118113
  Y2 = 117113
  Z1 = 0
  Z2 = 0
FEATURE [Part::Line] Axis_1_392
  AttacherType = Attacher::AttachEngine3D
  X1 = -98521.1
  X2 = -98521.1
  Y1 = 118113
  Y2 = 118113
  Z1 = 0
  Z2 = -1000
FEATURE [Part::Line] Axis_2_392
  AttacherType = Attacher::AttachEngine3D
  X1 = -98521.1
  X2 = -99521.1
  Y1 = 118113
  Y2 = 118113
  Z1 = 0
  Z2 = 0
FEATURE [Part::Feature] Heliostat_393  label="Heliostat_393(Mirror,Axis_1_393,Axis_2_393,Normal_393,Target_point)"
  Placement = pos=(98521.1,-213531,8.98539e-11) rot=(0,0,1;0rad)
  shape: bbox 10000 x 75.38 x 10000 mm, 1 faces, 0 solids (baked)
FEATURE [Part::Line] Normal_393
  AttacherType = Attacher::AttachEngine3D
  X1 = 98521.1
  X2 = 98521.1
  Y1 = 118113
  Y2 = 117113
  Z1 = 0
  Z2 = 0
FEATURE [Part::Line] Axis_1_393
  AttacherType = Attacher::AttachEngine3D
  X1 = 98521.1
  X2 = 98521.1
  Y1 = 118113
  Y2 = 118113
  Z1 = 0
  Z2 = -1000
FEATURE [Part::Line] Axis_2_393
  AttacherType = Attacher::AttachEngine3D
  X1 = 98521.1
  X2 = 97521.1
  Y1 = 118113
  Y2 = 118113
  Z1 = 0
  Z2 = 0
FEATURE [Part::Feature] Heliostat_394  label="Heliostat_394(Mirror,Axis_1_394,Axis_2_394,Normal_394,Target_point)"
  Placement = pos=(115474,-227154,3.0826e-11) rot=(0,0,1;0rad)
  shape: bbox 10000 x 80.99 x 10000 mm, 1 faces, 0 solids (baked)
FEATURE [Part::Line] Normal_394
  AttacherType = Attacher::AttachEngine3D
  X1 = 115474
  X2 = 115474
  Y1 = 81550.6
  Y2 = 80550.6
  Z1 = 0
  Z2 = 0
FEATURE [Part::Line] Axis_1_394
  AttacherType = Attacher::AttachEngine3D
  X1 = 115474
  X2 = 115474
  Y1 = 81550.6
  Y2 = 81550.6
  Z1 = 0
  Z2 = -1000
FEATURE [Part::Line] Axis_2_394
  AttacherType = Attacher::AttachEngine3D
  X1 = 115474
  X2 = 114474
  Y1 = 81550.6
  Y2 = 81550.6
  Z1 = 0
  Z2 = 0
FEATURE [Part::Feature] Heliostat_395  label="Heliostat_395(Mirror,Axis_1_395,Axis_2_395,Normal_395,Target_point)"
  Placement = pos=(-115474,-227154,3.0826e-11) rot=(0,0,1;0rad)
  shape: bbox 10000 x 80.99 x 10000 mm, 1 faces, 0 solids (baked)
FEATURE [Part::Line] Normal_395
  AttacherType = Attacher::AttachEngine3D
  X1 = -115474
  X2 = -115474
  Y1 = 81550.6
  Y2 = 80550.6
  Z1 = 0
  Z2 = 0
FEATURE [Part::Line] Axis_1_395
  AttacherType = Attacher::AttachEngine3D
  X1 = -115474
  X2 = -115474
  Y1 = 81550.6
  Y2 = 81550.6
  Z1 = 0
  Z2 = -1000
FEATURE [Part::Line] Axis_2_395
  AttacherType = Attacher::AttachEngine3D
  X1 = -115474
  X2 = -116474
  Y1 = 81550.6
  Y2 = 81550.6
  Z1 = 0
  Z2 = 0
FEATURE [Part::Feature] Heliostat_396  label="Heliostat_396(Mirror,Axis_1_396,Axis_2_396,Normal_396,Target_point)"
  Placement = pos=(76068,-264677,8.94339e-11) rot=(0,0,1;0rad)
  shape: bbox 10000 x 51.21 x 10000 mm, 1 faces, 0 solids (baked)
FEATURE [Part::Line] Normal_396
  AttacherType = Attacher::AttachEngine3D
  X1 = 76068
  X2 = 76068
  Y1 = 223504
  Y2 = 222504
  Z1 = 0
  Z2 = 0
FEATURE [Part::Line] Axis_1_396
  AttacherType = Attacher::AttachEngine3D
  X1 = 76068
  X2 = 76068
  Y1 = 223504
  Y2 = 223504
  Z1 = 0
  Z2 = -1000
FEATURE [Part::Line] Axis_2_396
  AttacherType = Attacher::AttachEngine3D
  X1 = 76068
  X2 = 75068
  Y1 = 223504
  Y2 = 223504
  Z1 = 0
  Z2 = 0
FEATURE [Part::Feature] Heliostat_397  label="Heliostat_397(Mirror,Axis_1_397,Axis_2_397,Normal_397,Target_point)"
  Placement = pos=(-76068,-264677,8.94339e-11) rot=(0,0,1;0rad)
  shape: bbox 10000 x 51.21 x 10000 mm, 1 faces, 0 solids (baked)
FEATURE [Part::Line] Normal_397
  AttacherType = Attacher::AttachEngine3D
  X1 = -76068
  X2 = -76068
  Y1 = 223504
  Y2 = 222504
  Z1 = 0
  Z2 = 0
FEATURE [Part::Line] Axis_1_397
  AttacherType = Attacher::AttachEngine3D
  X1 = -76068
  X2 = -76068
  Y1 = 223504
  Y2 = 223504
  Z1 = 0
  Z2 = -1000
FEATURE [Part::Line] Axis_2_397
  AttacherType = Attacher::AttachEngine3D
  X1 = -76068
  X2 = -77068
  Y1 = 223504
  Y2 = 223504
  Z1 = 0
  Z2 = 0
FEATURE [Part::Feature] Heliostat_398  label="Heliostat_398(Mirror,Axis_1_398,Axis_2_398,Normal_398,Target_point)"
  Placement = pos=(96158.8,-220542,1.27963e-10) rot=(0,0,1;0rad)
  shape: bbox 10000 x 69.71 x 10000 mm, 1 faces, 0 solids (baked)
FEATURE [Part::Line] Normal_398
  AttacherType = Attacher::AttachEngine3D
  X1 = 96158.8
  X2 = 96158.8
  Y1 = 138080
  Y2 = 137080
  Z1 = 0
  Z2 = 0
FEATURE [Part::Line] Axis_1_398
  AttacherType = Attacher::AttachEngine3D
  X1 = 96158.8
  X2 = 96158.8
  Y1 = 138080
  Y2 = 138080
  Z1 = 0
  Z2 = -1000
FEATURE [Part::Line] Axis_2_398
  AttacherType = Attacher::AttachEngine3D
  X1 = 96158.8
  X2 = 95158.8
  Y1 = 138080
  Y2 = 138080
  Z1 = 0
  Z2 = 0
FEATURE [Part::Feature] Heliostat_399  label="Heliostat_399(Mirror,Axis_1_399,Axis_2_399,Normal_399,Target_point)"
  Placement = pos=(-96158.8,-220542,1.27963e-10) rot=(0,0,1;0rad)
  shape: bbox 10000 x 69.71 x 10000 mm, 1 faces, 0 solids (baked)
FEATURE [Part::Line] Normal_399
  AttacherType = Attacher::AttachEngine3D
  X1 = -96158.8
  X2 = -96158.8
  Y1 = 138080
  Y2 = 137080
  Z1 = 0
  Z2 = 0
FEATURE [Part::Line] Axis_1_399
  AttacherType = Attacher::AttachEngine3D
  X1 = -96158.8
  X2 = -96158.8
  Y1 = 138080
  Y2 = 138080
  Z1 = 0
  Z2 = -1000
FEATURE [Part::Line] Axis_2_399
  AttacherType = Attacher::AttachEngine3D
  X1 = -96158.8
  X2 = -97158.8
  Y1 = 138080
  Y2 = 138080
  Z1 = 0
  Z2 = 0
FEATURE [Part::Feature] Heliostat_400  label="Heliostat_400(Mirror,Axis_1_400,Axis_2_400,Normal_400,Target_point)"
  Placement = pos=(80818.5,-249464,4.47692e-11) rot=(0,0,1;0rad)
  shape: bbox 10000 x 55.53 x 10000 mm, 1 faces, 0 solids (baked)
FEATURE [Part::Line] Normal_400
  AttacherType = Attacher::AttachEngine3D
  X1 = 80818.5
  X2 = 80818.5
  Y1 = 200756
  Y2 = 199756
  Z1 = 0
  Z2 = 0
FEATURE [Part::Line] Axis_1_400
  AttacherType = Attacher::AttachEngine3D
  X1 = 80818.5
  X2 = 80818.5
  Y1 = 200756
  Y2 = 200756
  Z1 = 0
  Z2 = -1000
FEATURE [Part::Line] Axis_2_400
  AttacherType = Attacher::AttachEngine3D
  X1 = 80818.5
  X2 = 79818.5
  Y1 = 200756
  Y2 = 200756
  Z1 = 0
  Z2 = 0
FEATURE [Part::Feature] Heliostat_401  label="Heliostat_401(Mirror,Axis_1_401,Axis_2_401,Normal_401,Target_point)"
  Placement = pos=(-80818.5,-249464,4.47692e-11) rot=(0,0,1;0rad)
  shape: bbox 10000 x 55.53 x 10000 mm, 1 faces, 0 solids (baked)
FEATURE [Part::Line] Normal_401
  AttacherType = Attacher::AttachEngine3D
  X1 = -80818.5
  X2 = -80818.5
  Y1 = 200756
  Y2 = 199756
  Z1 = 0
  Z2 = 0
FEATURE [Part::Line] Axis_1_401
  AttacherType = Attacher::AttachEngine3D
  X1 = -80818.5
  X2 = -80818.5
  Y1 = 200756
  Y2 = 200756
  Z1 = 0
  Z2 = -1000
FEATURE [Part::Line] Axis_2_401
  AttacherType = Attacher::AttachEngine3D
  X1 = -80818.5
  X2 = -81818.5
  Y1 = 200756
  Y2 = 200756
  Z1 = 0
  Z2 = 0
FEATURE [Part::Feature] Heliostat_402  label="Heliostat_402(Mirror,Axis_1_402,Axis_2_402,Normal_402,Target_point)"
  Placement = pos=(121740,-259798,4.25141e-11) rot=(0,0,1;0rad)
  shape: bbox 10000 x 59.82 x 10000 mm, 1 faces, 0 solids (baked)
FEATURE [Part::Line] Normal_402
  AttacherType = Attacher::AttachEngine3D
  X1 = 121740
  X2 = 121740
  Y1 = 158133
  Y2 = 157133
  Z1 = 0
  Z2 = 0
FEATURE [Part::Line] Axis_1_402
  AttacherType = Attacher::AttachEngine3D
  X1 = 121740
  X2 = 121740
  Y1 = 158133
  Y2 = 158133
  Z1 = 0
  Z2 = -1000
FEATURE [Part::Line] Axis_2_402
  AttacherType = Attacher::AttachEngine3D
  X1 = 121740
  X2 = 120740
  Y1 = 158133
  Y2 = 158133
  Z1 = 0
  Z2 = 0
FEATURE [Part::Feature] Heliostat_403  label="Heliostat_403(Mirror,Axis_1_403,Axis_2_403,Normal_403,Target_point)"
  Placement = pos=(-121740,-259798,4.25141e-11) rot=(0,0,1;0rad)
  shape: bbox 10000 x 59.82 x 10000 mm, 1 faces, 0 solids (baked)
FEATURE [Part::Line] Normal_403
  AttacherType = Attacher::AttachEngine3D
  X1 = -121740
  X2 = -121740
  Y1 = 158133
  Y2 = 157133
  Z1 = 0
  Z2 = 0
FEATURE [Part::Line] Axis_1_403
  AttacherType = Attacher::AttachEngine3D
  X1 = -121740
  X2 = -121740
  Y1 = 158133
  Y2 = 158133
  Z1 = 0
  Z2 = -1000
FEATURE [Part::Line] Axis_2_403
  AttacherType = Attacher::AttachEngine3D
  X1 = -121740
  X2 = -122740
  Y1 = 158133
  Y2 = 158133
  Z1 = 0
  Z2 = 0
FEATURE [Part::Feature] Heliostat_404  label="Heliostat_404(Mirror,Axis_1_404,Axis_2_404,Normal_404,Target_point)"
  Placement = pos=(54128.2,-297715,9.3684e-12) rot=(0,0,1;0rad)
  shape: bbox 10000 x 43.77 x 10000 mm, 1 faces, 0 solids (baked)
FEATURE [Part::Line] Normal_404
  AttacherType = Attacher::AttachEngine3D
  X1 = 54128.2
  X2 = 54128.2
  Y1 = 273499
  Y2 = 272499
  Z1 = 0
  Z2 = 0
FEATURE [Part::Line] Axis_1_404
  AttacherType = Attacher::AttachEngine3D
  X1 = 54128.2
  X2 = 54128.2
  Y1 = 273499
  Y2 = 273499
  Z1 = 0
  Z2 = -1000
FEATURE [Part::Line] Axis_2_404
  AttacherType = Attacher::AttachEngine3D
  X1 = 54128.2
  X2 = 53128.2
  Y1 = 273499
  Y2 = 273499
  Z1 = 0
  Z2 = 0
FEATURE [Part::Feature] Heliostat_405  label="Heliostat_405(Mirror,Axis_1_405,Axis_2_405,Normal_405,Target_point)"
  Placement = pos=(-54128.2,-297715,9.3684e-12) rot=(0,0,1;0rad)
  shape: bbox 10000 x 43.77 x 10000 mm, 1 faces, 0 solids (baked)
FEATURE [Part::Line] Normal_405
  AttacherType = Attacher::AttachEngine3D
  X1 = -54128.2
  X2 = -54128.2
  Y1 = 273499
  Y2 = 272499
  Z1 = 0
  Z2 = 0
FEATURE [Part::Line] Axis_1_405
  AttacherType = Attacher::AttachEngine3D
  X1 = -54128.2
  X2 = -54128.2
  Y1 = 273499
  Y2 = 273499
  Z1 = 0
  Z2 = -1000
FEATURE [Part::Line] Axis_2_405
  AttacherType = Attacher::AttachEngine3D
  X1 = -54128.2
  X2 = -55128.2
  Y1 = 273499
  Y2 = 273499
  Z1 = 0
  Z2 = 0
FEATURE [Part::Feature] Heliostat_406  label="Heliostat_406(Mirror,Axis_1_406,Axis_2_406,Normal_406,Target_point)"
  Placement = pos=(39817,-273691,9.64772e-11) rot=(0,0,1;0rad)
  shape: bbox 10000 x 47.5 x 10000 mm, 1 faces, 0 solids (baked)
FEATURE [Part::Line] Normal_406
  AttacherType = Attacher::AttachEngine3D
  X1 = 39817
  X2 = 39817
  Y1 = 252656
  Y2 = 251656
  Z1 = 0
  Z2 = 0
FEATURE [Part::Line] Axis_1_406
  AttacherType = Attacher::AttachEngine3D
  X1 = 39817
  X2 = 39817
  Y1 = 252656
  Y2 = 252656
  Z1 = 0
  Z2 = -1000
FEATURE [Part::Line] Axis_2_406
  AttacherType = Attacher::AttachEngine3D
  X1 = 39817
  X2 = 38817
  Y1 = 252656
  Y2 = 252656
  Z1 = 0
  Z2 = 0
FEATURE [Part::Feature] Heliostat_407  label="Heliostat_407(Mirror,Axis_1_407,Axis_2_407,Normal_407,Target_point)"
  Placement = pos=(-39817,-273691,9.64772e-11) rot=(0,0,1;0rad)
  shape: bbox 10000 x 47.5 x 10000 mm, 1 faces, 0 solids (baked)
FEATURE [Part::Line] Normal_407
  AttacherType = Attacher::AttachEngine3D
  X1 = -39817
  X2 = -39817
  Y1 = 252656
  Y2 = 251656
  Z1 = 0
  Z2 = 0
FEATURE [Part::Line] Axis_1_407
  AttacherType = Attacher::AttachEngine3D
  X1 = -39817
  X2 = -39817
  Y1 = 252656
  Y2 = 252656
  Z1 = 0
  Z2 = -1000
FEATURE [Part::Line] Axis_2_407
  AttacherType = Attacher::AttachEngine3D
  X1 = -39817
  X2 = -40817
  Y1 = 252656
  Y2 = 252656
  Z1 = 0
  Z2 = 0
FEATURE [Part::Feature] Heliostat_408  label="Heliostat_408(Mirror,Axis_1_408,Axis_2_408,Normal_408,Target_point)"
  Placement = pos=(51222.5,-257710,8.6968e-11) rot=(0,0,1;0rad)
  shape: bbox 10000 x 51.21 x 10000 mm, 1 faces, 0 solids (baked)
FEATURE [Part::Line] Normal_408
  AttacherType = Attacher::AttachEngine3D
  X1 = 51222.5
  X2 = 51222.5
  Y1 = 230470
  Y2 = 229470
  Z1 = 0
  Z2 = 0
FEATURE [Part::Line] Axis_1_408
  AttacherType = Attacher::AttachEngine3D
  X1 = 51222.5
  X2 = 51222.5
  Y1 = 230470
  Y2 = 230470
  Z1 = 0
  Z2 = -1000
FEATURE [Part::Line] Axis_2_408
  AttacherType = Attacher::AttachEngine3D
  X1 = 51222.5
  X2 = 50222.5
  Y1 = 230470
  Y2 = 230470
  Z1 = 0
  Z2 = 0
FEATURE [Part::Feature] Heliostat_409  label="Heliostat_409(Mirror,Axis_1_409,Axis_2_409,Normal_409,Target_point)"
  Placement = pos=(-51222.5,-257710,8.6968e-11) rot=(0,0,1;0rad)
  shape: bbox 10000 x 51.21 x 10000 mm, 1 faces, 0 solids (baked)
FEATURE [Part::Line] Normal_409
  AttacherType = Attacher::AttachEngine3D
  X1 = -51222.5
  X2 = -51222.5
  Y1 = 230470
  Y2 = 229470
  Z1 = 0
  Z2 = 0
FEATURE [Part::Line] Axis_1_409
  AttacherType = Attacher::AttachEngine3D
  X1 = -51222.5
  X2 = -51222.5
  Y1 = 230470
  Y2 = 230470
  Z1 = 0
  Z2 = -1000
FEATURE [Part::Line] Axis_2_409
  AttacherType = Attacher::AttachEngine3D
  X1 = -51222.5
  X2 = -52222.5
  Y1 = 230470
  Y2 = 230470
  Z1 = 0
  Z2 = 0
FEATURE [Part::Feature] Heliostat_410  label="Heliostat_410(Mirror,Axis_1_410,Axis_2_410,Normal_410,Target_point)"
  Placement = pos=(25765.1,-253497,4.94649e-11) rot=(0,0,1;0rad)
  shape: bbox 10000 x 51.21 x 10000 mm, 1 faces, 0 solids (baked)
FEATURE [Part::Line] Normal_410
  AttacherType = Attacher::AttachEngine3D
  X1 = 25765.1
  X2 = 25765.1
  Y1 = 234684
  Y2 = 233684
  Z1 = 0
  Z2 = 0
FEATURE [Part::Line] Axis_1_410
  AttacherType = Attacher::AttachEngine3D
  X1 = 25765.1
  X2 = 25765.1
  Y1 = 234684
  Y2 = 234684
  Z1 = 0
  Z2 = -1000
FEATURE [Part::Line] Axis_2_410
  AttacherType = Attacher::AttachEngine3D
  X1 = 25765.1
  X2 = 24765.1
  Y1 = 234684
  Y2 = 234684
  Z1 = 0
  Z2 = 0
FEATURE [Part::Feature] Heliostat_411  label="Heliostat_411(Mirror,Axis_1_411,Axis_2_411,Normal_411,Target_point)"
  Placement = pos=(-25765.1,-253497,4.94649e-11) rot=(0,0,1;0rad)
  shape: bbox 10000 x 51.21 x 10000 mm, 1 faces, 0 solids (baked)
FEATURE [Part::Line] Normal_411
  AttacherType = Attacher::AttachEngine3D
  X1 = -25765.1
  X2 = -25765.1
  Y1 = 234684
  Y2 = 233684
  Z1 = 0
  Z2 = 0
FEATURE [Part::Line] Axis_1_411
  AttacherType = Attacher::AttachEngine3D
  X1 = -25765.1
  X2 = -25765.1
  Y1 = 234684
  Y2 = 234684
  Z1 = 0
  Z2 = -1000
FEATURE [Part::Line] Axis_2_411
  AttacherType = Attacher::AttachEngine3D
  X1 = -25765.1
  X2 = -26765.1
  Y1 = 234684
  Y2 = 234684
  Z1 = 0
  Z2 = 0
FEATURE [Part::Feature] Heliostat_412  label="Heliostat_412(Mirror,Axis_1_412,Axis_2_412,Normal_412,Target_point)"
  Placement = pos=(58427.1,-241843,1.03206e-10) rot=(0,0,1;0rad)
  shape: bbox 10000 x 55.53 x 10000 mm, 1 faces, 0 solids (baked)
FEATURE [Part::Line] Normal_412
  AttacherType = Attacher::AttachEngine3D
  X1 = 58427.1
  X2 = 58427.1
  Y1 = 208377
  Y2 = 207377
  Z1 = 0
  Z2 = 0
FEATURE [Part::Line] Axis_1_412
  AttacherType = Attacher::AttachEngine3D
  X1 = 58427.1
  X2 = 58427.1
  Y1 = 208377
  Y2 = 208377
  Z1 = 0
  Z2 = -1000
FEATURE [Part::Line] Axis_2_412
  AttacherType = Attacher::AttachEngine3D
  X1 = 58427.1
  X2 = 57427.1
  Y1 = 208377
  Y2 = 208377
  Z1 = 0
  Z2 = 0
FEATURE [Part::Feature] Heliostat_413  label="Heliostat_413(Mirror,Axis_1_413,Axis_2_413,Normal_413,Target_point)"
  Placement = pos=(-58427.1,-241843,1.03206e-10) rot=(0,0,1;0rad)
  shape: bbox 10000 x 55.53 x 10000 mm, 1 faces, 0 solids (baked)
FEATURE [Part::Line] Normal_413
  AttacherType = Attacher::AttachEngine3D
  X1 = -58427.1
  X2 = -58427.1
  Y1 = 208377
  Y2 = 207377
  Z1 = 0
  Z2 = 0
FEATURE [Part::Line] Axis_1_413
  AttacherType = Attacher::AttachEngine3D
  X1 = -58427.1
  X2 = -58427.1
  Y1 = 208377
  Y2 = 208377
  Z1 = 0
  Z2 = -1000
FEATURE [Part::Line] Axis_2_413
  AttacherType = Attacher::AttachEngine3D
  X1 = -58427.1
  X2 = -59427.1
  Y1 = 208377
  Y2 = 208377
  Z1 = 0
  Z2 = 0
FEATURE [Part::Feature] Heliostat_414  label="Heliostat_414(Mirror,Axis_1_414,Axis_2_414,Normal_414,Target_point)"
  Placement = pos=(2.65487e-10,-252087,4.65955e-11) rot=(0,0,1;0rad)
  shape: bbox 10000 x 51.21 x 10000 mm, 1 faces, 0 solids (baked)
FEATURE [Part::Line] Normal_414
  AttacherType = Attacher::AttachEngine3D
  X1 = 0
  X2 = 0
  Y1 = 236094
  Y2 = 235094
  Z1 = 0
  Z2 = 0
FEATURE [Part::Line] Axis_1_414
  AttacherType = Attacher::AttachEngine3D
  X1 = 0
  X2 = 0
  Y1 = 236094
  Y2 = 236094
  Z1 = 0
  Z2 = -1000
FEATURE [Part::Line] Axis_2_414
  AttacherType = Attacher::AttachEngine3D
  X1 = 0
  X2 = -1000
  Y1 = 236094
  Y2 = 236094
  Z1 = 0
  Z2 = 0
FEATURE [Part::Feature] Heliostat_415  label="Heliostat_415(Mirror,Axis_1_415,Axis_2_415,Normal_415,Target_point)"
  Placement = pos=(55616,-149232,4.54403e-11) rot=(0,0,1;0rad)
  shape: bbox 10000 x 144.2 x 10000 mm, 1 faces, 0 solids (baked)
FEATURE [Part::Line] Normal_415
  AttacherType = Attacher::AttachEngine3D
  X1 = 55616
  X2 = 55616
  Y1 = 24172.9
  Y2 = 23172.9
  Z1 = 0
  Z2 = 0
FEATURE [Part::Line] Axis_1_415
  AttacherType = Attacher::AttachEngine3D
  X1 = 55616
  X2 = 55616
  Y1 = 24172.9
  Y2 = 24172.9
  Z1 = 0
  Z2 = -1000
FEATURE [Part::Line] Axis_2_415
  AttacherType = Attacher::AttachEngine3D
  X1 = 55616
  X2 = 54616
  Y1 = 24172.9
  Y2 = 24172.9
  Z1 = 0
  Z2 = 0
FEATURE [Part::Feature] Heliostat_416  label="Heliostat_416(Mirror,Axis_1_416,Axis_2_416,Normal_416,Target_point)"
  Placement = pos=(-55616,-149232,4.54403e-11) rot=(0,0,1;0rad)
  shape: bbox 10000 x 144.2 x 10000 mm, 1 faces, 0 solids (baked)
FEATURE [Part::Line] Normal_416
  AttacherType = Attacher::AttachEngine3D
  X1 = -55616
  X2 = -55616
  Y1 = 24172.9
  Y2 = 23172.9
  Z1 = 0
  Z2 = 0
FEATURE [Part::Line] Axis_1_416
  AttacherType = Attacher::AttachEngine3D
  X1 = -55616
  X2 = -55616
  Y1 = 24172.9
  Y2 = 24172.9
  Z1 = 0
  Z2 = -1000
FEATURE [Part::Line] Axis_2_416
  AttacherType = Attacher::AttachEngine3D
  X1 = -55616
  X2 = -56616
  Y1 = 24172.9
  Y2 = 24172.9
  Z1 = 0
  Z2 = 0
FEATURE [Part::Feature] Heliostat_417  label="Heliostat_417(Mirror,Axis_1_417,Axis_2_417,Normal_417,Target_point)"
  Placement = pos=(75316.3,-302776,1.04655e-10) rot=(0,0,1;0rad)
  shape: bbox 10000 x 43.77 x 10000 mm, 1 faces, 0 solids (baked)
FEATURE [Part::Line] Normal_417
  AttacherType = Attacher::AttachEngine3D
  X1 = 75316.3
  X2 = 75316.3
  Y1 = 268438
  Y2 = 267438
  Z1 = 0
  Z2 = 0
FEATURE [Part::Line] Axis_1_417
  AttacherType = Attacher::AttachEngine3D
  X1 = 75316.3
  X2 = 75316.3
  Y1 = 268438
  Y2 = 268438
  Z1 = 0
  Z2 = -1000
FEATURE [Part::Line] Axis_2_417
  AttacherType = Attacher::AttachEngine3D
  X1 = 75316.3
  X2 = 74316.3
  Y1 = 268438
  Y2 = 268438
  Z1 = 0
  Z2 = 0
FEATURE [Part::Feature] Heliostat_418  label="Heliostat_418(Mirror,Axis_1_418,Axis_2_418,Normal_418,Target_point)"
  Placement = pos=(-75316.3,-302776,1.04655e-10) rot=(0,0,1;0rad)
  shape: bbox 10000 x 43.77 x 10000 mm, 1 faces, 0 solids (baked)
FEATURE [Part::Line] Normal_418
  AttacherType = Attacher::AttachEngine3D
  X1 = -75316.3
  X2 = -75316.3
  Y1 = 268438
  Y2 = 267438
  Z1 = 0
  Z2 = 0
FEATURE [Part::Line] Axis_1_418
  AttacherType = Attacher::AttachEngine3D
  X1 = -75316.3
  X2 = -75316.3
  Y1 = 268438
  Y2 = 268438
  Z1 = 0
  Z2 = -1000
FEATURE [Part::Line] Axis_2_418
  AttacherType = Attacher::AttachEngine3D
  X1 = -75316.3
  X2 = -76316.3
  Y1 = 268438
  Y2 = 268438
  Z1 = 0
  Z2 = 0
FEATURE [Part::Feature] Heliostat_419  label="Heliostat_419(Mirror,Axis_1_419,Axis_2_419,Normal_419,Target_point)"
  Placement = pos=(35337.8,-236711,4.47692e-11) rot=(0,0,1;0rad)
  shape: bbox 10000 x 55.53 x 10000 mm, 1 faces, 0 solids (baked)
FEATURE [Part::Line] Normal_419
  AttacherType = Attacher::AttachEngine3D
  X1 = 35337.8
  X2 = 35337.8
  Y1 = 213509
  Y2 = 212509
  Z1 = 0
  Z2 = 0
FEATURE [Part::Line] Axis_1_419
  AttacherType = Attacher::AttachEngine3D
  X1 = 35337.8
  X2 = 35337.8
  Y1 = 213509
  Y2 = 213509
  Z1 = 0
  Z2 = -1000
FEATURE [Part::Line] Axis_2_419
  AttacherType = Attacher::AttachEngine3D
  X1 = 35337.8
  X2 = 34337.8
  Y1 = 213509
  Y2 = 213509
  Z1 = 0
  Z2 = 0
FEATURE [Part::Feature] Heliostat_420  label="Heliostat_420(Mirror,Axis_1_420,Axis_2_420,Normal_420,Target_point)"
  Placement = pos=(-35337.8,-236711,4.47692e-11) rot=(0,0,1;0rad)
  shape: bbox 10000 x 55.53 x 10000 mm, 1 faces, 0 solids (baked)
FEATURE [Part::Line] Normal_420
  AttacherType = Attacher::AttachEngine3D
  X1 = -35337.8
  X2 = -35337.8
  Y1 = 213509
  Y2 = 212509
  Z1 = 0
  Z2 = 0
FEATURE [Part::Line] Axis_1_420
  AttacherType = Attacher::AttachEngine3D
  X1 = -35337.8
  X2 = -35337.8
  Y1 = 213509
  Y2 = 213509
  Z1 = 0
  Z2 = -1000
FEATURE [Part::Line] Axis_2_420
  AttacherType = Attacher::AttachEngine3D
  X1 = -35337.8
  X2 = -36337.8
  Y1 = 213509
  Y2 = 213509
  Z1 = 0
  Z2 = 0
FEATURE [Part::Feature] Heliostat_421  label="Heliostat_421(Mirror,Axis_1_421,Axis_2_421,Normal_421,Target_point)"
  Placement = pos=(48319.5,-156767,7.04612e-11) rot=(0,0,1;0rad)
  shape: bbox 10000 x 95.83 x 10000 mm, 1 faces, 0 solids (baked)
FEATURE [Part::Line] Normal_421
  AttacherType = Attacher::AttachEngine3D
  X1 = 48319.5
  X2 = 48319.5
  Y1 = 104118
  Y2 = 103118
  Z1 = 0
  Z2 = 0
FEATURE [Part::Line] Axis_1_421
  AttacherType = Attacher::AttachEngine3D
  X1 = 48319.5
  X2 = 48319.5
  Y1 = 104118
  Y2 = 104118
  Z1 = 0
  Z2 = -1000
FEATURE [Part::Line] Axis_2_421
  AttacherType = Attacher::AttachEngine3D
  X1 = 48319.5
  X2 = 47319.5
  Y1 = 104118
  Y2 = 104118
  Z1 = 0
  Z2 = 0
FEATURE [Part::Feature] Heliostat_422  label="Heliostat_422(Mirror,Axis_1_422,Axis_2_422,Normal_422,Target_point)"
  Placement = pos=(-48319.5,-156767,7.04612e-11) rot=(0,0,1;0rad)
  shape: bbox 10000 x 95.83 x 10000 mm, 1 faces, 0 solids (baked)
FEATURE [Part::Line] Normal_422
  AttacherType = Attacher::AttachEngine3D
  X1 = -48319.5
  X2 = -48319.5
  Y1 = 104118
  Y2 = 103118
  Z1 = 0
  Z2 = 0
FEATURE [Part::Line] Axis_1_422
  AttacherType = Attacher::AttachEngine3D
  X1 = -48319.5
  X2 = -48319.5
  Y1 = 104118
  Y2 = 104118
  Z1 = 0
  Z2 = -1000
FEATURE [Part::Line] Axis_2_422
  AttacherType = Attacher::AttachEngine3D
  X1 = -48319.5
  X2 = -49319.5
  Y1 = 104118
  Y2 = 104118
  Z1 = 0
  Z2 = 0
FEATURE [Part::Feature] Heliostat_423  label="Heliostat_423(Mirror,Axis_1_423,Axis_2_423,Normal_423,Target_point)"
  Placement = pos=(72244.4,-167569,3.70585e-11) rot=(0,0,1;0rad)
  shape: bbox 10000 x 122.9 x 10000 mm, 1 faces, 0 solids (baked)
FEATURE [Part::Line] Normal_423
  AttacherType = Attacher::AttachEngine3D
  X1 = 72244.4
  X2 = 72244.4
  Y1 = 35831.5
  Y2 = 34831.5
  Z1 = 0
  Z2 = 0
FEATURE [Part::Line] Axis_1_423
  AttacherType = Attacher::AttachEngine3D
  X1 = 72244.4
  X2 = 72244.4
  Y1 = 35831.5
  Y2 = 35831.5
  Z1 = 0
  Z2 = -1000
FEATURE [Part::Line] Axis_2_423
  AttacherType = Attacher::AttachEngine3D
  X1 = 72244.4
  X2 = 71244.4
  Y1 = 35831.5
  Y2 = 35831.5
  Z1 = 0
  Z2 = 0
FEATURE [Part::Feature] Heliostat_424  label="Heliostat_424(Mirror,Axis_1_424,Axis_2_424,Normal_424,Target_point)"
  Placement = pos=(-72244.4,-167569,3.70585e-11) rot=(0,0,1;0rad)
  shape: bbox 10000 x 122.9 x 10000 mm, 1 faces, 0 solids (baked)
FEATURE [Part::Line] Normal_424
  AttacherType = Attacher::AttachEngine3D
  X1 = -72244.4
  X2 = -72244.4
  Y1 = 35831.5
  Y2 = 34831.5
  Z1 = 0
  Z2 = 0
FEATURE [Part::Line] Axis_1_424
  AttacherType = Attacher::AttachEngine3D
  X1 = -72244.4
  X2 = -72244.4
  Y1 = 35831.5
  Y2 = 35831.5
  Z1 = 0
  Z2 = -1000
FEATURE [Part::Line] Axis_2_424
  AttacherType = Attacher::AttachEngine3D
  X1 = -72244.4
  X2 = -73244.4
  Y1 = 35831.5
  Y2 = 35831.5
  Z1 = 0
  Z2 = 0
FEATURE [Part::Feature] Heliostat_425  label="Heliostat_425(Mirror,Axis_1_425,Axis_2_425,Normal_425,Target_point)"
  Placement = pos=(93760,-194670,7.04612e-11) rot=(0,0,1;0rad)
  shape: bbox 10000 x 95.83 x 10000 mm, 1 faces, 0 solids (baked)
FEATURE [Part::Line] Normal_425
  AttacherType = Attacher::AttachEngine3D
  X1 = 93760
  X2 = 93760
  Y1 = 66215.5
  Y2 = 65215.5
  Z1 = 0
  Z2 = 0
FEATURE [Part::Line] Axis_1_425
  AttacherType = Attacher::AttachEngine3D
  X1 = 93760
  X2 = 93760
  Y1 = 66215.5
  Y2 = 66215.5
  Z1 = 0
  Z2 = -1000
FEATURE [Part::Line] Axis_2_425
  AttacherType = Attacher::AttachEngine3D
  X1 = 93760
  X2 = 92760
  Y1 = 66215.5
  Y2 = 66215.5
  Z1 = 0
  Z2 = 0
FEATURE [Part::Feature] Heliostat_426  label="Heliostat_426(Mirror,Axis_1_426,Axis_2_426,Normal_426,Target_point)"
  Placement = pos=(-93760,-194670,7.04612e-11) rot=(0,0,1;0rad)
  shape: bbox 10000 x 95.83 x 10000 mm, 1 faces, 0 solids (baked)
FEATURE [Part::Line] Normal_426
  AttacherType = Attacher::AttachEngine3D
  X1 = -93760
  X2 = -93760
  Y1 = 66215.5
  Y2 = 65215.5
  Z1 = 0
  Z2 = 0
FEATURE [Part::Line] Axis_1_426
  AttacherType = Attacher::AttachEngine3D
  X1 = -93760
  X2 = -93760
  Y1 = 66215.5
  Y2 = 66215.5
  Z1 = 0
  Z2 = -1000
FEATURE [Part::Line] Axis_2_426
  AttacherType = Attacher::AttachEngine3D
  X1 = -93760
  X2 = -94760
  Y1 = 66215.5
  Y2 = 66215.5
  Z1 = 0
  Z2 = 0
FEATURE [Part::Feature] Heliostat_427  label="Heliostat_427(Mirror,Axis_1_427,Axis_2_427,Normal_427,Target_point)"
  Placement = pos=(76611.8,-198274,6.15032e-11) rot=(0,0,1;0rad)
  shape: bbox 10000 x 75.38 x 10000 mm, 1 faces, 0 solids (baked)
FEATURE [Part::Line] Normal_427
  AttacherType = Attacher::AttachEngine3D
  X1 = 76611.8
  X2 = 76611.8
  Y1 = 133371
  Y2 = 132371
  Z1 = 0
  Z2 = 0
FEATURE [Part::Line] Axis_1_427
  AttacherType = Attacher::AttachEngine3D
  X1 = 76611.8
  X2 = 76611.8
  Y1 = 133371
  Y2 = 133371
  Z1 = 0
  Z2 = -1000
FEATURE [Part::Line] Axis_2_427
  AttacherType = Attacher::AttachEngine3D
  X1 = 76611.8
  X2 = 75611.8
  Y1 = 133371
  Y2 = 133371
  Z1 = 0
  Z2 = 0
FEATURE [Part::Feature] Heliostat_428  label="Heliostat_428(Mirror,Axis_1_428,Axis_2_428,Normal_428,Target_point)"
  Placement = pos=(-76611.8,-198274,6.15032e-11) rot=(0,0,1;0rad)
  shape: bbox 10000 x 75.38 x 10000 mm, 1 faces, 0 solids (baked)
FEATURE [Part::Line] Normal_428
  AttacherType = Attacher::AttachEngine3D
  X1 = -76611.8
  X2 = -76611.8
  Y1 = 133371
  Y2 = 132371
  Z1 = 0
  Z2 = 0
FEATURE [Part::Line] Axis_1_428
  AttacherType = Attacher::AttachEngine3D
  X1 = -76611.8
  X2 = -76611.8
  Y1 = 133371
  Y2 = 133371
  Z1 = 0
  Z2 = -1000
FEATURE [Part::Line] Axis_2_428
  AttacherType = Attacher::AttachEngine3D
  X1 = -76611.8
  X2 = -77611.8
  Y1 = 133371
  Y2 = 133371
  Z1 = 0
  Z2 = 0
FEATURE [Part::Feature] Heliostat_429  label="Heliostat_429(Mirror,Axis_1_429,Axis_2_429,Normal_429,Target_point)"
  Placement = pos=(11826.4,-234130,7.3208e-12) rot=(0,0,1;0rad)
  shape: bbox 10000 x 55.53 x 10000 mm, 1 faces, 0 solids (baked)
FEATURE [Part::Line] Normal_429
  AttacherType = Attacher::AttachEngine3D
  X1 = 11826.4
  X2 = 11826.4
  Y1 = 216090
  Y2 = 215090
  Z1 = 0
  Z2 = 0
FEATURE [Part::Line] Axis_1_429
  AttacherType = Attacher::AttachEngine3D
  X1 = 11826.4
  X2 = 11826.4
  Y1 = 216090
  Y2 = 216090
  Z1 = 0
  Z2 = -1000
FEATURE [Part::Line] Axis_2_429
  AttacherType = Attacher::AttachEngine3D
  X1 = 11826.4
  X2 = 10826.4
  Y1 = 216090
  Y2 = 216090
  Z1 = 0
  Z2 = 0
FEATURE [Part::Feature] Heliostat_430  label="Heliostat_430(Mirror,Axis_1_430,Axis_2_430,Normal_430,Target_point)"
  Placement = pos=(-11826.4,-234130,7.3208e-12) rot=(0,0,1;0rad)
  shape: bbox 10000 x 55.53 x 10000 mm, 1 faces, 0 solids (baked)
FEATURE [Part::Line] Normal_430
  AttacherType = Attacher::AttachEngine3D
  X1 = -11826.4
  X2 = -11826.4
  Y1 = 216090
  Y2 = 215090
  Z1 = 0
  Z2 = 0
FEATURE [Part::Line] Axis_1_430
  AttacherType = Attacher::AttachEngine3D
  X1 = -11826.4
  X2 = -11826.4
  Y1 = 216090
  Y2 = 216090
  Z1 = 0
  Z2 = -1000
FEATURE [Part::Line] Axis_2_430
  AttacherType = Attacher::AttachEngine3D
  X1 = -11826.4
  X2 = -12826.4
  Y1 = 216090
  Y2 = 216090
  Z1 = 0
  Z2 = 0
FEATURE [Part::Feature] Heliostat_431  label="Heliostat_431(Mirror,Axis_1_431,Axis_2_431,Normal_431,Target_point)"
  Placement = pos=(70832.3,-205994,3.67341e-11) rot=(0,0,1;0rad)
  shape: bbox 10000 x 69.71 x 10000 mm, 1 faces, 0 solids (baked)
FEATURE [Part::Line] Normal_431
  AttacherType = Attacher::AttachEngine3D
  X1 = 70832.3
  X2 = 70832.3
  Y1 = 152629
  Y2 = 151629
  Z1 = 0
  Z2 = 0
FEATURE [Part::Line] Axis_1_431
  AttacherType = Attacher::AttachEngine3D
  X1 = 70832.3
  X2 = 70832.3
  Y1 = 152629
  Y2 = 152629
  Z1 = 0
  Z2 = -1000
FEATURE [Part::Line] Axis_2_431
  AttacherType = Attacher::AttachEngine3D
  X1 = 70832.3
  X2 = 69832.3
  Y1 = 152629
  Y2 = 152629
  Z1 = 0
  Z2 = 0
FEATURE [Part::Feature] Heliostat_432  label="Heliostat_432(Mirror,Axis_1_432,Axis_2_432,Normal_432,Target_point)"
  Placement = pos=(-70832.3,-205994,3.67341e-11) rot=(0,0,1;0rad)
  shape: bbox 10000 x 69.71 x 10000 mm, 1 faces, 0 solids (baked)
FEATURE [Part::Line] Normal_432
  AttacherType = Attacher::AttachEngine3D
  X1 = -70832.3
  X2 = -70832.3
  Y1 = 152629
  Y2 = 151629
  Z1 = 0
  Z2 = 0
FEATURE [Part::Line] Axis_1_432
  AttacherType = Attacher::AttachEngine3D
  X1 = -70832.3
  X2 = -70832.3
  Y1 = 152629
  Y2 = 152629
  Z1 = 0
  Z2 = -1000
FEATURE [Part::Line] Axis_2_432
  AttacherType = Attacher::AttachEngine3D
  X1 = -70832.3
  X2 = -71832.3
  Y1 = 152629
  Y2 = 152629
  Z1 = 0
  Z2 = 0
FEATURE [Part::Feature] Heliostat_433  label="Heliostat_433(Mirror,Axis_1_433,Axis_2_433,Normal_433,Target_point)"
  Placement = pos=(98459.4,-202857,5.2501e-11) rot=(0,0,1;0rad)
  shape: bbox 10000 x 87.39 x 10000 mm, 1 faces, 0 solids (baked)
FEATURE [Part::Line] Normal_433
  AttacherType = Attacher::AttachEngine3D
  X1 = 98459.4
  X2 = 98459.4
  Y1 = 83233.1
  Y2 = 82233.1
  Z1 = 0
  Z2 = 0
FEATURE [Part::Line] Axis_1_433
  AttacherType = Attacher::AttachEngine3D
  X1 = 98459.4
  X2 = 98459.4
  Y1 = 83233.1
  Y2 = 83233.1
  Z1 = 0
  Z2 = -1000
FEATURE [Part::Line] Axis_2_433
  AttacherType = Attacher::AttachEngine3D
  X1 = 98459.4
  X2 = 97459.4
  Y1 = 83233.1
  Y2 = 83233.1
  Z1 = 0
  Z2 = 0
FEATURE [Part::Feature] Heliostat_434  label="Heliostat_434(Mirror,Axis_1_434,Axis_2_434,Normal_434,Target_point)"
  Placement = pos=(-98459.4,-202857,5.2501e-11) rot=(0,0,1;0rad)
  shape: bbox 10000 x 87.39 x 10000 mm, 1 faces, 0 solids (baked)
FEATURE [Part::Line] Normal_434
  AttacherType = Attacher::AttachEngine3D
  X1 = -98459.4
  X2 = -98459.4
  Y1 = 83233.1
  Y2 = 82233.1
  Z1 = 0
  Z2 = 0
FEATURE [Part::Line] Axis_1_434
  AttacherType = Attacher::AttachEngine3D
  X1 = -98459.4
  X2 = -98459.4
  Y1 = 83233.1
  Y2 = 83233.1
  Z1 = 0
  Z2 = -1000
FEATURE [Part::Line] Axis_2_434
  AttacherType = Attacher::AttachEngine3D
  X1 = -98459.4
  X2 = -99459.4
  Y1 = 83233.1
  Y2 = 83233.1
  Z1 = 0
  Z2 = 0
FEATURE [Part::Feature] Heliostat_435  label="Heliostat_435(Mirror,Axis_1_435,Axis_2_435,Normal_435,Target_point)"
  Placement = pos=(10892.1,-292623,5.24243e-11) rot=(0,0,1;0rad)
  shape: bbox 10000 x 43.77 x 10000 mm, 1 faces, 0 solids (baked)
FEATURE [Part::Line] Normal_435
  AttacherType = Attacher::AttachEngine3D
  X1 = 10892.1
  X2 = 10892.1
  Y1 = 278591
  Y2 = 277591
  Z1 = 0
  Z2 = 0
FEATURE [Part::Line] Axis_1_435
  AttacherType = Attacher::AttachEngine3D
  X1 = 10892.1
  X2 = 10892.1
  Y1 = 278591
  Y2 = 278591
  Z1 = 0
  Z2 = -1000
FEATURE [Part::Line] Axis_2_435
  AttacherType = Attacher::AttachEngine3D
  X1 = 10892.1
  X2 = 9892.05
  Y1 = 278591
  Y2 = 278591
  Z1 = 0
  Z2 = 0
FEATURE [Part::Feature] Heliostat_436  label="Heliostat_436(Mirror,Axis_1_436,Axis_2_436,Normal_436,Target_point)"
  Placement = pos=(-10892.1,-292623,5.24243e-11) rot=(0,0,1;0rad)
  shape: bbox 10000 x 43.77 x 10000 mm, 1 faces, 0 solids (baked)
FEATURE [Part::Line] Normal_436
  AttacherType = Attacher::AttachEngine3D
  X1 = -10892.1
  X2 = -10892.1
  Y1 = 278591
  Y2 = 277591
  Z1 = 0
  Z2 = 0
FEATURE [Part::Line] Axis_1_436
  AttacherType = Attacher::AttachEngine3D
  X1 = -10892.1
  X2 = -10892.1
  Y1 = 278591
  Y2 = 278591
  Z1 = 0
  Z2 = -1000
FEATURE [Part::Line] Axis_2_436
  AttacherType = Attacher::AttachEngine3D
  X1 = -10892.1
  X2 = -11892.1
  Y1 = 278591
  Y2 = 278591
  Z1 = 0
  Z2 = 0
FEATURE [Part::Feature] Heliostat_437  label="Heliostat_437(Mirror,Axis_1_437,Axis_2_437,Normal_437,Target_point)"
  Placement = pos=(103756,-247457,1.27201e-10) rot=(0,0,1;0rad)
  shape: bbox 10000 x 59.82 x 10000 mm, 1 faces, 0 solids (baked)
FEATURE [Part::Line] Normal_437
  AttacherType = Attacher::AttachEngine3D
  X1 = 103756
  X2 = 103756
  Y1 = 170474
  Y2 = 169474
  Z1 = 0
  Z2 = 0
FEATURE [Part::Line] Axis_1_437
  AttacherType = Attacher::AttachEngine3D
  X1 = 103756
  X2 = 103756
  Y1 = 170474
  Y2 = 170474
  Z1 = 0
  Z2 = -1000
FEATURE [Part::Line] Axis_2_437
  AttacherType = Attacher::AttachEngine3D
  X1 = 103756
  X2 = 102756
  Y1 = 170474
  Y2 = 170474
  Z1 = 0
  Z2 = 0
FEATURE [Part::Feature] Heliostat_438  label="Heliostat_438(Mirror,Axis_1_438,Axis_2_438,Normal_438,Target_point)"
  Placement = pos=(-103756,-247457,1.27201e-10) rot=(0,0,1;0rad)
  shape: bbox 10000 x 59.82 x 10000 mm, 1 faces, 0 solids (baked)
FEATURE [Part::Line] Normal_438
  AttacherType = Attacher::AttachEngine3D
  X1 = -103756
  X2 = -103756
  Y1 = 170474
  Y2 = 169474
  Z1 = 0
  Z2 = 0
FEATURE [Part::Line] Axis_1_438
  AttacherType = Attacher::AttachEngine3D
  X1 = -103756
  X2 = -103756
  Y1 = 170474
  Y2 = 170474
  Z1 = 0
  Z2 = -1000
FEATURE [Part::Line] Axis_2_438
  AttacherType = Attacher::AttachEngine3D
  X1 = -103756
  X2 = -104756
  Y1 = 170474
  Y2 = 170474
  Z1 = 0
  Z2 = 0
FEATURE [Part::Feature] Heliostat_439  label="Heliostat_439(Mirror,Axis_1_439,Axis_2_439,Normal_439,Target_point)"
  Placement = pos=(86325.6,-224840,1.21972e-10) rot=(0,0,1;0rad)
  shape: bbox 10000 x 64.79 x 10000 mm, 1 faces, 0 solids (baked)
FEATURE [Part::Line] Normal_439
  AttacherType = Attacher::AttachEngine3D
  X1 = 86325.6
  X2 = 86325.6
  Y1 = 161041
  Y2 = 160041
  Z1 = 0
  Z2 = 0
FEATURE [Part::Line] Axis_1_439
  AttacherType = Attacher::AttachEngine3D
  X1 = 86325.6
  X2 = 86325.6
  Y1 = 161041
  Y2 = 161041
  Z1 = 0
  Z2 = -1000
FEATURE [Part::Line] Axis_2_439
  AttacherType = Attacher::AttachEngine3D
  X1 = 86325.6
  X2 = 85325.6
  Y1 = 161041
  Y2 = 161041
  Z1 = 0
  Z2 = 0
FEATURE [Part::Feature] Heliostat_440  label="Heliostat_440(Mirror,Axis_1_440,Axis_2_440,Normal_440,Target_point)"
  Placement = pos=(-86325.6,-224840,1.21972e-10) rot=(0,0,1;0rad)
  shape: bbox 10000 x 64.79 x 10000 mm, 1 faces, 0 solids (baked)
FEATURE [Part::Line] Normal_440
  AttacherType = Attacher::AttachEngine3D
  X1 = -86325.6
  X2 = -86325.6
  Y1 = 161041
  Y2 = 160041
  Z1 = 0
  Z2 = 0
FEATURE [Part::Line] Axis_1_440
  AttacherType = Attacher::AttachEngine3D
  X1 = -86325.6
  X2 = -86325.6
  Y1 = 161041
  Y2 = 161041
  Z1 = 0
  Z2 = -1000
FEATURE [Part::Line] Axis_2_440
  AttacherType = Attacher::AttachEngine3D
  X1 = -86325.6
  X2 = -87325.6
  Y1 = 161041
  Y2 = 161041
  Z1 = 0
  Z2 = 0
FEATURE [Part::Feature] Heliostat_441  label="Heliostat_441(Mirror,Axis_1_441,Axis_2_441,Normal_441,Target_point)"
  Placement = pos=(80897,-179454,2.73346e-11) rot=(0,0,1;0rad)
  shape: bbox 10000 x 95.83 x 10000 mm, 1 faces, 0 solids (baked)
FEATURE [Part::Line] Normal_441
  AttacherType = Attacher::AttachEngine3D
  X1 = 80897
  X2 = 80897
  Y1 = 81431.6
  Y2 = 80431.6
  Z1 = 0
  Z2 = 0
FEATURE [Part::Line] Axis_1_441
  AttacherType = Attacher::AttachEngine3D
  X1 = 80897
  X2 = 80897
  Y1 = 81431.6
  Y2 = 81431.6
  Z1 = 0
  Z2 = -1000
FEATURE [Part::Line] Axis_2_441
  AttacherType = Attacher::AttachEngine3D
  X1 = 80897
  X2 = 79897
  Y1 = 81431.6
  Y2 = 81431.6
  Z1 = 0
  Z2 = 0
FEATURE [Part::Feature] Heliostat_442  label="Heliostat_442(Mirror,Axis_1_442,Axis_2_442,Normal_442,Target_point)"
  Placement = pos=(-80897,-179454,2.73346e-11) rot=(0,0,1;0rad)
  shape: bbox 10000 x 95.83 x 10000 mm, 1 faces, 0 solids (baked)
FEATURE [Part::Line] Normal_442
  AttacherType = Attacher::AttachEngine3D
  X1 = -80897
  X2 = -80897
  Y1 = 81431.6
  Y2 = 80431.6
  Z1 = 0
  Z2 = 0
FEATURE [Part::Line] Axis_1_442
  AttacherType = Attacher::AttachEngine3D
  X1 = -80897
  X2 = -80897
  Y1 = 81431.6
  Y2 = 81431.6
  Z1 = 0
  Z2 = -1000
FEATURE [Part::Line] Axis_2_442
  AttacherType = Attacher::AttachEngine3D
  X1 = -80897
  X2 = -81897
  Y1 = 81431.6
  Y2 = 81431.6
  Z1 = 0
  Z2 = 0
FEATURE [Part::Feature] Heliostat_443  label="Heliostat_443(Mirror,Axis_1_443,Axis_2_443,Normal_443,Target_point)"
  Placement = pos=(43371.5,-196045,6.51989e-11) rot=(0,0,1;0rad)
  shape: bbox 10000 x 69.71 x 10000 mm, 1 faces, 0 solids (baked)
FEATURE [Part::Line] Normal_443
  AttacherType = Attacher::AttachEngine3D
  X1 = 43371.5
  X2 = 43371.5
  Y1 = 162578
  Y2 = 161578
  Z1 = 0
  Z2 = 0
FEATURE [Part::Line] Axis_1_443
  AttacherType = Attacher::AttachEngine3D
  X1 = 43371.5
  X2 = 43371.5
  Y1 = 162578
  Y2 = 162578
  Z1 = 0
  Z2 = -1000
FEATURE [Part::Line] Axis_2_443
  AttacherType = Attacher::AttachEngine3D
  X1 = 43371.5
  X2 = 42371.5
  Y1 = 162578
  Y2 = 162578
  Z1 = 0
  Z2 = 0
FEATURE [Part::Feature] Heliostat_444  label="Heliostat_444(Mirror,Axis_1_444,Axis_2_444,Normal_444,Target_point)"
  Placement = pos=(-43371.5,-196045,6.51989e-11) rot=(0,0,1;0rad)
  shape: bbox 10000 x 69.71 x 10000 mm, 1 faces, 0 solids (baked)
FEATURE [Part::Line] Normal_444
  AttacherType = Attacher::AttachEngine3D
  X1 = -43371.5
  X2 = -43371.5
  Y1 = 162578
  Y2 = 161578
  Z1 = 0
  Z2 = 0
FEATURE [Part::Line] Axis_1_444
  AttacherType = Attacher::AttachEngine3D
  X1 = -43371.5
  X2 = -43371.5
  Y1 = 162578
  Y2 = 162578
  Z1 = 0
  Z2 = -1000
FEATURE [Part::Line] Axis_2_444
  AttacherType = Attacher::AttachEngine3D
  X1 = -43371.5
  X2 = -44371.5
  Y1 = 162578
  Y2 = 162578
  Z1 = 0
  Z2 = 0
FEATURE [Part::Feature] Heliostat_445  label="Heliostat_445(Mirror,Axis_1_445,Axis_2_445,Normal_445,Target_point)"
  Placement = pos=(52394.1,-187035,6.15032e-11) rot=(0,0,1;0rad)
  shape: bbox 10000 x 75.38 x 10000 mm, 1 faces, 0 solids (baked)
FEATURE [Part::Line] Normal_445
  AttacherType = Attacher::AttachEngine3D
  X1 = 52394.1
  X2 = 52394.1
  Y1 = 144610
  Y2 = 143610
  Z1 = 0
  Z2 = 0
FEATURE [Part::Line] Axis_1_445
  AttacherType = Attacher::AttachEngine3D
  X1 = 52394.1
  X2 = 52394.1
  Y1 = 144610
  Y2 = 144610
  Z1 = 0
  Z2 = -1000
FEATURE [Part::Line] Axis_2_445
  AttacherType = Attacher::AttachEngine3D
  X1 = 52394.1
  X2 = 51394.1
  Y1 = 144610
  Y2 = 144610
  Z1 = 0
  Z2 = 0
FEATURE [Part::Feature] Heliostat_446  label="Heliostat_446(Mirror,Axis_1_446,Axis_2_446,Normal_446,Target_point)"
  Placement = pos=(-52394.1,-187035,6.15032e-11) rot=(0,0,1;0rad)
  shape: bbox 10000 x 75.38 x 10000 mm, 1 faces, 0 solids (baked)
FEATURE [Part::Line] Normal_446
  AttacherType = Attacher::AttachEngine3D
  X1 = -52394.1
  X2 = -52394.1
  Y1 = 144610
  Y2 = 143610
  Z1 = 0
  Z2 = 0
FEATURE [Part::Line] Axis_1_446
  AttacherType = Attacher::AttachEngine3D
  X1 = -52394.1
  X2 = -52394.1
  Y1 = 144610
  Y2 = 144610
  Z1 = 0
  Z2 = -1000
FEATURE [Part::Line] Axis_2_446
  AttacherType = Attacher::AttachEngine3D
  X1 = -52394.1
  X2 = -53394.1
  Y1 = 144610
  Y2 = 144610
  Z1 = 0
  Z2 = 0
FEATURE [Part::Feature] Heliostat_447  label="Heliostat_447(Mirror,Axis_1_447,Axis_2_447,Normal_447,Target_point)"
  Placement = pos=(75629.6,-169636,6.92563e-11) rot=(0,0,1;0rad)
  shape: bbox 10000 x 113.9 x 10000 mm, 1 faces, 0 solids (baked)
FEATURE [Part::Line] Normal_447
  AttacherType = Attacher::AttachEngine3D
  X1 = 75629.6
  X2 = 75629.6
  Y1 = 49961.6
  Y2 = 48961.6
  Z1 = 0
  Z2 = 0
FEATURE [Part::Line] Axis_1_447
  AttacherType = Attacher::AttachEngine3D
  X1 = 75629.6
  X2 = 75629.6
  Y1 = 49961.6
  Y2 = 49961.6
  Z1 = 0
  Z2 = -1000
FEATURE [Part::Line] Axis_2_447
  AttacherType = Attacher::AttachEngine3D
  X1 = 75629.6
  X2 = 74629.6
  Y1 = 49961.6
  Y2 = 49961.6
  Z1 = 0
  Z2 = 0
FEATURE [Part::Feature] Heliostat_448  label="Heliostat_448(Mirror,Axis_1_448,Axis_2_448,Normal_448,Target_point)"
  Placement = pos=(-75629.6,-169636,6.92563e-11) rot=(0,0,1;0rad)
  shape: bbox 10000 x 113.9 x 10000 mm, 1 faces, 0 solids (baked)
FEATURE [Part::Line] Normal_448
  AttacherType = Attacher::AttachEngine3D
  X1 = -75629.6
  X2 = -75629.6
  Y1 = 49961.6
  Y2 = 48961.6
  Z1 = 0
  Z2 = 0
FEATURE [Part::Line] Axis_1_448
  AttacherType = Attacher::AttachEngine3D
  X1 = -75629.6
  X2 = -75629.6
  Y1 = 49961.6
  Y2 = 49961.6
  Z1 = 0
  Z2 = -1000
FEATURE [Part::Line] Axis_2_448
  AttacherType = Attacher::AttachEngine3D
  X1 = -75629.6
  X2 = -76629.6
  Y1 = 49961.6
  Y2 = 49961.6
  Z1 = 0
  Z2 = 0
FEATURE [Part::Feature] Heliostat_449  label="Heliostat_449(Mirror,Axis_1_449,Axis_2_449,Normal_449,Target_point)"
  Placement = pos=(29835.9,-205614,1.05698e-10) rot=(0,0,1;0rad)
  shape: bbox 10000 x 64.79 x 10000 mm, 1 faces, 0 solids (baked)
FEATURE [Part::Line] Normal_449
  AttacherType = Attacher::AttachEngine3D
  X1 = 29835.9
  X2 = 29835.9
  Y1 = 180266
  Y2 = 179266
  Z1 = 0
  Z2 = 0
FEATURE [Part::Line] Axis_1_449
  AttacherType = Attacher::AttachEngine3D
  X1 = 29835.9
  X2 = 29835.9
  Y1 = 180266
  Y2 = 180266
  Z1 = 0
  Z2 = -1000
FEATURE [Part::Line] Axis_2_449
  AttacherType = Attacher::AttachEngine3D
  X1 = 29835.9
  X2 = 28835.9
  Y1 = 180266
  Y2 = 180266
  Z1 = 0
  Z2 = 0
FEATURE [Part::Feature] Heliostat_450  label="Heliostat_450(Mirror,Axis_1_450,Axis_2_450,Normal_450,Target_point)"
  Placement = pos=(-29835.9,-205614,1.05698e-10) rot=(0,0,1;0rad)
  shape: bbox 10000 x 64.79 x 10000 mm, 1 faces, 0 solids (baked)
FEATURE [Part::Line] Normal_450
  AttacherType = Attacher::AttachEngine3D
  X1 = -29835.9
  X2 = -29835.9
  Y1 = 180266
  Y2 = 179266
  Z1 = 0
  Z2 = 0
FEATURE [Part::Line] Axis_1_450
  AttacherType = Attacher::AttachEngine3D
  X1 = -29835.9
  X2 = -29835.9
  Y1 = 180266
  Y2 = 180266
  Z1 = 0
  Z2 = -1000
FEATURE [Part::Line] Axis_2_450
  AttacherType = Attacher::AttachEngine3D
  X1 = -29835.9
  X2 = -30835.9
  Y1 = 180266
  Y2 = 180266
  Z1 = 0
  Z2 = 0
FEATURE [Part::Feature] Heliostat_451  label="Heliostat_451(Mirror,Axis_1_451,Axis_2_451,Normal_451,Target_point)"
  Placement = pos=(21778.8,-219556,4.25141e-11) rot=(0,0,1;0rad)
  shape: bbox 10000 x 59.82 x 10000 mm, 1 faces, 0 solids (baked)
FEATURE [Part::Line] Normal_451
  AttacherType = Attacher::AttachEngine3D
  X1 = 21778.8
  X2 = 21778.8
  Y1 = 198374
  Y2 = 197374
  Z1 = 0
  Z2 = 0
FEATURE [Part::Line] Axis_1_451
  AttacherType = Attacher::AttachEngine3D
  X1 = 21778.8
  X2 = 21778.8
  Y1 = 198374
  Y2 = 198374
  Z1 = 0
  Z2 = -1000
FEATURE [Part::Line] Axis_2_451
  AttacherType = Attacher::AttachEngine3D
  X1 = 21778.8
  X2 = 20778.8
  Y1 = 198374
  Y2 = 198374
  Z1 = 0
  Z2 = 0
FEATURE [Part::Feature] Heliostat_452  label="Heliostat_452(Mirror,Axis_1_452,Axis_2_452,Normal_452,Target_point)"
  Placement = pos=(-21778.8,-219556,4.25141e-11) rot=(0,0,1;0rad)
  shape: bbox 10000 x 59.82 x 10000 mm, 1 faces, 0 solids (baked)
FEATURE [Part::Line] Normal_452
  AttacherType = Attacher::AttachEngine3D
  X1 = -21778.8
  X2 = -21778.8
  Y1 = 198374
  Y2 = 197374
  Z1 = 0
  Z2 = 0
FEATURE [Part::Line] Axis_1_452
  AttacherType = Attacher::AttachEngine3D
  X1 = -21778.8
  X2 = -21778.8
  Y1 = 198374
  Y2 = 198374
  Z1 = 0
  Z2 = -1000
FEATURE [Part::Line] Axis_2_452
  AttacherType = Attacher::AttachEngine3D
  X1 = -21778.8
  X2 = -22778.8
  Y1 = 198374
  Y2 = 198374
  Z1 = 0
  Z2 = 0
FEATURE [Part::Feature] Heliostat_453  label="Heliostat_453(Mirror,Axis_1_453,Axis_2_453,Normal_453,Target_point)"
  Placement = pos=(14603.8,-190994,9.5181e-11) rot=(0,0,1;0rad)
  shape: bbox 10000 x 69.71 x 10000 mm, 1 faces, 0 solids (baked)
FEATURE [Part::Line] Normal_453
  AttacherType = Attacher::AttachEngine3D
  X1 = 14603.8
  X2 = 14603.8
  Y1 = 167629
  Y2 = 166629
  Z1 = 0
  Z2 = 0
FEATURE [Part::Line] Axis_1_453
  AttacherType = Attacher::AttachEngine3D
  X1 = 14603.8
  X2 = 14603.8
  Y1 = 167629
  Y2 = 167629
  Z1 = 0
  Z2 = -1000
FEATURE [Part::Line] Axis_2_453
  AttacherType = Attacher::AttachEngine3D
  X1 = 14603.8
  X2 = 13603.8
  Y1 = 167629
  Y2 = 167629
  Z1 = 0
  Z2 = 0
FEATURE [Part::Feature] Heliostat_454  label="Heliostat_454(Mirror,Axis_1_454,Axis_2_454,Normal_454,Target_point)"
  Placement = pos=(-14603.8,-190994,9.5181e-11) rot=(0,0,1;0rad)
  shape: bbox 10000 x 69.71 x 10000 mm, 1 faces, 0 solids (baked)
FEATURE [Part::Line] Normal_454
  AttacherType = Attacher::AttachEngine3D
  X1 = -14603.8
  X2 = -14603.8
  Y1 = 167629
  Y2 = 166629
  Z1 = 0
  Z2 = 0
FEATURE [Part::Line] Axis_1_454
  AttacherType = Attacher::AttachEngine3D
  X1 = -14603.8
  X2 = -14603.8
  Y1 = 167629
  Y2 = 167629
  Z1 = 0
  Z2 = -1000
FEATURE [Part::Line] Axis_2_454
  AttacherType = Attacher::AttachEngine3D
  X1 = -14603.8
  X2 = -15603.8
  Y1 = 167629
  Y2 = 167629
  Z1 = 0
  Z2 = 0
FEATURE [Part::Feature] Heliostat_455  label="Heliostat_455(Mirror,Axis_1_455,Axis_2_455,Normal_455,Target_point)"
  Placement = pos=(26597.8,-180153,3.36582e-11) rot=(0,0,1;0rad)
  shape: bbox 10000 x 75.38 x 10000 mm, 1 faces, 0 solids (baked)
FEATURE [Part::Line] Normal_455
  AttacherType = Attacher::AttachEngine3D
  X1 = 26597.8
  X2 = 26597.8
  Y1 = 151492
  Y2 = 150492
  Z1 = 0
  Z2 = 0
FEATURE [Part::Line] Axis_1_455
  AttacherType = Attacher::AttachEngine3D
  X1 = 26597.8
  X2 = 26597.8
  Y1 = 151492
  Y2 = 151492
  Z1 = 0
  Z2 = -1000
FEATURE [Part::Line] Axis_2_455
  AttacherType = Attacher::AttachEngine3D
  X1 = 26597.8
  X2 = 25597.8
  Y1 = 151492
  Y2 = 151492
  Z1 = 0
  Z2 = 0
FEATURE [Part::Feature] Heliostat_456  label="Heliostat_456(Mirror,Axis_1_456,Axis_2_456,Normal_456,Target_point)"
  Placement = pos=(-26597.8,-180153,3.36582e-11) rot=(0,0,1;0rad)
  shape: bbox 10000 x 75.38 x 10000 mm, 1 faces, 0 solids (baked)
FEATURE [Part::Line] Normal_456
  AttacherType = Attacher::AttachEngine3D
  X1 = -26597.8
  X2 = -26597.8
  Y1 = 151492
  Y2 = 150492
  Z1 = 0
  Z2 = 0
FEATURE [Part::Line] Axis_1_456
  AttacherType = Attacher::AttachEngine3D
  X1 = -26597.8
  X2 = -26597.8
  Y1 = 151492
  Y2 = 151492
  Z1 = 0
  Z2 = -1000
FEATURE [Part::Line] Axis_2_456
  AttacherType = Attacher::AttachEngine3D
  X1 = -26597.8
  X2 = -27597.8
  Y1 = 151492
  Y2 = 151492
  Z1 = 0
  Z2 = 0
FEATURE [Part::Feature] Heliostat_457  label="Heliostat_457(Mirror,Axis_1_457,Axis_2_457,Normal_457,Target_point)"
  Placement = pos=(-1.9176e-12,-177836,6.16872e-11) rot=(0,0,1;0rad)
  shape: bbox 10000 x 75.38 x 10000 mm, 1 faces, 0 solids (baked)
FEATURE [Part::Line] Normal_457
  AttacherType = Attacher::AttachEngine3D
  X1 = 0
  X2 = 0
  Y1 = 153809
  Y2 = 152809
  Z1 = 0
  Z2 = 0
FEATURE [Part::Line] Axis_1_457
  AttacherType = Attacher::AttachEngine3D
  X1 = 0
  X2 = 0
  Y1 = 153809
  Y2 = 153809
  Z1 = 0
  Z2 = -1000
FEATURE [Part::Line] Axis_2_457
  AttacherType = Attacher::AttachEngine3D
  X1 = 0
  X2 = -1000
  Y1 = 153809
  Y2 = 153809
  Z1 = 0
  Z2 = 0
FEATURE [Part::Feature] Heliostat_458  label="Heliostat_458(Mirror,Axis_1_458,Axis_2_458,Normal_458,Target_point)"
  Placement = pos=(99632.3,-208414,8.37151e-11) rot=(0,0,1;0rad)
  shape: bbox 10000 x 80.99 x 10000 mm, 1 faces, 0 solids (baked)
FEATURE [Part::Line] Normal_458
  AttacherType = Attacher::AttachEngine3D
  X1 = 99632.3
  X2 = 99632.3
  Y1 = 100291
  Y2 = 99290.7
  Z1 = 0
  Z2 = 0
FEATURE [Part::Line] Axis_1_458
  AttacherType = Attacher::AttachEngine3D
  X1 = 99632.3
  X2 = 99632.3
  Y1 = 100291
  Y2 = 100291
  Z1 = 0
  Z2 = -1000
FEATURE [Part::Line] Axis_2_458
  AttacherType = Attacher::AttachEngine3D
  X1 = 99632.3
  X2 = 98632.3
  Y1 = 100291
  Y2 = 100291
  Z1 = 0
  Z2 = 0
FEATURE [Part::Feature] Heliostat_459  label="Heliostat_459(Mirror,Axis_1_459,Axis_2_459,Normal_459,Target_point)"
  Placement = pos=(-99632.3,-208414,8.37151e-11) rot=(0,0,1;0rad)
  shape: bbox 10000 x 80.99 x 10000 mm, 1 faces, 0 solids (baked)
FEATURE [Part::Line] Normal_459
  AttacherType = Attacher::AttachEngine3D
  X1 = -99632.3
  X2 = -99632.3
  Y1 = 100291
  Y2 = 99290.7
  Z1 = 0
  Z2 = 0
FEATURE [Part::Line] Axis_1_459
  AttacherType = Attacher::AttachEngine3D
  X1 = -99632.3
  X2 = -99632.3
  Y1 = 100291
  Y2 = 100291
  Z1 = 0
  Z2 = -1000
FEATURE [Part::Line] Axis_2_459
  AttacherType = Attacher::AttachEngine3D
  X1 = -99632.3
  X2 = -100632
  Y1 = 100291
  Y2 = 100291
  Z1 = 0
  Z2 = 0
FEATURE [Part::Feature] Heliostat_460  label="Heliostat_460(Mirror,Axis_1_460,Axis_2_460,Normal_460,Target_point)"
  Placement = pos=(64299,-229006,4.25141e-11) rot=(0,0,1;0rad)
  shape: bbox 10000 x 59.82 x 10000 mm, 1 faces, 0 solids (baked)
FEATURE [Part::Line] Normal_460
  AttacherType = Attacher::AttachEngine3D
  X1 = 64299
  X2 = 64299
  Y1 = 188924
  Y2 = 187924
  Z1 = 0
  Z2 = 0
FEATURE [Part::Line] Axis_1_460
  AttacherType = Attacher::AttachEngine3D
  X1 = 64299
  X2 = 64299
  Y1 = 188924
  Y2 = 188924
  Z1 = 0
  Z2 = -1000
FEATURE [Part::Line] Axis_2_460
  AttacherType = Attacher::AttachEngine3D
  X1 = 64299
  X2 = 63299
  Y1 = 188924
  Y2 = 188924
  Z1 = 0
  Z2 = 0
FEATURE [Part::Feature] Heliostat_461  label="Heliostat_461(Mirror,Axis_1_461,Axis_2_461,Normal_461,Target_point)"
  Placement = pos=(-64299,-229006,4.25141e-11) rot=(0,0,1;0rad)
  shape: bbox 10000 x 59.82 x 10000 mm, 1 faces, 0 solids (baked)
FEATURE [Part::Line] Normal_461
  AttacherType = Attacher::AttachEngine3D
  X1 = -64299
  X2 = -64299
  Y1 = 188924
  Y2 = 187924
  Z1 = 0
  Z2 = 0
FEATURE [Part::Line] Axis_1_461
  AttacherType = Attacher::AttachEngine3D
  X1 = -64299
  X2 = -64299
  Y1 = 188924
  Y2 = 188924
  Z1 = 0
  Z2 = -1000
FEATURE [Part::Line] Axis_2_461
  AttacherType = Attacher::AttachEngine3D
  X1 = -64299
  X2 = -65299
  Y1 = 188924
  Y2 = 188924
  Z1 = 0
  Z2 = 0
FEATURE [Part::Feature] Heliostat_462  label="Heliostat_462(Mirror,Axis_1_462,Axis_2_462,Normal_462,Target_point)"
  Placement = pos=(43297.5,-223118,7.61215e-11) rot=(0,0,1;0rad)
  shape: bbox 10000 x 59.82 x 10000 mm, 1 faces, 0 solids (baked)
FEATURE [Part::Line] Normal_462
  AttacherType = Attacher::AttachEngine3D
  X1 = 43297.5
  X2 = 43297.5
  Y1 = 194813
  Y2 = 193813
  Z1 = 0
  Z2 = 0
FEATURE [Part::Line] Axis_1_462
  AttacherType = Attacher::AttachEngine3D
  X1 = 43297.5
  X2 = 43297.5
  Y1 = 194813
  Y2 = 194813
  Z1 = 0
  Z2 = -1000
FEATURE [Part::Line] Axis_2_462
  AttacherType = Attacher::AttachEngine3D
  X1 = 43297.5
  X2 = 42297.5
  Y1 = 194813
  Y2 = 194813
  Z1 = 0
  Z2 = 0
FEATURE [Part::Feature] Heliostat_463  label="Heliostat_463(Mirror,Axis_1_463,Axis_2_463,Normal_463,Target_point)"
  Placement = pos=(-43297.5,-223118,7.61215e-11) rot=(0,0,1;0rad)
  shape: bbox 10000 x 59.82 x 10000 mm, 1 faces, 0 solids (baked)
FEATURE [Part::Line] Normal_463
  AttacherType = Attacher::AttachEngine3D
  X1 = -43297.5
  X2 = -43297.5
  Y1 = 194813
  Y2 = 193813
  Z1 = 0
  Z2 = 0
FEATURE [Part::Line] Axis_1_463
  AttacherType = Attacher::AttachEngine3D
  X1 = -43297.5
  X2 = -43297.5
  Y1 = 194813
  Y2 = 194813
  Z1 = 0
  Z2 = -1000
FEATURE [Part::Line] Axis_2_463
  AttacherType = Attacher::AttachEngine3D
  X1 = -43297.5
  X2 = -44297.5
  Y1 = 194813
  Y2 = 194813
  Z1 = 0
  Z2 = 0
FEATURE [Part::Feature] Heliostat_464  label="Heliostat_464(Mirror,Axis_1_464,Axis_2_464,Normal_464,Target_point)"
  Placement = pos=(82582.8,-187084,1.68398e-11) rot=(0,0,1;0rad)
  shape: bbox 10000 x 87.39 x 10000 mm, 1 faces, 0 solids (baked)
FEATURE [Part::Line] Normal_464
  AttacherType = Attacher::AttachEngine3D
  X1 = 82582.8
  X2 = 82582.8
  Y1 = 99005.5
  Y2 = 98005.5
  Z1 = 0
  Z2 = 0
FEATURE [Part::Line] Axis_1_464
  AttacherType = Attacher::AttachEngine3D
  X1 = 82582.8
  X2 = 82582.8
  Y1 = 99005.5
  Y2 = 99005.5
  Z1 = 0
  Z2 = -1000
FEATURE [Part::Line] Axis_2_464
  AttacherType = Attacher::AttachEngine3D
  X1 = 82582.8
  X2 = 81582.8
  Y1 = 99005.5
  Y2 = 99005.5
  Z1 = 0
  Z2 = 0
FEATURE [Part::Feature] Heliostat_465  label="Heliostat_465(Mirror,Axis_1_465,Axis_2_465,Normal_465,Target_point)"
  Placement = pos=(-82582.8,-187084,1.68398e-11) rot=(0,0,1;0rad)
  shape: bbox 10000 x 87.39 x 10000 mm, 1 faces, 0 solids (baked)
FEATURE [Part::Line] Normal_465
  AttacherType = Attacher::AttachEngine3D
  X1 = -82582.8
  X2 = -82582.8
  Y1 = 99005.5
  Y2 = 98005.5
  Z1 = 0
  Z2 = 0
FEATURE [Part::Line] Axis_1_465
  AttacherType = Attacher::AttachEngine3D
  X1 = -82582.8
  X2 = -82582.8
  Y1 = 99005.5
  Y2 = 99005.5
  Z1 = 0
  Z2 = -1000
FEATURE [Part::Line] Axis_2_465
  AttacherType = Attacher::AttachEngine3D
  X1 = -82582.8
  X2 = -83582.8
  Y1 = 99005.5
  Y2 = 99005.5
  Z1 = 0
  Z2 = 0
FEATURE [Part::Feature] Heliostat_466  label="Heliostat_466(Mirror,Axis_1_466,Axis_2_466,Normal_466,Target_point)"
  Placement = pos=(3.5974e-10,-218364,2.08967e-11) rot=(0,0,1;0rad)
  shape: bbox 10000 x 59.82 x 10000 mm, 1 faces, 0 solids (baked)
FEATURE [Part::Line] Normal_466
  AttacherType = Attacher::AttachEngine3D
  X1 = 0
  X2 = 0
  Y1 = 199566
  Y2 = 198566
  Z1 = 0
  Z2 = 0
FEATURE [Part::Line] Axis_1_466
  AttacherType = Attacher::AttachEngine3D
  X1 = 0
  X2 = 0
  Y1 = 199566
  Y2 = 199566
  Z1 = 0
  Z2 = -1000
FEATURE [Part::Line] Axis_2_466
  AttacherType = Attacher::AttachEngine3D
  X1 = 0
  X2 = -1000
  Y1 = 199566
  Y2 = 199566
  Z1 = 0
  Z2 = 0
FEATURE [Part::Feature] Heliostat_467  label="Heliostat_467(Mirror,Axis_1_467,Axis_2_467,Normal_467,Target_point)"
  Placement = pos=(76508.3,-170992,6.30254e-11) rot=(0,0,1;0rad)
  shape: bbox 10000 x 105.8 x 10000 mm, 1 faces, 0 solids (baked)
FEATURE [Part::Line] Normal_467
  AttacherType = Attacher::AttachEngine3D
  X1 = 76508.3
  X2 = 76508.3
  Y1 = 65385.9
  Y2 = 64385.9
  Z1 = 0
  Z2 = 0
FEATURE [Part::Line] Axis_1_467
  AttacherType = Attacher::AttachEngine3D
  X1 = 76508.3
  X2 = 76508.3
  Y1 = 65385.9
  Y2 = 65385.9
  Z1 = 0
  Z2 = -1000
FEATURE [Part::Line] Axis_2_467
  AttacherType = Attacher::AttachEngine3D
  X1 = 76508.3
  X2 = 75508.3
  Y1 = 65385.9
  Y2 = 65385.9
  Z1 = 0
  Z2 = 0
FEATURE [Part::Feature] Heliostat_468  label="Heliostat_468(Mirror,Axis_1_468,Axis_2_468,Normal_468,Target_point)"
  Placement = pos=(-76508.3,-170992,6.30254e-11) rot=(0,0,1;0rad)
  shape: bbox 10000 x 105.8 x 10000 mm, 1 faces, 0 solids (baked)
FEATURE [Part::Line] Normal_468
  AttacherType = Attacher::AttachEngine3D
  X1 = -76508.3
  X2 = -76508.3
  Y1 = 65385.9
  Y2 = 64385.9
  Z1 = 0
  Z2 = 0
FEATURE [Part::Line] Axis_1_468
  AttacherType = Attacher::AttachEngine3D
  X1 = -76508.3
  X2 = -76508.3
  Y1 = 65385.9
  Y2 = 65385.9
  Z1 = 0
  Z2 = -1000
FEATURE [Part::Line] Axis_2_468
  AttacherType = Attacher::AttachEngine3D
  X1 = -76508.3
  X2 = -77508.3
  Y1 = 65385.9
  Y2 = 65385.9
  Z1 = 0
  Z2 = 0
FEATURE [Part::Feature] Heliostat_469  label="Heliostat_469(Mirror,Axis_1_469,Axis_2_469,Normal_469,Target_point)"
  Placement = pos=(80788.3,-192696,4.03801e-11) rot=(0,0,1;0rad)
  shape: bbox 10000 x 80.99 x 10000 mm, 1 faces, 0 solids (baked)
FEATURE [Part::Line] Normal_469
  AttacherType = Attacher::AttachEngine3D
  X1 = 80788.3
  X2 = 80788.3
  Y1 = 116009
  Y2 = 115009
  Z1 = 0
  Z2 = 0
FEATURE [Part::Line] Axis_1_469
  AttacherType = Attacher::AttachEngine3D
  X1 = 80788.3
  X2 = 80788.3
  Y1 = 116009
  Y2 = 116009
  Z1 = 0
  Z2 = -1000
FEATURE [Part::Line] Axis_2_469
  AttacherType = Attacher::AttachEngine3D
  X1 = 80788.3
  X2 = 79788.3
  Y1 = 116009
  Y2 = 116009
  Z1 = 0
  Z2 = 0
FEATURE [Part::Feature] Heliostat_470  label="Heliostat_470(Mirror,Axis_1_470,Axis_2_470,Normal_470,Target_point)"
  Placement = pos=(-80788.3,-192696,4.03801e-11) rot=(0,0,1;0rad)
  shape: bbox 10000 x 80.99 x 10000 mm, 1 faces, 0 solids (baked)
FEATURE [Part::Line] Normal_470
  AttacherType = Attacher::AttachEngine3D
  X1 = -80788.3
  X2 = -80788.3
  Y1 = 116009
  Y2 = 115009
  Z1 = 0
  Z2 = 0
FEATURE [Part::Line] Axis_1_470
  AttacherType = Attacher::AttachEngine3D
  X1 = -80788.3
  X2 = -80788.3
  Y1 = 116009
  Y2 = 116009
  Z1 = 0
  Z2 = -1000
FEATURE [Part::Line] Axis_2_470
  AttacherType = Attacher::AttachEngine3D
  X1 = -80788.3
  X2 = -81788.3
  Y1 = 116009
  Y2 = 116009
  Z1 = 0
  Z2 = 0
FEATURE [Part::Feature] Heliostat_471  label="Heliostat_471(Mirror,Axis_1_471,Axis_2_471,Normal_471,Target_point)"
  Placement = pos=(64217.9,-174295,2.6439e-12) rot=(0,0,1;0rad)
  shape: bbox 10000 x 87.39 x 10000 mm, 1 faces, 0 solids (baked)
FEATURE [Part::Line] Normal_471
  AttacherType = Attacher::AttachEngine3D
  X1 = 64217.9
  X2 = 64217.9
  Y1 = 111795
  Y2 = 110795
  Z1 = 0
  Z2 = 0
FEATURE [Part::Line] Axis_1_471
  AttacherType = Attacher::AttachEngine3D
  X1 = 64217.9
  X2 = 64217.9
  Y1 = 111795
  Y2 = 111795
  Z1 = 0
  Z2 = -1000
FEATURE [Part::Line] Axis_2_471
  AttacherType = Attacher::AttachEngine3D
  X1 = 64217.9
  X2 = 63217.9
  Y1 = 111795
  Y2 = 111795
  Z1 = 0
  Z2 = 0
FEATURE [Part::Feature] Heliostat_472  label="Heliostat_472(Mirror,Axis_1_472,Axis_2_472,Normal_472,Target_point)"
  Placement = pos=(-64217.9,-174295,2.6439e-12) rot=(0,0,1;0rad)
  shape: bbox 10000 x 87.39 x 10000 mm, 1 faces, 0 solids (baked)
FEATURE [Part::Line] Normal_472
  AttacherType = Attacher::AttachEngine3D
  X1 = -64217.9
  X2 = -64217.9
  Y1 = 111795
  Y2 = 110795
  Z1 = 0
  Z2 = 0
FEATURE [Part::Line] Axis_1_472
  AttacherType = Attacher::AttachEngine3D
  X1 = -64217.9
  X2 = -64217.9
  Y1 = 111795
  Y2 = 111795
  Z1 = 0
  Z2 = -1000
FEATURE [Part::Line] Axis_2_472
  AttacherType = Attacher::AttachEngine3D
  X1 = -64217.9
  X2 = -65217.9
  Y1 = 111795
  Y2 = 111795
  Z1 = 0
  Z2 = 0
FEATURE [Part::Feature] Heliostat_473  label="Heliostat_473(Mirror,Axis_1_473,Axis_2_473,Normal_473,Target_point)"
  Placement = pos=(61135.6,-152677,2.29336e-11) rot=(0,0,1;0rad)
  shape: bbox 10000 x 113.9 x 10000 mm, 1 faces, 0 solids (baked)
FEATURE [Part::Line] Normal_473
  AttacherType = Attacher::AttachEngine3D
  X1 = 61135.6
  X2 = 61135.6
  Y1 = 66921.1
  Y2 = 65921.1
  Z1 = 0
  Z2 = 0
FEATURE [Part::Line] Axis_1_473
  AttacherType = Attacher::AttachEngine3D
  X1 = 61135.6
  X2 = 61135.6
  Y1 = 66921.1
  Y2 = 66921.1
  Z1 = 0
  Z2 = -1000
FEATURE [Part::Line] Axis_2_473
  AttacherType = Attacher::AttachEngine3D
  X1 = 61135.6
  X2 = 60135.6
  Y1 = 66921.1
  Y2 = 66921.1
  Z1 = 0
  Z2 = 0
FEATURE [Part::Feature] Heliostat_474  label="Heliostat_474(Mirror,Axis_1_474,Axis_2_474,Normal_474,Target_point)"
  Placement = pos=(-61135.6,-152677,2.29336e-11) rot=(0,0,1;0rad)
  shape: bbox 10000 x 113.9 x 10000 mm, 1 faces, 0 solids (baked)
FEATURE [Part::Line] Normal_474
  AttacherType = Attacher::AttachEngine3D
  X1 = -61135.6
  X2 = -61135.6
  Y1 = 66921.1
  Y2 = 65921.1
  Z1 = 0
  Z2 = 0
FEATURE [Part::Line] Axis_1_474
  AttacherType = Attacher::AttachEngine3D
  X1 = -61135.6
  X2 = -61135.6
  Y1 = 66921.1
  Y2 = 66921.1
  Z1 = 0
  Z2 = -1000
FEATURE [Part::Line] Axis_2_474
  AttacherType = Attacher::AttachEngine3D
  X1 = -61135.6
  X2 = -62135.6
  Y1 = 66921.1
  Y2 = 66921.1
  Z1 = 0
  Z2 = 0
FEATURE [Part::Feature] Heliostat_475  label="Heliostat_475(Mirror,Axis_1_475,Axis_2_475,Normal_475,Target_point)"
  Placement = pos=(43918.1,-164874,1.68398e-11) rot=(0,0,1;0rad)
  shape: bbox 10000 x 87.39 x 10000 mm, 1 faces, 0 solids (baked)
FEATURE [Part::Line] Normal_475
  AttacherType = Attacher::AttachEngine3D
  X1 = 43918.1
  X2 = 43918.1
  Y1 = 121216
  Y2 = 120216
  Z1 = 0
  Z2 = 0
FEATURE [Part::Line] Axis_1_475
  AttacherType = Attacher::AttachEngine3D
  X1 = 43918.1
  X2 = 43918.1
  Y1 = 121216
  Y2 = 121216
  Z1 = 0
  Z2 = -1000
FEATURE [Part::Line] Axis_2_475
  AttacherType = Attacher::AttachEngine3D
  X1 = 43918.1
  X2 = 42918.1
  Y1 = 121216
  Y2 = 121216
  Z1 = 0
  Z2 = 0
FEATURE [Part::Feature] Heliostat_476  label="Heliostat_476(Mirror,Axis_1_476,Axis_2_476,Normal_476,Target_point)"
  Placement = pos=(-43918.1,-164874,1.68398e-11) rot=(0,0,1;0rad)
  shape: bbox 10000 x 87.39 x 10000 mm, 1 faces, 0 solids (baked)
FEATURE [Part::Line] Normal_476
  AttacherType = Attacher::AttachEngine3D
  X1 = -43918.1
  X2 = -43918.1
  Y1 = 121216
  Y2 = 120216
  Z1 = 0
  Z2 = 0
FEATURE [Part::Line] Axis_1_476
  AttacherType = Attacher::AttachEngine3D
  X1 = -43918.1
  X2 = -43918.1
  Y1 = 121216
  Y2 = 121216
  Z1 = 0
  Z2 = -1000
FEATURE [Part::Line] Axis_2_476
  AttacherType = Attacher::AttachEngine3D
  X1 = -43918.1
  X2 = -44918.1
  Y1 = 121216
  Y2 = 121216
  Z1 = 0
  Z2 = 0
FEATURE [Part::Feature] Heliostat_477  label="Heliostat_477(Mirror,Axis_1_477,Axis_2_477,Normal_477,Target_point)"
  Placement = pos=(59510,-180473,5.59109e-11) rot=(0,0,1;0rad)
  shape: bbox 10000 x 80.99 x 10000 mm, 1 faces, 0 solids (baked)
FEATURE [Part::Line] Normal_477
  AttacherType = Attacher::AttachEngine3D
  X1 = 59510
  X2 = 59510
  Y1 = 128232
  Y2 = 127232
  Z1 = 0
  Z2 = 0
FEATURE [Part::Line] Axis_1_477
  AttacherType = Attacher::AttachEngine3D
  X1 = 59510
  X2 = 59510
  Y1 = 128232
  Y2 = 128232
  Z1 = 0
  Z2 = -1000
FEATURE [Part::Line] Axis_2_477
  AttacherType = Attacher::AttachEngine3D
  X1 = 59510
  X2 = 58510
  Y1 = 128232
  Y2 = 128232
  Z1 = 0
  Z2 = 0
FEATURE [Part::Feature] Heliostat_478  label="Heliostat_478(Mirror,Axis_1_478,Axis_2_478,Normal_478,Target_point)"
  Placement = pos=(-59510,-180473,5.59109e-11) rot=(0,0,1;0rad)
  shape: bbox 10000 x 80.99 x 10000 mm, 1 faces, 0 solids (baked)
FEATURE [Part::Line] Normal_478
  AttacherType = Attacher::AttachEngine3D
  X1 = -59510
  X2 = -59510
  Y1 = 128232
  Y2 = 127232
  Z1 = 0
  Z2 = 0
FEATURE [Part::Line] Axis_1_478
  AttacherType = Attacher::AttachEngine3D
  X1 = -59510
  X2 = -59510
  Y1 = 128232
  Y2 = 128232
  Z1 = 0
  Z2 = -1000
FEATURE [Part::Line] Axis_2_478
  AttacherType = Attacher::AttachEngine3D
  X1 = -59510
  X2 = -60510
  Y1 = 128232
  Y2 = 128232
  Z1 = 0
  Z2 = 0
FEATURE [Part::Feature] Heliostat_479  label="Heliostat_479(Mirror,Axis_1_479,Axis_2_479,Normal_479,Target_point)"
  Placement = pos=(61304.3,-151009,3.64263e-11) rot=(0,0,1;0rad)
  shape: bbox 10000 x 122.9 x 10000 mm, 1 faces, 0 solids (baked)
FEATURE [Part::Line] Normal_479
  AttacherType = Attacher::AttachEngine3D
  X1 = 61304.3
  X2 = 61304.3
  Y1 = 52392.1
  Y2 = 51392.1
  Z1 = 0
  Z2 = 0
FEATURE [Part::Line] Axis_1_479
  AttacherType = Attacher::AttachEngine3D
  X1 = 61304.3
  X2 = 61304.3
  Y1 = 52392.1
  Y2 = 52392.1
  Z1 = 0
  Z2 = -1000
FEATURE [Part::Line] Axis_2_479
  AttacherType = Attacher::AttachEngine3D
  X1 = 61304.3
  X2 = 60304.3
  Y1 = 52392.1
  Y2 = 52392.1
  Z1 = 0
  Z2 = 0
FEATURE [Part::Feature] Heliostat_480  label="Heliostat_480(Mirror,Axis_1_480,Axis_2_480,Normal_480,Target_point)"
  Placement = pos=(-61304.3,-151009,3.64263e-11) rot=(0,0,1;0rad)
  shape: bbox 10000 x 122.9 x 10000 mm, 1 faces, 0 solids (baked)
FEATURE [Part::Line] Normal_480
  AttacherType = Attacher::AttachEngine3D
  X1 = -61304.3
  X2 = -61304.3
  Y1 = 52392.1
  Y2 = 51392.1
  Z1 = 0
  Z2 = 0
FEATURE [Part::Line] Axis_1_480
  AttacherType = Attacher::AttachEngine3D
  X1 = -61304.3
  X2 = -61304.3
  Y1 = 52392.1
  Y2 = 52392.1
  Z1 = 0
  Z2 = -1000
FEATURE [Part::Line] Axis_2_480
  AttacherType = Attacher::AttachEngine3D
  X1 = -61304.3
  X2 = -62304.3
  Y1 = 52392.1
  Y2 = 52392.1
  Z1 = 0
  Z2 = 0
FEATURE [Part::Feature] Heliostat_481  label="Heliostat_481(Mirror,Axis_1_481,Axis_2_481,Normal_481,Target_point)"
  Placement = pos=(48562.3,-137084,3.16914e-11) rot=(0,0,1;0rad)
  shape: bbox 10000 x 144.2 x 10000 mm, 1 faces, 0 solids (baked)
FEATURE [Part::Line] Normal_481
  AttacherType = Attacher::AttachEngine3D
  X1 = 48562.3
  X2 = 48562.3
  Y1 = 36320.4
  Y2 = 35320.4
  Z1 = 0
  Z2 = 0
FEATURE [Part::Line] Axis_1_481
  AttacherType = Attacher::AttachEngine3D
  X1 = 48562.3
  X2 = 48562.3
  Y1 = 36320.4
  Y2 = 36320.4
  Z1 = 0
  Z2 = -1000
FEATURE [Part::Line] Axis_2_481
  AttacherType = Attacher::AttachEngine3D
  X1 = 48562.3
  X2 = 47562.3
  Y1 = 36320.4
  Y2 = 36320.4
  Z1 = 0
  Z2 = 0
FEATURE [Part::Feature] Heliostat_482  label="Heliostat_482(Mirror,Axis_1_482,Axis_2_482,Normal_482,Target_point)"
  Placement = pos=(-48562.3,-137084,3.16914e-11) rot=(0,0,1;0rad)
  shape: bbox 10000 x 144.2 x 10000 mm, 1 faces, 0 solids (baked)
FEATURE [Part::Line] Normal_482
  AttacherType = Attacher::AttachEngine3D
  X1 = -48562.3
  X2 = -48562.3
  Y1 = 36320.4
  Y2 = 35320.4
  Z1 = 0
  Z2 = 0
FEATURE [Part::Line] Axis_1_482
  AttacherType = Attacher::AttachEngine3D
  X1 = -48562.3
  X2 = -48562.3
  Y1 = 36320.4
  Y2 = 36320.4
  Z1 = 0
  Z2 = -1000
FEATURE [Part::Line] Axis_2_482
  AttacherType = Attacher::AttachEngine3D
  X1 = -48562.3
  X2 = -49562.3
  Y1 = 36320.4
  Y2 = 36320.4
  Z1 = 0
  Z2 = 0
FEATURE [Part::Feature] Heliostat_483  label="Heliostat_483(Mirror,Axis_1_483,Axis_2_483,Normal_483,Target_point)"
  Placement = pos=(22294.9,-159106,5.18342e-11) rot=(0,0,1;0rad)
  shape: bbox 10000 x 87.39 x 10000 mm, 1 faces, 0 solids (baked)
FEATURE [Part::Line] Normal_483
  AttacherType = Attacher::AttachEngine3D
  X1 = 22294.9
  X2 = 22294.9
  Y1 = 126984
  Y2 = 125984
  Z1 = 0
  Z2 = 0
FEATURE [Part::Line] Axis_1_483
  AttacherType = Attacher::AttachEngine3D
  X1 = 22294.9
  X2 = 22294.9
  Y1 = 126984
  Y2 = 126984
  Z1 = 0
  Z2 = -1000
FEATURE [Part::Line] Axis_2_483
  AttacherType = Attacher::AttachEngine3D
  X1 = 22294.9
  X2 = 21294.9
  Y1 = 126984
  Y2 = 126984
  Z1 = 0
  Z2 = 0
FEATURE [Part::Feature] Heliostat_484  label="Heliostat_484(Mirror,Axis_1_484,Axis_2_484,Normal_484,Target_point)"
  Placement = pos=(-22294.9,-159106,5.18342e-11) rot=(0,0,1;0rad)
  shape: bbox 10000 x 87.39 x 10000 mm, 1 faces, 0 solids (baked)
FEATURE [Part::Line] Normal_484
  AttacherType = Attacher::AttachEngine3D
  X1 = -22294.9
  X2 = -22294.9
  Y1 = 126984
  Y2 = 125984
  Z1 = 0
  Z2 = 0
FEATURE [Part::Line] Axis_1_484
  AttacherType = Attacher::AttachEngine3D
  X1 = -22294.9
  X2 = -22294.9
  Y1 = 126984
  Y2 = 126984
  Z1 = 0
  Z2 = -1000
FEATURE [Part::Line] Axis_2_484
  AttacherType = Attacher::AttachEngine3D
  X1 = -22294.9
  X2 = -23294.9
  Y1 = 126984
  Y2 = 126984
  Z1 = 0
  Z2 = 0
FEATURE [Part::Feature] Heliostat_485  label="Heliostat_485(Mirror,Axis_1_485,Axis_2_485,Normal_485,Target_point)"
  Placement = pos=(8.5801e-11,-157163,1.68398e-11) rot=(0,0,1;0rad)
  shape: bbox 10000 x 87.39 x 10000 mm, 1 faces, 0 solids (baked)
FEATURE [Part::Line] Normal_485
  AttacherType = Attacher::AttachEngine3D
  X1 = 0
  X2 = 0
  Y1 = 128926
  Y2 = 127926
  Z1 = 0
  Z2 = 0
FEATURE [Part::Line] Axis_1_485
  AttacherType = Attacher::AttachEngine3D
  X1 = 0
  X2 = 0
  Y1 = 128926
  Y2 = 128926
  Z1 = 0
  Z2 = -1000
FEATURE [Part::Line] Axis_2_485
  AttacherType = Attacher::AttachEngine3D
  X1 = 0
  X2 = -1000
  Y1 = 128926
  Y2 = 128926
  Z1 = 0
  Z2 = 0
FEATURE [Part::Feature] Heliostat_486  label="Heliostat_486(Mirror,Axis_1_486,Axis_2_486,Normal_486,Target_point)"
  Placement = pos=(36438.7,-172114,4.03801e-11) rot=(0,0,1;0rad)
  shape: bbox 10000 x 80.99 x 10000 mm, 1 faces, 0 solids (baked)
FEATURE [Part::Line] Normal_486
  AttacherType = Attacher::AttachEngine3D
  X1 = 36438.7
  X2 = 36438.7
  Y1 = 136591
  Y2 = 135591
  Z1 = 0
  Z2 = 0
FEATURE [Part::Line] Axis_1_486
  AttacherType = Attacher::AttachEngine3D
  X1 = 36438.7
  X2 = 36438.7
  Y1 = 136591
  Y2 = 136591
  Z1 = 0
  Z2 = -1000
FEATURE [Part::Line] Axis_2_486
  AttacherType = Attacher::AttachEngine3D
  X1 = 36438.7
  X2 = 35438.7
  Y1 = 136591
  Y2 = 136591
  Z1 = 0
  Z2 = 0
FEATURE [Part::Feature] Heliostat_487  label="Heliostat_487(Mirror,Axis_1_487,Axis_2_487,Normal_487,Target_point)"
  Placement = pos=(-36438.7,-172114,4.03801e-11) rot=(0,0,1;0rad)
  shape: bbox 10000 x 80.99 x 10000 mm, 1 faces, 0 solids (baked)
FEATURE [Part::Line] Normal_487
  AttacherType = Attacher::AttachEngine3D
  X1 = -36438.7
  X2 = -36438.7
  Y1 = 136591
  Y2 = 135591
  Z1 = 0
  Z2 = 0
FEATURE [Part::Line] Axis_1_487
  AttacherType = Attacher::AttachEngine3D
  X1 = -36438.7
  X2 = -36438.7
  Y1 = 136591
  Y2 = 136591
  Z1 = 0
  Z2 = -1000
FEATURE [Part::Line] Axis_2_487
  AttacherType = Attacher::AttachEngine3D
  X1 = -36438.7
  X2 = -37438.7
  Y1 = 136591
  Y2 = 136591
  Z1 = 0
  Z2 = 0
FEATURE [Part::Feature] Heliostat_488  label="Heliostat_488(Mirror,Axis_1_488,Axis_2_488,Normal_488,Target_point)"
  Placement = pos=(58220.3,-154285,6.30899e-11) rot=(0,0,1;0rad)
  shape: bbox 10000 x 105.8 x 10000 mm, 1 faces, 0 solids (baked)
FEATURE [Part::Line] Normal_488
  AttacherType = Attacher::AttachEngine3D
  X1 = 58220.3
  X2 = 58220.3
  Y1 = 82092.9
  Y2 = 81092.9
  Z1 = 0
  Z2 = 0
FEATURE [Part::Line] Axis_1_488
  AttacherType = Attacher::AttachEngine3D
  X1 = 58220.3
  X2 = 58220.3
  Y1 = 82092.9
  Y2 = 82092.9
  Z1 = 0
  Z2 = -1000
FEATURE [Part::Line] Axis_2_488
  AttacherType = Attacher::AttachEngine3D
  X1 = 58220.3
  X2 = 57220.3
  Y1 = 82092.9
  Y2 = 82092.9
  Z1 = 0
  Z2 = 0
FEATURE [Part::Feature] Heliostat_489  label="Heliostat_489(Mirror,Axis_1_489,Axis_2_489,Normal_489,Target_point)"
  Placement = pos=(-58220.3,-154285,6.30899e-11) rot=(0,0,1;0rad)
  shape: bbox 10000 x 105.8 x 10000 mm, 1 faces, 0 solids (baked)
FEATURE [Part::Line] Normal_489
  AttacherType = Attacher::AttachEngine3D
  X1 = -58220.3
  X2 = -58220.3
  Y1 = 82092.9
  Y2 = 81092.9
  Z1 = 0
  Z2 = 0
FEATURE [Part::Line] Axis_1_489
  AttacherType = Attacher::AttachEngine3D
  X1 = -58220.3
  X2 = -58220.3
  Y1 = 82092.9
  Y2 = 82092.9
  Z1 = 0
  Z2 = -1000
FEATURE [Part::Line] Axis_2_489
  AttacherType = Attacher::AttachEngine3D
  X1 = -58220.3
  X2 = -59220.3
  Y1 = 82092.9
  Y2 = 82092.9
  Z1 = 0
  Z2 = 0
FEATURE [Part::Feature] Heliostat_490  label="Heliostat_490(Mirror,Axis_1_490,Axis_2_490,Normal_490,Target_point)"
  Placement = pos=(36582,-126241,1.83e-12) rot=(0,0,1;0rad)
  shape: bbox 10010 x 161.4 x 10000 mm, 1 faces, 0 solids (baked)
FEATURE [Part::Line] Normal_490
  AttacherType = Attacher::AttachEngine3D
  X1 = 36582
  X2 = 36582
  Y1 = 28705.6
  Y2 = 27705.6
  Z1 = 0
  Z2 = 0
FEATURE [Part::Line] Axis_1_490
  AttacherType = Attacher::AttachEngine3D
  X1 = 36582
  X2 = 36582
  Y1 = 28705.6
  Y2 = 28705.6
  Z1 = 0
  Z2 = -1000
FEATURE [Part::Line] Axis_2_490
  AttacherType = Attacher::AttachEngine3D
  X1 = 36582
  X2 = 35582
  Y1 = 28705.6
  Y2 = 28705.6
  Z1 = 0
  Z2 = 0
FEATURE [Part::Feature] Heliostat_491  label="Heliostat_491(Mirror,Axis_1_491,Axis_2_491,Normal_491,Target_point)"
  Placement = pos=(-36582,-126241,1.83e-12) rot=(0,0,1;0rad)
  shape: bbox 10010 x 161.4 x 10000 mm, 1 faces, 0 solids (baked)
FEATURE [Part::Line] Normal_491
  AttacherType = Attacher::AttachEngine3D
  X1 = -36582
  X2 = -36582
  Y1 = 28705.6
  Y2 = 27705.6
  Z1 = 0
  Z2 = 0
FEATURE [Part::Line] Axis_1_491
  AttacherType = Attacher::AttachEngine3D
  X1 = -36582
  X2 = -36582
  Y1 = 28705.6
  Y2 = 28705.6
  Z1 = 0
  Z2 = -1000
FEATURE [Part::Line] Axis_2_491
  AttacherType = Attacher::AttachEngine3D
  X1 = -36582
  X2 = -37582
  Y1 = 28705.6
  Y2 = 28705.6
  Z1 = 0
  Z2 = 0
FEATURE [Part::Feature] Heliostat_492  label="Heliostat_492(Mirror,Axis_1_492,Axis_2_492,Normal_492,Target_point)"
  Placement = pos=(42938.1,-139771,4.06801e-11) rot=(0,0,1;0rad)
  shape: bbox 10000 x 113.9 x 10000 mm, 1 faces, 0 solids (baked)
FEATURE [Part::Line] Normal_492
  AttacherType = Attacher::AttachEngine3D
  X1 = 42938.1
  X2 = 42938.1
  Y1 = 79826.8
  Y2 = 78826.8
  Z1 = 0
  Z2 = 0
FEATURE [Part::Line] Axis_1_492
  AttacherType = Attacher::AttachEngine3D
  X1 = 42938.1
  X2 = 42938.1
  Y1 = 79826.8
  Y2 = 79826.8
  Z1 = 0
  Z2 = -1000
FEATURE [Part::Line] Axis_2_492
  AttacherType = Attacher::AttachEngine3D
  X1 = 42938.1
  X2 = 41938.1
  Y1 = 79826.8
  Y2 = 79826.8
  Z1 = 0
  Z2 = 0
FEATURE [Part::Feature] Heliostat_493  label="Heliostat_493(Mirror,Axis_1_493,Axis_2_493,Normal_493,Target_point)"
  Placement = pos=(-42938.1,-139771,4.06801e-11) rot=(0,0,1;0rad)
  shape: bbox 10000 x 113.9 x 10000 mm, 1 faces, 0 solids (baked)
FEATURE [Part::Line] Normal_493
  AttacherType = Attacher::AttachEngine3D
  X1 = -42938.1
  X2 = -42938.1
  Y1 = 79826.8
  Y2 = 78826.8
  Z1 = 0
  Z2 = 0
FEATURE [Part::Line] Axis_1_493
  AttacherType = Attacher::AttachEngine3D
  X1 = -42938.1
  X2 = -42938.1
  Y1 = 79826.8
  Y2 = 79826.8
  Z1 = 0
  Z2 = -1000
FEATURE [Part::Line] Axis_2_493
  AttacherType = Attacher::AttachEngine3D
  X1 = -42938.1
  X2 = -43938.1
  Y1 = 79826.8
  Y2 = 79826.8
  Z1 = 0
  Z2 = 0
FEATURE [Part::Feature] Heliostat_494  label="Heliostat_494(Mirror,Axis_1_494,Axis_2_494,Normal_494,Target_point)"
  Placement = pos=(12269.5,-167870,1.09784e-10) rot=(0,0,1;0rad)
  shape: bbox 10000 x 80.99 x 10000 mm, 1 faces, 0 solids (baked)
FEATURE [Part::Line] Normal_494
  AttacherType = Attacher::AttachEngine3D
  X1 = 12269.5
  X2 = 12269.5
  Y1 = 140834
  Y2 = 139834
  Z1 = 0
  Z2 = 0
FEATURE [Part::Line] Axis_1_494
  AttacherType = Attacher::AttachEngine3D
  X1 = 12269.5
  X2 = 12269.5
  Y1 = 140834
  Y2 = 140834
  Z1 = 0
  Z2 = -1000
FEATURE [Part::Line] Axis_2_494
  AttacherType = Attacher::AttachEngine3D
  X1 = 12269.5
  X2 = 11269.5
  Y1 = 140834
  Y2 = 140834
  Z1 = 0
  Z2 = 0
FEATURE [Part::Feature] Heliostat_495  label="Heliostat_495(Mirror,Axis_1_495,Axis_2_495,Normal_495,Target_point)"
  Placement = pos=(-12269.5,-167870,1.09784e-10) rot=(0,0,1;0rad)
  shape: bbox 10000 x 80.99 x 10000 mm, 1 faces, 0 solids (baked)
FEATURE [Part::Line] Normal_495
  AttacherType = Attacher::AttachEngine3D
  X1 = -12269.5
  X2 = -12269.5
  Y1 = 140834
  Y2 = 139834
  Z1 = 0
  Z2 = 0
FEATURE [Part::Line] Axis_1_495
  AttacherType = Attacher::AttachEngine3D
  X1 = -12269.5
  X2 = -12269.5
  Y1 = 140834
  Y2 = 140834
  Z1 = 0
  Z2 = -1000
FEATURE [Part::Line] Axis_2_495
  AttacherType = Attacher::AttachEngine3D
  X1 = -12269.5
  X2 = -13269.5
  Y1 = 140834
  Y2 = 140834
  Z1 = 0
  Z2 = 0
FEATURE [Part::Feature] Heliostat_496  label="Heliostat_496(Mirror,Axis_1_496,Axis_2_496,Normal_496,Target_point)"
  Placement = pos=(22139.6,-131701,2.29336e-11) rot=(0,0,1;0rad)
  shape: bbox 10000 x 113.9 x 10000 mm, 1 faces, 0 solids (baked)
FEATURE [Part::Line] Normal_496
  AttacherType = Attacher::AttachEngine3D
  X1 = 22139.6
  X2 = 22139.6
  Y1 = 87896.7
  Y2 = 86896.7
  Z1 = 0
  Z2 = 0
FEATURE [Part::Line] Axis_1_496
  AttacherType = Attacher::AttachEngine3D
  X1 = 22139.6
  X2 = 22139.6
  Y1 = 87896.7
  Y2 = 87896.7
  Z1 = 0
  Z2 = -1000
FEATURE [Part::Line] Axis_2_496
  AttacherType = Attacher::AttachEngine3D
  X1 = 22139.6
  X2 = 21139.6
  Y1 = 87896.7
  Y2 = 87896.7
  Z1 = 0
  Z2 = 0
FEATURE [Part::Feature] Heliostat_497  label="Heliostat_497(Mirror,Axis_1_497,Axis_2_497,Normal_497,Target_point)"
  Placement = pos=(-22139.6,-131701,2.29336e-11) rot=(0,0,1;0rad)
  shape: bbox 10000 x 113.9 x 10000 mm, 1 faces, 0 solids (baked)
FEATURE [Part::Line] Normal_497
  AttacherType = Attacher::AttachEngine3D
  X1 = -22139.6
  X2 = -22139.6
  Y1 = 87896.7
  Y2 = 86896.7
  Z1 = 0
  Z2 = 0
FEATURE [Part::Line] Axis_1_497
  AttacherType = Attacher::AttachEngine3D
  X1 = -22139.6
  X2 = -22139.6
  Y1 = 87896.7
  Y2 = 87896.7
  Z1 = 0
  Z2 = -1000
FEATURE [Part::Line] Axis_2_497
  AttacherType = Attacher::AttachEngine3D
  X1 = -22139.6
  X2 = -23139.6
  Y1 = 87896.7
  Y2 = 87896.7
  Z1 = 0
  Z2 = 0
FEATURE [Part::Feature] Heliostat_498  label="Heliostat_498(Mirror,Axis_1_498,Axis_2_498,Normal_498,Target_point)"
  Placement = pos=(29586.6,-149979,7.05225e-11) rot=(0,0,1;0rad)
  shape: bbox 10000 x 95.83 x 10000 mm, 1 faces, 0 solids (baked)
FEATURE [Part::Line] Normal_498
  AttacherType = Attacher::AttachEngine3D
  X1 = 29586.6
  X2 = 29586.6
  Y1 = 110906
  Y2 = 109906
  Z1 = 0
  Z2 = 0
FEATURE [Part::Line] Axis_1_498
  AttacherType = Attacher::AttachEngine3D
  X1 = 29586.6
  X2 = 29586.6
  Y1 = 110906
  Y2 = 110906
  Z1 = 0
  Z2 = -1000
FEATURE [Part::Line] Axis_2_498
  AttacherType = Attacher::AttachEngine3D
  X1 = 29586.6
  X2 = 28586.6
  Y1 = 110906
  Y2 = 110906
  Z1 = 0
  Z2 = 0
FEATURE [Part::Feature] Heliostat_499  label="Heliostat_499(Mirror,Axis_1_499,Axis_2_499,Normal_499,Target_point)"
  Placement = pos=(-29586.6,-149979,7.05225e-11) rot=(0,0,1;0rad)
  shape: bbox 10000 x 95.83 x 10000 mm, 1 faces, 0 solids (baked)
FEATURE [Part::Line] Normal_499
  AttacherType = Attacher::AttachEngine3D
  X1 = -29586.6
  X2 = -29586.6
  Y1 = 110906
  Y2 = 109906
  Z1 = 0
  Z2 = 0
FEATURE [Part::Line] Axis_1_499
  AttacherType = Attacher::AttachEngine3D
  X1 = -29586.6
  X2 = -29586.6
  Y1 = 110906
  Y2 = 110906
  Z1 = 0
  Z2 = -1000
FEATURE [Part::Line] Axis_2_499
  AttacherType = Attacher::AttachEngine3D
  X1 = -29586.6
  X2 = -30586.6
  Y1 = 110906
  Y2 = 110906
  Z1 = 0
  Z2 = 0
FEATURE [Part::Feature] Heliostat_500  label="Heliostat_500(Mirror,Axis_1_500,Axis_2_500,Normal_500,Target_point)"
  Placement = pos=(46650.5,-137622,2.00636e-11) rot=(0,0,1;0rad)
  shape: bbox 10000 x 122.9 x 10000 mm, 1 faces, 0 solids (baked)
FEATURE [Part::Line] Normal_500
  AttacherType = Attacher::AttachEngine3D
  X1 = 46650.5
  X2 = 46650.5
  Y1 = 65779
  Y2 = 64779
  Z1 = 0
  Z2 = 0
FEATURE [Part::Line] Axis_1_500
  AttacherType = Attacher::AttachEngine3D
  X1 = 46650.5
  X2 = 46650.5
  Y1 = 65779
  Y2 = 65779
  Z1 = 0
  Z2 = -1000
FEATURE [Part::Line] Axis_2_500
  AttacherType = Attacher::AttachEngine3D
  X1 = 46650.5
  X2 = 45650.5
  Y1 = 65779
  Y2 = 65779
  Z1 = 0
  Z2 = 0
FEATURE [Part::Feature] Heliostat_501  label="Heliostat_501(Mirror,Axis_1_501,Axis_2_501,Normal_501,Target_point)"
  Placement = pos=(-46650.5,-137622,2.00636e-11) rot=(0,0,1;0rad)
  shape: bbox 10000 x 122.9 x 10000 mm, 1 faces, 0 solids (baked)
FEATURE [Part::Line] Normal_501
  AttacherType = Attacher::AttachEngine3D
  X1 = -46650.5
  X2 = -46650.5
  Y1 = 65779
  Y2 = 64779
  Z1 = 0
  Z2 = 0
FEATURE [Part::Line] Axis_1_501
  AttacherType = Attacher::AttachEngine3D
  X1 = -46650.5
  X2 = -46650.5
  Y1 = 65779
  Y2 = 65779
  Z1 = 0
  Z2 = -1000
FEATURE [Part::Line] Axis_2_501
  AttacherType = Attacher::AttachEngine3D
  X1 = -46650.5
  X2 = -47650.5
  Y1 = 65779
  Y2 = 65779
  Z1 = 0
  Z2 = 0
FEATURE [Part::Feature] Heliostat_502  label="Heliostat_502(Mirror,Axis_1_502,Axis_2_502,Normal_502,Target_point)"
  Placement = pos=(36405.4,-142551,4.3105e-11) rot=(0,0,1;0rad)
  shape: bbox 10000 x 105.8 x 10000 mm, 1 faces, 0 solids (baked)
FEATURE [Part::Line] Normal_502
  AttacherType = Attacher::AttachEngine3D
  X1 = 36405.4
  X2 = 36405.4
  Y1 = 93826.9
  Y2 = 92826.9
  Z1 = 0
  Z2 = 0
FEATURE [Part::Line] Axis_1_502
  AttacherType = Attacher::AttachEngine3D
  X1 = 36405.4
  X2 = 36405.4
  Y1 = 93826.9
  Y2 = 93826.9
  Z1 = 0
  Z2 = -1000
FEATURE [Part::Line] Axis_2_502
  AttacherType = Attacher::AttachEngine3D
  X1 = 36405.4
  X2 = 35405.4
  Y1 = 93826.9
  Y2 = 93826.9
  Z1 = 0
  Z2 = 0
FEATURE [Part::Feature] Heliostat_503  label="Heliostat_503(Mirror,Axis_1_503,Axis_2_503,Normal_503,Target_point)"
  Placement = pos=(-36405.4,-142551,4.3105e-11) rot=(0,0,1;0rad)
  shape: bbox 10000 x 105.8 x 10000 mm, 1 faces, 0 solids (baked)
FEATURE [Part::Line] Normal_503
  AttacherType = Attacher::AttachEngine3D
  X1 = -36405.4
  X2 = -36405.4
  Y1 = 93826.9
  Y2 = 92826.9
  Z1 = 0
  Z2 = 0
FEATURE [Part::Line] Axis_1_503
  AttacherType = Attacher::AttachEngine3D
  X1 = -36405.4
  X2 = -36405.4
  Y1 = 93826.9
  Y2 = 93826.9
  Z1 = 0
  Z2 = -1000
FEATURE [Part::Line] Axis_2_503
  AttacherType = Attacher::AttachEngine3D
  X1 = -36405.4
  X2 = -37405.4
  Y1 = 93826.9
  Y2 = 93826.9
  Z1 = 0
  Z2 = 0
FEATURE [Part::Feature] Heliostat_504  label="Heliostat_504(Mirror,Axis_1_504,Axis_2_504,Normal_504,Target_point)"
  Placement = pos=(2.65186e-10,-128956,5.74625e-11) rot=(0,0,1;0rad)
  shape: bbox 10000 x 113.9 x 10000 mm, 1 faces, 0 solids (baked)
FEATURE [Part::Line] Normal_504
  AttacherType = Attacher::AttachEngine3D
  X1 = 0
  X2 = 0
  Y1 = 90642.1
  Y2 = 89642.1
  Z1 = 0
  Z2 = 0
FEATURE [Part::Line] Axis_1_504
  AttacherType = Attacher::AttachEngine3D
  X1 = 0
  X2 = 0
  Y1 = 90642.1
  Y2 = 90642.1
  Z1 = 0
  Z2 = -1000
FEATURE [Part::Line] Axis_2_504
  AttacherType = Attacher::AttachEngine3D
  X1 = 0
  X2 = -1000
  Y1 = 90642.1
  Y2 = 90642.1
  Z1 = 0
  Z2 = 0
FEATURE [Part::Feature] Heliostat_505  label="Heliostat_505(Mirror,Axis_1_505,Axis_2_505,Normal_505,Target_point)"
  Placement = pos=(38903,-126886,4.56517e-11) rot=(0,0,1;0rad)
  shape: bbox 10000 x 144.2 x 10000 mm, 1 faces, 0 solids (baked)
FEATURE [Part::Line] Normal_505
  AttacherType = Attacher::AttachEngine3D
  X1 = 38903
  X2 = 38903
  Y1 = 46519.1
  Y2 = 45519.1
  Z1 = 0
  Z2 = 0
FEATURE [Part::Line] Axis_1_505
  AttacherType = Attacher::AttachEngine3D
  X1 = 38903
  X2 = 38903
  Y1 = 46519.1
  Y2 = 46519.1
  Z1 = 0
  Z2 = -1000
FEATURE [Part::Line] Axis_2_505
  AttacherType = Attacher::AttachEngine3D
  X1 = 38903
  X2 = 37903
  Y1 = 46519.1
  Y2 = 46519.1
  Z1 = 0
  Z2 = 0
FEATURE [Part::Feature] Heliostat_506  label="Heliostat_506(Mirror,Axis_1_506,Axis_2_506,Normal_506,Target_point)"
  Placement = pos=(-38903,-126886,4.56517e-11) rot=(0,0,1;0rad)
  shape: bbox 10000 x 144.2 x 10000 mm, 1 faces, 0 solids (baked)
FEATURE [Part::Line] Normal_506
  AttacherType = Attacher::AttachEngine3D
  X1 = -38903
  X2 = -38903
  Y1 = 46519.1
  Y2 = 45519.1
  Z1 = 0
  Z2 = 0
FEATURE [Part::Line] Axis_1_506
  AttacherType = Attacher::AttachEngine3D
  X1 = -38903
  X2 = -38903
  Y1 = 46519.1
  Y2 = 46519.1
  Z1 = 0
  Z2 = -1000
FEATURE [Part::Line] Axis_2_506
  AttacherType = Attacher::AttachEngine3D
  X1 = -38903
  X2 = -39903
  Y1 = 46519.1
  Y2 = 46519.1
  Z1 = 0
  Z2 = 0
FEATURE [Part::Feature] Heliostat_507  label="Heliostat_507(Mirror,Axis_1_507,Axis_2_507,Normal_507,Target_point)"
  Placement = pos=(12385.2,-136501,-4.87e-14) rot=(0,0,1;0rad)
  shape: bbox 10000 x 105.8 x 10000 mm, 1 faces, 0 solids (baked)
FEATURE [Part::Line] Normal_507
  AttacherType = Attacher::AttachEngine3D
  X1 = 12385.2
  X2 = 12385.2
  Y1 = 99877.2
  Y2 = 98877.2
  Z1 = 0
  Z2 = 0
FEATURE [Part::Line] Axis_1_507
  AttacherType = Attacher::AttachEngine3D
  X1 = 12385.2
  X2 = 12385.2
  Y1 = 99877.2
  Y2 = 99877.2
  Z1 = 0
  Z2 = -1000
FEATURE [Part::Line] Axis_2_507
  AttacherType = Attacher::AttachEngine3D
  X1 = 12385.2
  X2 = 11385.2
  Y1 = 99877.2
  Y2 = 99877.2
  Z1 = 0
  Z2 = 0
FEATURE [Part::Feature] Heliostat_508  label="Heliostat_508(Mirror,Axis_1_508,Axis_2_508,Normal_508,Target_point)"
  Placement = pos=(-12385.2,-136501,-4.87e-14) rot=(0,0,1;0rad)
  shape: bbox 10000 x 105.8 x 10000 mm, 1 faces, 0 solids (baked)
FEATURE [Part::Line] Normal_508
  AttacherType = Attacher::AttachEngine3D
  X1 = -12385.2
  X2 = -12385.2
  Y1 = 99877.2
  Y2 = 98877.2
  Z1 = 0
  Z2 = 0
FEATURE [Part::Line] Axis_1_508
  AttacherType = Attacher::AttachEngine3D
  X1 = -12385.2
  X2 = -12385.2
  Y1 = 99877.2
  Y2 = 99877.2
  Z1 = 0
  Z2 = -1000
FEATURE [Part::Line] Axis_2_508
  AttacherType = Attacher::AttachEngine3D
  X1 = -12385.2
  X2 = -13385.2
  Y1 = 99877.2
  Y2 = 99877.2
  Z1 = 0
  Z2 = 0
FEATURE [Part::Feature] Heliostat_509  label="Heliostat_509(Mirror,Axis_1_509,Axis_2_509,Normal_509,Target_point)"
  Placement = pos=(29170.8,-128220,3.72505e-11) rot=(0,0,1;0rad)
  shape: bbox 10000 x 122.9 x 10000 mm, 1 faces, 0 solids (baked)
FEATURE [Part::Line] Normal_509
  AttacherType = Attacher::AttachEngine3D
  X1 = 29170.8
  X2 = 29170.8
  Y1 = 75181.2
  Y2 = 74181.2
  Z1 = 0
  Z2 = 0
FEATURE [Part::Line] Axis_1_509
  AttacherType = Attacher::AttachEngine3D
  X1 = 29170.8
  X2 = 29170.8
  Y1 = 75181.2
  Y2 = 75181.2
  Z1 = 0
  Z2 = -1000
FEATURE [Part::Line] Axis_2_509
  AttacherType = Attacher::AttachEngine3D
  X1 = 29170.8
  X2 = 28170.8
  Y1 = 75181.2
  Y2 = 75181.2
  Z1 = 0
  Z2 = 0
FEATURE [Part::Feature] Heliostat_510  label="Heliostat_510(Mirror,Axis_1_510,Axis_2_510,Normal_510,Target_point)"
  Placement = pos=(-29170.8,-128220,3.72505e-11) rot=(0,0,1;0rad)
  shape: bbox 10000 x 122.9 x 10000 mm, 1 faces, 0 solids (baked)
FEATURE [Part::Line] Normal_510
  AttacherType = Attacher::AttachEngine3D
  X1 = -29170.8
  X2 = -29170.8
  Y1 = 75181.2
  Y2 = 74181.2
  Z1 = 0
  Z2 = 0
FEATURE [Part::Line] Axis_1_510
  AttacherType = Attacher::AttachEngine3D
  X1 = -29170.8
  X2 = -29170.8
  Y1 = 75181.2
  Y2 = 75181.2
  Z1 = 0
  Z2 = -1000
FEATURE [Part::Line] Axis_2_510
  AttacherType = Attacher::AttachEngine3D
  X1 = -29170.8
  X2 = -30170.8
  Y1 = 75181.2
  Y2 = 75181.2
  Z1 = 0
  Z2 = 0
FEATURE [Part::Feature] Heliostat_511  label="Heliostat_511(Mirror,Axis_1_511,Axis_2_511,Normal_511,Target_point)"
  Placement = pos=(26395.4,-116664,2.84745e-11) rot=(0,0,1;0rad)
  shape: bbox 10010 x 161.4 x 10000 mm, 1 faces, 0 solids (baked)
FEATURE [Part::Line] Normal_511
  AttacherType = Attacher::AttachEngine3D
  X1 = 26395.4
  X2 = 26395.4
  Y1 = 38282.3
  Y2 = 37282.3
  Z1 = 0
  Z2 = 0
FEATURE [Part::Line] Axis_1_511
  AttacherType = Attacher::AttachEngine3D
  X1 = 26395.4
  X2 = 26395.4
  Y1 = 38282.3
  Y2 = 38282.3
  Z1 = 0
  Z2 = -1000
FEATURE [Part::Line] Axis_2_511
  AttacherType = Attacher::AttachEngine3D
  X1 = 26395.4
  X2 = 25395.4
  Y1 = 38282.3
  Y2 = 38282.3
  Z1 = 0
  Z2 = 0
FEATURE [Part::Feature] Heliostat_512  label="Heliostat_512(Mirror,Axis_1_512,Axis_2_512,Normal_512,Target_point)"
  Placement = pos=(-26395.4,-116664,2.84745e-11) rot=(0,0,1;0rad)
  shape: bbox 10010 x 161.4 x 10000 mm, 1 faces, 0 solids (baked)
FEATURE [Part::Line] Normal_512
  AttacherType = Attacher::AttachEngine3D
  X1 = -26395.4
  X2 = -26395.4
  Y1 = 38282.3
  Y2 = 37282.3
  Z1 = 0
  Z2 = 0
FEATURE [Part::Line] Axis_1_512
  AttacherType = Attacher::AttachEngine3D
  X1 = -26395.4
  X2 = -26395.4
  Y1 = 38282.3
  Y2 = 38282.3
  Z1 = 0
  Z2 = -1000
FEATURE [Part::Line] Axis_2_512
  AttacherType = Attacher::AttachEngine3D
  X1 = -26395.4
  X2 = -27395.4
  Y1 = 38282.3
  Y2 = 38282.3
  Z1 = 0
  Z2 = 0
FEATURE [Part::Feature] Heliostat_513  label="Heliostat_513(Mirror,Axis_1_513,Axis_2_513,Normal_513,Target_point)"
  Placement = pos=(9923.99,-123372,3.72728e-11) rot=(0,0,1;0rad)
  shape: bbox 10000 x 122.9 x 10000 mm, 1 faces, 0 solids (baked)
FEATURE [Part::Line] Normal_513
  AttacherType = Attacher::AttachEngine3D
  X1 = 9923.99
  X2 = 9923.99
  Y1 = 80029.2
  Y2 = 79029.2
  Z1 = 0
  Z2 = 0
FEATURE [Part::Line] Axis_1_513
  AttacherType = Attacher::AttachEngine3D
  X1 = 9923.99
  X2 = 9923.99
  Y1 = 80029.2
  Y2 = 80029.2
  Z1 = 0
  Z2 = -1000
FEATURE [Part::Line] Axis_2_513
  AttacherType = Attacher::AttachEngine3D
  X1 = 9923.99
  X2 = 8923.99
  Y1 = 80029.2
  Y2 = 80029.2
  Z1 = 0
  Z2 = 0
FEATURE [Part::Feature] Heliostat_514  label="Heliostat_514(Mirror,Axis_1_514,Axis_2_514,Normal_514,Target_point)"
  Placement = pos=(-9923.99,-123372,3.72728e-11) rot=(0,0,1;0rad)
  shape: bbox 10000 x 122.9 x 10000 mm, 1 faces, 0 solids (baked)
FEATURE [Part::Line] Normal_514
  AttacherType = Attacher::AttachEngine3D
  X1 = -9923.99
  X2 = -9923.99
  Y1 = 80029.2
  Y2 = 79029.2
  Z1 = 0
  Z2 = 0
FEATURE [Part::Line] Axis_1_514
  AttacherType = Attacher::AttachEngine3D
  X1 = -9923.99
  X2 = -9923.99
  Y1 = 80029.2
  Y2 = 80029.2
  Z1 = 0
  Z2 = -1000
FEATURE [Part::Line] Axis_2_514
  AttacherType = Attacher::AttachEngine3D
  X1 = -9923.99
  X2 = -10924
  Y1 = 80029.2
  Y2 = 80029.2
  Z1 = 0
  Z2 = 0
FEATURE [Part::Feature] Heliostat_515  label="Heliostat_515(Mirror,Axis_1_515,Axis_2_515,Normal_515,Target_point)"
  Placement = pos=(27156.2,-119183,3.21711e-11) rot=(0,0,1;0rad)
  shape: bbox 10000 x 144.2 x 10000 mm, 1 faces, 0 solids (baked)
FEATURE [Part::Line] Normal_515
  AttacherType = Attacher::AttachEngine3D
  X1 = 27156.2
  X2 = 27156.2
  Y1 = 54221.8
  Y2 = 53221.8
  Z1 = 0
  Z2 = 0
FEATURE [Part::Line] Axis_1_515
  AttacherType = Attacher::AttachEngine3D
  X1 = 27156.2
  X2 = 27156.2
  Y1 = 54221.8
  Y2 = 54221.8
  Z1 = 0
  Z2 = -1000
FEATURE [Part::Line] Axis_2_515
  AttacherType = Attacher::AttachEngine3D
  X1 = 27156.2
  X2 = 26156.2
  Y1 = 54221.8
  Y2 = 54221.8
  Z1 = 0
  Z2 = 0
FEATURE [Part::Feature] Heliostat_516  label="Heliostat_516(Mirror,Axis_1_516,Axis_2_516,Normal_516,Target_point)"
  Placement = pos=(-27156.2,-119183,3.21711e-11) rot=(0,0,1;0rad)
  shape: bbox 10000 x 144.2 x 10000 mm, 1 faces, 0 solids (baked)
FEATURE [Part::Line] Normal_516
  AttacherType = Attacher::AttachEngine3D
  X1 = -27156.2
  X2 = -27156.2
  Y1 = 54221.8
  Y2 = 53221.8
  Z1 = 0
  Z2 = 0
FEATURE [Part::Line] Axis_1_516
  AttacherType = Attacher::AttachEngine3D
  X1 = -27156.2
  X2 = -27156.2
  Y1 = 54221.8
  Y2 = 54221.8
  Z1 = 0
  Z2 = -1000
FEATURE [Part::Line] Axis_2_516
  AttacherType = Attacher::AttachEngine3D
  X1 = -27156.2
  X2 = -28156.2
  Y1 = 54221.8
  Y2 = 54221.8
  Z1 = 0
  Z2 = 0
FEATURE [Part::Feature] Heliostat_517  label="Heliostat_517(Mirror,Axis_1_517,Axis_2_517,Normal_517,Target_point)"
  Placement = pos=(13952.4,-114390,3.14671e-11) rot=(0,0,1;0rad)
  shape: bbox 10000 x 144.2 x 10000 mm, 1 faces, 0 solids (baked)
FEATURE [Part::Line] Normal_517
  AttacherType = Attacher::AttachEngine3D
  X1 = 13952.4
  X2 = 13952.4
  Y1 = 59015.2
  Y2 = 58015.2
  Z1 = 0
  Z2 = 0
FEATURE [Part::Line] Axis_1_517
  AttacherType = Attacher::AttachEngine3D
  X1 = 13952.4
  X2 = 13952.4
  Y1 = 59015.2
  Y2 = 59015.2
  Z1 = 0
  Z2 = -1000
FEATURE [Part::Line] Axis_2_517
  AttacherType = Attacher::AttachEngine3D
  X1 = 13952.4
  X2 = 12952.4
  Y1 = 59015.2
  Y2 = 59015.2
  Z1 = 0
  Z2 = 0
FEATURE [Part::Feature] Heliostat_518  label="Heliostat_518(Mirror,Axis_1_518,Axis_2_518,Normal_518,Target_point)"
  Placement = pos=(-13952.4,-114390,3.14671e-11) rot=(0,0,1;0rad)
  shape: bbox 10000 x 144.2 x 10000 mm, 1 faces, 0 solids (baked)
FEATURE [Part::Line] Normal_518
  AttacherType = Attacher::AttachEngine3D
  X1 = -13952.4
  X2 = -13952.4
  Y1 = 59015.2
  Y2 = 58015.2
  Z1 = 0
  Z2 = 0
FEATURE [Part::Line] Axis_1_518
  AttacherType = Attacher::AttachEngine3D
  X1 = -13952.4
  X2 = -13952.4
  Y1 = 59015.2
  Y2 = 59015.2
  Z1 = 0
  Z2 = -1000
FEATURE [Part::Line] Axis_2_518
  AttacherType = Attacher::AttachEngine3D
  X1 = -13952.4
  X2 = -14952.4
  Y1 = 59015.2
  Y2 = 59015.2
  Z1 = 0
  Z2 = 0
FEATURE [Part::Feature] Heliostat_519  label="Heliostat_519(Mirror,Axis_1_519,Axis_2_519,Normal_519,Target_point)"
  Placement = pos=(2.03472e-10,-112763,6.09531e-11) rot=(0,0,1;0rad)
  shape: bbox 10000 x 144.2 x 10000 mm, 1 faces, 0 solids (baked)
FEATURE [Part::Line] Normal_519
  AttacherType = Attacher::AttachEngine3D
  X1 = 0
  X2 = 0
  Y1 = 60642.1
  Y2 = 59642.1
  Z1 = 0
  Z2 = 0
FEATURE [Part::Line] Axis_1_519
  AttacherType = Attacher::AttachEngine3D
  X1 = 0
  X2 = 0
  Y1 = 60642.1
  Y2 = 60642.1
  Z1 = 0
  Z2 = -1000
FEATURE [Part::Line] Axis_2_519
  AttacherType = Attacher::AttachEngine3D
  X1 = 0
  X2 = -1000
  Y1 = 60642.1
  Y2 = 60642.1
  Z1 = 0
  Z2 = 0
FEATURE [Part::Feature] Heliostat_520  label="Heliostat_520(Mirror,Axis_1_520,Axis_2_520,Normal_520,Target_point)"
  Placement = pos=(13822.5,-110548,2.87359e-11) rot=(0,0,1;0rad)
  shape: bbox 10010 x 161.4 x 10000 mm, 1 faces, 0 solids (baked)
FEATURE [Part::Line] Normal_520
  AttacherType = Attacher::AttachEngine3D
  X1 = 13822.5
  X2 = 13822.5
  Y1 = 44398.1
  Y2 = 43398.1
  Z1 = 0
  Z2 = 0
FEATURE [Part::Line] Axis_1_520
  AttacherType = Attacher::AttachEngine3D
  X1 = 13822.5
  X2 = 13822.5
  Y1 = 44398.1
  Y2 = 44398.1
  Z1 = 0
  Z2 = -1000
FEATURE [Part::Line] Axis_2_520
  AttacherType = Attacher::AttachEngine3D
  X1 = 13822.5
  X2 = 12822.5
  Y1 = 44398.1
  Y2 = 44398.1
  Z1 = 0
  Z2 = 0
FEATURE [Part::Feature] Heliostat_521  label="Heliostat_521(Mirror,Axis_1_521,Axis_2_521,Normal_521,Target_point)"
  Placement = pos=(-13822.5,-110548,2.87359e-11) rot=(0,0,1;0rad)
  shape: bbox 10010 x 161.4 x 10000 mm, 1 faces, 0 solids (baked)
FEATURE [Part::Line] Normal_521
  AttacherType = Attacher::AttachEngine3D
  X1 = -13822.5
  X2 = -13822.5
  Y1 = 44398.1
  Y2 = 43398.1
  Z1 = 0
  Z2 = 0
FEATURE [Part::Line] Axis_1_521
  AttacherType = Attacher::AttachEngine3D
  X1 = -13822.5
  X2 = -13822.5
  Y1 = 44398.1
  Y2 = 44398.1
  Z1 = 0
  Z2 = -1000
FEATURE [Part::Line] Axis_2_521
  AttacherType = Attacher::AttachEngine3D
  X1 = -13822.5
  X2 = -14822.5
  Y1 = 44398.1
  Y2 = 44398.1
  Z1 = 0
  Z2 = 0
FEATURE [Part::Feature] Heliostat_522  label="Heliostat_522(Mirror,Axis_1_522,Axis_2_522,Normal_522,Target_point)"
  Placement = pos=(3.9589e-12,-108446,4.24456e-11) rot=(0,0,1;0rad)
  shape: bbox 10010 x 161.4 x 10000 mm, 1 faces, 0 solids (baked)
FEATURE [Part::Line] Normal_522
  AttacherType = Attacher::AttachEngine3D
  X1 = 0
  X2 = 0
  Y1 = 46500
  Y2 = 45500
  Z1 = 0
  Z2 = 0
FEATURE [Part::Line] Axis_1_522
  AttacherType = Attacher::AttachEngine3D
  X1 = 0
  X2 = 0
  Y1 = 46500
  Y2 = 46500
  Z1 = 0
  Z2 = -1000
FEATURE [Part::Line] Axis_2_522
  AttacherType = Attacher::AttachEngine3D
  X1 = 0
  X2 = -1000
  Y1 = 46500
  Y2 = 46500
  Z1 = 0
  Z2 = 0
FEATURE [Part::Feature] Target_point
  shape: bbox 2e-07 x 2e-07 x 2e-07 mm, 0 faces, 0 solids (baked)
FEATURE [Part::Plane] Receiver  label="Receiver(Abs)"
  AttacherType = Attacher::AttachEngine3D
  Length = 8000
  Placement = pos=(-4000,0,59000) rot=(1,0,0;1.5708rad)
  Width = 6000
FEATURE [Part::Box] Tower  label="Tower(Opaque)"
  AttacherType = Attacher::AttachEngine3D
  Height = 62000
  Length = 8000
  Placement = pos=(-4000,-9600,0) rot=(0,0,1;0rad)
  Width = 6000
